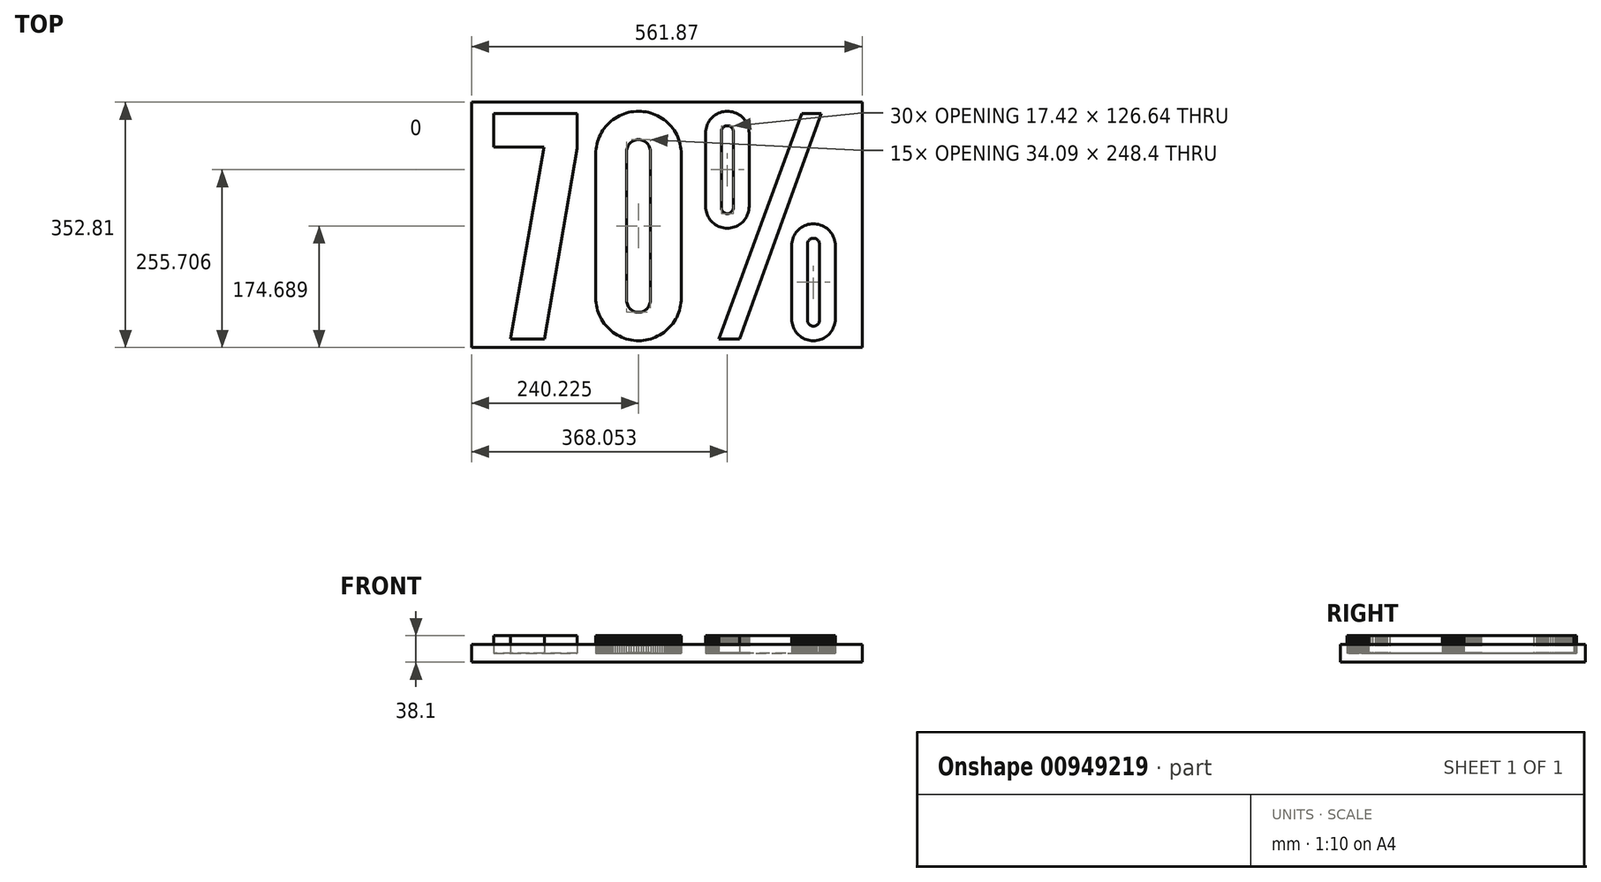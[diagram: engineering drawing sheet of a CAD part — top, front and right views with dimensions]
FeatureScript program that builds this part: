
annotation { "Feature Type Name" : "Feature", "Feature Type Description" : "" }
export const myFeature = defineFeature(function(context is Context, id is Id, definition is map)
    precondition{}
    {
        {
            var Q0;
            Q0=qCreatedBy(makeId("Top.planeOp"),FACE);
            var sketch = newSketch(context, id + "F0", { "sketchPlane" : qUnion([Q0])});
            skLineSegment(sketch, "E0", {"start": v(-116.2, -328.45) * mm, "end": v(-116.2, -376.5) * mm});
            skLineSegment(sketch, "E1", {"start": v(-116.2, -376.5) * mm, "end": v(-116.2, -377.7) * mm});
            skLineSegment(sketch, "E2", {"start": v(-116.2, -377.7) * mm, "end": v(-115.97, -378.89) * mm});
            skLineSegment(sketch, "E3", {"start": v(-115.97, -378.89) * mm, "end": v(-115.65, -379.97) * mm});
            skLineSegment(sketch, "E4", {"start": v(-115.65, -379.97) * mm, "end": v(-115.22, -381.05) * mm});
            skLineSegment(sketch, "E5", {"start": v(-115.22, -381.05) * mm, "end": v(-114.78, -382.02) * mm});
            skLineSegment(sketch, "E6", {"start": v(-114.78, -382.02) * mm, "end": v(-114.14, -383) * mm});
            skLineSegment(sketch, "E7", {"start": v(-114.14, -383) * mm, "end": v(-113.38, -383.86) * mm});
            skLineSegment(sketch, "E8", {"start": v(-113.38, -383.86) * mm, "end": v(-112.62, -384.73) * mm});
            skLineSegment(sketch, "E9", {"start": v(-112.62, -384.73) * mm, "end": v(-111.65, -385.49) * mm});
            skLineSegment(sketch, "E10", {"start": v(-111.65, -385.49) * mm, "end": v(-110.78, -386.03) * mm});
            skLineSegment(sketch, "E11", {"start": v(-110.78, -386.03) * mm, "end": v(-109.7, -386.57) * mm});
            skLineSegment(sketch, "E12", {"start": v(-109.7, -386.57) * mm, "end": v(-108.61, -387) * mm});
            skLineSegment(sketch, "E13", {"start": v(-108.61, -387) * mm, "end": v(-107.53, -387.33) * mm});
            skLineSegment(sketch, "E14", {"start": v(-107.53, -387.33) * mm, "end": v(-106.34, -387.44) * mm});
            skLineSegment(sketch, "E15", {"start": v(-106.34, -387.44) * mm, "end": v(-105.26, -387.54) * mm});
            skLineSegment(sketch, "E16", {"start": v(-105.26, -387.54) * mm, "end": v(-104.07, -387.44) * mm});
            skLineSegment(sketch, "E17", {"start": v(-104.07, -387.44) * mm, "end": v(-102.99, -387.33) * mm});
            skLineSegment(sketch, "E18", {"start": v(-102.99, -387.33) * mm, "end": v(-101.8, -387) * mm});
            skLineSegment(sketch, "E19", {"start": v(-101.8, -387) * mm, "end": v(-100.82, -386.57) * mm});
            skLineSegment(sketch, "E20", {"start": v(-100.82, -386.57) * mm, "end": v(-99.74, -386.03) * mm});
            skLineSegment(sketch, "E21", {"start": v(-99.74, -386.03) * mm, "end": v(-98.76, -385.49) * mm});
            skLineSegment(sketch, "E22", {"start": v(-98.76, -385.49) * mm, "end": v(-97.9, -384.73) * mm});
            skLineSegment(sketch, "E23", {"start": v(-97.9, -384.73) * mm, "end": v(-97.03, -383.86) * mm});
            skLineSegment(sketch, "E24", {"start": v(-97.03, -383.86) * mm, "end": v(-96.38, -383) * mm});
            skLineSegment(sketch, "E25", {"start": v(-96.38, -383) * mm, "end": v(-95.73, -382.02) * mm});
            skLineSegment(sketch, "E26", {"start": v(-95.73, -382.02) * mm, "end": v(-95.2, -381.05) * mm});
            skLineSegment(sketch, "E27", {"start": v(-95.2, -381.05) * mm, "end": v(-94.76, -379.97) * mm});
            skLineSegment(sketch, "E28", {"start": v(-94.76, -379.97) * mm, "end": v(-94.54, -378.89) * mm});
            skLineSegment(sketch, "E29", {"start": v(-94.54, -378.89) * mm, "end": v(-94.33, -377.7) * mm});
            skLineSegment(sketch, "E30", {"start": v(-94.33, -377.7) * mm, "end": v(-94.22, -376.5) * mm});
            skLineSegment(sketch, "E31", {"start": v(-94.22, -376.5) * mm, "end": v(-94.22, -328.45) * mm});
            skLineSegment(sketch, "E32", {"start": v(-94.22, -328.45) * mm, "end": v(-102.23, -328.45) * mm});
            skLineSegment(sketch, "E33", {"start": v(-102.23, -328.45) * mm, "end": v(-102.23, -377.15) * mm});
            skLineSegment(sketch, "E34", {"start": v(-108.3, -377.15) * mm, "end": v(-108.18, -377.8) * mm});
            skLineSegment(sketch, "E35", {"start": v(-108.18, -377.8) * mm, "end": v(-108.08, -378.34) * mm});
            skLineSegment(sketch, "E36", {"start": v(-108.08, -378.34) * mm, "end": v(-107.75, -378.89) * mm});
            skLineSegment(sketch, "E37", {"start": v(-107.75, -378.89) * mm, "end": v(-107.43, -379.32) * mm});
            skLineSegment(sketch, "E38", {"start": v(-107.43, -379.32) * mm, "end": v(-106.88, -379.75) * mm});
            skLineSegment(sketch, "E39", {"start": v(-106.88, -379.75) * mm, "end": v(-106.45, -379.97) * mm});
            skLineSegment(sketch, "E40", {"start": v(-106.45, -379.97) * mm, "end": v(-105.8, -380.18) * mm});
            skLineSegment(sketch, "E41", {"start": v(-105.8, -380.18) * mm, "end": v(-104.61, -380.18) * mm});
            skLineSegment(sketch, "E42", {"start": v(-104.61, -380.18) * mm, "end": v(-104.07, -379.97) * mm});
            skLineSegment(sketch, "E43", {"start": v(-104.07, -379.97) * mm, "end": v(-103.53, -379.75) * mm});
            skLineSegment(sketch, "E44", {"start": v(-103.53, -379.75) * mm, "end": v(-103.1, -379.32) * mm});
            skLineSegment(sketch, "E45", {"start": v(-103.1, -379.32) * mm, "end": v(-102.66, -378.89) * mm});
            skLineSegment(sketch, "E46", {"start": v(-102.66, -378.89) * mm, "end": v(-102.23, -377.8) * mm});
            skLineSegment(sketch, "E47", {"start": v(-102.23, -377.8) * mm, "end": v(-102.23, -377.15) * mm});
            skLineSegment(sketch, "E48", {"start": v(-108.3, -377.15) * mm, "end": v(-108.3, -328.45) * mm});
            skLineSegment(sketch, "E49", {"start": v(-108.3, -328.45) * mm, "end": v(-116.2, -328.45) * mm});
            skLineSegment(sketch, "E50", {"start": v(9.9, -341.44) * mm, "end": v(9.9, -375.1) * mm});
            skLineSegment(sketch, "E51", {"start": v(3.95, -380.3) * mm, "end": v(4.82, -380.18) * mm});
            skLineSegment(sketch, "E52", {"start": v(4.82, -380.18) * mm, "end": v(5.8, -379.97) * mm});
            skLineSegment(sketch, "E53", {"start": v(5.8, -379.97) * mm, "end": v(6.66, -379.54) * mm});
            skLineSegment(sketch, "E54", {"start": v(6.66, -379.54) * mm, "end": v(7.42, -379) * mm});
            skLineSegment(sketch, "E55", {"start": v(7.42, -379) * mm, "end": v(8.17, -378.45) * mm});
            skLineSegment(sketch, "E56", {"start": v(8.17, -378.45) * mm, "end": v(8.82, -377.7) * mm});
            skLineSegment(sketch, "E57", {"start": v(8.82, -377.7) * mm, "end": v(9.25, -376.94) * mm});
            skLineSegment(sketch, "E58", {"start": v(9.25, -376.94) * mm, "end": v(9.69, -376.07) * mm});
            skLineSegment(sketch, "E59", {"start": v(9.69, -376.07) * mm, "end": v(9.9, -375.1) * mm});
            skLineSegment(sketch, "E60", {"start": v(3.95, -380.3) * mm, "end": v(3.2, -380.3) * mm});
            skLineSegment(sketch, "E61", {"start": v(3.2, -380.3) * mm, "end": v(3.2, -336.24) * mm});
            skLineSegment(sketch, "E62", {"start": v(3.2, -336.24) * mm, "end": v(3.95, -336.24) * mm});
            skLineSegment(sketch, "E63", {"start": v(9.9, -341.44) * mm, "end": v(9.69, -340.46) * mm});
            skLineSegment(sketch, "E64", {"start": v(9.69, -340.46) * mm, "end": v(9.25, -339.6) * mm});
            skLineSegment(sketch, "E65", {"start": v(9.25, -339.6) * mm, "end": v(8.82, -338.84) * mm});
            skLineSegment(sketch, "E66", {"start": v(8.82, -338.84) * mm, "end": v(8.17, -338.08) * mm});
            skLineSegment(sketch, "E67", {"start": v(8.17, -338.08) * mm, "end": v(7.42, -337.43) * mm});
            skLineSegment(sketch, "E68", {"start": v(7.42, -337.43) * mm, "end": v(6.66, -337) * mm});
            skLineSegment(sketch, "E69", {"start": v(6.66, -337) * mm, "end": v(5.8, -336.56) * mm});
            skLineSegment(sketch, "E70", {"start": v(5.8, -336.56) * mm, "end": v(4.82, -336.35) * mm});
            skLineSegment(sketch, "E71", {"start": v(4.82, -336.35) * mm, "end": v(3.95, -336.24) * mm});
            skLineSegment(sketch, "E72", {"start": v(-5.36, -328.45) * mm, "end": v(-5.36, -387.98) * mm});
            skLineSegment(sketch, "E73", {"start": v(-5.36, -387.98) * mm, "end": v(8.6, -387.98) * mm});
            skLineSegment(sketch, "E74", {"start": v(8.6, -387.98) * mm, "end": v(9.9, -387.44) * mm});
            skLineSegment(sketch, "E75", {"start": v(9.9, -387.44) * mm, "end": v(11.2, -386.79) * mm});
            skLineSegment(sketch, "E76", {"start": v(11.2, -386.79) * mm, "end": v(12.4, -386.03) * mm});
            skLineSegment(sketch, "E77", {"start": v(12.4, -386.03) * mm, "end": v(13.48, -385.16) * mm});
            skLineSegment(sketch, "E78", {"start": v(13.48, -385.16) * mm, "end": v(14.45, -384.19) * mm});
            skLineSegment(sketch, "E79", {"start": v(14.45, -384.19) * mm, "end": v(15.42, -383.1) * mm});
            skLineSegment(sketch, "E80", {"start": v(15.42, -383.1) * mm, "end": v(16.3, -382.02) * mm});
            skLineSegment(sketch, "E81", {"start": v(16.3, -382.02) * mm, "end": v(16.94, -380.73) * mm});
            skLineSegment(sketch, "E82", {"start": v(16.94, -380.73) * mm, "end": v(17.59, -379.54) * mm});
            skLineSegment(sketch, "E83", {"start": v(17.59, -379.54) * mm, "end": v(18.13, -378.13) * mm});
            skLineSegment(sketch, "E84", {"start": v(18.13, -378.13) * mm, "end": v(18.46, -376.83) * mm});
            skLineSegment(sketch, "E85", {"start": v(18.46, -376.83) * mm, "end": v(18.46, -339.7) * mm});
            skLineSegment(sketch, "E86", {"start": v(18.46, -339.7) * mm, "end": v(18.13, -338.3) * mm});
            skLineSegment(sketch, "E87", {"start": v(18.13, -338.3) * mm, "end": v(17.59, -337) * mm});
            skLineSegment(sketch, "E88", {"start": v(17.59, -337) * mm, "end": v(16.94, -335.7) * mm});
            skLineSegment(sketch, "E89", {"start": v(16.94, -335.7) * mm, "end": v(16.3, -334.5) * mm});
            skLineSegment(sketch, "E90", {"start": v(16.3, -334.5) * mm, "end": v(15.42, -333.43) * mm});
            skLineSegment(sketch, "E91", {"start": v(15.42, -333.43) * mm, "end": v(14.45, -332.34) * mm});
            skLineSegment(sketch, "E92", {"start": v(14.45, -332.34) * mm, "end": v(13.48, -331.37) * mm});
            skLineSegment(sketch, "E93", {"start": v(13.48, -331.37) * mm, "end": v(12.4, -330.5) * mm});
            skLineSegment(sketch, "E94", {"start": v(12.4, -330.5) * mm, "end": v(11.2, -329.75) * mm});
            skLineSegment(sketch, "E95", {"start": v(11.2, -329.75) * mm, "end": v(9.9, -329.1) * mm});
            skLineSegment(sketch, "E96", {"start": v(9.9, -329.1) * mm, "end": v(8.6, -328.45) * mm});
            skLineSegment(sketch, "E97", {"start": v(8.6, -328.45) * mm, "end": v(-5.36, -328.45) * mm});
            skLineSegment(sketch, "E98", {"start": v(-135.57, -338.84) * mm, "end": v(-135.57, -377.15) * mm});
            skLineSegment(sketch, "E99", {"start": v(-141.63, -377.15) * mm, "end": v(-141.63, -377.8) * mm});
            skLineSegment(sketch, "E100", {"start": v(-141.63, -377.8) * mm, "end": v(-141.41, -378.34) * mm});
            skLineSegment(sketch, "E101", {"start": v(-141.41, -378.34) * mm, "end": v(-141.09, -378.89) * mm});
            skLineSegment(sketch, "E102", {"start": v(-141.09, -378.89) * mm, "end": v(-140.76, -379.32) * mm});
            skLineSegment(sketch, "E103", {"start": v(-140.76, -379.32) * mm, "end": v(-140.33, -379.75) * mm});
            skLineSegment(sketch, "E104", {"start": v(-140.33, -379.75) * mm, "end": v(-139.79, -379.97) * mm});
            skLineSegment(sketch, "E105", {"start": v(-139.79, -379.97) * mm, "end": v(-139.14, -380.18) * mm});
            skLineSegment(sketch, "E106", {"start": v(-139.14, -380.18) * mm, "end": v(-137.95, -380.18) * mm});
            skLineSegment(sketch, "E107", {"start": v(-137.95, -380.18) * mm, "end": v(-136.86, -379.75) * mm});
            skLineSegment(sketch, "E108", {"start": v(-136.86, -379.75) * mm, "end": v(-136, -378.89) * mm});
            skLineSegment(sketch, "E109", {"start": v(-136, -378.89) * mm, "end": v(-135.57, -377.8) * mm});
            skLineSegment(sketch, "E110", {"start": v(-135.57, -377.8) * mm, "end": v(-135.57, -377.15) * mm});
            skLineSegment(sketch, "E111", {"start": v(-141.63, -377.15) * mm, "end": v(-141.63, -338.84) * mm});
            skLineSegment(sketch, "E112", {"start": v(-135.57, -338.84) * mm, "end": v(-135.57, -338.3) * mm});
            skLineSegment(sketch, "E113", {"start": v(-135.57, -338.3) * mm, "end": v(-135.78, -337.65) * mm});
            skLineSegment(sketch, "E114", {"start": v(-135.78, -337.65) * mm, "end": v(-136, -337.21) * mm});
            skLineSegment(sketch, "E115", {"start": v(-136, -337.21) * mm, "end": v(-136.43, -336.67) * mm});
            skLineSegment(sketch, "E116", {"start": v(-136.43, -336.67) * mm, "end": v(-136.86, -336.35) * mm});
            skLineSegment(sketch, "E117", {"start": v(-136.86, -336.35) * mm, "end": v(-137.4, -336.02) * mm});
            skLineSegment(sketch, "E118", {"start": v(-137.4, -336.02) * mm, "end": v(-137.95, -335.91) * mm});
            skLineSegment(sketch, "E119", {"start": v(-137.95, -335.91) * mm, "end": v(-138.6, -335.8) * mm});
            skLineSegment(sketch, "E120", {"start": v(-138.6, -335.8) * mm, "end": v(-139.14, -335.91) * mm});
            skLineSegment(sketch, "E121", {"start": v(-139.14, -335.91) * mm, "end": v(-139.79, -336.02) * mm});
            skLineSegment(sketch, "E122", {"start": v(-139.79, -336.02) * mm, "end": v(-140.33, -336.35) * mm});
            skLineSegment(sketch, "E123", {"start": v(-140.33, -336.35) * mm, "end": v(-140.76, -336.67) * mm});
            skLineSegment(sketch, "E124", {"start": v(-140.76, -336.67) * mm, "end": v(-141.09, -337.21) * mm});
            skLineSegment(sketch, "E125", {"start": v(-141.09, -337.21) * mm, "end": v(-141.41, -337.65) * mm});
            skLineSegment(sketch, "E126", {"start": v(-141.41, -337.65) * mm, "end": v(-141.63, -338.3) * mm});
            skLineSegment(sketch, "E127", {"start": v(-141.63, -338.3) * mm, "end": v(-141.63, -338.84) * mm});
            skLineSegment(sketch, "E128", {"start": v(-149.53, -376.5) * mm, "end": v(-149.53, -339.49) * mm});
            skLineSegment(sketch, "E129", {"start": v(-127.55, -339.49) * mm, "end": v(-127.66, -338.3) * mm});
            skLineSegment(sketch, "E130", {"start": v(-127.66, -338.3) * mm, "end": v(-128.1, -336.13) * mm});
            skLineSegment(sketch, "E131", {"start": v(-128.1, -336.13) * mm, "end": v(-128.53, -335.05) * mm});
            skLineSegment(sketch, "E132", {"start": v(-128.53, -335.05) * mm, "end": v(-129.07, -333.97) * mm});
            skLineSegment(sketch, "E133", {"start": v(-129.07, -333.97) * mm, "end": v(-129.72, -333) * mm});
            skLineSegment(sketch, "E134", {"start": v(-129.72, -333) * mm, "end": v(-130.48, -332.13) * mm});
            skLineSegment(sketch, "E135", {"start": v(-130.48, -332.13) * mm, "end": v(-131.24, -331.37) * mm});
            skLineSegment(sketch, "E136", {"start": v(-131.24, -331.37) * mm, "end": v(-132.1, -330.61) * mm});
            skLineSegment(sketch, "E137", {"start": v(-132.1, -330.61) * mm, "end": v(-133.08, -329.96) * mm});
            skLineSegment(sketch, "E138", {"start": v(-133.08, -329.96) * mm, "end": v(-134.16, -329.42) * mm});
            skLineSegment(sketch, "E139", {"start": v(-134.16, -329.42) * mm, "end": v(-135.24, -328.99) * mm});
            skLineSegment(sketch, "E140", {"start": v(-135.24, -328.99) * mm, "end": v(-136.33, -328.77) * mm});
            skLineSegment(sketch, "E141", {"start": v(-136.33, -328.77) * mm, "end": v(-137.4, -328.56) * mm});
            skLineSegment(sketch, "E142", {"start": v(-137.4, -328.56) * mm, "end": v(-138.6, -328.45) * mm});
            skLineSegment(sketch, "E143", {"start": v(-138.6, -328.45) * mm, "end": v(-139.79, -328.56) * mm});
            skLineSegment(sketch, "E144", {"start": v(-139.79, -328.56) * mm, "end": v(-140.87, -328.77) * mm});
            skLineSegment(sketch, "E145", {"start": v(-140.87, -328.77) * mm, "end": v(-141.95, -328.99) * mm});
            skLineSegment(sketch, "E146", {"start": v(-141.95, -328.99) * mm, "end": v(-143.03, -329.42) * mm});
            skLineSegment(sketch, "E147", {"start": v(-143.03, -329.42) * mm, "end": v(-144.12, -329.96) * mm});
            skLineSegment(sketch, "E148", {"start": v(-144.12, -329.96) * mm, "end": v(-145.1, -330.61) * mm});
            skLineSegment(sketch, "E149", {"start": v(-145.1, -330.61) * mm, "end": v(-145.96, -331.37) * mm});
            skLineSegment(sketch, "E150", {"start": v(-145.96, -331.37) * mm, "end": v(-146.71, -332.13) * mm});
            skLineSegment(sketch, "E151", {"start": v(-146.71, -332.13) * mm, "end": v(-147.47, -333) * mm});
            skLineSegment(sketch, "E152", {"start": v(-147.47, -333) * mm, "end": v(-148.12, -333.97) * mm});
            skLineSegment(sketch, "E153", {"start": v(-148.12, -333.97) * mm, "end": v(-148.66, -335.05) * mm});
            skLineSegment(sketch, "E154", {"start": v(-148.66, -335.05) * mm, "end": v(-148.99, -336.13) * mm});
            skLineSegment(sketch, "E155", {"start": v(-148.99, -336.13) * mm, "end": v(-149.31, -337.21) * mm});
            skLineSegment(sketch, "E156", {"start": v(-149.31, -337.21) * mm, "end": v(-149.53, -338.3) * mm});
            skLineSegment(sketch, "E157", {"start": v(-149.53, -338.3) * mm, "end": v(-149.53, -339.49) * mm});
            skLineSegment(sketch, "E158", {"start": v(-127.55, -339.49) * mm, "end": v(-127.55, -376.5) * mm});
            skLineSegment(sketch, "E159", {"start": v(-129.29, -382.35) * mm, "end": v(-128.64, -381.27) * mm});
            skLineSegment(sketch, "E160", {"start": v(-128.64, -381.27) * mm, "end": v(-128.2, -380.08) * mm});
            skLineSegment(sketch, "E161", {"start": v(-128.2, -380.08) * mm, "end": v(-127.88, -379) * mm});
            skLineSegment(sketch, "E162", {"start": v(-127.88, -379) * mm, "end": v(-127.66, -377.8) * mm});
            skLineSegment(sketch, "E163", {"start": v(-127.66, -377.8) * mm, "end": v(-127.55, -376.5) * mm});
            skLineSegment(sketch, "E164", {"start": v(-129.29, -382.35) * mm, "end": v(-128.2, -383.43) * mm});
            skLineSegment(sketch, "E165", {"start": v(-128.2, -383.43) * mm, "end": v(-127.55, -383.97) * mm});
            skLineSegment(sketch, "E166", {"start": v(-127.55, -383.97) * mm, "end": v(-126.8, -384.3) * mm});
            skLineSegment(sketch, "E167", {"start": v(-126.8, -384.3) * mm, "end": v(-126.04, -384.51) * mm});
            skLineSegment(sketch, "E168", {"start": v(-126.04, -384.51) * mm, "end": v(-126.04, -391.55) * mm});
            skLineSegment(sketch, "E169", {"start": v(-134.05, -386.57) * mm, "end": v(-133.4, -387.44) * mm});
            skLineSegment(sketch, "E170", {"start": v(-133.4, -387.44) * mm, "end": v(-132.75, -388.3) * mm});
            skLineSegment(sketch, "E171", {"start": v(-132.75, -388.3) * mm, "end": v(-131.89, -389.06) * mm});
            skLineSegment(sketch, "E172", {"start": v(-131.89, -389.06) * mm, "end": v(-131.13, -389.7) * mm});
            skLineSegment(sketch, "E173", {"start": v(-131.13, -389.7) * mm, "end": v(-130.16, -390.25) * mm});
            skLineSegment(sketch, "E174", {"start": v(-130.16, -390.25) * mm, "end": v(-129.18, -390.8) * mm});
            skLineSegment(sketch, "E175", {"start": v(-129.18, -390.8) * mm, "end": v(-128.2, -391.12) * mm});
            skLineSegment(sketch, "E176", {"start": v(-128.2, -391.12) * mm, "end": v(-127.12, -391.33) * mm});
            skLineSegment(sketch, "E177", {"start": v(-127.12, -391.33) * mm, "end": v(-126.04, -391.55) * mm});
            skLineSegment(sketch, "E178", {"start": v(-149.53, -376.5) * mm, "end": v(-149.53, -377.7) * mm});
            skLineSegment(sketch, "E179", {"start": v(-149.53, -377.7) * mm, "end": v(-149.31, -378.89) * mm});
            skLineSegment(sketch, "E180", {"start": v(-149.31, -378.89) * mm, "end": v(-148.99, -379.97) * mm});
            skLineSegment(sketch, "E181", {"start": v(-148.99, -379.97) * mm, "end": v(-148.66, -381.05) * mm});
            skLineSegment(sketch, "E182", {"start": v(-148.66, -381.05) * mm, "end": v(-148.12, -382.02) * mm});
            skLineSegment(sketch, "E183", {"start": v(-148.12, -382.02) * mm, "end": v(-147.47, -383) * mm});
            skLineSegment(sketch, "E184", {"start": v(-147.47, -383) * mm, "end": v(-146.71, -383.97) * mm});
            skLineSegment(sketch, "E185", {"start": v(-146.71, -383.97) * mm, "end": v(-145.85, -384.73) * mm});
            skLineSegment(sketch, "E186", {"start": v(-145.85, -384.73) * mm, "end": v(-144.98, -385.49) * mm});
            skLineSegment(sketch, "E187", {"start": v(-144.98, -385.49) * mm, "end": v(-144, -386.14) * mm});
            skLineSegment(sketch, "E188", {"start": v(-144, -386.14) * mm, "end": v(-143.03, -386.57) * mm});
            skLineSegment(sketch, "E189", {"start": v(-143.03, -386.57) * mm, "end": v(-141.95, -387) * mm});
            skLineSegment(sketch, "E190", {"start": v(-141.95, -387) * mm, "end": v(-140.76, -387.33) * mm});
            skLineSegment(sketch, "E191", {"start": v(-140.76, -387.33) * mm, "end": v(-139.68, -387.44) * mm});
            skLineSegment(sketch, "E192", {"start": v(-139.68, -387.44) * mm, "end": v(-138.49, -387.54) * mm});
            skLineSegment(sketch, "E193", {"start": v(-138.49, -387.54) * mm, "end": v(-137.3, -387.44) * mm});
            skLineSegment(sketch, "E194", {"start": v(-137.3, -387.44) * mm, "end": v(-136.22, -387.33) * mm});
            skLineSegment(sketch, "E195", {"start": v(-136.22, -387.33) * mm, "end": v(-135.13, -387) * mm});
            skLineSegment(sketch, "E196", {"start": v(-135.13, -387) * mm, "end": v(-134.05, -386.57) * mm});
            skLineSegment(sketch, "E197", {"start": v(-167.06, -338.84) * mm, "end": v(-167.06, -343.7) * mm});
            skLineSegment(sketch, "E198", {"start": v(-167.06, -343.7) * mm, "end": v(-159.16, -343.7) * mm});
            skLineSegment(sketch, "E199", {"start": v(-159.16, -343.7) * mm, "end": v(-159.16, -339.49) * mm});
            skLineSegment(sketch, "E200", {"start": v(-159.16, -339.49) * mm, "end": v(-159.16, -338.3) * mm});
            skLineSegment(sketch, "E201", {"start": v(-159.16, -338.3) * mm, "end": v(-159.38, -337.21) * mm});
            skLineSegment(sketch, "E202", {"start": v(-159.38, -337.21) * mm, "end": v(-159.7, -336.13) * mm});
            skLineSegment(sketch, "E203", {"start": v(-159.7, -336.13) * mm, "end": v(-160.03, -335.05) * mm});
            skLineSegment(sketch, "E204", {"start": v(-160.03, -335.05) * mm, "end": v(-160.57, -333.97) * mm});
            skLineSegment(sketch, "E205", {"start": v(-160.57, -333.97) * mm, "end": v(-161.22, -333) * mm});
            skLineSegment(sketch, "E206", {"start": v(-161.22, -333) * mm, "end": v(-161.97, -332.13) * mm});
            skLineSegment(sketch, "E207", {"start": v(-161.97, -332.13) * mm, "end": v(-162.73, -331.37) * mm});
            skLineSegment(sketch, "E208", {"start": v(-162.73, -331.37) * mm, "end": v(-163.7, -330.61) * mm});
            skLineSegment(sketch, "E209", {"start": v(-163.7, -330.61) * mm, "end": v(-164.58, -329.96) * mm});
            skLineSegment(sketch, "E210", {"start": v(-164.58, -329.96) * mm, "end": v(-165.65, -329.42) * mm});
            skLineSegment(sketch, "E211", {"start": v(-165.65, -329.42) * mm, "end": v(-166.74, -328.99) * mm});
            skLineSegment(sketch, "E212", {"start": v(-166.74, -328.99) * mm, "end": v(-167.82, -328.77) * mm});
            skLineSegment(sketch, "E213", {"start": v(-167.82, -328.77) * mm, "end": v(-169.01, -328.56) * mm});
            skLineSegment(sketch, "E214", {"start": v(-169.01, -328.56) * mm, "end": v(-170.1, -328.45) * mm});
            skLineSegment(sketch, "E215", {"start": v(-170.1, -328.45) * mm, "end": v(-171.28, -328.56) * mm});
            skLineSegment(sketch, "E216", {"start": v(-171.28, -328.56) * mm, "end": v(-172.37, -328.77) * mm});
            skLineSegment(sketch, "E217", {"start": v(-172.37, -328.77) * mm, "end": v(-173.45, -328.99) * mm});
            skLineSegment(sketch, "E218", {"start": v(-173.45, -328.99) * mm, "end": v(-174.53, -329.42) * mm});
            skLineSegment(sketch, "E219", {"start": v(-174.53, -329.42) * mm, "end": v(-175.61, -329.96) * mm});
            skLineSegment(sketch, "E220", {"start": v(-175.61, -329.96) * mm, "end": v(-176.59, -330.61) * mm});
            skLineSegment(sketch, "E221", {"start": v(-176.59, -330.61) * mm, "end": v(-177.46, -331.37) * mm});
            skLineSegment(sketch, "E222", {"start": v(-177.46, -331.37) * mm, "end": v(-178.32, -332.13) * mm});
            skLineSegment(sketch, "E223", {"start": v(-178.32, -332.13) * mm, "end": v(-178.97, -333) * mm});
            skLineSegment(sketch, "E224", {"start": v(-178.97, -333) * mm, "end": v(-179.62, -333.97) * mm});
            skLineSegment(sketch, "E225", {"start": v(-179.62, -333.97) * mm, "end": v(-180.16, -335.05) * mm});
            skLineSegment(sketch, "E226", {"start": v(-180.16, -335.05) * mm, "end": v(-180.6, -336.13) * mm});
            skLineSegment(sketch, "E227", {"start": v(-180.6, -336.13) * mm, "end": v(-180.8, -337.21) * mm});
            skLineSegment(sketch, "E228", {"start": v(-180.8, -337.21) * mm, "end": v(-181.03, -338.3) * mm});
            skLineSegment(sketch, "E229", {"start": v(-181.03, -338.3) * mm, "end": v(-181.13, -339.49) * mm});
            skLineSegment(sketch, "E230", {"start": v(-181.13, -339.49) * mm, "end": v(-181.13, -343.7) * mm});
            skLineSegment(sketch, "E231", {"start": v(-181.13, -343.7) * mm, "end": v(-180.38, -346.09) * mm});
            skLineSegment(sketch, "E232", {"start": v(-180.38, -346.09) * mm, "end": v(-179.51, -348.36) * mm});
            skLineSegment(sketch, "E233", {"start": v(-179.51, -348.36) * mm, "end": v(-178.54, -350.63) * mm});
            skLineSegment(sketch, "E234", {"start": v(-178.54, -350.63) * mm, "end": v(-177.46, -352.8) * mm});
            skLineSegment(sketch, "E235", {"start": v(-177.46, -352.8) * mm, "end": v(-176.26, -354.96) * mm});
            skLineSegment(sketch, "E236", {"start": v(-176.26, -354.96) * mm, "end": v(-174.86, -357.02) * mm});
            skLineSegment(sketch, "E237", {"start": v(-174.86, -357.02) * mm, "end": v(-173.34, -358.97) * mm});
            skLineSegment(sketch, "E238", {"start": v(-166.52, -370.66) * mm, "end": v(-168.69, -366.65) * mm});
            skLineSegment(sketch, "E239", {"start": v(-168.69, -366.65) * mm, "end": v(-170.96, -362.87) * mm});
            skLineSegment(sketch, "E240", {"start": v(-170.96, -362.87) * mm, "end": v(-173.34, -358.97) * mm});
            skLineSegment(sketch, "E241", {"start": v(-166.52, -370.66) * mm, "end": v(-166.52, -376.18) * mm});
            skLineSegment(sketch, "E242", {"start": v(-174.53, -377.15) * mm, "end": v(-174.31, -377.8) * mm});
            skLineSegment(sketch, "E243", {"start": v(-174.31, -377.8) * mm, "end": v(-174, -378.45) * mm});
            skLineSegment(sketch, "E244", {"start": v(-174, -378.45) * mm, "end": v(-173.56, -379) * mm});
            skLineSegment(sketch, "E245", {"start": v(-173.56, -379) * mm, "end": v(-173.02, -379.43) * mm});
            skLineSegment(sketch, "E246", {"start": v(-173.02, -379.43) * mm, "end": v(-172.47, -379.86) * mm});
            skLineSegment(sketch, "E247", {"start": v(-172.47, -379.86) * mm, "end": v(-171.82, -380.08) * mm});
            skLineSegment(sketch, "E248", {"start": v(-171.82, -380.08) * mm, "end": v(-171.07, -380.3) * mm});
            skLineSegment(sketch, "E249", {"start": v(-171.07, -380.3) * mm, "end": v(-170.42, -380.3) * mm});
            skLineSegment(sketch, "E250", {"start": v(-170.42, -380.3) * mm, "end": v(-169.77, -380.18) * mm});
            skLineSegment(sketch, "E251", {"start": v(-169.77, -380.18) * mm, "end": v(-169.01, -379.97) * mm});
            skLineSegment(sketch, "E252", {"start": v(-169.01, -379.97) * mm, "end": v(-168.47, -379.75) * mm});
            skLineSegment(sketch, "E253", {"start": v(-168.47, -379.75) * mm, "end": v(-167.82, -379.32) * mm});
            skLineSegment(sketch, "E254", {"start": v(-167.82, -379.32) * mm, "end": v(-167.39, -378.78) * mm});
            skLineSegment(sketch, "E255", {"start": v(-167.39, -378.78) * mm, "end": v(-166.96, -378.23) * mm});
            skLineSegment(sketch, "E256", {"start": v(-166.96, -378.23) * mm, "end": v(-166.74, -377.59) * mm});
            skLineSegment(sketch, "E257", {"start": v(-166.74, -377.59) * mm, "end": v(-166.52, -376.94) * mm});
            skLineSegment(sketch, "E258", {"start": v(-166.52, -376.94) * mm, "end": v(-166.52, -376.18) * mm});
            skLineSegment(sketch, "E259", {"start": v(-174.53, -377.15) * mm, "end": v(-174.53, -370.66) * mm});
            skLineSegment(sketch, "E260", {"start": v(-174.53, -370.66) * mm, "end": v(-182.32, -370.66) * mm});
            skLineSegment(sketch, "E261", {"start": v(-182.32, -370.66) * mm, "end": v(-182.32, -376.5) * mm});
            skLineSegment(sketch, "E262", {"start": v(-182.32, -376.5) * mm, "end": v(-182.22, -377.8) * mm});
            skLineSegment(sketch, "E263", {"start": v(-182.22, -377.8) * mm, "end": v(-182, -379) * mm});
            skLineSegment(sketch, "E264", {"start": v(-182, -379) * mm, "end": v(-181.57, -380.08) * mm});
            skLineSegment(sketch, "E265", {"start": v(-181.57, -380.08) * mm, "end": v(-181.13, -381.27) * mm});
            skLineSegment(sketch, "E266", {"start": v(-181.13, -381.27) * mm, "end": v(-180.49, -382.24) * mm});
            skLineSegment(sketch, "E267", {"start": v(-180.49, -382.24) * mm, "end": v(-179.73, -383.21) * mm});
            skLineSegment(sketch, "E268", {"start": v(-179.73, -383.21) * mm, "end": v(-178.97, -384.19) * mm});
            skLineSegment(sketch, "E269", {"start": v(-178.97, -384.19) * mm, "end": v(-178.1, -384.95) * mm});
            skLineSegment(sketch, "E270", {"start": v(-178.1, -384.95) * mm, "end": v(-177.02, -385.7) * mm});
            skLineSegment(sketch, "E271", {"start": v(-177.02, -385.7) * mm, "end": v(-176.05, -386.25) * mm});
            skLineSegment(sketch, "E272", {"start": v(-176.05, -386.25) * mm, "end": v(-174.86, -386.79) * mm});
            skLineSegment(sketch, "E273", {"start": v(-174.86, -386.79) * mm, "end": v(-173.78, -387.11) * mm});
            skLineSegment(sketch, "E274", {"start": v(-173.78, -387.11) * mm, "end": v(-172.58, -387.44) * mm});
            skLineSegment(sketch, "E275", {"start": v(-172.58, -387.44) * mm, "end": v(-171.4, -387.54) * mm});
            skLineSegment(sketch, "E276", {"start": v(-171.4, -387.54) * mm, "end": v(-170.1, -387.54) * mm});
            skLineSegment(sketch, "E277", {"start": v(-170.1, -387.54) * mm, "end": v(-168.9, -387.44) * mm});
            skLineSegment(sketch, "E278", {"start": v(-168.9, -387.44) * mm, "end": v(-167.71, -387.11) * mm});
            skLineSegment(sketch, "E279", {"start": v(-167.71, -387.11) * mm, "end": v(-166.63, -386.79) * mm});
            skLineSegment(sketch, "E280", {"start": v(-166.63, -386.79) * mm, "end": v(-165.44, -386.25) * mm});
            skLineSegment(sketch, "E281", {"start": v(-165.44, -386.25) * mm, "end": v(-164.47, -385.7) * mm});
            skLineSegment(sketch, "E282", {"start": v(-164.47, -385.7) * mm, "end": v(-163.38, -384.95) * mm});
            skLineSegment(sketch, "E283", {"start": v(-163.38, -384.95) * mm, "end": v(-162.52, -384.19) * mm});
            skLineSegment(sketch, "E284", {"start": v(-162.52, -384.19) * mm, "end": v(-161.76, -383.21) * mm});
            skLineSegment(sketch, "E285", {"start": v(-161.76, -383.21) * mm, "end": v(-161, -382.24) * mm});
            skLineSegment(sketch, "E286", {"start": v(-161, -382.24) * mm, "end": v(-160.35, -381.27) * mm});
            skLineSegment(sketch, "E287", {"start": v(-160.35, -381.27) * mm, "end": v(-159.92, -380.08) * mm});
            skLineSegment(sketch, "E288", {"start": v(-159.92, -380.08) * mm, "end": v(-159.49, -379) * mm});
            skLineSegment(sketch, "E289", {"start": v(-159.49, -379) * mm, "end": v(-159.27, -377.8) * mm});
            skLineSegment(sketch, "E290", {"start": v(-159.27, -377.8) * mm, "end": v(-159.16, -376.5) * mm});
            skLineSegment(sketch, "E291", {"start": v(-159.16, -376.5) * mm, "end": v(-159.16, -370.66) * mm});
            skLineSegment(sketch, "E292", {"start": v(-159.16, -370.66) * mm, "end": v(-159.81, -368.06) * mm});
            skLineSegment(sketch, "E293", {"start": v(-159.81, -368.06) * mm, "end": v(-160.79, -365.57) * mm});
            skLineSegment(sketch, "E294", {"start": v(-160.79, -365.57) * mm, "end": v(-161.76, -363.2) * mm});
            skLineSegment(sketch, "E295", {"start": v(-161.76, -363.2) * mm, "end": v(-162.84, -360.8) * mm});
            skLineSegment(sketch, "E296", {"start": v(-162.84, -360.8) * mm, "end": v(-164.14, -358.54) * mm});
            skLineSegment(sketch, "E297", {"start": v(-164.14, -358.54) * mm, "end": v(-165.55, -356.37) * mm});
            skLineSegment(sketch, "E298", {"start": v(-165.55, -356.37) * mm, "end": v(-167.06, -354.2) * mm});
            skLineSegment(sketch, "E299", {"start": v(-173.12, -343.7) * mm, "end": v(-172.15, -345.87) * mm});
            skLineSegment(sketch, "E300", {"start": v(-172.15, -345.87) * mm, "end": v(-171.07, -348.04) * mm});
            skLineSegment(sketch, "E301", {"start": v(-171.07, -348.04) * mm, "end": v(-169.77, -350.2) * mm});
            skLineSegment(sketch, "E302", {"start": v(-169.77, -350.2) * mm, "end": v(-168.47, -352.26) * mm});
            skLineSegment(sketch, "E303", {"start": v(-168.47, -352.26) * mm, "end": v(-167.06, -354.2) * mm});
            skLineSegment(sketch, "E304", {"start": v(-173.12, -343.7) * mm, "end": v(-173.12, -338.84) * mm});
            skLineSegment(sketch, "E305", {"start": v(-167.06, -338.84) * mm, "end": v(-167.06, -338.3) * mm});
            skLineSegment(sketch, "E306", {"start": v(-167.06, -338.3) * mm, "end": v(-167.28, -337.65) * mm});
            skLineSegment(sketch, "E307", {"start": v(-167.28, -337.65) * mm, "end": v(-167.6, -337.21) * mm});
            skLineSegment(sketch, "E308", {"start": v(-167.6, -337.21) * mm, "end": v(-167.93, -336.67) * mm});
            skLineSegment(sketch, "E309", {"start": v(-167.93, -336.67) * mm, "end": v(-168.36, -336.35) * mm});
            skLineSegment(sketch, "E310", {"start": v(-168.36, -336.35) * mm, "end": v(-168.9, -336.02) * mm});
            skLineSegment(sketch, "E311", {"start": v(-168.9, -336.02) * mm, "end": v(-169.55, -335.91) * mm});
            skLineSegment(sketch, "E312", {"start": v(-169.55, -335.91) * mm, "end": v(-170.1, -335.8) * mm});
            skLineSegment(sketch, "E313", {"start": v(-170.1, -335.8) * mm, "end": v(-170.74, -335.91) * mm});
            skLineSegment(sketch, "E314", {"start": v(-170.74, -335.91) * mm, "end": v(-171.28, -336.02) * mm});
            skLineSegment(sketch, "E315", {"start": v(-171.28, -336.02) * mm, "end": v(-171.82, -336.35) * mm});
            skLineSegment(sketch, "E316", {"start": v(-171.82, -336.35) * mm, "end": v(-172.26, -336.67) * mm});
            skLineSegment(sketch, "E317", {"start": v(-172.26, -336.67) * mm, "end": v(-172.7, -337.21) * mm});
            skLineSegment(sketch, "E318", {"start": v(-172.7, -337.21) * mm, "end": v(-172.9, -337.65) * mm});
            skLineSegment(sketch, "E319", {"start": v(-172.9, -337.65) * mm, "end": v(-173.12, -338.3) * mm});
            skLineSegment(sketch, "E320", {"start": v(-173.12, -338.3) * mm, "end": v(-173.12, -338.84) * mm});
            skLineSegment(sketch, "E321", {"start": v(-39.34, -338.84) * mm, "end": v(-39.34, -343.7) * mm});
            skLineSegment(sketch, "E322", {"start": v(-39.34, -343.7) * mm, "end": v(-31.44, -343.7) * mm});
            skLineSegment(sketch, "E323", {"start": v(-31.44, -343.7) * mm, "end": v(-31.44, -339.49) * mm});
            skLineSegment(sketch, "E324", {"start": v(-31.44, -339.49) * mm, "end": v(-31.55, -338.3) * mm});
            skLineSegment(sketch, "E325", {"start": v(-31.55, -338.3) * mm, "end": v(-31.66, -337.21) * mm});
            skLineSegment(sketch, "E326", {"start": v(-31.66, -337.21) * mm, "end": v(-31.98, -336.13) * mm});
            skLineSegment(sketch, "E327", {"start": v(-31.98, -336.13) * mm, "end": v(-32.42, -335.05) * mm});
            skLineSegment(sketch, "E328", {"start": v(-32.42, -335.05) * mm, "end": v(-32.96, -333.97) * mm});
            skLineSegment(sketch, "E329", {"start": v(-32.96, -333.97) * mm, "end": v(-33.6, -333) * mm});
            skLineSegment(sketch, "E330", {"start": v(-33.6, -333) * mm, "end": v(-34.26, -332.13) * mm});
            skLineSegment(sketch, "E331", {"start": v(-34.26, -332.13) * mm, "end": v(-35.12, -331.37) * mm});
            skLineSegment(sketch, "E332", {"start": v(-35.12, -331.37) * mm, "end": v(-35.99, -330.61) * mm});
            skLineSegment(sketch, "E333", {"start": v(-35.99, -330.61) * mm, "end": v(-36.96, -329.96) * mm});
            skLineSegment(sketch, "E334", {"start": v(-36.96, -329.96) * mm, "end": v(-37.94, -329.42) * mm});
            skLineSegment(sketch, "E335", {"start": v(-37.94, -329.42) * mm, "end": v(-39.02, -328.99) * mm});
            skLineSegment(sketch, "E336", {"start": v(-39.02, -328.99) * mm, "end": v(-40.2, -328.77) * mm});
            skLineSegment(sketch, "E337", {"start": v(-40.2, -328.77) * mm, "end": v(-41.3, -328.56) * mm});
            skLineSegment(sketch, "E338", {"start": v(-41.3, -328.56) * mm, "end": v(-42.48, -328.45) * mm});
            skLineSegment(sketch, "E339", {"start": v(-42.48, -328.45) * mm, "end": v(-43.56, -328.56) * mm});
            skLineSegment(sketch, "E340", {"start": v(-43.56, -328.56) * mm, "end": v(-44.75, -328.77) * mm});
            skLineSegment(sketch, "E341", {"start": v(-44.75, -328.77) * mm, "end": v(-45.84, -328.99) * mm});
            skLineSegment(sketch, "E342", {"start": v(-45.84, -328.99) * mm, "end": v(-46.92, -329.42) * mm});
            skLineSegment(sketch, "E343", {"start": v(-46.92, -329.42) * mm, "end": v(-47.9, -329.96) * mm});
            skLineSegment(sketch, "E344", {"start": v(-47.9, -329.96) * mm, "end": v(-48.87, -330.61) * mm});
            skLineSegment(sketch, "E345", {"start": v(-48.87, -330.61) * mm, "end": v(-49.84, -331.37) * mm});
            skLineSegment(sketch, "E346", {"start": v(-49.84, -331.37) * mm, "end": v(-50.6, -332.13) * mm});
            skLineSegment(sketch, "E347", {"start": v(-50.6, -332.13) * mm, "end": v(-51.36, -333) * mm});
            skLineSegment(sketch, "E348", {"start": v(-51.36, -333) * mm, "end": v(-52, -333.97) * mm});
            skLineSegment(sketch, "E349", {"start": v(-52, -333.97) * mm, "end": v(-52.44, -335.05) * mm});
            skLineSegment(sketch, "E350", {"start": v(-52.44, -335.05) * mm, "end": v(-52.87, -336.13) * mm});
            skLineSegment(sketch, "E351", {"start": v(-52.87, -336.13) * mm, "end": v(-53.2, -337.21) * mm});
            skLineSegment(sketch, "E352", {"start": v(-53.2, -337.21) * mm, "end": v(-53.41, -338.3) * mm});
            skLineSegment(sketch, "E353", {"start": v(-53.41, -338.3) * mm, "end": v(-53.41, -339.49) * mm});
            skLineSegment(sketch, "E354", {"start": v(-53.41, -339.49) * mm, "end": v(-53.41, -343.7) * mm});
            skLineSegment(sketch, "E355", {"start": v(-53.41, -343.7) * mm, "end": v(-52.77, -346.09) * mm});
            skLineSegment(sketch, "E356", {"start": v(-52.77, -346.09) * mm, "end": v(-51.9, -348.36) * mm});
            skLineSegment(sketch, "E357", {"start": v(-51.9, -348.36) * mm, "end": v(-50.92, -350.63) * mm});
            skLineSegment(sketch, "E358", {"start": v(-50.92, -350.63) * mm, "end": v(-49.84, -352.8) * mm});
            skLineSegment(sketch, "E359", {"start": v(-49.84, -352.8) * mm, "end": v(-48.54, -354.96) * mm});
            skLineSegment(sketch, "E360", {"start": v(-48.54, -354.96) * mm, "end": v(-47.25, -357.02) * mm});
            skLineSegment(sketch, "E361", {"start": v(-47.25, -357.02) * mm, "end": v(-45.73, -358.97) * mm});
            skLineSegment(sketch, "E362", {"start": v(-38.8, -370.66) * mm, "end": v(-40.97, -366.65) * mm});
            skLineSegment(sketch, "E363", {"start": v(-40.97, -366.65) * mm, "end": v(-43.35, -362.87) * mm});
            skLineSegment(sketch, "E364", {"start": v(-43.35, -362.87) * mm, "end": v(-45.73, -358.97) * mm});
            skLineSegment(sketch, "E365", {"start": v(-38.8, -370.66) * mm, "end": v(-38.8, -376.18) * mm});
            skLineSegment(sketch, "E366", {"start": v(-46.81, -377.15) * mm, "end": v(-46.6, -377.8) * mm});
            skLineSegment(sketch, "E367", {"start": v(-46.6, -377.8) * mm, "end": v(-46.27, -378.45) * mm});
            skLineSegment(sketch, "E368", {"start": v(-46.27, -378.45) * mm, "end": v(-45.84, -379) * mm});
            skLineSegment(sketch, "E369", {"start": v(-45.84, -379) * mm, "end": v(-45.4, -379.43) * mm});
            skLineSegment(sketch, "E370", {"start": v(-45.4, -379.43) * mm, "end": v(-44.75, -379.86) * mm});
            skLineSegment(sketch, "E371", {"start": v(-44.75, -379.86) * mm, "end": v(-44.1, -380.08) * mm});
            skLineSegment(sketch, "E372", {"start": v(-44.1, -380.08) * mm, "end": v(-43.46, -380.3) * mm});
            skLineSegment(sketch, "E373", {"start": v(-43.46, -380.3) * mm, "end": v(-42.7, -380.3) * mm});
            skLineSegment(sketch, "E374", {"start": v(-42.7, -380.3) * mm, "end": v(-42.05, -380.18) * mm});
            skLineSegment(sketch, "E375", {"start": v(-42.05, -380.18) * mm, "end": v(-40.75, -379.75) * mm});
            skLineSegment(sketch, "E376", {"start": v(-40.75, -379.75) * mm, "end": v(-40.2, -379.32) * mm});
            skLineSegment(sketch, "E377", {"start": v(-40.2, -379.32) * mm, "end": v(-39.67, -378.78) * mm});
            skLineSegment(sketch, "E378", {"start": v(-39.67, -378.78) * mm, "end": v(-39.34, -378.23) * mm});
            skLineSegment(sketch, "E379", {"start": v(-39.34, -378.23) * mm, "end": v(-39.02, -377.59) * mm});
            skLineSegment(sketch, "E380", {"start": v(-39.02, -377.59) * mm, "end": v(-38.91, -376.94) * mm});
            skLineSegment(sketch, "E381", {"start": v(-38.91, -376.94) * mm, "end": v(-38.8, -376.18) * mm});
            skLineSegment(sketch, "E382", {"start": v(-46.81, -377.15) * mm, "end": v(-46.81, -370.66) * mm});
            skLineSegment(sketch, "E383", {"start": v(-46.81, -370.66) * mm, "end": v(-54.71, -370.66) * mm});
            skLineSegment(sketch, "E384", {"start": v(-54.71, -370.66) * mm, "end": v(-54.71, -376.5) * mm});
            skLineSegment(sketch, "E385", {"start": v(-54.71, -376.5) * mm, "end": v(-54.6, -377.8) * mm});
            skLineSegment(sketch, "E386", {"start": v(-54.6, -377.8) * mm, "end": v(-54.28, -379) * mm});
            skLineSegment(sketch, "E387", {"start": v(-54.28, -379) * mm, "end": v(-53.96, -380.08) * mm});
            skLineSegment(sketch, "E388", {"start": v(-53.96, -380.08) * mm, "end": v(-53.41, -381.27) * mm});
            skLineSegment(sketch, "E389", {"start": v(-53.41, -381.27) * mm, "end": v(-52.87, -382.24) * mm});
            skLineSegment(sketch, "E390", {"start": v(-52.87, -382.24) * mm, "end": v(-52.12, -383.21) * mm});
            skLineSegment(sketch, "E391", {"start": v(-52.12, -383.21) * mm, "end": v(-51.25, -384.19) * mm});
            skLineSegment(sketch, "E392", {"start": v(-51.25, -384.19) * mm, "end": v(-50.38, -384.95) * mm});
            skLineSegment(sketch, "E393", {"start": v(-50.38, -384.95) * mm, "end": v(-49.4, -385.7) * mm});
            skLineSegment(sketch, "E394", {"start": v(-49.4, -385.7) * mm, "end": v(-48.33, -386.25) * mm});
            skLineSegment(sketch, "E395", {"start": v(-48.33, -386.25) * mm, "end": v(-47.25, -386.79) * mm});
            skLineSegment(sketch, "E396", {"start": v(-47.25, -386.79) * mm, "end": v(-44.86, -387.44) * mm});
            skLineSegment(sketch, "E397", {"start": v(-44.86, -387.44) * mm, "end": v(-43.67, -387.54) * mm});
            skLineSegment(sketch, "E398", {"start": v(-43.67, -387.54) * mm, "end": v(-42.48, -387.54) * mm});
            skLineSegment(sketch, "E399", {"start": v(-42.48, -387.54) * mm, "end": v(-41.3, -387.44) * mm});
            skLineSegment(sketch, "E400", {"start": v(-41.3, -387.44) * mm, "end": v(-38.91, -386.79) * mm});
            skLineSegment(sketch, "E401", {"start": v(-38.91, -386.79) * mm, "end": v(-37.83, -386.25) * mm});
            skLineSegment(sketch, "E402", {"start": v(-37.83, -386.25) * mm, "end": v(-36.75, -385.7) * mm});
            skLineSegment(sketch, "E403", {"start": v(-36.75, -385.7) * mm, "end": v(-35.77, -384.95) * mm});
            skLineSegment(sketch, "E404", {"start": v(-35.77, -384.95) * mm, "end": v(-34.9, -384.19) * mm});
            skLineSegment(sketch, "E405", {"start": v(-34.9, -384.19) * mm, "end": v(-34.04, -383.21) * mm});
            skLineSegment(sketch, "E406", {"start": v(-34.04, -383.21) * mm, "end": v(-33.28, -382.24) * mm});
            skLineSegment(sketch, "E407", {"start": v(-33.28, -382.24) * mm, "end": v(-32.74, -381.27) * mm});
            skLineSegment(sketch, "E408", {"start": v(-32.74, -381.27) * mm, "end": v(-32.2, -380.08) * mm});
            skLineSegment(sketch, "E409", {"start": v(-32.2, -380.08) * mm, "end": v(-31.88, -379) * mm});
            skLineSegment(sketch, "E410", {"start": v(-31.88, -379) * mm, "end": v(-31.55, -377.8) * mm});
            skLineSegment(sketch, "E411", {"start": v(-31.55, -377.8) * mm, "end": v(-31.44, -376.5) * mm});
            skLineSegment(sketch, "E412", {"start": v(-31.44, -376.5) * mm, "end": v(-31.44, -370.66) * mm});
            skLineSegment(sketch, "E413", {"start": v(-31.44, -370.66) * mm, "end": v(-32.2, -368.06) * mm});
            skLineSegment(sketch, "E414", {"start": v(-32.2, -368.06) * mm, "end": v(-33.07, -365.57) * mm});
            skLineSegment(sketch, "E415", {"start": v(-33.07, -365.57) * mm, "end": v(-34.04, -363.2) * mm});
            skLineSegment(sketch, "E416", {"start": v(-34.04, -363.2) * mm, "end": v(-35.23, -360.8) * mm});
            skLineSegment(sketch, "E417", {"start": v(-35.23, -360.8) * mm, "end": v(-36.53, -358.54) * mm});
            skLineSegment(sketch, "E418", {"start": v(-36.53, -358.54) * mm, "end": v(-37.83, -356.37) * mm});
            skLineSegment(sketch, "E419", {"start": v(-37.83, -356.37) * mm, "end": v(-39.34, -354.2) * mm});
            skLineSegment(sketch, "E420", {"start": v(-45.51, -343.7) * mm, "end": v(-44.54, -345.87) * mm});
            skLineSegment(sketch, "E421", {"start": v(-44.54, -345.87) * mm, "end": v(-43.35, -348.04) * mm});
            skLineSegment(sketch, "E422", {"start": v(-43.35, -348.04) * mm, "end": v(-42.16, -350.2) * mm});
            skLineSegment(sketch, "E423", {"start": v(-42.16, -350.2) * mm, "end": v(-40.86, -352.26) * mm});
            skLineSegment(sketch, "E424", {"start": v(-40.86, -352.26) * mm, "end": v(-39.34, -354.2) * mm});
            skLineSegment(sketch, "E425", {"start": v(-45.51, -343.7) * mm, "end": v(-45.51, -338.84) * mm});
            skLineSegment(sketch, "E426", {"start": v(-39.34, -338.84) * mm, "end": v(-39.45, -338.3) * mm});
            skLineSegment(sketch, "E427", {"start": v(-39.45, -338.3) * mm, "end": v(-39.67, -337.65) * mm});
            skLineSegment(sketch, "E428", {"start": v(-39.67, -337.65) * mm, "end": v(-39.89, -337.21) * mm});
            skLineSegment(sketch, "E429", {"start": v(-39.89, -337.21) * mm, "end": v(-40.32, -336.67) * mm});
            skLineSegment(sketch, "E430", {"start": v(-40.32, -336.67) * mm, "end": v(-40.75, -336.35) * mm});
            skLineSegment(sketch, "E431", {"start": v(-40.75, -336.35) * mm, "end": v(-41.3, -336.02) * mm});
            skLineSegment(sketch, "E432", {"start": v(-41.3, -336.02) * mm, "end": v(-41.83, -335.91) * mm});
            skLineSegment(sketch, "E433", {"start": v(-41.83, -335.91) * mm, "end": v(-42.48, -335.8) * mm});
            skLineSegment(sketch, "E434", {"start": v(-42.48, -335.8) * mm, "end": v(-43.03, -335.91) * mm});
            skLineSegment(sketch, "E435", {"start": v(-43.03, -335.91) * mm, "end": v(-43.56, -336.02) * mm});
            skLineSegment(sketch, "E436", {"start": v(-43.56, -336.02) * mm, "end": v(-44.1, -336.35) * mm});
            skLineSegment(sketch, "E437", {"start": v(-44.1, -336.35) * mm, "end": v(-44.65, -336.67) * mm});
            skLineSegment(sketch, "E438", {"start": v(-44.65, -336.67) * mm, "end": v(-44.97, -337.21) * mm});
            skLineSegment(sketch, "E439", {"start": v(-44.97, -337.21) * mm, "end": v(-45.3, -337.65) * mm});
            skLineSegment(sketch, "E440", {"start": v(-45.3, -337.65) * mm, "end": v(-45.4, -338.3) * mm});
            skLineSegment(sketch, "E441", {"start": v(-45.4, -338.3) * mm, "end": v(-45.51, -338.84) * mm});
            skLineSegment(sketch, "E442", {"start": v(-234.06, -376.18) * mm, "end": v(-233.52, -374.88) * mm});
            skLineSegment(sketch, "E443", {"start": v(-233.52, -374.88) * mm, "end": v(-233.09, -373.47) * mm});
            skLineSegment(sketch, "E444", {"start": v(-233.09, -373.47) * mm, "end": v(-232.65, -372.07) * mm});
            skLineSegment(sketch, "E445", {"start": v(-232.65, -372.07) * mm, "end": v(-232.55, -370.66) * mm});
            skLineSegment(sketch, "E446", {"start": v(-232.55, -370.66) * mm, "end": v(-232.44, -369.25) * mm});
            skLineSegment(sketch, "E447", {"start": v(-232.44, -369.25) * mm, "end": v(-232.55, -367.84) * mm});
            skLineSegment(sketch, "E448", {"start": v(-232.55, -367.84) * mm, "end": v(-232.65, -366.44) * mm});
            skLineSegment(sketch, "E449", {"start": v(-232.65, -366.44) * mm, "end": v(-233.09, -365.03) * mm});
            skLineSegment(sketch, "E450", {"start": v(-233.09, -365.03) * mm, "end": v(-233.52, -363.73) * mm});
            skLineSegment(sketch, "E451", {"start": v(-233.52, -363.73) * mm, "end": v(-234.06, -362.43) * mm});
            skLineSegment(sketch, "E452", {"start": v(-239.37, -378.34) * mm, "end": v(-238.28, -378.13) * mm});
            skLineSegment(sketch, "E453", {"start": v(-238.28, -378.13) * mm, "end": v(-237.1, -377.91) * mm});
            skLineSegment(sketch, "E454", {"start": v(-237.1, -377.91) * mm, "end": v(-236.01, -377.48) * mm});
            skLineSegment(sketch, "E455", {"start": v(-236.01, -377.48) * mm, "end": v(-235.04, -376.83) * mm});
            skLineSegment(sketch, "E456", {"start": v(-235.04, -376.83) * mm, "end": v(-234.06, -376.18) * mm});
            skLineSegment(sketch, "E457", {"start": v(-239.37, -378.34) * mm, "end": v(-239.37, -360.27) * mm});
            skLineSegment(sketch, "E458", {"start": v(-234.06, -362.43) * mm, "end": v(-235.04, -361.68) * mm});
            skLineSegment(sketch, "E459", {"start": v(-235.04, -361.68) * mm, "end": v(-236.01, -361.13) * mm});
            skLineSegment(sketch, "E460", {"start": v(-236.01, -361.13) * mm, "end": v(-237.1, -360.7) * mm});
            skLineSegment(sketch, "E461", {"start": v(-237.1, -360.7) * mm, "end": v(-238.28, -360.38) * mm});
            skLineSegment(sketch, "E462", {"start": v(-238.28, -360.38) * mm, "end": v(-239.37, -360.27) * mm});
            skLineSegment(sketch, "E463", {"start": v(-234.06, -350.2) * mm, "end": v(-233.52, -349.12) * mm});
            skLineSegment(sketch, "E464", {"start": v(-233.52, -349.12) * mm, "end": v(-232.98, -348.04) * mm});
            skLineSegment(sketch, "E465", {"start": v(-232.98, -348.04) * mm, "end": v(-232.65, -346.85) * mm});
            skLineSegment(sketch, "E466", {"start": v(-232.65, -346.85) * mm, "end": v(-232.44, -345.66) * mm});
            skLineSegment(sketch, "E467", {"start": v(-232.44, -345.66) * mm, "end": v(-232.44, -343.17) * mm});
            skLineSegment(sketch, "E468", {"start": v(-232.44, -343.17) * mm, "end": v(-232.65, -341.98) * mm});
            skLineSegment(sketch, "E469", {"start": v(-232.65, -341.98) * mm, "end": v(-232.98, -340.79) * mm});
            skLineSegment(sketch, "E470", {"start": v(-232.98, -340.79) * mm, "end": v(-233.52, -339.6) * mm});
            skLineSegment(sketch, "E471", {"start": v(-233.52, -339.6) * mm, "end": v(-234.06, -338.62) * mm});
            skLineSegment(sketch, "E472", {"start": v(-239.37, -352.48) * mm, "end": v(-238.6, -352.58) * mm});
            skLineSegment(sketch, "E473", {"start": v(-238.6, -352.58) * mm, "end": v(-237.1, -352.37) * mm});
            skLineSegment(sketch, "E474", {"start": v(-237.1, -352.37) * mm, "end": v(-236.44, -352.15) * mm});
            skLineSegment(sketch, "E475", {"start": v(-236.44, -352.15) * mm, "end": v(-235.69, -351.82) * mm});
            skLineSegment(sketch, "E476", {"start": v(-235.69, -351.82) * mm, "end": v(-235.14, -351.4) * mm});
            skLineSegment(sketch, "E477", {"start": v(-235.14, -351.4) * mm, "end": v(-234.6, -350.85) * mm});
            skLineSegment(sketch, "E478", {"start": v(-234.6, -350.85) * mm, "end": v(-234.06, -350.2) * mm});
            skLineSegment(sketch, "E479", {"start": v(-239.37, -352.48) * mm, "end": v(-239.37, -336.35) * mm});
            skLineSegment(sketch, "E480", {"start": v(-234.06, -338.62) * mm, "end": v(-235.04, -337.86) * mm});
            skLineSegment(sketch, "E481", {"start": v(-235.04, -337.86) * mm, "end": v(-236.01, -337.32) * mm});
            skLineSegment(sketch, "E482", {"start": v(-236.01, -337.32) * mm, "end": v(-237.1, -336.78) * mm});
            skLineSegment(sketch, "E483", {"start": v(-237.1, -336.78) * mm, "end": v(-238.28, -336.56) * mm});
            skLineSegment(sketch, "E484", {"start": v(-238.28, -336.56) * mm, "end": v(-239.37, -336.35) * mm});
            skLineSegment(sketch, "E485", {"start": v(-247.7, -328.45) * mm, "end": v(-247.7, -387.98) * mm});
            skLineSegment(sketch, "E486", {"start": v(-247.7, -387.98) * mm, "end": v(-238.82, -387.98) * mm});
            skLineSegment(sketch, "E487", {"start": v(-238.82, -387.98) * mm, "end": v(-237.53, -387.87) * mm});
            skLineSegment(sketch, "E488", {"start": v(-237.53, -387.87) * mm, "end": v(-236.12, -387.54) * mm});
            skLineSegment(sketch, "E489", {"start": v(-236.12, -387.54) * mm, "end": v(-234.82, -387.11) * mm});
            skLineSegment(sketch, "E490", {"start": v(-234.82, -387.11) * mm, "end": v(-233.52, -386.57) * mm});
            skLineSegment(sketch, "E491", {"start": v(-233.52, -386.57) * mm, "end": v(-232.33, -385.92) * mm});
            skLineSegment(sketch, "E492", {"start": v(-232.33, -385.92) * mm, "end": v(-231.14, -385.16) * mm});
            skLineSegment(sketch, "E493", {"start": v(-231.14, -385.16) * mm, "end": v(-230.06, -384.3) * mm});
            skLineSegment(sketch, "E494", {"start": v(-230.06, -384.3) * mm, "end": v(-229.08, -383.32) * mm});
            skLineSegment(sketch, "E495", {"start": v(-229.08, -383.32) * mm, "end": v(-228.22, -382.24) * mm});
            skLineSegment(sketch, "E496", {"start": v(-228.22, -382.24) * mm, "end": v(-227.46, -381.16) * mm});
            skLineSegment(sketch, "E497", {"start": v(-227.46, -381.16) * mm, "end": v(-226.81, -379.97) * mm});
            skLineSegment(sketch, "E498", {"start": v(-226.81, -379.97) * mm, "end": v(-226.05, -378.34) * mm});
            skLineSegment(sketch, "E499", {"start": v(-226.05, -378.34) * mm, "end": v(-225.4, -376.83) * mm});
            skLineSegment(sketch, "E500", {"start": v(-225.4, -376.83) * mm, "end": v(-224.97, -375.2) * mm});
            skLineSegment(sketch, "E501", {"start": v(-224.97, -375.2) * mm, "end": v(-224.54, -373.47) * mm});
            skLineSegment(sketch, "E502", {"start": v(-224.54, -373.47) * mm, "end": v(-224.32, -371.85) * mm});
            skLineSegment(sketch, "E503", {"start": v(-224.32, -371.85) * mm, "end": v(-224.21, -370.12) * mm});
            skLineSegment(sketch, "E504", {"start": v(-224.21, -370.12) * mm, "end": v(-224.21, -368.39) * mm});
            skLineSegment(sketch, "E505", {"start": v(-224.21, -368.39) * mm, "end": v(-224.32, -366.76) * mm});
            skLineSegment(sketch, "E506", {"start": v(-224.32, -366.76) * mm, "end": v(-224.54, -365.03) * mm});
            skLineSegment(sketch, "E507", {"start": v(-224.54, -365.03) * mm, "end": v(-224.97, -363.4) * mm});
            skLineSegment(sketch, "E508", {"start": v(-224.97, -363.4) * mm, "end": v(-225.4, -361.78) * mm});
            skLineSegment(sketch, "E509", {"start": v(-225.4, -361.78) * mm, "end": v(-226.05, -360.16) * mm});
            skLineSegment(sketch, "E510", {"start": v(-226.05, -360.16) * mm, "end": v(-226.81, -358.64) * mm});
            skLineSegment(sketch, "E511", {"start": v(-226.81, -358.64) * mm, "end": v(-227.68, -357.45) * mm});
            skLineSegment(sketch, "E512", {"start": v(-227.68, -357.45) * mm, "end": v(-228.65, -356.48) * mm});
            skLineSegment(sketch, "E513", {"start": v(-228.65, -356.48) * mm, "end": v(-229.73, -355.5) * mm});
            skLineSegment(sketch, "E514", {"start": v(-229.73, -355.5) * mm, "end": v(-228.65, -354.53) * mm});
            skLineSegment(sketch, "E515", {"start": v(-228.65, -354.53) * mm, "end": v(-227.68, -353.56) * mm});
            skLineSegment(sketch, "E516", {"start": v(-227.68, -353.56) * mm, "end": v(-226.81, -352.37) * mm});
            skLineSegment(sketch, "E517", {"start": v(-226.81, -352.37) * mm, "end": v(-226.05, -351.18) * mm});
            skLineSegment(sketch, "E518", {"start": v(-226.05, -351.18) * mm, "end": v(-225.4, -349.88) * mm});
            skLineSegment(sketch, "E519", {"start": v(-225.4, -349.88) * mm, "end": v(-224.86, -348.47) * mm});
            skLineSegment(sketch, "E520", {"start": v(-224.86, -348.47) * mm, "end": v(-224.54, -347.06) * mm});
            skLineSegment(sketch, "E521", {"start": v(-224.54, -347.06) * mm, "end": v(-224.21, -345.66) * mm});
            skLineSegment(sketch, "E522", {"start": v(-224.21, -345.66) * mm, "end": v(-224.1, -344.25) * mm});
            skLineSegment(sketch, "E523", {"start": v(-224.1, -344.25) * mm, "end": v(-224.1, -342.84) * mm});
            skLineSegment(sketch, "E524", {"start": v(-224.1, -342.84) * mm, "end": v(-224.21, -341.33) * mm});
            skLineSegment(sketch, "E525", {"start": v(-224.21, -341.33) * mm, "end": v(-224.54, -339.92) * mm});
            skLineSegment(sketch, "E526", {"start": v(-224.54, -339.92) * mm, "end": v(-224.86, -338.51) * mm});
            skLineSegment(sketch, "E527", {"start": v(-224.86, -338.51) * mm, "end": v(-225.4, -337.21) * mm});
            skLineSegment(sketch, "E528", {"start": v(-225.4, -337.21) * mm, "end": v(-226.05, -335.91) * mm});
            skLineSegment(sketch, "E529", {"start": v(-226.05, -335.91) * mm, "end": v(-226.81, -334.62) * mm});
            skLineSegment(sketch, "E530", {"start": v(-226.81, -334.62) * mm, "end": v(-227.57, -333.53) * mm});
            skLineSegment(sketch, "E531", {"start": v(-227.57, -333.53) * mm, "end": v(-228.54, -332.45) * mm});
            skLineSegment(sketch, "E532", {"start": v(-228.54, -332.45) * mm, "end": v(-229.62, -331.37) * mm});
            skLineSegment(sketch, "E533", {"start": v(-229.62, -331.37) * mm, "end": v(-230.82, -330.5) * mm});
            skLineSegment(sketch, "E534", {"start": v(-230.82, -330.5) * mm, "end": v(-232, -329.75) * mm});
            skLineSegment(sketch, "E535", {"start": v(-232, -329.75) * mm, "end": v(-233.3, -329.1) * mm});
            skLineSegment(sketch, "E536", {"start": v(-233.3, -329.1) * mm, "end": v(-234.6, -328.45) * mm});
            skLineSegment(sketch, "E537", {"start": v(-234.6, -328.45) * mm, "end": v(-247.7, -328.45) * mm});
            skLineSegment(sketch, "E538", {"start": v(239.48, -378.67) * mm, "end": v(247.7, -378.67) * mm});
            skLineSegment(sketch, "E539", {"start": v(247.7, -378.67) * mm, "end": v(247.7, -387.98) * mm});
            skLineSegment(sketch, "E540", {"start": v(247.7, -387.98) * mm, "end": v(239.48, -387.98) * mm});
            skLineSegment(sketch, "E541", {"start": v(239.48, -387.98) * mm, "end": v(239.48, -378.67) * mm});
            skLineSegment(sketch, "E542", {"start": v(-237.74, -272.7) * mm, "end": v(-237.74, -296.4) * mm});
            skLineSegment(sketch, "E543", {"start": v(-241.96, -300.09) * mm, "end": v(-241.31, -299.98) * mm});
            skLineSegment(sketch, "E544", {"start": v(-241.31, -299.98) * mm, "end": v(-240.56, -299.76) * mm});
            skLineSegment(sketch, "E545", {"start": v(-240.56, -299.76) * mm, "end": v(-239.9, -299.44) * mm});
            skLineSegment(sketch, "E546", {"start": v(-239.9, -299.44) * mm, "end": v(-239.26, -299) * mm});
            skLineSegment(sketch, "E547", {"start": v(-239.26, -299) * mm, "end": v(-238.72, -298.46) * mm});
            skLineSegment(sketch, "E548", {"start": v(-238.72, -298.46) * mm, "end": v(-238.28, -297.81) * mm});
            skLineSegment(sketch, "E549", {"start": v(-238.28, -297.81) * mm, "end": v(-237.96, -297.17) * mm});
            skLineSegment(sketch, "E550", {"start": v(-237.96, -297.17) * mm, "end": v(-237.74, -296.4) * mm});
            skLineSegment(sketch, "E551", {"start": v(-241.96, -300.09) * mm, "end": v(-242.5, -300.09) * mm});
            skLineSegment(sketch, "E552", {"start": v(-242.5, -300.09) * mm, "end": v(-242.5, -269.02) * mm});
            skLineSegment(sketch, "E553", {"start": v(-242.5, -269.02) * mm, "end": v(-241.96, -269.02) * mm});
            skLineSegment(sketch, "E554", {"start": v(-237.74, -272.7) * mm, "end": v(-237.96, -271.95) * mm});
            skLineSegment(sketch, "E555", {"start": v(-237.96, -271.95) * mm, "end": v(-238.28, -271.3) * mm});
            skLineSegment(sketch, "E556", {"start": v(-238.28, -271.3) * mm, "end": v(-238.72, -270.65) * mm});
            skLineSegment(sketch, "E557", {"start": v(-238.72, -270.65) * mm, "end": v(-239.26, -270.1) * mm});
            skLineSegment(sketch, "E558", {"start": v(-239.26, -270.1) * mm, "end": v(-239.9, -269.67) * mm});
            skLineSegment(sketch, "E559", {"start": v(-239.9, -269.67) * mm, "end": v(-240.56, -269.35) * mm});
            skLineSegment(sketch, "E560", {"start": v(-240.56, -269.35) * mm, "end": v(-241.31, -269.13) * mm});
            skLineSegment(sketch, "E561", {"start": v(-241.31, -269.13) * mm, "end": v(-241.96, -269.02) * mm});
            skLineSegment(sketch, "E562", {"start": v(-248.57, -263.61) * mm, "end": v(-248.57, -305.5) * mm});
            skLineSegment(sketch, "E563", {"start": v(-248.57, -305.5) * mm, "end": v(-238.72, -305.5) * mm});
            skLineSegment(sketch, "E564", {"start": v(-238.72, -305.5) * mm, "end": v(-237.53, -305.07) * mm});
            skLineSegment(sketch, "E565", {"start": v(-237.53, -305.07) * mm, "end": v(-236.55, -304.42) * mm});
            skLineSegment(sketch, "E566", {"start": v(-236.55, -304.42) * mm, "end": v(-235.47, -303.77) * mm});
            skLineSegment(sketch, "E567", {"start": v(-235.47, -303.77) * mm, "end": v(-234.6, -302.9) * mm});
            skLineSegment(sketch, "E568", {"start": v(-234.6, -302.9) * mm, "end": v(-233.85, -302.04) * mm});
            skLineSegment(sketch, "E569", {"start": v(-233.85, -302.04) * mm, "end": v(-233.09, -301.06) * mm});
            skLineSegment(sketch, "E570", {"start": v(-233.09, -301.06) * mm, "end": v(-232.55, -299.98) * mm});
            skLineSegment(sketch, "E571", {"start": v(-232.55, -299.98) * mm, "end": v(-232, -298.79) * mm});
            skLineSegment(sketch, "E572", {"start": v(-232, -298.79) * mm, "end": v(-231.68, -297.7) * mm});
            skLineSegment(sketch, "E573", {"start": v(-231.68, -297.7) * mm, "end": v(-231.68, -271.4) * mm});
            skLineSegment(sketch, "E574", {"start": v(-231.68, -271.4) * mm, "end": v(-232, -270.32) * mm});
            skLineSegment(sketch, "E575", {"start": v(-232, -270.32) * mm, "end": v(-232.55, -269.13) * mm});
            skLineSegment(sketch, "E576", {"start": v(-232.55, -269.13) * mm, "end": v(-233.09, -268.05) * mm});
            skLineSegment(sketch, "E577", {"start": v(-233.09, -268.05) * mm, "end": v(-233.85, -267.08) * mm});
            skLineSegment(sketch, "E578", {"start": v(-233.85, -267.08) * mm, "end": v(-234.6, -266.2) * mm});
            skLineSegment(sketch, "E579", {"start": v(-234.6, -266.2) * mm, "end": v(-235.47, -265.34) * mm});
            skLineSegment(sketch, "E580", {"start": v(-235.47, -265.34) * mm, "end": v(-236.55, -264.7) * mm});
            skLineSegment(sketch, "E581", {"start": v(-236.55, -264.7) * mm, "end": v(-237.53, -264.04) * mm});
            skLineSegment(sketch, "E582", {"start": v(-237.53, -264.04) * mm, "end": v(-238.72, -263.61) * mm});
            skLineSegment(sketch, "E583", {"start": v(-238.72, -263.61) * mm, "end": v(-248.57, -263.61) * mm});
            skLineSegment(sketch, "E584", {"start": v(63.16, -272.7) * mm, "end": v(63.16, -296.4) * mm});
            skLineSegment(sketch, "E585", {"start": v(58.93, -300.09) * mm, "end": v(59.7, -299.98) * mm});
            skLineSegment(sketch, "E586", {"start": v(59.7, -299.98) * mm, "end": v(60.45, -299.76) * mm});
            skLineSegment(sketch, "E587", {"start": v(60.45, -299.76) * mm, "end": v(61.1, -299.44) * mm});
            skLineSegment(sketch, "E588", {"start": v(61.1, -299.44) * mm, "end": v(61.64, -299) * mm});
            skLineSegment(sketch, "E589", {"start": v(61.64, -299) * mm, "end": v(62.18, -298.46) * mm});
            skLineSegment(sketch, "E590", {"start": v(62.18, -298.46) * mm, "end": v(62.62, -297.81) * mm});
            skLineSegment(sketch, "E591", {"start": v(62.62, -297.81) * mm, "end": v(62.94, -297.17) * mm});
            skLineSegment(sketch, "E592", {"start": v(62.94, -297.17) * mm, "end": v(63.16, -296.4) * mm});
            skLineSegment(sketch, "E593", {"start": v(58.93, -300.09) * mm, "end": v(58.5, -300.09) * mm});
            skLineSegment(sketch, "E594", {"start": v(58.5, -300.09) * mm, "end": v(58.5, -269.02) * mm});
            skLineSegment(sketch, "E595", {"start": v(58.5, -269.02) * mm, "end": v(58.93, -269.02) * mm});
            skLineSegment(sketch, "E596", {"start": v(63.16, -272.7) * mm, "end": v(62.94, -271.95) * mm});
            skLineSegment(sketch, "E597", {"start": v(62.94, -271.95) * mm, "end": v(62.62, -271.3) * mm});
            skLineSegment(sketch, "E598", {"start": v(62.62, -271.3) * mm, "end": v(62.18, -270.65) * mm});
            skLineSegment(sketch, "E599", {"start": v(62.18, -270.65) * mm, "end": v(61.64, -270.1) * mm});
            skLineSegment(sketch, "E600", {"start": v(61.64, -270.1) * mm, "end": v(61.1, -269.67) * mm});
            skLineSegment(sketch, "E601", {"start": v(61.1, -269.67) * mm, "end": v(60.45, -269.35) * mm});
            skLineSegment(sketch, "E602", {"start": v(60.45, -269.35) * mm, "end": v(59.7, -269.13) * mm});
            skLineSegment(sketch, "E603", {"start": v(59.7, -269.13) * mm, "end": v(58.93, -269.02) * mm});
            skLineSegment(sketch, "E604", {"start": v(52.44, -263.61) * mm, "end": v(52.44, -305.5) * mm});
            skLineSegment(sketch, "E605", {"start": v(52.44, -305.5) * mm, "end": v(62.29, -305.5) * mm});
            skLineSegment(sketch, "E606", {"start": v(62.29, -305.5) * mm, "end": v(63.37, -305.07) * mm});
            skLineSegment(sketch, "E607", {"start": v(63.37, -305.07) * mm, "end": v(64.46, -304.42) * mm});
            skLineSegment(sketch, "E608", {"start": v(64.46, -304.42) * mm, "end": v(65.43, -303.77) * mm});
            skLineSegment(sketch, "E609", {"start": v(65.43, -303.77) * mm, "end": v(66.3, -302.9) * mm});
            skLineSegment(sketch, "E610", {"start": v(66.3, -302.9) * mm, "end": v(67.16, -302.04) * mm});
            skLineSegment(sketch, "E611", {"start": v(67.16, -302.04) * mm, "end": v(67.8, -301.06) * mm});
            skLineSegment(sketch, "E612", {"start": v(67.8, -301.06) * mm, "end": v(68.46, -299.98) * mm});
            skLineSegment(sketch, "E613", {"start": v(68.46, -299.98) * mm, "end": v(68.9, -298.79) * mm});
            skLineSegment(sketch, "E614", {"start": v(68.9, -298.79) * mm, "end": v(69.22, -297.7) * mm});
            skLineSegment(sketch, "E615", {"start": v(69.22, -297.7) * mm, "end": v(69.22, -271.4) * mm});
            skLineSegment(sketch, "E616", {"start": v(69.22, -271.4) * mm, "end": v(68.9, -270.32) * mm});
            skLineSegment(sketch, "E617", {"start": v(68.9, -270.32) * mm, "end": v(68.46, -269.13) * mm});
            skLineSegment(sketch, "E618", {"start": v(68.46, -269.13) * mm, "end": v(67.8, -268.05) * mm});
            skLineSegment(sketch, "E619", {"start": v(67.8, -268.05) * mm, "end": v(67.16, -267.08) * mm});
            skLineSegment(sketch, "E620", {"start": v(67.16, -267.08) * mm, "end": v(65.43, -265.34) * mm});
            skLineSegment(sketch, "E621", {"start": v(65.43, -265.34) * mm, "end": v(64.46, -264.7) * mm});
            skLineSegment(sketch, "E622", {"start": v(64.46, -264.7) * mm, "end": v(63.37, -264.04) * mm});
            skLineSegment(sketch, "E623", {"start": v(63.37, -264.04) * mm, "end": v(62.29, -263.61) * mm});
            skLineSegment(sketch, "E624", {"start": v(62.29, -263.61) * mm, "end": v(52.44, -263.61) * mm});
            skLineSegment(sketch, "E625", {"start": v(135.13, -272.7) * mm, "end": v(135.13, -296.4) * mm});
            skLineSegment(sketch, "E626", {"start": v(130.91, -300.09) * mm, "end": v(131.67, -299.98) * mm});
            skLineSegment(sketch, "E627", {"start": v(131.67, -299.98) * mm, "end": v(132.43, -299.76) * mm});
            skLineSegment(sketch, "E628", {"start": v(132.43, -299.76) * mm, "end": v(133.08, -299.44) * mm});
            skLineSegment(sketch, "E629", {"start": v(133.08, -299.44) * mm, "end": v(133.62, -299) * mm});
            skLineSegment(sketch, "E630", {"start": v(133.62, -299) * mm, "end": v(134.16, -298.46) * mm});
            skLineSegment(sketch, "E631", {"start": v(134.16, -298.46) * mm, "end": v(134.6, -297.81) * mm});
            skLineSegment(sketch, "E632", {"start": v(134.6, -297.81) * mm, "end": v(134.92, -297.17) * mm});
            skLineSegment(sketch, "E633", {"start": v(134.92, -297.17) * mm, "end": v(135.13, -296.4) * mm});
            skLineSegment(sketch, "E634", {"start": v(130.91, -300.09) * mm, "end": v(130.37, -300.09) * mm});
            skLineSegment(sketch, "E635", {"start": v(130.37, -300.09) * mm, "end": v(130.37, -269.02) * mm});
            skLineSegment(sketch, "E636", {"start": v(130.37, -269.02) * mm, "end": v(130.91, -269.02) * mm});
            skLineSegment(sketch, "E637", {"start": v(135.13, -272.7) * mm, "end": v(134.92, -271.95) * mm});
            skLineSegment(sketch, "E638", {"start": v(134.92, -271.95) * mm, "end": v(134.6, -271.3) * mm});
            skLineSegment(sketch, "E639", {"start": v(134.6, -271.3) * mm, "end": v(134.16, -270.65) * mm});
            skLineSegment(sketch, "E640", {"start": v(134.16, -270.65) * mm, "end": v(133.62, -270.1) * mm});
            skLineSegment(sketch, "E641", {"start": v(133.62, -270.1) * mm, "end": v(133.08, -269.67) * mm});
            skLineSegment(sketch, "E642", {"start": v(133.08, -269.67) * mm, "end": v(132.43, -269.35) * mm});
            skLineSegment(sketch, "E643", {"start": v(132.43, -269.35) * mm, "end": v(131.67, -269.13) * mm});
            skLineSegment(sketch, "E644", {"start": v(131.67, -269.13) * mm, "end": v(130.91, -269.02) * mm});
            skLineSegment(sketch, "E645", {"start": v(124.42, -263.61) * mm, "end": v(124.42, -305.5) * mm});
            skLineSegment(sketch, "E646", {"start": v(124.42, -305.5) * mm, "end": v(134.27, -305.5) * mm});
            skLineSegment(sketch, "E647", {"start": v(134.27, -305.5) * mm, "end": v(135.35, -305.07) * mm});
            skLineSegment(sketch, "E648", {"start": v(135.35, -305.07) * mm, "end": v(136.43, -304.42) * mm});
            skLineSegment(sketch, "E649", {"start": v(136.43, -304.42) * mm, "end": v(137.4, -303.77) * mm});
            skLineSegment(sketch, "E650", {"start": v(137.4, -303.77) * mm, "end": v(138.27, -302.9) * mm});
            skLineSegment(sketch, "E651", {"start": v(138.27, -302.9) * mm, "end": v(139.14, -302.04) * mm});
            skLineSegment(sketch, "E652", {"start": v(139.14, -302.04) * mm, "end": v(139.79, -301.06) * mm});
            skLineSegment(sketch, "E653", {"start": v(139.79, -301.06) * mm, "end": v(140.44, -299.98) * mm});
            skLineSegment(sketch, "E654", {"start": v(140.44, -299.98) * mm, "end": v(140.87, -298.79) * mm});
            skLineSegment(sketch, "E655", {"start": v(140.87, -298.79) * mm, "end": v(141.2, -297.7) * mm});
            skLineSegment(sketch, "E656", {"start": v(141.2, -297.7) * mm, "end": v(141.2, -271.4) * mm});
            skLineSegment(sketch, "E657", {"start": v(141.2, -271.4) * mm, "end": v(140.87, -270.32) * mm});
            skLineSegment(sketch, "E658", {"start": v(140.87, -270.32) * mm, "end": v(140.44, -269.13) * mm});
            skLineSegment(sketch, "E659", {"start": v(140.44, -269.13) * mm, "end": v(139.79, -268.05) * mm});
            skLineSegment(sketch, "E660", {"start": v(139.79, -268.05) * mm, "end": v(139.14, -267.08) * mm});
            skLineSegment(sketch, "E661", {"start": v(139.14, -267.08) * mm, "end": v(137.4, -265.34) * mm});
            skLineSegment(sketch, "E662", {"start": v(137.4, -265.34) * mm, "end": v(136.43, -264.7) * mm});
            skLineSegment(sketch, "E663", {"start": v(136.43, -264.7) * mm, "end": v(135.35, -264.04) * mm});
            skLineSegment(sketch, "E664", {"start": v(135.35, -264.04) * mm, "end": v(134.27, -263.61) * mm});
            skLineSegment(sketch, "E665", {"start": v(134.27, -263.61) * mm, "end": v(124.42, -263.61) * mm});
            skLineSegment(sketch, "E666", {"start": v(-223.02, -263.61) * mm, "end": v(-217.07, -263.61) * mm});
            skLineSegment(sketch, "E667", {"start": v(-217.07, -263.61) * mm, "end": v(-217.07, -305.5) * mm});
            skLineSegment(sketch, "E668", {"start": v(-217.07, -305.5) * mm, "end": v(-223.02, -305.5) * mm});
            skLineSegment(sketch, "E669", {"start": v(-223.02, -305.5) * mm, "end": v(-223.02, -263.61) * mm});
            skLineSegment(sketch, "E670", {"start": v(-197.15, -280.82) * mm, "end": v(-196.61, -279.85) * mm});
            skLineSegment(sketch, "E671", {"start": v(-196.61, -279.85) * mm, "end": v(-196.29, -278.76) * mm});
            skLineSegment(sketch, "E672", {"start": v(-196.29, -278.76) * mm, "end": v(-195.96, -277.68) * mm});
            skLineSegment(sketch, "E673", {"start": v(-195.96, -277.68) * mm, "end": v(-195.86, -276.5) * mm});
            skLineSegment(sketch, "E674", {"start": v(-195.86, -276.5) * mm, "end": v(-195.86, -275.4) * mm});
            skLineSegment(sketch, "E675", {"start": v(-195.86, -275.4) * mm, "end": v(-195.96, -274.22) * mm});
            skLineSegment(sketch, "E676", {"start": v(-195.96, -274.22) * mm, "end": v(-196.29, -273.14) * mm});
            skLineSegment(sketch, "E677", {"start": v(-196.29, -273.14) * mm, "end": v(-196.61, -272.05) * mm});
            skLineSegment(sketch, "E678", {"start": v(-196.61, -272.05) * mm, "end": v(-197.15, -271.08) * mm});
            skLineSegment(sketch, "E679", {"start": v(-200.83, -282.34) * mm, "end": v(-199.86, -282.23) * mm});
            skLineSegment(sketch, "E680", {"start": v(-199.86, -282.23) * mm, "end": v(-198.88, -281.9) * mm});
            skLineSegment(sketch, "E681", {"start": v(-198.88, -281.9) * mm, "end": v(-197.91, -281.47) * mm});
            skLineSegment(sketch, "E682", {"start": v(-197.91, -281.47) * mm, "end": v(-197.15, -280.82) * mm});
            skLineSegment(sketch, "E683", {"start": v(-200.83, -282.34) * mm, "end": v(-200.83, -269.57) * mm});
            skLineSegment(sketch, "E684", {"start": v(-197.15, -271.08) * mm, "end": v(-197.91, -270.43) * mm});
            skLineSegment(sketch, "E685", {"start": v(-197.91, -270.43) * mm, "end": v(-198.88, -270) * mm});
            skLineSegment(sketch, "E686", {"start": v(-198.88, -270) * mm, "end": v(-199.86, -269.67) * mm});
            skLineSegment(sketch, "E687", {"start": v(-199.86, -269.67) * mm, "end": v(-200.83, -269.57) * mm});
            skLineSegment(sketch, "E688", {"start": v(-200.83, -263.61) * mm, "end": v(-206.46, -263.61) * mm});
            skLineSegment(sketch, "E689", {"start": v(-206.46, -263.61) * mm, "end": v(-206.46, -305.5) * mm});
            skLineSegment(sketch, "E690", {"start": v(-206.46, -305.5) * mm, "end": v(-200.83, -305.5) * mm});
            skLineSegment(sketch, "E691", {"start": v(-200.83, -305.5) * mm, "end": v(-200.83, -287.2) * mm});
            skLineSegment(sketch, "E692", {"start": v(-200.83, -287.2) * mm, "end": v(-200.4, -287.42) * mm});
            skLineSegment(sketch, "E693", {"start": v(-200.4, -287.42) * mm, "end": v(-199.54, -287.42) * mm});
            skLineSegment(sketch, "E694", {"start": v(-199.54, -287.42) * mm, "end": v(-199.1, -287.2) * mm});
            skLineSegment(sketch, "E695", {"start": v(-199.1, -287.2) * mm, "end": v(-195.86, -305.5) * mm});
            skLineSegment(sketch, "E696", {"start": v(-195.86, -305.5) * mm, "end": v(-190, -305.5) * mm});
            skLineSegment(sketch, "E697", {"start": v(-190, -305.5) * mm, "end": v(-193.47, -285.58) * mm});
            skLineSegment(sketch, "E698", {"start": v(-193.47, -285.58) * mm, "end": v(-192.6, -284.4) * mm});
            skLineSegment(sketch, "E699", {"start": v(-192.6, -284.4) * mm, "end": v(-191.96, -283.1) * mm});
            skLineSegment(sketch, "E700", {"start": v(-191.96, -283.1) * mm, "end": v(-191.3, -281.8) * mm});
            skLineSegment(sketch, "E701", {"start": v(-191.3, -281.8) * mm, "end": v(-190.87, -280.39) * mm});
            skLineSegment(sketch, "E702", {"start": v(-190.87, -280.39) * mm, "end": v(-190.44, -278.87) * mm});
            skLineSegment(sketch, "E703", {"start": v(-190.44, -278.87) * mm, "end": v(-190.23, -277.47) * mm});
            skLineSegment(sketch, "E704", {"start": v(-190.23, -277.47) * mm, "end": v(-190.23, -274.44) * mm});
            skLineSegment(sketch, "E705", {"start": v(-190.23, -274.44) * mm, "end": v(-190.44, -273.03) * mm});
            skLineSegment(sketch, "E706", {"start": v(-190.44, -273.03) * mm, "end": v(-190.87, -271.51) * mm});
            skLineSegment(sketch, "E707", {"start": v(-190.87, -271.51) * mm, "end": v(-191.3, -270.1) * mm});
            skLineSegment(sketch, "E708", {"start": v(-191.3, -270.1) * mm, "end": v(-191.96, -268.8) * mm});
            skLineSegment(sketch, "E709", {"start": v(-191.96, -268.8) * mm, "end": v(-192.6, -267.5) * mm});
            skLineSegment(sketch, "E710", {"start": v(-192.6, -267.5) * mm, "end": v(-193.47, -266.32) * mm});
            skLineSegment(sketch, "E711", {"start": v(-193.47, -266.32) * mm, "end": v(-194.56, -265.56) * mm});
            skLineSegment(sketch, "E712", {"start": v(-194.56, -265.56) * mm, "end": v(-195.75, -264.91) * mm});
            skLineSegment(sketch, "E713", {"start": v(-195.75, -264.91) * mm, "end": v(-196.93, -264.37) * mm});
            skLineSegment(sketch, "E714", {"start": v(-196.93, -264.37) * mm, "end": v(-198.24, -263.94) * mm});
            skLineSegment(sketch, "E715", {"start": v(-198.24, -263.94) * mm, "end": v(-199.54, -263.72) * mm});
            skLineSegment(sketch, "E716", {"start": v(-199.54, -263.72) * mm, "end": v(-200.83, -263.61) * mm});
            skLineSegment(sketch, "E717", {"start": v(-167.82, -263.61) * mm, "end": v(-181.57, -263.61) * mm});
            skLineSegment(sketch, "E718", {"start": v(-181.57, -263.61) * mm, "end": v(-181.57, -305.5) * mm});
            skLineSegment(sketch, "E719", {"start": v(-181.57, -305.5) * mm, "end": v(-167.82, -305.5) * mm});
            skLineSegment(sketch, "E720", {"start": v(-167.82, -305.5) * mm, "end": v(-167.82, -299.65) * mm});
            skLineSegment(sketch, "E721", {"start": v(-167.82, -299.65) * mm, "end": v(-175.83, -299.65) * mm});
            skLineSegment(sketch, "E722", {"start": v(-175.83, -299.65) * mm, "end": v(-175.83, -287.64) * mm});
            skLineSegment(sketch, "E723", {"start": v(-175.83, -287.64) * mm, "end": v(-170.1, -287.64) * mm});
            skLineSegment(sketch, "E724", {"start": v(-170.1, -287.64) * mm, "end": v(-170.1, -281.36) * mm});
            skLineSegment(sketch, "E725", {"start": v(-170.1, -281.36) * mm, "end": v(-175.83, -281.36) * mm});
            skLineSegment(sketch, "E726", {"start": v(-175.83, -281.36) * mm, "end": v(-175.83, -270.32) * mm});
            skLineSegment(sketch, "E727", {"start": v(-175.83, -270.32) * mm, "end": v(-167.82, -270.32) * mm});
            skLineSegment(sketch, "E728", {"start": v(-167.82, -270.32) * mm, "end": v(-167.82, -263.61) * mm});
            skLineSegment(sketch, "E729", {"start": v(-41.72, -263.61) * mm, "end": v(-55.47, -263.61) * mm});
            skLineSegment(sketch, "E730", {"start": v(-55.47, -263.61) * mm, "end": v(-55.47, -305.5) * mm});
            skLineSegment(sketch, "E731", {"start": v(-55.47, -305.5) * mm, "end": v(-41.72, -305.5) * mm});
            skLineSegment(sketch, "E732", {"start": v(-41.72, -305.5) * mm, "end": v(-41.72, -299.65) * mm});
            skLineSegment(sketch, "E733", {"start": v(-41.72, -299.65) * mm, "end": v(-49.73, -299.65) * mm});
            skLineSegment(sketch, "E734", {"start": v(-49.73, -299.65) * mm, "end": v(-49.73, -287.64) * mm});
            skLineSegment(sketch, "E735", {"start": v(-49.73, -287.64) * mm, "end": v(-44, -287.64) * mm});
            skLineSegment(sketch, "E736", {"start": v(-44, -287.64) * mm, "end": v(-44, -281.36) * mm});
            skLineSegment(sketch, "E737", {"start": v(-44, -281.36) * mm, "end": v(-49.73, -281.36) * mm});
            skLineSegment(sketch, "E738", {"start": v(-49.73, -281.36) * mm, "end": v(-49.73, -270.32) * mm});
            skLineSegment(sketch, "E739", {"start": v(-49.73, -270.32) * mm, "end": v(-41.72, -270.32) * mm});
            skLineSegment(sketch, "E740", {"start": v(-41.72, -270.32) * mm, "end": v(-41.72, -263.61) * mm});
            skLineSegment(sketch, "E741", {"start": v(31.01, -263.61) * mm, "end": v(17.26, -263.61) * mm});
            skLineSegment(sketch, "E742", {"start": v(17.26, -263.61) * mm, "end": v(17.26, -305.5) * mm});
            skLineSegment(sketch, "E743", {"start": v(17.26, -305.5) * mm, "end": v(31.01, -305.5) * mm});
            skLineSegment(sketch, "E744", {"start": v(31.01, -305.5) * mm, "end": v(31.01, -299.65) * mm});
            skLineSegment(sketch, "E745", {"start": v(31.01, -299.65) * mm, "end": v(23, -299.65) * mm});
            skLineSegment(sketch, "E746", {"start": v(23, -299.65) * mm, "end": v(23, -287.64) * mm});
            skLineSegment(sketch, "E747", {"start": v(23, -287.64) * mm, "end": v(28.74, -287.64) * mm});
            skLineSegment(sketch, "E748", {"start": v(28.74, -287.64) * mm, "end": v(28.74, -281.36) * mm});
            skLineSegment(sketch, "E749", {"start": v(28.74, -281.36) * mm, "end": v(23, -281.36) * mm});
            skLineSegment(sketch, "E750", {"start": v(23, -281.36) * mm, "end": v(23, -270.32) * mm});
            skLineSegment(sketch, "E751", {"start": v(23, -270.32) * mm, "end": v(31.01, -270.32) * mm});
            skLineSegment(sketch, "E752", {"start": v(31.01, -270.32) * mm, "end": v(31.01, -263.61) * mm});
            skLineSegment(sketch, "E753", {"start": v(92.38, -263.61) * mm, "end": v(78.63, -263.61) * mm});
            skLineSegment(sketch, "E754", {"start": v(78.63, -263.61) * mm, "end": v(78.63, -305.5) * mm});
            skLineSegment(sketch, "E755", {"start": v(78.63, -305.5) * mm, "end": v(92.38, -305.5) * mm});
            skLineSegment(sketch, "E756", {"start": v(92.38, -305.5) * mm, "end": v(92.38, -299.65) * mm});
            skLineSegment(sketch, "E757", {"start": v(92.38, -299.65) * mm, "end": v(84.37, -299.65) * mm});
            skLineSegment(sketch, "E758", {"start": v(84.37, -299.65) * mm, "end": v(84.37, -287.64) * mm});
            skLineSegment(sketch, "E759", {"start": v(84.37, -287.64) * mm, "end": v(90.1, -287.64) * mm});
            skLineSegment(sketch, "E760", {"start": v(90.1, -287.64) * mm, "end": v(90.1, -281.36) * mm});
            skLineSegment(sketch, "E761", {"start": v(90.1, -281.36) * mm, "end": v(84.37, -281.36) * mm});
            skLineSegment(sketch, "E762", {"start": v(84.37, -281.36) * mm, "end": v(84.37, -270.32) * mm});
            skLineSegment(sketch, "E763", {"start": v(84.37, -270.32) * mm, "end": v(92.38, -270.32) * mm});
            skLineSegment(sketch, "E764", {"start": v(92.38, -270.32) * mm, "end": v(92.38, -263.61) * mm});
            skLineSegment(sketch, "E765", {"start": v(164.47, -263.61) * mm, "end": v(150.72, -263.61) * mm});
            skLineSegment(sketch, "E766", {"start": v(150.72, -263.61) * mm, "end": v(150.72, -305.5) * mm});
            skLineSegment(sketch, "E767", {"start": v(150.72, -305.5) * mm, "end": v(164.47, -305.5) * mm});
            skLineSegment(sketch, "E768", {"start": v(164.47, -305.5) * mm, "end": v(164.47, -299.65) * mm});
            skLineSegment(sketch, "E769", {"start": v(164.47, -299.65) * mm, "end": v(156.46, -299.65) * mm});
            skLineSegment(sketch, "E770", {"start": v(156.46, -299.65) * mm, "end": v(156.46, -287.64) * mm});
            skLineSegment(sketch, "E771", {"start": v(156.46, -287.64) * mm, "end": v(162.2, -287.64) * mm});
            skLineSegment(sketch, "E772", {"start": v(162.2, -287.64) * mm, "end": v(162.2, -281.36) * mm});
            skLineSegment(sketch, "E773", {"start": v(162.2, -281.36) * mm, "end": v(156.46, -281.36) * mm});
            skLineSegment(sketch, "E774", {"start": v(156.46, -281.36) * mm, "end": v(156.46, -270.32) * mm});
            skLineSegment(sketch, "E775", {"start": v(156.46, -270.32) * mm, "end": v(164.47, -270.32) * mm});
            skLineSegment(sketch, "E776", {"start": v(164.47, -270.32) * mm, "end": v(164.47, -263.61) * mm});
            skLineSegment(sketch, "E777", {"start": v(-159.7, -297.7) * mm, "end": v(-159.7, -298.79) * mm});
            skLineSegment(sketch, "E778", {"start": v(-159.7, -298.79) * mm, "end": v(-159.49, -299.76) * mm});
            skLineSegment(sketch, "E779", {"start": v(-159.49, -299.76) * mm, "end": v(-159.16, -300.74) * mm});
            skLineSegment(sketch, "E780", {"start": v(-159.16, -300.74) * mm, "end": v(-158.73, -301.6) * mm});
            skLineSegment(sketch, "E781", {"start": v(-158.73, -301.6) * mm, "end": v(-158.08, -302.47) * mm});
            skLineSegment(sketch, "E782", {"start": v(-158.08, -302.47) * mm, "end": v(-157.43, -303.23) * mm});
            skLineSegment(sketch, "E783", {"start": v(-157.43, -303.23) * mm, "end": v(-156.67, -303.98) * mm});
            skLineSegment(sketch, "E784", {"start": v(-156.67, -303.98) * mm, "end": v(-155.8, -304.53) * mm});
            skLineSegment(sketch, "E785", {"start": v(-155.8, -304.53) * mm, "end": v(-154.94, -304.96) * mm});
            skLineSegment(sketch, "E786", {"start": v(-154.94, -304.96) * mm, "end": v(-153.97, -305.28) * mm});
            skLineSegment(sketch, "E787", {"start": v(-153.97, -305.28) * mm, "end": v(-152.88, -305.5) * mm});
            skLineSegment(sketch, "E788", {"start": v(-152.88, -305.5) * mm, "end": v(-150.94, -305.5) * mm});
            skLineSegment(sketch, "E789", {"start": v(-150.94, -305.5) * mm, "end": v(-149.85, -305.28) * mm});
            skLineSegment(sketch, "E790", {"start": v(-149.85, -305.28) * mm, "end": v(-148.88, -304.96) * mm});
            skLineSegment(sketch, "E791", {"start": v(-148.88, -304.96) * mm, "end": v(-148.01, -304.53) * mm});
            skLineSegment(sketch, "E792", {"start": v(-148.01, -304.53) * mm, "end": v(-147.15, -303.98) * mm});
            skLineSegment(sketch, "E793", {"start": v(-147.15, -303.98) * mm, "end": v(-146.39, -303.23) * mm});
            skLineSegment(sketch, "E794", {"start": v(-146.39, -303.23) * mm, "end": v(-145.74, -302.47) * mm});
            skLineSegment(sketch, "E795", {"start": v(-145.74, -302.47) * mm, "end": v(-144.66, -300.74) * mm});
            skLineSegment(sketch, "E796", {"start": v(-144.66, -300.74) * mm, "end": v(-144.33, -299.76) * mm});
            skLineSegment(sketch, "E797", {"start": v(-144.33, -299.76) * mm, "end": v(-144.22, -298.79) * mm});
            skLineSegment(sketch, "E798", {"start": v(-144.22, -298.79) * mm, "end": v(-144.12, -297.7) * mm});
            skLineSegment(sketch, "E799", {"start": v(-144.12, -297.7) * mm, "end": v(-144.12, -291.21) * mm});
            skLineSegment(sketch, "E800", {"start": v(-144.12, -291.21) * mm, "end": v(-149.74, -291.21) * mm});
            skLineSegment(sketch, "E801", {"start": v(-149.74, -291.21) * mm, "end": v(-149.74, -298.14) * mm});
            skLineSegment(sketch, "E802", {"start": v(-154.07, -298.14) * mm, "end": v(-154.07, -298.68) * mm});
            skLineSegment(sketch, "E803", {"start": v(-154.07, -298.68) * mm, "end": v(-153.86, -299.11) * mm});
            skLineSegment(sketch, "E804", {"start": v(-153.86, -299.11) * mm, "end": v(-153.64, -299.55) * mm});
            skLineSegment(sketch, "E805", {"start": v(-153.64, -299.55) * mm, "end": v(-153.32, -299.87) * mm});
            skLineSegment(sketch, "E806", {"start": v(-153.32, -299.87) * mm, "end": v(-152.88, -300.09) * mm});
            skLineSegment(sketch, "E807", {"start": v(-152.88, -300.09) * mm, "end": v(-152.45, -300.3) * mm});
            skLineSegment(sketch, "E808", {"start": v(-152.45, -300.3) * mm, "end": v(-151.48, -300.3) * mm});
            skLineSegment(sketch, "E809", {"start": v(-151.48, -300.3) * mm, "end": v(-150.94, -300.09) * mm});
            skLineSegment(sketch, "E810", {"start": v(-150.94, -300.09) * mm, "end": v(-150.61, -299.87) * mm});
            skLineSegment(sketch, "E811", {"start": v(-150.61, -299.87) * mm, "end": v(-150.18, -299.55) * mm});
            skLineSegment(sketch, "E812", {"start": v(-150.18, -299.55) * mm, "end": v(-149.96, -299.11) * mm});
            skLineSegment(sketch, "E813", {"start": v(-149.96, -299.11) * mm, "end": v(-149.74, -298.68) * mm});
            skLineSegment(sketch, "E814", {"start": v(-149.74, -298.68) * mm, "end": v(-149.74, -298.14) * mm});
            skLineSegment(sketch, "E815", {"start": v(-154.07, -298.14) * mm, "end": v(-154.07, -270.97) * mm});
            skLineSegment(sketch, "E816", {"start": v(-149.74, -270.97) * mm, "end": v(-149.74, -270.43) * mm});
            skLineSegment(sketch, "E817", {"start": v(-149.74, -270.43) * mm, "end": v(-149.96, -270) * mm});
            skLineSegment(sketch, "E818", {"start": v(-149.96, -270) * mm, "end": v(-150.18, -269.57) * mm});
            skLineSegment(sketch, "E819", {"start": v(-150.18, -269.57) * mm, "end": v(-150.61, -269.24) * mm});
            skLineSegment(sketch, "E820", {"start": v(-150.61, -269.24) * mm, "end": v(-150.94, -269.02) * mm});
            skLineSegment(sketch, "E821", {"start": v(-150.94, -269.02) * mm, "end": v(-151.48, -268.8) * mm});
            skLineSegment(sketch, "E822", {"start": v(-151.48, -268.8) * mm, "end": v(-152.45, -268.8) * mm});
            skLineSegment(sketch, "E823", {"start": v(-152.45, -268.8) * mm, "end": v(-153.32, -269.24) * mm});
            skLineSegment(sketch, "E824", {"start": v(-153.32, -269.24) * mm, "end": v(-153.64, -269.57) * mm});
            skLineSegment(sketch, "E825", {"start": v(-153.64, -269.57) * mm, "end": v(-153.86, -270) * mm});
            skLineSegment(sketch, "E826", {"start": v(-153.86, -270) * mm, "end": v(-154.07, -270.43) * mm});
            skLineSegment(sketch, "E827", {"start": v(-154.07, -270.43) * mm, "end": v(-154.07, -270.97) * mm});
            skLineSegment(sketch, "E828", {"start": v(-149.74, -270.97) * mm, "end": v(-149.74, -277.9) * mm});
            skLineSegment(sketch, "E829", {"start": v(-149.74, -277.9) * mm, "end": v(-144.12, -277.9) * mm});
            skLineSegment(sketch, "E830", {"start": v(-144.12, -277.9) * mm, "end": v(-144.12, -271.4) * mm});
            skLineSegment(sketch, "E831", {"start": v(-144.12, -271.4) * mm, "end": v(-144.22, -270.32) * mm});
            skLineSegment(sketch, "E832", {"start": v(-144.22, -270.32) * mm, "end": v(-144.33, -269.35) * mm});
            skLineSegment(sketch, "E833", {"start": v(-144.33, -269.35) * mm, "end": v(-144.66, -268.37) * mm});
            skLineSegment(sketch, "E834", {"start": v(-144.66, -268.37) * mm, "end": v(-145.2, -267.5) * mm});
            skLineSegment(sketch, "E835", {"start": v(-145.2, -267.5) * mm, "end": v(-145.74, -266.64) * mm});
            skLineSegment(sketch, "E836", {"start": v(-145.74, -266.64) * mm, "end": v(-146.39, -265.88) * mm});
            skLineSegment(sketch, "E837", {"start": v(-146.39, -265.88) * mm, "end": v(-147.15, -265.13) * mm});
            skLineSegment(sketch, "E838", {"start": v(-147.15, -265.13) * mm, "end": v(-148.01, -264.59) * mm});
            skLineSegment(sketch, "E839", {"start": v(-148.01, -264.59) * mm, "end": v(-148.88, -264.15) * mm});
            skLineSegment(sketch, "E840", {"start": v(-148.88, -264.15) * mm, "end": v(-149.85, -263.83) * mm});
            skLineSegment(sketch, "E841", {"start": v(-149.85, -263.83) * mm, "end": v(-150.94, -263.61) * mm});
            skLineSegment(sketch, "E842", {"start": v(-150.94, -263.61) * mm, "end": v(-152.88, -263.61) * mm});
            skLineSegment(sketch, "E843", {"start": v(-152.88, -263.61) * mm, "end": v(-153.97, -263.83) * mm});
            skLineSegment(sketch, "E844", {"start": v(-153.97, -263.83) * mm, "end": v(-154.94, -264.15) * mm});
            skLineSegment(sketch, "E845", {"start": v(-154.94, -264.15) * mm, "end": v(-155.8, -264.59) * mm});
            skLineSegment(sketch, "E846", {"start": v(-155.8, -264.59) * mm, "end": v(-156.67, -265.13) * mm});
            skLineSegment(sketch, "E847", {"start": v(-156.67, -265.13) * mm, "end": v(-157.43, -265.88) * mm});
            skLineSegment(sketch, "E848", {"start": v(-157.43, -265.88) * mm, "end": v(-158.08, -266.64) * mm});
            skLineSegment(sketch, "E849", {"start": v(-158.08, -266.64) * mm, "end": v(-158.73, -267.5) * mm});
            skLineSegment(sketch, "E850", {"start": v(-158.73, -267.5) * mm, "end": v(-159.16, -268.37) * mm});
            skLineSegment(sketch, "E851", {"start": v(-159.16, -268.37) * mm, "end": v(-159.49, -269.35) * mm});
            skLineSegment(sketch, "E852", {"start": v(-159.49, -269.35) * mm, "end": v(-159.7, -270.32) * mm});
            skLineSegment(sketch, "E853", {"start": v(-159.7, -270.32) * mm, "end": v(-159.7, -271.4) * mm});
            skLineSegment(sketch, "E854", {"start": v(-159.7, -271.4) * mm, "end": v(-159.7, -297.7) * mm});
            skLineSegment(sketch, "E855", {"start": v(-119.87, -263.61) * mm, "end": v(-136.97, -263.61) * mm});
            skLineSegment(sketch, "E856", {"start": v(-136.97, -263.61) * mm, "end": v(-136.97, -270.32) * mm});
            skLineSegment(sketch, "E857", {"start": v(-136.97, -270.32) * mm, "end": v(-131.56, -270.32) * mm});
            skLineSegment(sketch, "E858", {"start": v(-131.56, -270.32) * mm, "end": v(-131.56, -305.5) * mm});
            skLineSegment(sketch, "E859", {"start": v(-131.56, -305.5) * mm, "end": v(-125.6, -305.5) * mm});
            skLineSegment(sketch, "E860", {"start": v(-125.6, -305.5) * mm, "end": v(-125.6, -270.32) * mm});
            skLineSegment(sketch, "E861", {"start": v(-125.6, -270.32) * mm, "end": v(-119.87, -270.32) * mm});
            skLineSegment(sketch, "E862", {"start": v(-119.87, -270.32) * mm, "end": v(-119.87, -263.61) * mm});
            skLineSegment(sketch, "E863", {"start": v(9.58, -263.61) * mm, "end": v(-7.52, -263.61) * mm});
            skLineSegment(sketch, "E864", {"start": v(-7.52, -263.61) * mm, "end": v(-7.52, -270.32) * mm});
            skLineSegment(sketch, "E865", {"start": v(-7.52, -270.32) * mm, "end": v(-2.1, -270.32) * mm});
            skLineSegment(sketch, "E866", {"start": v(-2.1, -270.32) * mm, "end": v(-2.1, -305.5) * mm});
            skLineSegment(sketch, "E867", {"start": v(-2.1, -305.5) * mm, "end": v(3.74, -305.5) * mm});
            skLineSegment(sketch, "E868", {"start": v(3.74, -305.5) * mm, "end": v(3.74, -270.32) * mm});
            skLineSegment(sketch, "E869", {"start": v(3.74, -270.32) * mm, "end": v(9.58, -270.32) * mm});
            skLineSegment(sketch, "E870", {"start": v(9.58, -270.32) * mm, "end": v(9.58, -263.61) * mm});
            skLineSegment(sketch, "E871", {"start": v(110.35, -270.97) * mm, "end": v(110.35, -274.33) * mm});
            skLineSegment(sketch, "E872", {"start": v(110.35, -274.33) * mm, "end": v(116.08, -274.33) * mm});
            skLineSegment(sketch, "E873", {"start": v(116.08, -274.33) * mm, "end": v(116.08, -271.4) * mm});
            skLineSegment(sketch, "E874", {"start": v(116.08, -271.4) * mm, "end": v(115.98, -270.32) * mm});
            skLineSegment(sketch, "E875", {"start": v(115.98, -270.32) * mm, "end": v(115.76, -269.35) * mm});
            skLineSegment(sketch, "E876", {"start": v(115.76, -269.35) * mm, "end": v(115.43, -268.37) * mm});
            skLineSegment(sketch, "E877", {"start": v(115.43, -268.37) * mm, "end": v(115, -267.5) * mm});
            skLineSegment(sketch, "E878", {"start": v(115, -267.5) * mm, "end": v(114.46, -266.64) * mm});
            skLineSegment(sketch, "E879", {"start": v(114.46, -266.64) * mm, "end": v(113.7, -265.88) * mm});
            skLineSegment(sketch, "E880", {"start": v(113.7, -265.88) * mm, "end": v(112.95, -265.24) * mm});
            skLineSegment(sketch, "E881", {"start": v(112.95, -265.24) * mm, "end": v(112.08, -264.59) * mm});
            skLineSegment(sketch, "E882", {"start": v(112.08, -264.59) * mm, "end": v(111.21, -264.15) * mm});
            skLineSegment(sketch, "E883", {"start": v(111.21, -264.15) * mm, "end": v(110.24, -263.83) * mm});
            skLineSegment(sketch, "E884", {"start": v(110.24, -263.83) * mm, "end": v(109.26, -263.61) * mm});
            skLineSegment(sketch, "E885", {"start": v(109.26, -263.61) * mm, "end": v(107.2, -263.61) * mm});
            skLineSegment(sketch, "E886", {"start": v(107.2, -263.61) * mm, "end": v(106.23, -263.83) * mm});
            skLineSegment(sketch, "E887", {"start": v(106.23, -263.83) * mm, "end": v(105.26, -264.15) * mm});
            skLineSegment(sketch, "E888", {"start": v(105.26, -264.15) * mm, "end": v(104.29, -264.59) * mm});
            skLineSegment(sketch, "E889", {"start": v(104.29, -264.59) * mm, "end": v(103.53, -265.24) * mm});
            skLineSegment(sketch, "E890", {"start": v(103.53, -265.24) * mm, "end": v(102.67, -265.88) * mm});
            skLineSegment(sketch, "E891", {"start": v(102.67, -265.88) * mm, "end": v(102.02, -266.64) * mm});
            skLineSegment(sketch, "E892", {"start": v(102.02, -266.64) * mm, "end": v(101.47, -267.5) * mm});
            skLineSegment(sketch, "E893", {"start": v(101.47, -267.5) * mm, "end": v(101.04, -268.37) * mm});
            skLineSegment(sketch, "E894", {"start": v(101.04, -268.37) * mm, "end": v(100.72, -269.35) * mm});
            skLineSegment(sketch, "E895", {"start": v(100.72, -269.35) * mm, "end": v(100.5, -270.32) * mm});
            skLineSegment(sketch, "E896", {"start": v(100.5, -270.32) * mm, "end": v(100.39, -271.4) * mm});
            skLineSegment(sketch, "E897", {"start": v(100.39, -271.4) * mm, "end": v(100.39, -274.33) * mm});
            skLineSegment(sketch, "E898", {"start": v(100.39, -274.33) * mm, "end": v(101.04, -276.28) * mm});
            skLineSegment(sketch, "E899", {"start": v(101.04, -276.28) * mm, "end": v(101.69, -278.22) * mm});
            skLineSegment(sketch, "E900", {"start": v(101.69, -278.22) * mm, "end": v(102.56, -280.06) * mm});
            skLineSegment(sketch, "E901", {"start": v(102.56, -280.06) * mm, "end": v(103.53, -281.9) * mm});
            skLineSegment(sketch, "E902", {"start": v(103.53, -281.9) * mm, "end": v(104.72, -283.64) * mm});
            skLineSegment(sketch, "E903", {"start": v(104.72, -283.64) * mm, "end": v(105.9, -285.26) * mm});
            skLineSegment(sketch, "E904", {"start": v(110.78, -293.49) * mm, "end": v(108.4, -289.37) * mm});
            skLineSegment(sketch, "E905", {"start": v(108.4, -289.37) * mm, "end": v(105.9, -285.26) * mm});
            skLineSegment(sketch, "E906", {"start": v(110.78, -293.49) * mm, "end": v(110.78, -297.49) * mm});
            skLineSegment(sketch, "E907", {"start": v(105.05, -298.14) * mm, "end": v(105.26, -298.68) * mm});
            skLineSegment(sketch, "E908", {"start": v(105.26, -298.68) * mm, "end": v(105.59, -299.22) * mm});
            skLineSegment(sketch, "E909", {"start": v(105.59, -299.22) * mm, "end": v(105.9, -299.65) * mm});
            skLineSegment(sketch, "E910", {"start": v(105.9, -299.65) * mm, "end": v(106.34, -299.98) * mm});
            skLineSegment(sketch, "E911", {"start": v(106.34, -299.98) * mm, "end": v(106.88, -300.2) * mm});
            skLineSegment(sketch, "E912", {"start": v(106.88, -300.2) * mm, "end": v(107.43, -300.3) * mm});
            skLineSegment(sketch, "E913", {"start": v(107.43, -300.3) * mm, "end": v(107.97, -300.41) * mm});
            skLineSegment(sketch, "E914", {"start": v(107.97, -300.41) * mm, "end": v(108.51, -300.3) * mm});
            skLineSegment(sketch, "E915", {"start": v(108.51, -300.3) * mm, "end": v(109.05, -300.2) * mm});
            skLineSegment(sketch, "E916", {"start": v(109.05, -300.2) * mm, "end": v(109.59, -299.87) * mm});
            skLineSegment(sketch, "E917", {"start": v(109.59, -299.87) * mm, "end": v(110.02, -299.55) * mm});
            skLineSegment(sketch, "E918", {"start": v(110.02, -299.55) * mm, "end": v(110.35, -299.11) * mm});
            skLineSegment(sketch, "E919", {"start": v(110.35, -299.11) * mm, "end": v(110.78, -298.03) * mm});
            skLineSegment(sketch, "E920", {"start": v(110.78, -298.03) * mm, "end": v(110.78, -297.49) * mm});
            skLineSegment(sketch, "E921", {"start": v(105.05, -298.14) * mm, "end": v(105.05, -293.49) * mm});
            skLineSegment(sketch, "E922", {"start": v(105.05, -293.49) * mm, "end": v(99.52, -293.49) * mm});
            skLineSegment(sketch, "E923", {"start": v(99.52, -293.49) * mm, "end": v(99.52, -297.7) * mm});
            skLineSegment(sketch, "E924", {"start": v(99.52, -297.7) * mm, "end": v(99.63, -298.68) * mm});
            skLineSegment(sketch, "E925", {"start": v(99.63, -298.68) * mm, "end": v(99.85, -299.65) * mm});
            skLineSegment(sketch, "E926", {"start": v(99.85, -299.65) * mm, "end": v(100.17, -300.63) * mm});
            skLineSegment(sketch, "E927", {"start": v(100.17, -300.63) * mm, "end": v(100.72, -301.5) * mm});
            skLineSegment(sketch, "E928", {"start": v(100.72, -301.5) * mm, "end": v(101.26, -302.36) * mm});
            skLineSegment(sketch, "E929", {"start": v(101.26, -302.36) * mm, "end": v(101.9, -303.12) * mm});
            skLineSegment(sketch, "E930", {"start": v(101.9, -303.12) * mm, "end": v(102.67, -303.77) * mm});
            skLineSegment(sketch, "E931", {"start": v(102.67, -303.77) * mm, "end": v(103.53, -304.3) * mm});
            skLineSegment(sketch, "E932", {"start": v(103.53, -304.3) * mm, "end": v(104.4, -304.85) * mm});
            skLineSegment(sketch, "E933", {"start": v(104.4, -304.85) * mm, "end": v(105.26, -305.18) * mm});
            skLineSegment(sketch, "E934", {"start": v(105.26, -305.18) * mm, "end": v(106.23, -305.4) * mm});
            skLineSegment(sketch, "E935", {"start": v(106.23, -305.4) * mm, "end": v(107.32, -305.5) * mm});
            skLineSegment(sketch, "E936", {"start": v(107.32, -305.5) * mm, "end": v(108.3, -305.5) * mm});
            skLineSegment(sketch, "E937", {"start": v(108.3, -305.5) * mm, "end": v(109.26, -305.4) * mm});
            skLineSegment(sketch, "E938", {"start": v(109.26, -305.4) * mm, "end": v(110.24, -305.18) * mm});
            skLineSegment(sketch, "E939", {"start": v(110.24, -305.18) * mm, "end": v(111.21, -304.85) * mm});
            skLineSegment(sketch, "E940", {"start": v(111.21, -304.85) * mm, "end": v(112.08, -304.3) * mm});
            skLineSegment(sketch, "E941", {"start": v(112.08, -304.3) * mm, "end": v(112.95, -303.77) * mm});
            skLineSegment(sketch, "E942", {"start": v(112.95, -303.77) * mm, "end": v(114.35, -302.36) * mm});
            skLineSegment(sketch, "E943", {"start": v(114.35, -302.36) * mm, "end": v(114.9, -301.5) * mm});
            skLineSegment(sketch, "E944", {"start": v(114.9, -301.5) * mm, "end": v(115.33, -300.63) * mm});
            skLineSegment(sketch, "E945", {"start": v(115.33, -300.63) * mm, "end": v(115.65, -299.65) * mm});
            skLineSegment(sketch, "E946", {"start": v(115.65, -299.65) * mm, "end": v(115.87, -298.68) * mm});
            skLineSegment(sketch, "E947", {"start": v(115.87, -298.68) * mm, "end": v(116.08, -297.7) * mm});
            skLineSegment(sketch, "E948", {"start": v(116.08, -297.7) * mm, "end": v(116.08, -293.49) * mm});
            skLineSegment(sketch, "E949", {"start": v(116.08, -293.49) * mm, "end": v(115.43, -291.43) * mm});
            skLineSegment(sketch, "E950", {"start": v(115.43, -291.43) * mm, "end": v(114.68, -289.37) * mm});
            skLineSegment(sketch, "E951", {"start": v(114.68, -289.37) * mm, "end": v(113.81, -287.42) * mm});
            skLineSegment(sketch, "E952", {"start": v(113.81, -287.42) * mm, "end": v(112.73, -285.48) * mm});
            skLineSegment(sketch, "E953", {"start": v(112.73, -285.48) * mm, "end": v(111.65, -283.64) * mm});
            skLineSegment(sketch, "E954", {"start": v(111.65, -283.64) * mm, "end": v(110.35, -281.9) * mm});
            skLineSegment(sketch, "E955", {"start": v(106.02, -274.33) * mm, "end": v(107, -276.38) * mm});
            skLineSegment(sketch, "E956", {"start": v(107, -276.38) * mm, "end": v(107.97, -278.22) * mm});
            skLineSegment(sketch, "E957", {"start": v(107.97, -278.22) * mm, "end": v(109.16, -280.06) * mm});
            skLineSegment(sketch, "E958", {"start": v(109.16, -280.06) * mm, "end": v(110.35, -281.9) * mm});
            skLineSegment(sketch, "E959", {"start": v(106.02, -274.33) * mm, "end": v(106.02, -270.97) * mm});
            skLineSegment(sketch, "E960", {"start": v(110.35, -270.97) * mm, "end": v(110.35, -270.43) * mm});
            skLineSegment(sketch, "E961", {"start": v(110.35, -270.43) * mm, "end": v(110.13, -270) * mm});
            skLineSegment(sketch, "E962", {"start": v(110.13, -270) * mm, "end": v(109.91, -269.57) * mm});
            skLineSegment(sketch, "E963", {"start": v(109.91, -269.57) * mm, "end": v(109.59, -269.24) * mm});
            skLineSegment(sketch, "E964", {"start": v(109.59, -269.24) * mm, "end": v(109.16, -269.02) * mm});
            skLineSegment(sketch, "E965", {"start": v(109.16, -269.02) * mm, "end": v(108.73, -268.8) * mm});
            skLineSegment(sketch, "E966", {"start": v(108.73, -268.8) * mm, "end": v(107.75, -268.8) * mm});
            skLineSegment(sketch, "E967", {"start": v(107.75, -268.8) * mm, "end": v(107.32, -269.02) * mm});
            skLineSegment(sketch, "E968", {"start": v(107.32, -269.02) * mm, "end": v(106.88, -269.24) * mm});
            skLineSegment(sketch, "E969", {"start": v(106.88, -269.24) * mm, "end": v(106.56, -269.57) * mm});
            skLineSegment(sketch, "E970", {"start": v(106.56, -269.57) * mm, "end": v(106.23, -270) * mm});
            skLineSegment(sketch, "E971", {"start": v(106.23, -270) * mm, "end": v(106.13, -270.43) * mm});
            skLineSegment(sketch, "E972", {"start": v(106.13, -270.43) * mm, "end": v(106.02, -270.97) * mm});
            skLineSegment(sketch, "E973", {"start": v(242.94, -270.97) * mm, "end": v(242.94, -274.33) * mm});
            skLineSegment(sketch, "E974", {"start": v(242.94, -274.33) * mm, "end": v(248.57, -274.33) * mm});
            skLineSegment(sketch, "E975", {"start": v(248.57, -274.33) * mm, "end": v(248.57, -271.4) * mm});
            skLineSegment(sketch, "E976", {"start": v(248.57, -271.4) * mm, "end": v(248.57, -270.32) * mm});
            skLineSegment(sketch, "E977", {"start": v(248.57, -270.32) * mm, "end": v(248.35, -269.35) * mm});
            skLineSegment(sketch, "E978", {"start": v(248.35, -269.35) * mm, "end": v(248.03, -268.37) * mm});
            skLineSegment(sketch, "E979", {"start": v(248.03, -268.37) * mm, "end": v(247.48, -267.5) * mm});
            skLineSegment(sketch, "E980", {"start": v(247.48, -267.5) * mm, "end": v(246.94, -266.64) * mm});
            skLineSegment(sketch, "E981", {"start": v(246.94, -266.64) * mm, "end": v(246.3, -265.88) * mm});
            skLineSegment(sketch, "E982", {"start": v(246.3, -265.88) * mm, "end": v(245.54, -265.24) * mm});
            skLineSegment(sketch, "E983", {"start": v(245.54, -265.24) * mm, "end": v(244.67, -264.59) * mm});
            skLineSegment(sketch, "E984", {"start": v(244.67, -264.59) * mm, "end": v(243.8, -264.15) * mm});
            skLineSegment(sketch, "E985", {"start": v(243.8, -264.15) * mm, "end": v(242.83, -263.83) * mm});
            skLineSegment(sketch, "E986", {"start": v(242.83, -263.83) * mm, "end": v(241.75, -263.61) * mm});
            skLineSegment(sketch, "E987", {"start": v(241.75, -263.61) * mm, "end": v(239.8, -263.61) * mm});
            skLineSegment(sketch, "E988", {"start": v(239.8, -263.61) * mm, "end": v(238.72, -263.83) * mm});
            skLineSegment(sketch, "E989", {"start": v(238.72, -263.83) * mm, "end": v(237.74, -264.15) * mm});
            skLineSegment(sketch, "E990", {"start": v(237.74, -264.15) * mm, "end": v(236.88, -264.59) * mm});
            skLineSegment(sketch, "E991", {"start": v(236.88, -264.59) * mm, "end": v(236.01, -265.24) * mm});
            skLineSegment(sketch, "E992", {"start": v(236.01, -265.24) * mm, "end": v(235.25, -265.88) * mm});
            skLineSegment(sketch, "E993", {"start": v(235.25, -265.88) * mm, "end": v(234.6, -266.64) * mm});
            skLineSegment(sketch, "E994", {"start": v(234.6, -266.64) * mm, "end": v(234.07, -267.5) * mm});
            skLineSegment(sketch, "E995", {"start": v(234.07, -267.5) * mm, "end": v(233.52, -268.37) * mm});
            skLineSegment(sketch, "E996", {"start": v(233.52, -268.37) * mm, "end": v(233.2, -269.35) * mm});
            skLineSegment(sketch, "E997", {"start": v(233.2, -269.35) * mm, "end": v(233.09, -270.32) * mm});
            skLineSegment(sketch, "E998", {"start": v(233.09, -270.32) * mm, "end": v(232.98, -271.4) * mm});
            skLineSegment(sketch, "E999", {"start": v(232.98, -271.4) * mm, "end": v(232.98, -274.33) * mm});
            skLineSegment(sketch, "E1000", {"start": v(232.98, -274.33) * mm, "end": v(233.52, -276.28) * mm});
            skLineSegment(sketch, "E1001", {"start": v(233.52, -276.28) * mm, "end": v(234.28, -278.22) * mm});
            skLineSegment(sketch, "E1002", {"start": v(234.28, -278.22) * mm, "end": v(235.14, -280.06) * mm});
            skLineSegment(sketch, "E1003", {"start": v(235.14, -280.06) * mm, "end": v(236.12, -281.9) * mm});
            skLineSegment(sketch, "E1004", {"start": v(236.12, -281.9) * mm, "end": v(237.2, -283.64) * mm});
            skLineSegment(sketch, "E1005", {"start": v(237.2, -283.64) * mm, "end": v(238.5, -285.26) * mm});
            skLineSegment(sketch, "E1006", {"start": v(243.37, -293.49) * mm, "end": v(241, -289.37) * mm});
            skLineSegment(sketch, "E1007", {"start": v(241, -289.37) * mm, "end": v(238.5, -285.26) * mm});
            skLineSegment(sketch, "E1008", {"start": v(243.37, -293.49) * mm, "end": v(243.37, -297.49) * mm});
            skLineSegment(sketch, "E1009", {"start": v(237.63, -298.14) * mm, "end": v(237.85, -298.68) * mm});
            skLineSegment(sketch, "E1010", {"start": v(237.85, -298.68) * mm, "end": v(238.07, -299.22) * mm});
            skLineSegment(sketch, "E1011", {"start": v(238.07, -299.22) * mm, "end": v(238.5, -299.65) * mm});
            skLineSegment(sketch, "E1012", {"start": v(238.5, -299.65) * mm, "end": v(238.93, -299.98) * mm});
            skLineSegment(sketch, "E1013", {"start": v(238.93, -299.98) * mm, "end": v(239.48, -300.2) * mm});
            skLineSegment(sketch, "E1014", {"start": v(239.48, -300.2) * mm, "end": v(240.02, -300.3) * mm});
            skLineSegment(sketch, "E1015", {"start": v(240.02, -300.3) * mm, "end": v(240.55, -300.41) * mm});
            skLineSegment(sketch, "E1016", {"start": v(240.55, -300.41) * mm, "end": v(241.1, -300.3) * mm});
            skLineSegment(sketch, "E1017", {"start": v(241.1, -300.3) * mm, "end": v(241.64, -300.2) * mm});
            skLineSegment(sketch, "E1018", {"start": v(241.64, -300.2) * mm, "end": v(242.07, -299.87) * mm});
            skLineSegment(sketch, "E1019", {"start": v(242.07, -299.87) * mm, "end": v(242.5, -299.55) * mm});
            skLineSegment(sketch, "E1020", {"start": v(242.5, -299.55) * mm, "end": v(242.94, -299.11) * mm});
            skLineSegment(sketch, "E1021", {"start": v(242.94, -299.11) * mm, "end": v(243.16, -298.57) * mm});
            skLineSegment(sketch, "E1022", {"start": v(243.16, -298.57) * mm, "end": v(243.37, -297.49) * mm});
            skLineSegment(sketch, "E1023", {"start": v(237.63, -298.14) * mm, "end": v(237.63, -293.49) * mm});
            skLineSegment(sketch, "E1024", {"start": v(237.63, -293.49) * mm, "end": v(232.12, -293.49) * mm});
            skLineSegment(sketch, "E1025", {"start": v(232.12, -293.49) * mm, "end": v(232.12, -297.7) * mm});
            skLineSegment(sketch, "E1026", {"start": v(232.12, -297.7) * mm, "end": v(232.22, -298.68) * mm});
            skLineSegment(sketch, "E1027", {"start": v(232.22, -298.68) * mm, "end": v(232.44, -299.65) * mm});
            skLineSegment(sketch, "E1028", {"start": v(232.44, -299.65) * mm, "end": v(232.76, -300.63) * mm});
            skLineSegment(sketch, "E1029", {"start": v(232.76, -300.63) * mm, "end": v(233.2, -301.5) * mm});
            skLineSegment(sketch, "E1030", {"start": v(233.2, -301.5) * mm, "end": v(233.85, -302.36) * mm});
            skLineSegment(sketch, "E1031", {"start": v(233.85, -302.36) * mm, "end": v(234.5, -303.12) * mm});
            skLineSegment(sketch, "E1032", {"start": v(234.5, -303.12) * mm, "end": v(235.25, -303.77) * mm});
            skLineSegment(sketch, "E1033", {"start": v(235.25, -303.77) * mm, "end": v(236.01, -304.3) * mm});
            skLineSegment(sketch, "E1034", {"start": v(236.01, -304.3) * mm, "end": v(236.88, -304.85) * mm});
            skLineSegment(sketch, "E1035", {"start": v(236.88, -304.85) * mm, "end": v(237.85, -305.18) * mm});
            skLineSegment(sketch, "E1036", {"start": v(237.85, -305.18) * mm, "end": v(238.83, -305.4) * mm});
            skLineSegment(sketch, "E1037", {"start": v(238.83, -305.4) * mm, "end": v(239.8, -305.5) * mm});
            skLineSegment(sketch, "E1038", {"start": v(239.8, -305.5) * mm, "end": v(240.77, -305.5) * mm});
            skLineSegment(sketch, "E1039", {"start": v(240.77, -305.5) * mm, "end": v(241.86, -305.4) * mm});
            skLineSegment(sketch, "E1040", {"start": v(241.86, -305.4) * mm, "end": v(242.83, -305.18) * mm});
            skLineSegment(sketch, "E1041", {"start": v(242.83, -305.18) * mm, "end": v(243.7, -304.85) * mm});
            skLineSegment(sketch, "E1042", {"start": v(243.7, -304.85) * mm, "end": v(244.67, -304.3) * mm});
            skLineSegment(sketch, "E1043", {"start": v(244.67, -304.3) * mm, "end": v(245.43, -303.77) * mm});
            skLineSegment(sketch, "E1044", {"start": v(245.43, -303.77) * mm, "end": v(246.19, -303.12) * mm});
            skLineSegment(sketch, "E1045", {"start": v(246.19, -303.12) * mm, "end": v(246.83, -302.36) * mm});
            skLineSegment(sketch, "E1046", {"start": v(246.83, -302.36) * mm, "end": v(247.38, -301.5) * mm});
            skLineSegment(sketch, "E1047", {"start": v(247.38, -301.5) * mm, "end": v(247.92, -300.63) * mm});
            skLineSegment(sketch, "E1048", {"start": v(247.92, -300.63) * mm, "end": v(248.24, -299.65) * mm});
            skLineSegment(sketch, "E1049", {"start": v(248.24, -299.65) * mm, "end": v(248.46, -298.68) * mm});
            skLineSegment(sketch, "E1050", {"start": v(248.46, -298.68) * mm, "end": v(248.57, -297.7) * mm});
            skLineSegment(sketch, "E1051", {"start": v(248.57, -297.7) * mm, "end": v(248.57, -293.49) * mm});
            skLineSegment(sketch, "E1052", {"start": v(248.57, -293.49) * mm, "end": v(247.92, -291.43) * mm});
            skLineSegment(sketch, "E1053", {"start": v(247.92, -291.43) * mm, "end": v(247.16, -289.37) * mm});
            skLineSegment(sketch, "E1054", {"start": v(247.16, -289.37) * mm, "end": v(246.3, -287.42) * mm});
            skLineSegment(sketch, "E1055", {"start": v(246.3, -287.42) * mm, "end": v(245.32, -285.48) * mm});
            skLineSegment(sketch, "E1056", {"start": v(245.32, -285.48) * mm, "end": v(244.24, -283.64) * mm});
            skLineSegment(sketch, "E1057", {"start": v(244.24, -283.64) * mm, "end": v(242.94, -281.9) * mm});
            skLineSegment(sketch, "E1058", {"start": v(238.6, -274.33) * mm, "end": v(239.48, -276.38) * mm});
            skLineSegment(sketch, "E1059", {"start": v(239.48, -276.38) * mm, "end": v(240.55, -278.22) * mm});
            skLineSegment(sketch, "E1060", {"start": v(240.55, -278.22) * mm, "end": v(241.64, -280.06) * mm});
            skLineSegment(sketch, "E1061", {"start": v(241.64, -280.06) * mm, "end": v(242.94, -281.9) * mm});
            skLineSegment(sketch, "E1062", {"start": v(238.6, -274.33) * mm, "end": v(238.6, -270.97) * mm});
            skLineSegment(sketch, "E1063", {"start": v(242.94, -270.97) * mm, "end": v(242.94, -270.43) * mm});
            skLineSegment(sketch, "E1064", {"start": v(242.94, -270.43) * mm, "end": v(242.72, -270) * mm});
            skLineSegment(sketch, "E1065", {"start": v(242.72, -270) * mm, "end": v(242.5, -269.57) * mm});
            skLineSegment(sketch, "E1066", {"start": v(242.5, -269.57) * mm, "end": v(242.18, -269.24) * mm});
            skLineSegment(sketch, "E1067", {"start": v(242.18, -269.24) * mm, "end": v(241.75, -269.02) * mm});
            skLineSegment(sketch, "E1068", {"start": v(241.75, -269.02) * mm, "end": v(241.2, -268.8) * mm});
            skLineSegment(sketch, "E1069", {"start": v(241.2, -268.8) * mm, "end": v(240.34, -268.8) * mm});
            skLineSegment(sketch, "E1070", {"start": v(240.34, -268.8) * mm, "end": v(239.8, -269.02) * mm});
            skLineSegment(sketch, "E1071", {"start": v(239.8, -269.02) * mm, "end": v(239.48, -269.24) * mm});
            skLineSegment(sketch, "E1072", {"start": v(239.48, -269.24) * mm, "end": v(239.04, -269.57) * mm});
            skLineSegment(sketch, "E1073", {"start": v(239.04, -269.57) * mm, "end": v(238.83, -270) * mm});
            skLineSegment(sketch, "E1074", {"start": v(238.83, -270) * mm, "end": v(238.6, -270.43) * mm});
            skLineSegment(sketch, "E1075", {"start": v(238.6, -270.43) * mm, "end": v(238.6, -270.97) * mm});
            skLineSegment(sketch, "E1076", {"start": v(-105.48, -274.44) * mm, "end": v(-103.1, -290.89) * mm});
            skLineSegment(sketch, "E1077", {"start": v(-103.1, -290.89) * mm, "end": v(-107.86, -290.89) * mm});
            skLineSegment(sketch, "E1078", {"start": v(-107.86, -290.89) * mm, "end": v(-105.48, -274.44) * mm});
            skLineSegment(sketch, "E1079", {"start": v(-101.8, -263.61) * mm, "end": v(-109.16, -263.61) * mm});
            skLineSegment(sketch, "E1080", {"start": v(-109.16, -263.61) * mm, "end": v(-115.22, -305.5) * mm});
            skLineSegment(sketch, "E1081", {"start": v(-115.22, -305.5) * mm, "end": v(-110.02, -305.5) * mm});
            skLineSegment(sketch, "E1082", {"start": v(-110.02, -305.5) * mm, "end": v(-108.72, -297.27) * mm});
            skLineSegment(sketch, "E1083", {"start": v(-108.72, -297.27) * mm, "end": v(-102.12, -297.27) * mm});
            skLineSegment(sketch, "E1084", {"start": v(-102.12, -297.27) * mm, "end": v(-100.93, -305.5) * mm});
            skLineSegment(sketch, "E1085", {"start": v(-100.93, -305.5) * mm, "end": v(-95.63, -305.5) * mm});
            skLineSegment(sketch, "E1086", {"start": v(-95.63, -305.5) * mm, "end": v(-101.8, -263.61) * mm});
            skLineSegment(sketch, "E1087", {"start": v(191.74, -263.61) * mm, "end": v(185.9, -263.61) * mm});
            skLineSegment(sketch, "E1088", {"start": v(185.9, -263.61) * mm, "end": v(185.9, -305.5) * mm});
            skLineSegment(sketch, "E1089", {"start": v(185.9, -305.5) * mm, "end": v(199.75, -305.5) * mm});
            skLineSegment(sketch, "E1090", {"start": v(199.75, -305.5) * mm, "end": v(199.75, -300.3) * mm});
            skLineSegment(sketch, "E1091", {"start": v(199.75, -300.3) * mm, "end": v(191.74, -300.3) * mm});
            skLineSegment(sketch, "E1092", {"start": v(191.74, -300.3) * mm, "end": v(191.74, -263.61) * mm});
            skLineSegment(sketch, "E1093", {"start": v(217.07, -270.97) * mm, "end": v(217.07, -298.14) * mm});
            skLineSegment(sketch, "E1094", {"start": v(212.74, -298.14) * mm, "end": v(212.74, -298.68) * mm});
            skLineSegment(sketch, "E1095", {"start": v(212.74, -298.68) * mm, "end": v(212.96, -299.11) * mm});
            skLineSegment(sketch, "E1096", {"start": v(212.96, -299.11) * mm, "end": v(213.17, -299.55) * mm});
            skLineSegment(sketch, "E1097", {"start": v(213.17, -299.55) * mm, "end": v(213.6, -299.87) * mm});
            skLineSegment(sketch, "E1098", {"start": v(213.6, -299.87) * mm, "end": v(213.93, -300.09) * mm});
            skLineSegment(sketch, "E1099", {"start": v(213.93, -300.09) * mm, "end": v(214.47, -300.3) * mm});
            skLineSegment(sketch, "E1100", {"start": v(214.47, -300.3) * mm, "end": v(215.45, -300.3) * mm});
            skLineSegment(sketch, "E1101", {"start": v(215.45, -300.3) * mm, "end": v(215.88, -300.09) * mm});
            skLineSegment(sketch, "E1102", {"start": v(215.88, -300.09) * mm, "end": v(216.31, -299.87) * mm});
            skLineSegment(sketch, "E1103", {"start": v(216.31, -299.87) * mm, "end": v(216.64, -299.55) * mm});
            skLineSegment(sketch, "E1104", {"start": v(216.64, -299.55) * mm, "end": v(216.85, -299.11) * mm});
            skLineSegment(sketch, "E1105", {"start": v(216.85, -299.11) * mm, "end": v(217.07, -298.68) * mm});
            skLineSegment(sketch, "E1106", {"start": v(217.07, -298.68) * mm, "end": v(217.07, -298.14) * mm});
            skLineSegment(sketch, "E1107", {"start": v(212.74, -298.14) * mm, "end": v(212.74, -270.97) * mm});
            skLineSegment(sketch, "E1108", {"start": v(217.07, -270.97) * mm, "end": v(217.07, -270.43) * mm});
            skLineSegment(sketch, "E1109", {"start": v(217.07, -270.43) * mm, "end": v(216.64, -269.57) * mm});
            skLineSegment(sketch, "E1110", {"start": v(216.64, -269.57) * mm, "end": v(216.31, -269.24) * mm});
            skLineSegment(sketch, "E1111", {"start": v(216.31, -269.24) * mm, "end": v(215.88, -269.02) * mm});
            skLineSegment(sketch, "E1112", {"start": v(215.88, -269.02) * mm, "end": v(215.45, -268.8) * mm});
            skLineSegment(sketch, "E1113", {"start": v(215.45, -268.8) * mm, "end": v(214.47, -268.8) * mm});
            skLineSegment(sketch, "E1114", {"start": v(214.47, -268.8) * mm, "end": v(213.93, -269.02) * mm});
            skLineSegment(sketch, "E1115", {"start": v(213.93, -269.02) * mm, "end": v(213.6, -269.24) * mm});
            skLineSegment(sketch, "E1116", {"start": v(213.6, -269.24) * mm, "end": v(213.17, -269.57) * mm});
            skLineSegment(sketch, "E1117", {"start": v(213.17, -269.57) * mm, "end": v(212.96, -270) * mm});
            skLineSegment(sketch, "E1118", {"start": v(212.96, -270) * mm, "end": v(212.74, -270.43) * mm});
            skLineSegment(sketch, "E1119", {"start": v(212.74, -270.43) * mm, "end": v(212.74, -270.97) * mm});
            skLineSegment(sketch, "E1120", {"start": v(207.11, -271.4) * mm, "end": v(207.11, -297.7) * mm});
            skLineSegment(sketch, "E1121", {"start": v(207.11, -297.7) * mm, "end": v(207.22, -298.79) * mm});
            skLineSegment(sketch, "E1122", {"start": v(207.22, -298.79) * mm, "end": v(207.33, -299.76) * mm});
            skLineSegment(sketch, "E1123", {"start": v(207.33, -299.76) * mm, "end": v(207.65, -300.74) * mm});
            skLineSegment(sketch, "E1124", {"start": v(207.65, -300.74) * mm, "end": v(208.74, -302.47) * mm});
            skLineSegment(sketch, "E1125", {"start": v(208.74, -302.47) * mm, "end": v(209.39, -303.23) * mm});
            skLineSegment(sketch, "E1126", {"start": v(209.39, -303.23) * mm, "end": v(210.14, -303.98) * mm});
            skLineSegment(sketch, "E1127", {"start": v(210.14, -303.98) * mm, "end": v(211, -304.53) * mm});
            skLineSegment(sketch, "E1128", {"start": v(211, -304.53) * mm, "end": v(211.87, -304.96) * mm});
            skLineSegment(sketch, "E1129", {"start": v(211.87, -304.96) * mm, "end": v(212.85, -305.28) * mm});
            skLineSegment(sketch, "E1130", {"start": v(212.85, -305.28) * mm, "end": v(213.93, -305.5) * mm});
            skLineSegment(sketch, "E1131", {"start": v(213.93, -305.5) * mm, "end": v(215.88, -305.5) * mm});
            skLineSegment(sketch, "E1132", {"start": v(215.88, -305.5) * mm, "end": v(216.96, -305.28) * mm});
            skLineSegment(sketch, "E1133", {"start": v(216.96, -305.28) * mm, "end": v(217.94, -304.96) * mm});
            skLineSegment(sketch, "E1134", {"start": v(217.94, -304.96) * mm, "end": v(218.8, -304.53) * mm});
            skLineSegment(sketch, "E1135", {"start": v(218.8, -304.53) * mm, "end": v(219.67, -303.98) * mm});
            skLineSegment(sketch, "E1136", {"start": v(219.67, -303.98) * mm, "end": v(220.43, -303.23) * mm});
            skLineSegment(sketch, "E1137", {"start": v(220.43, -303.23) * mm, "end": v(221.08, -302.47) * mm});
            skLineSegment(sketch, "E1138", {"start": v(221.08, -302.47) * mm, "end": v(221.72, -301.6) * mm});
            skLineSegment(sketch, "E1139", {"start": v(221.72, -301.6) * mm, "end": v(222.16, -300.74) * mm});
            skLineSegment(sketch, "E1140", {"start": v(222.16, -300.74) * mm, "end": v(222.48, -299.76) * mm});
            skLineSegment(sketch, "E1141", {"start": v(222.48, -299.76) * mm, "end": v(222.7, -298.79) * mm});
            skLineSegment(sketch, "E1142", {"start": v(222.7, -298.79) * mm, "end": v(222.7, -297.7) * mm});
            skLineSegment(sketch, "E1143", {"start": v(222.7, -297.7) * mm, "end": v(222.7, -271.4) * mm});
            skLineSegment(sketch, "E1144", {"start": v(222.7, -271.4) * mm, "end": v(222.7, -270.32) * mm});
            skLineSegment(sketch, "E1145", {"start": v(222.7, -270.32) * mm, "end": v(222.48, -269.35) * mm});
            skLineSegment(sketch, "E1146", {"start": v(222.48, -269.35) * mm, "end": v(222.16, -268.37) * mm});
            skLineSegment(sketch, "E1147", {"start": v(222.16, -268.37) * mm, "end": v(221.72, -267.5) * mm});
            skLineSegment(sketch, "E1148", {"start": v(221.72, -267.5) * mm, "end": v(221.08, -266.64) * mm});
            skLineSegment(sketch, "E1149", {"start": v(221.08, -266.64) * mm, "end": v(220.43, -265.88) * mm});
            skLineSegment(sketch, "E1150", {"start": v(220.43, -265.88) * mm, "end": v(219.67, -265.13) * mm});
            skLineSegment(sketch, "E1151", {"start": v(219.67, -265.13) * mm, "end": v(218.8, -264.59) * mm});
            skLineSegment(sketch, "E1152", {"start": v(218.8, -264.59) * mm, "end": v(217.94, -264.15) * mm});
            skLineSegment(sketch, "E1153", {"start": v(217.94, -264.15) * mm, "end": v(216.96, -263.83) * mm});
            skLineSegment(sketch, "E1154", {"start": v(216.96, -263.83) * mm, "end": v(215.88, -263.61) * mm});
            skLineSegment(sketch, "E1155", {"start": v(215.88, -263.61) * mm, "end": v(213.93, -263.61) * mm});
            skLineSegment(sketch, "E1156", {"start": v(213.93, -263.61) * mm, "end": v(212.85, -263.83) * mm});
            skLineSegment(sketch, "E1157", {"start": v(212.85, -263.83) * mm, "end": v(211.87, -264.15) * mm});
            skLineSegment(sketch, "E1158", {"start": v(211.87, -264.15) * mm, "end": v(211, -264.59) * mm});
            skLineSegment(sketch, "E1159", {"start": v(211, -264.59) * mm, "end": v(210.14, -265.13) * mm});
            skLineSegment(sketch, "E1160", {"start": v(210.14, -265.13) * mm, "end": v(209.39, -265.88) * mm});
            skLineSegment(sketch, "E1161", {"start": v(209.39, -265.88) * mm, "end": v(208.74, -266.64) * mm});
            skLineSegment(sketch, "E1162", {"start": v(208.74, -266.64) * mm, "end": v(208.2, -267.5) * mm});
            skLineSegment(sketch, "E1163", {"start": v(208.2, -267.5) * mm, "end": v(207.65, -268.37) * mm});
            skLineSegment(sketch, "E1164", {"start": v(207.65, -268.37) * mm, "end": v(207.33, -269.35) * mm});
            skLineSegment(sketch, "E1165", {"start": v(207.33, -269.35) * mm, "end": v(207.22, -270.32) * mm});
            skLineSegment(sketch, "E1166", {"start": v(207.22, -270.32) * mm, "end": v(207.11, -271.4) * mm});
            skLineSegment(sketch, "E1167", {"start": v(-80.58, -263.61) * mm, "end": v(-87.4, -263.61) * mm});
            skLineSegment(sketch, "E1168", {"start": v(-87.4, -263.61) * mm, "end": v(-87.4, -305.5) * mm});
            skLineSegment(sketch, "E1169", {"start": v(-87.4, -305.5) * mm, "end": v(-82.31, -305.5) * mm});
            skLineSegment(sketch, "E1170", {"start": v(-82.31, -305.5) * mm, "end": v(-82.31, -277.25) * mm});
            skLineSegment(sketch, "E1171", {"start": v(-82.31, -277.25) * mm, "end": v(-81.77, -277.25) * mm});
            skLineSegment(sketch, "E1172", {"start": v(-81.77, -277.25) * mm, "end": v(-77.55, -305.5) * mm});
            skLineSegment(sketch, "E1173", {"start": v(-77.55, -305.5) * mm, "end": v(-75.17, -305.5) * mm});
            skLineSegment(sketch, "E1174", {"start": v(-75.17, -305.5) * mm, "end": v(-70.95, -277.25) * mm});
            skLineSegment(sketch, "E1175", {"start": v(-70.95, -277.25) * mm, "end": v(-70.52, -277.25) * mm});
            skLineSegment(sketch, "E1176", {"start": v(-70.52, -277.25) * mm, "end": v(-70.52, -305.5) * mm});
            skLineSegment(sketch, "E1177", {"start": v(-70.52, -305.5) * mm, "end": v(-65.32, -305.5) * mm});
            skLineSegment(sketch, "E1178", {"start": v(-65.32, -305.5) * mm, "end": v(-65.32, -263.61) * mm});
            skLineSegment(sketch, "E1179", {"start": v(-65.32, -263.61) * mm, "end": v(-72.14, -263.61) * mm});
            skLineSegment(sketch, "E1180", {"start": v(-72.14, -263.61) * mm, "end": v(-75.93, -284.83) * mm});
            skLineSegment(sketch, "E1181", {"start": v(-75.93, -284.83) * mm, "end": v(-76.8, -284.83) * mm});
            skLineSegment(sketch, "E1182", {"start": v(-76.8, -284.83) * mm, "end": v(-80.58, -263.61) * mm});
            skLineSegment(sketch, "E1183", {"start": v(-27.65, -263.61) * mm, "end": v(-33.17, -263.61) * mm});
            skLineSegment(sketch, "E1184", {"start": v(-33.17, -263.61) * mm, "end": v(-33.17, -305.5) * mm});
            skLineSegment(sketch, "E1185", {"start": v(-33.17, -305.5) * mm, "end": v(-27.65, -305.5) * mm});
            skLineSegment(sketch, "E1186", {"start": v(-27.65, -305.5) * mm, "end": v(-27.65, -281.9) * mm});
            skLineSegment(sketch, "E1187", {"start": v(-27.65, -281.9) * mm, "end": v(-27, -281.9) * mm});
            skLineSegment(sketch, "E1188", {"start": v(-27, -281.9) * mm, "end": v(-20.73, -305.5) * mm});
            skLineSegment(sketch, "E1189", {"start": v(-20.73, -305.5) * mm, "end": v(-15.53, -305.5) * mm});
            skLineSegment(sketch, "E1190", {"start": v(-15.53, -305.5) * mm, "end": v(-15.53, -263.61) * mm});
            skLineSegment(sketch, "E1191", {"start": v(-15.53, -263.61) * mm, "end": v(-20.73, -263.61) * mm});
            skLineSegment(sketch, "E1192", {"start": v(-20.73, -263.61) * mm, "end": v(-20.73, -287.75) * mm});
            skLineSegment(sketch, "E1193", {"start": v(-20.73, -287.75) * mm, "end": v(-21.38, -287.75) * mm});
            skLineSegment(sketch, "E1194", {"start": v(-21.38, -287.75) * mm, "end": v(-27.65, -263.61) * mm});
            skLineSegment(sketch, "E1195", {"start": v(-0.05, 391.55) * mm, "end": v(-13.58, 391.55) * mm});
            skLineSegment(sketch, "E1196", {"start": v(-13.58, 391.55) * mm, "end": v(-13.58, 298.68) * mm});
            skLineSegment(sketch, "E1197", {"start": v(-13.58, 298.68) * mm, "end": v(-0.05, 298.68) * mm});
            skLineSegment(sketch, "E1198", {"start": v(-0.05, 298.68) * mm, "end": v(-0.05, 333.2) * mm});
            skLineSegment(sketch, "E1199", {"start": v(-0.05, 333.2) * mm, "end": v(3.84, 341.54) * mm});
            skLineSegment(sketch, "E1200", {"start": v(3.84, 341.54) * mm, "end": v(14.01, 298.68) * mm});
            skLineSegment(sketch, "E1201", {"start": v(14.01, 298.68) * mm, "end": v(27.22, 298.68) * mm});
            skLineSegment(sketch, "E1202", {"start": v(27.22, 298.68) * mm, "end": v(12.61, 360.16) * mm});
            skLineSegment(sketch, "E1203", {"start": v(12.61, 360.16) * mm, "end": v(25.17, 391.55) * mm});
            skLineSegment(sketch, "E1204", {"start": v(25.17, 391.55) * mm, "end": v(12.5, 391.55) * mm});
            skLineSegment(sketch, "E1205", {"start": v(12.5, 391.55) * mm, "end": v(-0.05, 357.34) * mm});
            skLineSegment(sketch, "E1206", {"start": v(-0.05, 357.34) * mm, "end": v(-0.05, 391.55) * mm});
            skLineSegment(sketch, "E1207", {"start": v(103.53, 391.55) * mm, "end": v(90.1, 391.55) * mm});
            skLineSegment(sketch, "E1208", {"start": v(90.1, 391.55) * mm, "end": v(90.1, 298.68) * mm});
            skLineSegment(sketch, "E1209", {"start": v(90.1, 298.68) * mm, "end": v(103.53, 298.68) * mm});
            skLineSegment(sketch, "E1210", {"start": v(103.53, 298.68) * mm, "end": v(103.53, 333.2) * mm});
            skLineSegment(sketch, "E1211", {"start": v(103.53, 333.2) * mm, "end": v(107.53, 341.54) * mm});
            skLineSegment(sketch, "E1212", {"start": v(107.53, 341.54) * mm, "end": v(117.6, 298.68) * mm});
            skLineSegment(sketch, "E1213", {"start": v(117.6, 298.68) * mm, "end": v(130.8, 298.68) * mm});
            skLineSegment(sketch, "E1214", {"start": v(130.8, 298.68) * mm, "end": v(116.3, 360.16) * mm});
            skLineSegment(sketch, "E1215", {"start": v(116.3, 360.16) * mm, "end": v(128.75, 391.55) * mm});
            skLineSegment(sketch, "E1216", {"start": v(128.75, 391.55) * mm, "end": v(116.08, 391.55) * mm});
            skLineSegment(sketch, "E1217", {"start": v(116.08, 391.55) * mm, "end": v(103.53, 357.34) * mm});
            skLineSegment(sketch, "E1218", {"start": v(103.53, 357.34) * mm, "end": v(103.53, 391.55) * mm});
            skLineSegment(sketch, "E1219", {"start": v(56.88, 367.4) * mm, "end": v(62.18, 331.15) * mm});
            skLineSegment(sketch, "E1220", {"start": v(62.18, 331.15) * mm, "end": v(51.69, 331.15) * mm});
            skLineSegment(sketch, "E1221", {"start": v(51.69, 331.15) * mm, "end": v(56.88, 367.4) * mm});
            skLineSegment(sketch, "E1222", {"start": v(65.1, 391.55) * mm, "end": v(48.76, 391.55) * mm});
            skLineSegment(sketch, "E1223", {"start": v(48.76, 391.55) * mm, "end": v(35.23, 298.68) * mm});
            skLineSegment(sketch, "E1224", {"start": v(35.23, 298.68) * mm, "end": v(46.92, 298.68) * mm});
            skLineSegment(sketch, "E1225", {"start": v(46.92, 298.68) * mm, "end": v(49.63, 317.08) * mm});
            skLineSegment(sketch, "E1226", {"start": v(49.63, 317.08) * mm, "end": v(64.24, 317.08) * mm});
            skLineSegment(sketch, "E1227", {"start": v(64.24, 317.08) * mm, "end": v(66.95, 298.68) * mm});
            skLineSegment(sketch, "E1228", {"start": v(66.95, 298.68) * mm, "end": v(78.63, 298.68) * mm});
            skLineSegment(sketch, "E1229", {"start": v(78.63, 298.68) * mm, "end": v(65.1, 391.55) * mm});
            skLineSegment(sketch, "E1230", {"start": v(159.92, 367.4) * mm, "end": v(165.23, 331.15) * mm});
            skLineSegment(sketch, "E1231", {"start": v(165.23, 331.15) * mm, "end": v(154.62, 331.15) * mm});
            skLineSegment(sketch, "E1232", {"start": v(154.62, 331.15) * mm, "end": v(159.92, 367.4) * mm});
            skLineSegment(sketch, "E1233", {"start": v(168.04, 391.55) * mm, "end": v(151.8, 391.55) * mm});
            skLineSegment(sketch, "E1234", {"start": v(151.8, 391.55) * mm, "end": v(138.16, 298.68) * mm});
            skLineSegment(sketch, "E1235", {"start": v(138.16, 298.68) * mm, "end": v(149.86, 298.68) * mm});
            skLineSegment(sketch, "E1236", {"start": v(149.86, 298.68) * mm, "end": v(152.56, 317.08) * mm});
            skLineSegment(sketch, "E1237", {"start": v(152.56, 317.08) * mm, "end": v(167.28, 317.08) * mm});
            skLineSegment(sketch, "E1238", {"start": v(167.28, 317.08) * mm, "end": v(169.88, 298.68) * mm});
            skLineSegment(sketch, "E1239", {"start": v(169.88, 298.68) * mm, "end": v(181.57, 298.68) * mm});
            skLineSegment(sketch, "E1240", {"start": v(181.57, 298.68) * mm, "end": v(168.04, 391.55) * mm});
            skLineSegment(sketch, "E1241", {"start": v(-78.42, 391.55) * mm, "end": v(-62.07, 391.55) * mm});
            skLineSegment(sketch, "E1242", {"start": v(-70.19, 367.4) * mm, "end": v(-64.89, 331.15) * mm});
            skLineSegment(sketch, "E1243", {"start": v(-64.89, 331.15) * mm, "end": v(-75.5, 331.15) * mm});
            skLineSegment(sketch, "E1244", {"start": v(-75.5, 331.15) * mm, "end": v(-70.19, 367.4) * mm});
            skLineSegment(sketch, "E1245", {"start": v(-62.07, 391.55) * mm, "end": v(-78.42, 391.55) * mm});
            skLineSegment(sketch, "E1246", {"start": v(-78.42, 391.55) * mm, "end": v(-91.95, 298.68) * mm});
            skLineSegment(sketch, "E1247", {"start": v(-91.95, 298.68) * mm, "end": v(-80.26, 298.68) * mm});
            skLineSegment(sketch, "E1248", {"start": v(-80.26, 298.68) * mm, "end": v(-77.55, 317.08) * mm});
            skLineSegment(sketch, "E1249", {"start": v(-77.55, 317.08) * mm, "end": v(-62.83, 317.08) * mm});
            skLineSegment(sketch, "E1250", {"start": v(-62.83, 317.08) * mm, "end": v(-60.23, 298.68) * mm});
            skLineSegment(sketch, "E1251", {"start": v(-60.23, 298.68) * mm, "end": v(-48.54, 298.68) * mm});
            skLineSegment(sketch, "E1252", {"start": v(-48.54, 298.68) * mm, "end": v(-62.07, 391.55) * mm});
            skLineSegment(sketch, "E1253", {"start": v(-171.5, 391.55) * mm, "end": v(-155.16, 391.55) * mm});
            skLineSegment(sketch, "E1254", {"start": v(-163.27, 367.4) * mm, "end": v(-158.08, 331.15) * mm});
            skLineSegment(sketch, "E1255", {"start": v(-158.08, 331.15) * mm, "end": v(-168.58, 331.15) * mm});
            skLineSegment(sketch, "E1256", {"start": v(-168.58, 331.15) * mm, "end": v(-163.27, 367.4) * mm});
            skLineSegment(sketch, "E1257", {"start": v(-155.16, 391.55) * mm, "end": v(-171.5, 391.55) * mm});
            skLineSegment(sketch, "E1258", {"start": v(-171.5, 391.55) * mm, "end": v(-185.03, 298.68) * mm});
            skLineSegment(sketch, "E1259", {"start": v(-185.03, 298.68) * mm, "end": v(-173.34, 298.68) * mm});
            skLineSegment(sketch, "E1260", {"start": v(-173.34, 298.68) * mm, "end": v(-170.64, 317.08) * mm});
            skLineSegment(sketch, "E1261", {"start": v(-170.64, 317.08) * mm, "end": v(-156.02, 317.08) * mm});
            skLineSegment(sketch, "E1262", {"start": v(-156.02, 317.08) * mm, "end": v(-153.32, 298.68) * mm});
            skLineSegment(sketch, "E1263", {"start": v(-153.32, 298.68) * mm, "end": v(-141.63, 298.68) * mm});
            skLineSegment(sketch, "E1264", {"start": v(-141.63, 298.68) * mm, "end": v(-155.16, 391.55) * mm});
            skLineSegment(sketch, "E1265", {"start": v(198.78, 391.55) * mm, "end": v(187.2, 391.55) * mm});
            skLineSegment(sketch, "E1266", {"start": v(187.2, 391.55) * mm, "end": v(199.53, 298.68) * mm});
            skLineSegment(sketch, "E1267", {"start": v(199.53, 298.68) * mm, "end": v(209.39, 298.68) * mm});
            skLineSegment(sketch, "E1268", {"start": v(209.39, 298.68) * mm, "end": v(216.85, 348.8) * mm});
            skLineSegment(sketch, "E1269", {"start": v(216.85, 348.8) * mm, "end": v(217.4, 348.8) * mm});
            skLineSegment(sketch, "E1270", {"start": v(217.4, 348.8) * mm, "end": v(224.86, 298.68) * mm});
            skLineSegment(sketch, "E1271", {"start": v(224.86, 298.68) * mm, "end": v(234.71, 298.68) * mm});
            skLineSegment(sketch, "E1272", {"start": v(234.71, 298.68) * mm, "end": v(246.94, 391.55) * mm});
            skLineSegment(sketch, "E1273", {"start": v(246.94, 391.55) * mm, "end": v(235.47, 391.55) * mm});
            skLineSegment(sketch, "E1274", {"start": v(235.47, 391.55) * mm, "end": v(229.3, 339.27) * mm});
            skLineSegment(sketch, "E1275", {"start": v(229.3, 339.27) * mm, "end": v(228.44, 339.27) * mm});
            skLineSegment(sketch, "E1276", {"start": v(228.44, 339.27) * mm, "end": v(221.94, 391.55) * mm});
            skLineSegment(sketch, "E1277", {"start": v(221.94, 391.55) * mm, "end": v(212.3, 391.55) * mm});
            skLineSegment(sketch, "E1278", {"start": v(212.3, 391.55) * mm, "end": v(205.81, 339.27) * mm});
            skLineSegment(sketch, "E1279", {"start": v(205.81, 339.27) * mm, "end": v(204.95, 339.27) * mm});
            skLineSegment(sketch, "E1280", {"start": v(204.95, 339.27) * mm, "end": v(198.78, 391.55) * mm});
            skLineSegment(sketch, "E1281", {"start": v(-96.82, 391.55) * mm, "end": v(-109.26, 391.55) * mm});
            skLineSegment(sketch, "E1282", {"start": v(-109.26, 391.55) * mm, "end": v(-116.4, 361.02) * mm});
            skLineSegment(sketch, "E1283", {"start": v(-116.4, 361.02) * mm, "end": v(-117.38, 361.02) * mm});
            skLineSegment(sketch, "E1284", {"start": v(-117.38, 361.02) * mm, "end": v(-124.85, 391.55) * mm});
            skLineSegment(sketch, "E1285", {"start": v(-124.85, 391.55) * mm, "end": v(-137.62, 391.55) * mm});
            skLineSegment(sketch, "E1286", {"start": v(-137.62, 391.55) * mm, "end": v(-124.1, 341) * mm});
            skLineSegment(sketch, "E1287", {"start": v(-124.1, 341) * mm, "end": v(-124.1, 298.68) * mm});
            skLineSegment(sketch, "E1288", {"start": v(-124.1, 298.68) * mm, "end": v(-110.24, 298.68) * mm});
            skLineSegment(sketch, "E1289", {"start": v(-110.24, 298.68) * mm, "end": v(-110.24, 341) * mm});
            skLineSegment(sketch, "E1290", {"start": v(-110.24, 341) * mm, "end": v(-96.82, 391.55) * mm});
            skLineSegment(sketch, "E1291", {"start": v(-231.36, 391.55) * mm, "end": v(-246.4, 391.55) * mm});
            skLineSegment(sketch, "E1292", {"start": v(-246.4, 391.55) * mm, "end": v(-246.4, 298.68) * mm});
            skLineSegment(sketch, "E1293", {"start": v(-246.4, 298.68) * mm, "end": v(-235.04, 298.68) * mm});
            skLineSegment(sketch, "E1294", {"start": v(-235.04, 298.68) * mm, "end": v(-235.04, 361.35) * mm});
            skLineSegment(sketch, "E1295", {"start": v(-235.04, 361.35) * mm, "end": v(-234.06, 361.35) * mm});
            skLineSegment(sketch, "E1296", {"start": v(-234.06, 361.35) * mm, "end": v(-224.75, 298.68) * mm});
            skLineSegment(sketch, "E1297", {"start": v(-224.75, 298.68) * mm, "end": v(-219.23, 298.68) * mm});
            skLineSegment(sketch, "E1298", {"start": v(-219.23, 298.68) * mm, "end": v(-209.93, 361.35) * mm});
            skLineSegment(sketch, "E1299", {"start": v(-209.93, 361.35) * mm, "end": v(-208.95, 361.35) * mm});
            skLineSegment(sketch, "E1300", {"start": v(-208.95, 361.35) * mm, "end": v(-208.95, 298.68) * mm});
            skLineSegment(sketch, "E1301", {"start": v(-208.95, 298.68) * mm, "end": v(-197.59, 298.68) * mm});
            skLineSegment(sketch, "E1302", {"start": v(-197.59, 298.68) * mm, "end": v(-197.59, 391.55) * mm});
            skLineSegment(sketch, "E1303", {"start": v(-197.59, 391.55) * mm, "end": v(-212.63, 391.55) * mm});
            skLineSegment(sketch, "E1304", {"start": v(-212.63, 391.55) * mm, "end": v(-221.07, 344.68) * mm});
            skLineSegment(sketch, "E1305", {"start": v(-221.07, 344.68) * mm, "end": v(-222.91, 344.68) * mm});
            skLineSegment(sketch, "E1306", {"start": v(-222.91, 344.68) * mm, "end": v(-231.36, 391.55) * mm});
            skLineSegment(sketch, "E1307", {"start": v(-202.13, 262.3) * mm, "end": v(-189.8, 262.3) * mm});
            skLineSegment(sketch, "E1308", {"start": v(-195.96, 244.02) * mm, "end": v(-192.07, 216.74) * mm});
            skLineSegment(sketch, "E1309", {"start": v(-192.07, 216.74) * mm, "end": v(-199.97, 216.74) * mm});
            skLineSegment(sketch, "E1310", {"start": v(-199.97, 216.74) * mm, "end": v(-195.96, 244.02) * mm});
            skLineSegment(sketch, "E1311", {"start": v(-189.8, 262.3) * mm, "end": v(-202.13, 262.3) * mm});
            skLineSegment(sketch, "E1312", {"start": v(-202.13, 262.3) * mm, "end": v(-212.41, 192.18) * mm});
            skLineSegment(sketch, "E1313", {"start": v(-212.41, 192.18) * mm, "end": v(-203.54, 192.18) * mm});
            skLineSegment(sketch, "E1314", {"start": v(-203.54, 192.18) * mm, "end": v(-201.6, 206.03) * mm});
            skLineSegment(sketch, "E1315", {"start": v(-201.6, 206.03) * mm, "end": v(-190.44, 206.03) * mm});
            skLineSegment(sketch, "E1316", {"start": v(-190.44, 206.03) * mm, "end": v(-188.39, 192.18) * mm});
            skLineSegment(sketch, "E1317", {"start": v(-188.39, 192.18) * mm, "end": v(-179.62, 192.18) * mm});
            skLineSegment(sketch, "E1318", {"start": v(-179.62, 192.18) * mm, "end": v(-189.8, 262.3) * mm});
            skLineSegment(sketch, "E1319", {"start": v(-124.96, 262.3) * mm, "end": v(-112.62, 262.3) * mm});
            skLineSegment(sketch, "E1320", {"start": v(-118.79, 244.02) * mm, "end": v(-114.78, 216.74) * mm});
            skLineSegment(sketch, "E1321", {"start": v(-114.78, 216.74) * mm, "end": v(-122.8, 216.74) * mm});
            skLineSegment(sketch, "E1322", {"start": v(-122.8, 216.74) * mm, "end": v(-118.79, 244.02) * mm});
            skLineSegment(sketch, "E1323", {"start": v(-112.62, 262.3) * mm, "end": v(-124.96, 262.3) * mm});
            skLineSegment(sketch, "E1324", {"start": v(-124.96, 262.3) * mm, "end": v(-135.13, 192.18) * mm});
            skLineSegment(sketch, "E1325", {"start": v(-135.13, 192.18) * mm, "end": v(-126.37, 192.18) * mm});
            skLineSegment(sketch, "E1326", {"start": v(-126.37, 192.18) * mm, "end": v(-124.3, 206.03) * mm});
            skLineSegment(sketch, "E1327", {"start": v(-124.3, 206.03) * mm, "end": v(-113.27, 206.03) * mm});
            skLineSegment(sketch, "E1328", {"start": v(-113.27, 206.03) * mm, "end": v(-111.21, 192.18) * mm});
            skLineSegment(sketch, "E1329", {"start": v(-111.21, 192.18) * mm, "end": v(-102.34, 192.18) * mm});
            skLineSegment(sketch, "E1330", {"start": v(-102.34, 192.18) * mm, "end": v(-112.62, 262.3) * mm});
            skLineSegment(sketch, "E1331", {"start": v(87.5, 262.3) * mm, "end": v(99.85, 262.3) * mm});
            skLineSegment(sketch, "E1332", {"start": v(93.68, 244.02) * mm, "end": v(97.68, 216.74) * mm});
            skLineSegment(sketch, "E1333", {"start": v(97.68, 216.74) * mm, "end": v(89.68, 216.74) * mm});
            skLineSegment(sketch, "E1334", {"start": v(89.68, 216.74) * mm, "end": v(93.68, 244.02) * mm});
            skLineSegment(sketch, "E1335", {"start": v(99.85, 262.3) * mm, "end": v(87.5, 262.3) * mm});
            skLineSegment(sketch, "E1336", {"start": v(87.5, 262.3) * mm, "end": v(77.33, 192.18) * mm});
            skLineSegment(sketch, "E1337", {"start": v(77.33, 192.18) * mm, "end": v(86.1, 192.18) * mm});
            skLineSegment(sketch, "E1338", {"start": v(86.1, 192.18) * mm, "end": v(88.16, 206.03) * mm});
            skLineSegment(sketch, "E1339", {"start": v(88.16, 206.03) * mm, "end": v(99.2, 206.03) * mm});
            skLineSegment(sketch, "E1340", {"start": v(99.2, 206.03) * mm, "end": v(101.26, 192.18) * mm});
            skLineSegment(sketch, "E1341", {"start": v(101.26, 192.18) * mm, "end": v(110.02, 192.18) * mm});
            skLineSegment(sketch, "E1342", {"start": v(110.02, 192.18) * mm, "end": v(99.85, 262.3) * mm});
            skLineSegment(sketch, "E1343", {"start": v(161.54, 262.3) * mm, "end": v(171.4, 262.3) * mm});
            skLineSegment(sketch, "E1344", {"start": v(171.4, 262.3) * mm, "end": v(171.4, 192.18) * mm});
            skLineSegment(sketch, "E1345", {"start": v(171.4, 192.18) * mm, "end": v(161.54, 192.18) * mm});
            skLineSegment(sketch, "E1346", {"start": v(161.54, 192.18) * mm, "end": v(161.54, 262.3) * mm});
            skLineSegment(sketch, "E1347", {"start": v(237.74, 249.97) * mm, "end": v(237.74, 204.51) * mm});
            skLineSegment(sketch, "E1348", {"start": v(230.5, 204.51) * mm, "end": v(230.5, 203.65) * mm});
            skLineSegment(sketch, "E1349", {"start": v(230.5, 203.65) * mm, "end": v(230.81, 202.89) * mm});
            skLineSegment(sketch, "E1350", {"start": v(230.81, 202.89) * mm, "end": v(231.25, 202.24) * mm});
            skLineSegment(sketch, "E1351", {"start": v(231.25, 202.24) * mm, "end": v(231.8, 201.6) * mm});
            skLineSegment(sketch, "E1352", {"start": v(231.8, 201.6) * mm, "end": v(232.44, 201.16) * mm});
            skLineSegment(sketch, "E1353", {"start": v(232.44, 201.16) * mm, "end": v(233.3, 200.94) * mm});
            skLineSegment(sketch, "E1354", {"start": v(233.3, 200.94) * mm, "end": v(234.07, 200.83) * mm});
            skLineSegment(sketch, "E1355", {"start": v(234.07, 200.83) * mm, "end": v(234.82, 200.94) * mm});
            skLineSegment(sketch, "E1356", {"start": v(234.82, 200.94) * mm, "end": v(235.69, 201.16) * mm});
            skLineSegment(sketch, "E1357", {"start": v(235.69, 201.16) * mm, "end": v(236.34, 201.6) * mm});
            skLineSegment(sketch, "E1358", {"start": v(236.34, 201.6) * mm, "end": v(236.88, 202.24) * mm});
            skLineSegment(sketch, "E1359", {"start": v(236.88, 202.24) * mm, "end": v(237.3, 202.89) * mm});
            skLineSegment(sketch, "E1360", {"start": v(237.3, 202.89) * mm, "end": v(237.63, 203.65) * mm});
            skLineSegment(sketch, "E1361", {"start": v(237.63, 203.65) * mm, "end": v(237.74, 204.51) * mm});
            skLineSegment(sketch, "E1362", {"start": v(230.5, 204.51) * mm, "end": v(230.5, 249.97) * mm});
            skLineSegment(sketch, "E1363", {"start": v(237.74, 249.97) * mm, "end": v(237.63, 250.84) * mm});
            skLineSegment(sketch, "E1364", {"start": v(237.63, 250.84) * mm, "end": v(237.3, 251.6) * mm});
            skLineSegment(sketch, "E1365", {"start": v(237.3, 251.6) * mm, "end": v(236.88, 252.25) * mm});
            skLineSegment(sketch, "E1366", {"start": v(236.88, 252.25) * mm, "end": v(236.34, 252.78) * mm});
            skLineSegment(sketch, "E1367", {"start": v(236.34, 252.78) * mm, "end": v(235.69, 253.22) * mm});
            skLineSegment(sketch, "E1368", {"start": v(235.69, 253.22) * mm, "end": v(234.82, 253.54) * mm});
            skLineSegment(sketch, "E1369", {"start": v(234.82, 253.54) * mm, "end": v(234.07, 253.65) * mm});
            skLineSegment(sketch, "E1370", {"start": v(234.07, 253.65) * mm, "end": v(233.3, 253.54) * mm});
            skLineSegment(sketch, "E1371", {"start": v(233.3, 253.54) * mm, "end": v(232.44, 253.22) * mm});
            skLineSegment(sketch, "E1372", {"start": v(232.44, 253.22) * mm, "end": v(231.8, 252.78) * mm});
            skLineSegment(sketch, "E1373", {"start": v(231.8, 252.78) * mm, "end": v(231.25, 252.25) * mm});
            skLineSegment(sketch, "E1374", {"start": v(231.25, 252.25) * mm, "end": v(230.81, 251.6) * mm});
            skLineSegment(sketch, "E1375", {"start": v(230.81, 251.6) * mm, "end": v(230.5, 250.84) * mm});
            skLineSegment(sketch, "E1376", {"start": v(230.5, 250.84) * mm, "end": v(230.5, 249.97) * mm});
            skLineSegment(sketch, "E1377", {"start": v(221.08, 249.22) * mm, "end": v(221.08, 205.16) * mm});
            skLineSegment(sketch, "E1378", {"start": v(221.08, 205.16) * mm, "end": v(221.08, 203.65) * mm});
            skLineSegment(sketch, "E1379", {"start": v(221.08, 203.65) * mm, "end": v(221.4, 202.13) * mm});
            skLineSegment(sketch, "E1380", {"start": v(221.4, 202.13) * mm, "end": v(221.83, 200.62) * mm});
            skLineSegment(sketch, "E1381", {"start": v(221.83, 200.62) * mm, "end": v(222.48, 199.1) * mm});
            skLineSegment(sketch, "E1382", {"start": v(222.48, 199.1) * mm, "end": v(223.35, 197.8) * mm});
            skLineSegment(sketch, "E1383", {"start": v(223.35, 197.8) * mm, "end": v(224.32, 196.61) * mm});
            skLineSegment(sketch, "E1384", {"start": v(224.32, 196.61) * mm, "end": v(225.4, 195.42) * mm});
            skLineSegment(sketch, "E1385", {"start": v(225.4, 195.42) * mm, "end": v(226.7, 194.45) * mm});
            skLineSegment(sketch, "E1386", {"start": v(226.7, 194.45) * mm, "end": v(228, 193.69) * mm});
            skLineSegment(sketch, "E1387", {"start": v(228, 193.69) * mm, "end": v(229.4, 193.04) * mm});
            skLineSegment(sketch, "E1388", {"start": v(229.4, 193.04) * mm, "end": v(230.92, 192.5) * mm});
            skLineSegment(sketch, "E1389", {"start": v(230.92, 192.5) * mm, "end": v(232.55, 192.28) * mm});
            skLineSegment(sketch, "E1390", {"start": v(232.55, 192.28) * mm, "end": v(234.07, 192.18) * mm});
            skLineSegment(sketch, "E1391", {"start": v(234.07, 192.18) * mm, "end": v(235.69, 192.28) * mm});
            skLineSegment(sketch, "E1392", {"start": v(235.69, 192.28) * mm, "end": v(237.2, 192.5) * mm});
            skLineSegment(sketch, "E1393", {"start": v(237.2, 192.5) * mm, "end": v(238.72, 193.04) * mm});
            skLineSegment(sketch, "E1394", {"start": v(238.72, 193.04) * mm, "end": v(240.13, 193.69) * mm});
            skLineSegment(sketch, "E1395", {"start": v(240.13, 193.69) * mm, "end": v(241.42, 194.45) * mm});
            skLineSegment(sketch, "E1396", {"start": v(241.42, 194.45) * mm, "end": v(242.72, 195.42) * mm});
            skLineSegment(sketch, "E1397", {"start": v(242.72, 195.42) * mm, "end": v(243.8, 196.61) * mm});
            skLineSegment(sketch, "E1398", {"start": v(243.8, 196.61) * mm, "end": v(244.78, 197.8) * mm});
            skLineSegment(sketch, "E1399", {"start": v(244.78, 197.8) * mm, "end": v(245.64, 199.1) * mm});
            skLineSegment(sketch, "E1400", {"start": v(245.64, 199.1) * mm, "end": v(246.3, 200.62) * mm});
            skLineSegment(sketch, "E1401", {"start": v(246.3, 200.62) * mm, "end": v(246.72, 202.13) * mm});
            skLineSegment(sketch, "E1402", {"start": v(246.72, 202.13) * mm, "end": v(247.05, 203.65) * mm});
            skLineSegment(sketch, "E1403", {"start": v(247.05, 203.65) * mm, "end": v(247.16, 205.16) * mm});
            skLineSegment(sketch, "E1404", {"start": v(247.16, 205.16) * mm, "end": v(247.16, 249.22) * mm});
            skLineSegment(sketch, "E1405", {"start": v(247.16, 249.22) * mm, "end": v(247.05, 250.84) * mm});
            skLineSegment(sketch, "E1406", {"start": v(247.05, 250.84) * mm, "end": v(246.72, 252.36) * mm});
            skLineSegment(sketch, "E1407", {"start": v(246.72, 252.36) * mm, "end": v(246.3, 253.87) * mm});
            skLineSegment(sketch, "E1408", {"start": v(246.3, 253.87) * mm, "end": v(245.64, 255.28) * mm});
            skLineSegment(sketch, "E1409", {"start": v(245.64, 255.28) * mm, "end": v(244.78, 256.68) * mm});
            skLineSegment(sketch, "E1410", {"start": v(244.78, 256.68) * mm, "end": v(243.8, 257.87) * mm});
            skLineSegment(sketch, "E1411", {"start": v(243.8, 257.87) * mm, "end": v(242.72, 258.96) * mm});
            skLineSegment(sketch, "E1412", {"start": v(242.72, 258.96) * mm, "end": v(241.42, 259.93) * mm});
            skLineSegment(sketch, "E1413", {"start": v(241.42, 259.93) * mm, "end": v(240.13, 260.8) * mm});
            skLineSegment(sketch, "E1414", {"start": v(240.13, 260.8) * mm, "end": v(238.72, 261.45) * mm});
            skLineSegment(sketch, "E1415", {"start": v(238.72, 261.45) * mm, "end": v(237.2, 261.88) * mm});
            skLineSegment(sketch, "E1416", {"start": v(237.2, 261.88) * mm, "end": v(235.69, 262.2) * mm});
            skLineSegment(sketch, "E1417", {"start": v(235.69, 262.2) * mm, "end": v(234.07, 262.3) * mm});
            skLineSegment(sketch, "E1418", {"start": v(234.07, 262.3) * mm, "end": v(232.55, 262.2) * mm});
            skLineSegment(sketch, "E1419", {"start": v(232.55, 262.2) * mm, "end": v(230.92, 261.88) * mm});
            skLineSegment(sketch, "E1420", {"start": v(230.92, 261.88) * mm, "end": v(229.4, 261.45) * mm});
            skLineSegment(sketch, "E1421", {"start": v(229.4, 261.45) * mm, "end": v(228, 260.8) * mm});
            skLineSegment(sketch, "E1422", {"start": v(228, 260.8) * mm, "end": v(226.7, 259.93) * mm});
            skLineSegment(sketch, "E1423", {"start": v(226.7, 259.93) * mm, "end": v(225.4, 258.96) * mm});
            skLineSegment(sketch, "E1424", {"start": v(225.4, 258.96) * mm, "end": v(224.32, 257.87) * mm});
            skLineSegment(sketch, "E1425", {"start": v(224.32, 257.87) * mm, "end": v(223.35, 256.68) * mm});
            skLineSegment(sketch, "E1426", {"start": v(223.35, 256.68) * mm, "end": v(222.48, 255.28) * mm});
            skLineSegment(sketch, "E1427", {"start": v(222.48, 255.28) * mm, "end": v(221.83, 253.87) * mm});
            skLineSegment(sketch, "E1428", {"start": v(221.83, 253.87) * mm, "end": v(221.4, 252.36) * mm});
            skLineSegment(sketch, "E1429", {"start": v(221.4, 252.36) * mm, "end": v(221.08, 250.84) * mm});
            skLineSegment(sketch, "E1430", {"start": v(221.08, 250.84) * mm, "end": v(221.08, 249.22) * mm});
            skLineSegment(sketch, "E1431", {"start": v(183.84, 205.16) * mm, "end": v(183.95, 203.65) * mm});
            skLineSegment(sketch, "E1432", {"start": v(183.95, 203.65) * mm, "end": v(184.17, 202.13) * mm});
            skLineSegment(sketch, "E1433", {"start": v(184.17, 202.13) * mm, "end": v(184.7, 200.62) * mm});
            skLineSegment(sketch, "E1434", {"start": v(184.7, 200.62) * mm, "end": v(185.36, 199.1) * mm});
            skLineSegment(sketch, "E1435", {"start": v(185.36, 199.1) * mm, "end": v(186.11, 197.8) * mm});
            skLineSegment(sketch, "E1436", {"start": v(186.11, 197.8) * mm, "end": v(187.09, 196.61) * mm});
            skLineSegment(sketch, "E1437", {"start": v(187.09, 196.61) * mm, "end": v(188.17, 195.42) * mm});
            skLineSegment(sketch, "E1438", {"start": v(188.17, 195.42) * mm, "end": v(189.47, 194.45) * mm});
            skLineSegment(sketch, "E1439", {"start": v(189.47, 194.45) * mm, "end": v(190.77, 193.69) * mm});
            skLineSegment(sketch, "E1440", {"start": v(190.77, 193.69) * mm, "end": v(192.18, 193.04) * mm});
            skLineSegment(sketch, "E1441", {"start": v(192.18, 193.04) * mm, "end": v(193.7, 192.5) * mm});
            skLineSegment(sketch, "E1442", {"start": v(193.7, 192.5) * mm, "end": v(195.31, 192.28) * mm});
            skLineSegment(sketch, "E1443", {"start": v(195.31, 192.28) * mm, "end": v(196.83, 192.18) * mm});
            skLineSegment(sketch, "E1444", {"start": v(196.83, 192.18) * mm, "end": v(198.45, 192.28) * mm});
            skLineSegment(sketch, "E1445", {"start": v(198.45, 192.28) * mm, "end": v(199.97, 192.5) * mm});
            skLineSegment(sketch, "E1446", {"start": v(199.97, 192.5) * mm, "end": v(201.48, 193.04) * mm});
            skLineSegment(sketch, "E1447", {"start": v(201.48, 193.04) * mm, "end": v(202.9, 193.69) * mm});
            skLineSegment(sketch, "E1448", {"start": v(202.9, 193.69) * mm, "end": v(204.3, 194.45) * mm});
            skLineSegment(sketch, "E1449", {"start": v(204.3, 194.45) * mm, "end": v(205.5, 195.42) * mm});
            skLineSegment(sketch, "E1450", {"start": v(205.5, 195.42) * mm, "end": v(206.57, 196.61) * mm});
            skLineSegment(sketch, "E1451", {"start": v(206.57, 196.61) * mm, "end": v(207.54, 197.8) * mm});
            skLineSegment(sketch, "E1452", {"start": v(207.54, 197.8) * mm, "end": v(208.41, 199.1) * mm});
            skLineSegment(sketch, "E1453", {"start": v(208.41, 199.1) * mm, "end": v(209.06, 200.62) * mm});
            skLineSegment(sketch, "E1454", {"start": v(209.06, 200.62) * mm, "end": v(209.5, 202.13) * mm});
            skLineSegment(sketch, "E1455", {"start": v(209.5, 202.13) * mm, "end": v(209.82, 203.65) * mm});
            skLineSegment(sketch, "E1456", {"start": v(209.82, 203.65) * mm, "end": v(209.93, 205.16) * mm});
            skLineSegment(sketch, "E1457", {"start": v(209.93, 205.16) * mm, "end": v(209.93, 216.2) * mm});
            skLineSegment(sketch, "E1458", {"start": v(209.93, 216.2) * mm, "end": v(200.51, 216.2) * mm});
            skLineSegment(sketch, "E1459", {"start": v(200.51, 216.2) * mm, "end": v(200.51, 204.51) * mm});
            skLineSegment(sketch, "E1460", {"start": v(193.26, 204.51) * mm, "end": v(193.37, 203.65) * mm});
            skLineSegment(sketch, "E1461", {"start": v(193.37, 203.65) * mm, "end": v(193.58, 202.89) * mm});
            skLineSegment(sketch, "E1462", {"start": v(193.58, 202.89) * mm, "end": v(194.02, 202.24) * mm});
            skLineSegment(sketch, "E1463", {"start": v(194.02, 202.24) * mm, "end": v(194.56, 201.6) * mm});
            skLineSegment(sketch, "E1464", {"start": v(194.56, 201.6) * mm, "end": v(195.31, 201.16) * mm});
            skLineSegment(sketch, "E1465", {"start": v(195.31, 201.16) * mm, "end": v(196.07, 200.94) * mm});
            skLineSegment(sketch, "E1466", {"start": v(196.07, 200.94) * mm, "end": v(196.83, 200.83) * mm});
            skLineSegment(sketch, "E1467", {"start": v(196.83, 200.83) * mm, "end": v(197.7, 200.94) * mm});
            skLineSegment(sketch, "E1468", {"start": v(197.7, 200.94) * mm, "end": v(198.45, 201.16) * mm});
            skLineSegment(sketch, "E1469", {"start": v(198.45, 201.16) * mm, "end": v(199.1, 201.6) * mm});
            skLineSegment(sketch, "E1470", {"start": v(199.1, 201.6) * mm, "end": v(199.64, 202.24) * mm});
            skLineSegment(sketch, "E1471", {"start": v(199.64, 202.24) * mm, "end": v(200.08, 202.89) * mm});
            skLineSegment(sketch, "E1472", {"start": v(200.08, 202.89) * mm, "end": v(200.4, 203.65) * mm});
            skLineSegment(sketch, "E1473", {"start": v(200.4, 203.65) * mm, "end": v(200.51, 204.51) * mm});
            skLineSegment(sketch, "E1474", {"start": v(193.26, 204.51) * mm, "end": v(193.26, 249.97) * mm});
            skLineSegment(sketch, "E1475", {"start": v(200.51, 249.97) * mm, "end": v(200.4, 250.84) * mm});
            skLineSegment(sketch, "E1476", {"start": v(200.4, 250.84) * mm, "end": v(200.08, 251.6) * mm});
            skLineSegment(sketch, "E1477", {"start": v(200.08, 251.6) * mm, "end": v(199.64, 252.25) * mm});
            skLineSegment(sketch, "E1478", {"start": v(199.64, 252.25) * mm, "end": v(199.1, 252.78) * mm});
            skLineSegment(sketch, "E1479", {"start": v(199.1, 252.78) * mm, "end": v(198.45, 253.22) * mm});
            skLineSegment(sketch, "E1480", {"start": v(198.45, 253.22) * mm, "end": v(197.7, 253.54) * mm});
            skLineSegment(sketch, "E1481", {"start": v(197.7, 253.54) * mm, "end": v(196.83, 253.65) * mm});
            skLineSegment(sketch, "E1482", {"start": v(196.83, 253.65) * mm, "end": v(196.07, 253.54) * mm});
            skLineSegment(sketch, "E1483", {"start": v(196.07, 253.54) * mm, "end": v(195.31, 253.22) * mm});
            skLineSegment(sketch, "E1484", {"start": v(195.31, 253.22) * mm, "end": v(194.56, 252.78) * mm});
            skLineSegment(sketch, "E1485", {"start": v(194.56, 252.78) * mm, "end": v(194.02, 252.25) * mm});
            skLineSegment(sketch, "E1486", {"start": v(194.02, 252.25) * mm, "end": v(193.58, 251.6) * mm});
            skLineSegment(sketch, "E1487", {"start": v(193.58, 251.6) * mm, "end": v(193.37, 250.84) * mm});
            skLineSegment(sketch, "E1488", {"start": v(193.37, 250.84) * mm, "end": v(193.26, 249.97) * mm});
            skLineSegment(sketch, "E1489", {"start": v(200.51, 249.97) * mm, "end": v(200.51, 238.28) * mm});
            skLineSegment(sketch, "E1490", {"start": v(200.51, 238.28) * mm, "end": v(209.93, 238.28) * mm});
            skLineSegment(sketch, "E1491", {"start": v(209.93, 238.28) * mm, "end": v(209.93, 249.22) * mm});
            skLineSegment(sketch, "E1492", {"start": v(209.93, 249.22) * mm, "end": v(209.82, 250.84) * mm});
            skLineSegment(sketch, "E1493", {"start": v(209.82, 250.84) * mm, "end": v(209.5, 252.36) * mm});
            skLineSegment(sketch, "E1494", {"start": v(209.5, 252.36) * mm, "end": v(209.06, 253.87) * mm});
            skLineSegment(sketch, "E1495", {"start": v(209.06, 253.87) * mm, "end": v(208.41, 255.28) * mm});
            skLineSegment(sketch, "E1496", {"start": v(208.41, 255.28) * mm, "end": v(207.54, 256.68) * mm});
            skLineSegment(sketch, "E1497", {"start": v(207.54, 256.68) * mm, "end": v(206.57, 257.87) * mm});
            skLineSegment(sketch, "E1498", {"start": v(206.57, 257.87) * mm, "end": v(205.5, 258.96) * mm});
            skLineSegment(sketch, "E1499", {"start": v(205.5, 258.96) * mm, "end": v(204.3, 259.93) * mm});
            skLineSegment(sketch, "E1500", {"start": v(204.3, 259.93) * mm, "end": v(202.9, 260.8) * mm});
            skLineSegment(sketch, "E1501", {"start": v(202.9, 260.8) * mm, "end": v(201.48, 261.45) * mm});
            skLineSegment(sketch, "E1502", {"start": v(201.48, 261.45) * mm, "end": v(199.97, 261.88) * mm});
            skLineSegment(sketch, "E1503", {"start": v(199.97, 261.88) * mm, "end": v(198.45, 262.2) * mm});
            skLineSegment(sketch, "E1504", {"start": v(198.45, 262.2) * mm, "end": v(196.83, 262.3) * mm});
            skLineSegment(sketch, "E1505", {"start": v(196.83, 262.3) * mm, "end": v(195.31, 262.2) * mm});
            skLineSegment(sketch, "E1506", {"start": v(195.31, 262.2) * mm, "end": v(193.7, 261.88) * mm});
            skLineSegment(sketch, "E1507", {"start": v(193.7, 261.88) * mm, "end": v(192.18, 261.45) * mm});
            skLineSegment(sketch, "E1508", {"start": v(192.18, 261.45) * mm, "end": v(190.77, 260.8) * mm});
            skLineSegment(sketch, "E1509", {"start": v(190.77, 260.8) * mm, "end": v(189.47, 259.93) * mm});
            skLineSegment(sketch, "E1510", {"start": v(189.47, 259.93) * mm, "end": v(188.17, 258.96) * mm});
            skLineSegment(sketch, "E1511", {"start": v(188.17, 258.96) * mm, "end": v(187.09, 257.87) * mm});
            skLineSegment(sketch, "E1512", {"start": v(187.09, 257.87) * mm, "end": v(186.11, 256.68) * mm});
            skLineSegment(sketch, "E1513", {"start": v(186.11, 256.68) * mm, "end": v(185.36, 255.28) * mm});
            skLineSegment(sketch, "E1514", {"start": v(185.36, 255.28) * mm, "end": v(184.7, 253.87) * mm});
            skLineSegment(sketch, "E1515", {"start": v(184.7, 253.87) * mm, "end": v(184.17, 252.36) * mm});
            skLineSegment(sketch, "E1516", {"start": v(184.17, 252.36) * mm, "end": v(183.95, 250.84) * mm});
            skLineSegment(sketch, "E1517", {"start": v(183.95, 250.84) * mm, "end": v(183.84, 249.22) * mm});
            skLineSegment(sketch, "E1518", {"start": v(183.84, 249.22) * mm, "end": v(183.84, 205.16) * mm});
            skLineSegment(sketch, "E1519", {"start": v(-19.1, 249.97) * mm, "end": v(-19.1, 204.51) * mm});
            skLineSegment(sketch, "E1520", {"start": v(-26.35, 204.51) * mm, "end": v(-26.25, 203.65) * mm});
            skLineSegment(sketch, "E1521", {"start": v(-26.25, 203.65) * mm, "end": v(-25.92, 202.89) * mm});
            skLineSegment(sketch, "E1522", {"start": v(-25.92, 202.89) * mm, "end": v(-25.49, 202.24) * mm});
            skLineSegment(sketch, "E1523", {"start": v(-25.49, 202.24) * mm, "end": v(-24.95, 201.6) * mm});
            skLineSegment(sketch, "E1524", {"start": v(-24.95, 201.6) * mm, "end": v(-24.3, 201.16) * mm});
            skLineSegment(sketch, "E1525", {"start": v(-24.3, 201.16) * mm, "end": v(-23.54, 200.94) * mm});
            skLineSegment(sketch, "E1526", {"start": v(-23.54, 200.94) * mm, "end": v(-22.67, 200.83) * mm});
            skLineSegment(sketch, "E1527", {"start": v(-22.67, 200.83) * mm, "end": v(-21.92, 200.94) * mm});
            skLineSegment(sketch, "E1528", {"start": v(-21.92, 200.94) * mm, "end": v(-21.16, 201.16) * mm});
            skLineSegment(sketch, "E1529", {"start": v(-21.16, 201.16) * mm, "end": v(-20.4, 201.6) * mm});
            skLineSegment(sketch, "E1530", {"start": v(-20.4, 201.6) * mm, "end": v(-19.86, 202.24) * mm});
            skLineSegment(sketch, "E1531", {"start": v(-19.86, 202.24) * mm, "end": v(-19.43, 202.89) * mm});
            skLineSegment(sketch, "E1532", {"start": v(-19.43, 202.89) * mm, "end": v(-19.1, 203.65) * mm});
            skLineSegment(sketch, "E1533", {"start": v(-19.1, 203.65) * mm, "end": v(-19.1, 204.51) * mm});
            skLineSegment(sketch, "E1534", {"start": v(-26.35, 204.51) * mm, "end": v(-26.35, 249.97) * mm});
            skLineSegment(sketch, "E1535", {"start": v(-19.1, 249.97) * mm, "end": v(-19.1, 250.84) * mm});
            skLineSegment(sketch, "E1536", {"start": v(-19.1, 250.84) * mm, "end": v(-19.43, 251.6) * mm});
            skLineSegment(sketch, "E1537", {"start": v(-19.43, 251.6) * mm, "end": v(-19.86, 252.25) * mm});
            skLineSegment(sketch, "E1538", {"start": v(-19.86, 252.25) * mm, "end": v(-20.4, 252.78) * mm});
            skLineSegment(sketch, "E1539", {"start": v(-20.4, 252.78) * mm, "end": v(-21.16, 253.22) * mm});
            skLineSegment(sketch, "E1540", {"start": v(-21.16, 253.22) * mm, "end": v(-21.92, 253.54) * mm});
            skLineSegment(sketch, "E1541", {"start": v(-21.92, 253.54) * mm, "end": v(-22.67, 253.65) * mm});
            skLineSegment(sketch, "E1542", {"start": v(-22.67, 253.65) * mm, "end": v(-23.54, 253.54) * mm});
            skLineSegment(sketch, "E1543", {"start": v(-23.54, 253.54) * mm, "end": v(-24.3, 253.22) * mm});
            skLineSegment(sketch, "E1544", {"start": v(-24.3, 253.22) * mm, "end": v(-24.95, 252.78) * mm});
            skLineSegment(sketch, "E1545", {"start": v(-24.95, 252.78) * mm, "end": v(-25.49, 252.25) * mm});
            skLineSegment(sketch, "E1546", {"start": v(-25.49, 252.25) * mm, "end": v(-25.92, 251.6) * mm});
            skLineSegment(sketch, "E1547", {"start": v(-25.92, 251.6) * mm, "end": v(-26.25, 250.84) * mm});
            skLineSegment(sketch, "E1548", {"start": v(-26.25, 250.84) * mm, "end": v(-26.35, 249.97) * mm});
            skLineSegment(sketch, "E1549", {"start": v(-35.77, 249.22) * mm, "end": v(-35.77, 205.16) * mm});
            skLineSegment(sketch, "E1550", {"start": v(-35.77, 205.16) * mm, "end": v(-35.66, 203.65) * mm});
            skLineSegment(sketch, "E1551", {"start": v(-35.66, 203.65) * mm, "end": v(-35.34, 202.13) * mm});
            skLineSegment(sketch, "E1552", {"start": v(-35.34, 202.13) * mm, "end": v(-34.9, 200.62) * mm});
            skLineSegment(sketch, "E1553", {"start": v(-34.9, 200.62) * mm, "end": v(-34.26, 199.1) * mm});
            skLineSegment(sketch, "E1554", {"start": v(-34.26, 199.1) * mm, "end": v(-33.4, 197.8) * mm});
            skLineSegment(sketch, "E1555", {"start": v(-33.4, 197.8) * mm, "end": v(-32.42, 196.61) * mm});
            skLineSegment(sketch, "E1556", {"start": v(-32.42, 196.61) * mm, "end": v(-31.33, 195.42) * mm});
            skLineSegment(sketch, "E1557", {"start": v(-31.33, 195.42) * mm, "end": v(-30.14, 194.45) * mm});
            skLineSegment(sketch, "E1558", {"start": v(-30.14, 194.45) * mm, "end": v(-28.74, 193.69) * mm});
            skLineSegment(sketch, "E1559", {"start": v(-28.74, 193.69) * mm, "end": v(-27.33, 193.04) * mm});
            skLineSegment(sketch, "E1560", {"start": v(-27.33, 193.04) * mm, "end": v(-25.81, 192.5) * mm});
            skLineSegment(sketch, "E1561", {"start": v(-25.81, 192.5) * mm, "end": v(-24.3, 192.28) * mm});
            skLineSegment(sketch, "E1562", {"start": v(-24.3, 192.28) * mm, "end": v(-22.67, 192.18) * mm});
            skLineSegment(sketch, "E1563", {"start": v(-22.67, 192.18) * mm, "end": v(-21.16, 192.28) * mm});
            skLineSegment(sketch, "E1564", {"start": v(-21.16, 192.28) * mm, "end": v(-19.54, 192.5) * mm});
            skLineSegment(sketch, "E1565", {"start": v(-19.54, 192.5) * mm, "end": v(-18.02, 193.04) * mm});
            skLineSegment(sketch, "E1566", {"start": v(-18.02, 193.04) * mm, "end": v(-16.61, 193.69) * mm});
            skLineSegment(sketch, "E1567", {"start": v(-16.61, 193.69) * mm, "end": v(-15.31, 194.45) * mm});
            skLineSegment(sketch, "E1568", {"start": v(-15.31, 194.45) * mm, "end": v(-14.02, 195.42) * mm});
            skLineSegment(sketch, "E1569", {"start": v(-14.02, 195.42) * mm, "end": v(-12.93, 196.61) * mm});
            skLineSegment(sketch, "E1570", {"start": v(-12.93, 196.61) * mm, "end": v(-11.96, 197.8) * mm});
            skLineSegment(sketch, "E1571", {"start": v(-11.96, 197.8) * mm, "end": v(-11.1, 199.1) * mm});
            skLineSegment(sketch, "E1572", {"start": v(-11.1, 199.1) * mm, "end": v(-10.45, 200.62) * mm});
            skLineSegment(sketch, "E1573", {"start": v(-10.45, 200.62) * mm, "end": v(-10.01, 202.13) * mm});
            skLineSegment(sketch, "E1574", {"start": v(-10.01, 202.13) * mm, "end": v(-9.69, 203.65) * mm});
            skLineSegment(sketch, "E1575", {"start": v(-9.69, 203.65) * mm, "end": v(-9.69, 205.16) * mm});
            skLineSegment(sketch, "E1576", {"start": v(-9.69, 205.16) * mm, "end": v(-9.69, 249.22) * mm});
            skLineSegment(sketch, "E1577", {"start": v(-9.69, 249.22) * mm, "end": v(-9.69, 250.84) * mm});
            skLineSegment(sketch, "E1578", {"start": v(-9.69, 250.84) * mm, "end": v(-10.01, 252.36) * mm});
            skLineSegment(sketch, "E1579", {"start": v(-10.01, 252.36) * mm, "end": v(-10.45, 253.87) * mm});
            skLineSegment(sketch, "E1580", {"start": v(-10.45, 253.87) * mm, "end": v(-11.1, 255.28) * mm});
            skLineSegment(sketch, "E1581", {"start": v(-11.1, 255.28) * mm, "end": v(-11.96, 256.68) * mm});
            skLineSegment(sketch, "E1582", {"start": v(-11.96, 256.68) * mm, "end": v(-12.93, 257.87) * mm});
            skLineSegment(sketch, "E1583", {"start": v(-12.93, 257.87) * mm, "end": v(-14.02, 258.96) * mm});
            skLineSegment(sketch, "E1584", {"start": v(-14.02, 258.96) * mm, "end": v(-15.31, 259.93) * mm});
            skLineSegment(sketch, "E1585", {"start": v(-15.31, 259.93) * mm, "end": v(-16.61, 260.8) * mm});
            skLineSegment(sketch, "E1586", {"start": v(-16.61, 260.8) * mm, "end": v(-18.02, 261.45) * mm});
            skLineSegment(sketch, "E1587", {"start": v(-18.02, 261.45) * mm, "end": v(-19.54, 261.88) * mm});
            skLineSegment(sketch, "E1588", {"start": v(-19.54, 261.88) * mm, "end": v(-21.16, 262.2) * mm});
            skLineSegment(sketch, "E1589", {"start": v(-21.16, 262.2) * mm, "end": v(-22.67, 262.3) * mm});
            skLineSegment(sketch, "E1590", {"start": v(-22.67, 262.3) * mm, "end": v(-24.3, 262.2) * mm});
            skLineSegment(sketch, "E1591", {"start": v(-24.3, 262.2) * mm, "end": v(-25.81, 261.88) * mm});
            skLineSegment(sketch, "E1592", {"start": v(-25.81, 261.88) * mm, "end": v(-27.33, 261.45) * mm});
            skLineSegment(sketch, "E1593", {"start": v(-27.33, 261.45) * mm, "end": v(-28.74, 260.8) * mm});
            skLineSegment(sketch, "E1594", {"start": v(-28.74, 260.8) * mm, "end": v(-30.14, 259.93) * mm});
            skLineSegment(sketch, "E1595", {"start": v(-30.14, 259.93) * mm, "end": v(-31.33, 258.96) * mm});
            skLineSegment(sketch, "E1596", {"start": v(-31.33, 258.96) * mm, "end": v(-32.42, 257.87) * mm});
            skLineSegment(sketch, "E1597", {"start": v(-32.42, 257.87) * mm, "end": v(-33.4, 256.68) * mm});
            skLineSegment(sketch, "E1598", {"start": v(-33.4, 256.68) * mm, "end": v(-34.26, 255.28) * mm});
            skLineSegment(sketch, "E1599", {"start": v(-34.26, 255.28) * mm, "end": v(-34.9, 253.87) * mm});
            skLineSegment(sketch, "E1600", {"start": v(-34.9, 253.87) * mm, "end": v(-35.34, 252.36) * mm});
            skLineSegment(sketch, "E1601", {"start": v(-35.34, 252.36) * mm, "end": v(-35.66, 250.84) * mm});
            skLineSegment(sketch, "E1602", {"start": v(-35.66, 250.84) * mm, "end": v(-35.77, 249.22) * mm});
            skLineSegment(sketch, "E1603", {"start": v(-76.58, 249.97) * mm, "end": v(-76.58, 204.51) * mm});
            skLineSegment(sketch, "E1604", {"start": v(-83.83, 204.51) * mm, "end": v(-83.72, 203.65) * mm});
            skLineSegment(sketch, "E1605", {"start": v(-83.72, 203.65) * mm, "end": v(-83.5, 202.89) * mm});
            skLineSegment(sketch, "E1606", {"start": v(-83.5, 202.89) * mm, "end": v(-83.07, 202.24) * mm});
            skLineSegment(sketch, "E1607", {"start": v(-83.07, 202.24) * mm, "end": v(-82.53, 201.6) * mm});
            skLineSegment(sketch, "E1608", {"start": v(-82.53, 201.6) * mm, "end": v(-81.77, 201.16) * mm});
            skLineSegment(sketch, "E1609", {"start": v(-81.77, 201.16) * mm, "end": v(-81.01, 200.94) * mm});
            skLineSegment(sketch, "E1610", {"start": v(-81.01, 200.94) * mm, "end": v(-80.26, 200.83) * mm});
            skLineSegment(sketch, "E1611", {"start": v(-80.26, 200.83) * mm, "end": v(-79.39, 200.94) * mm});
            skLineSegment(sketch, "E1612", {"start": v(-79.39, 200.94) * mm, "end": v(-78.63, 201.16) * mm});
            skLineSegment(sketch, "E1613", {"start": v(-78.63, 201.16) * mm, "end": v(-77.98, 201.6) * mm});
            skLineSegment(sketch, "E1614", {"start": v(-77.98, 201.6) * mm, "end": v(-77.44, 202.24) * mm});
            skLineSegment(sketch, "E1615", {"start": v(-77.44, 202.24) * mm, "end": v(-77.01, 202.89) * mm});
            skLineSegment(sketch, "E1616", {"start": v(-77.01, 202.89) * mm, "end": v(-76.68, 203.65) * mm});
            skLineSegment(sketch, "E1617", {"start": v(-76.68, 203.65) * mm, "end": v(-76.58, 204.51) * mm});
            skLineSegment(sketch, "E1618", {"start": v(-83.83, 204.51) * mm, "end": v(-83.83, 249.97) * mm});
            skLineSegment(sketch, "E1619", {"start": v(-76.58, 249.97) * mm, "end": v(-76.68, 250.84) * mm});
            skLineSegment(sketch, "E1620", {"start": v(-76.68, 250.84) * mm, "end": v(-77.01, 251.6) * mm});
            skLineSegment(sketch, "E1621", {"start": v(-77.01, 251.6) * mm, "end": v(-77.44, 252.25) * mm});
            skLineSegment(sketch, "E1622", {"start": v(-77.44, 252.25) * mm, "end": v(-77.98, 252.78) * mm});
            skLineSegment(sketch, "E1623", {"start": v(-77.98, 252.78) * mm, "end": v(-78.63, 253.22) * mm});
            skLineSegment(sketch, "E1624", {"start": v(-78.63, 253.22) * mm, "end": v(-79.39, 253.54) * mm});
            skLineSegment(sketch, "E1625", {"start": v(-79.39, 253.54) * mm, "end": v(-80.26, 253.65) * mm});
            skLineSegment(sketch, "E1626", {"start": v(-80.26, 253.65) * mm, "end": v(-81.01, 253.54) * mm});
            skLineSegment(sketch, "E1627", {"start": v(-81.01, 253.54) * mm, "end": v(-81.77, 253.22) * mm});
            skLineSegment(sketch, "E1628", {"start": v(-81.77, 253.22) * mm, "end": v(-82.53, 252.78) * mm});
            skLineSegment(sketch, "E1629", {"start": v(-82.53, 252.78) * mm, "end": v(-83.07, 252.25) * mm});
            skLineSegment(sketch, "E1630", {"start": v(-83.07, 252.25) * mm, "end": v(-83.5, 251.6) * mm});
            skLineSegment(sketch, "E1631", {"start": v(-83.5, 251.6) * mm, "end": v(-83.72, 250.84) * mm});
            skLineSegment(sketch, "E1632", {"start": v(-83.72, 250.84) * mm, "end": v(-83.83, 249.97) * mm});
            skLineSegment(sketch, "E1633", {"start": v(-93.25, 249.22) * mm, "end": v(-93.25, 205.16) * mm});
            skLineSegment(sketch, "E1634", {"start": v(-93.25, 205.16) * mm, "end": v(-93.14, 203.65) * mm});
            skLineSegment(sketch, "E1635", {"start": v(-93.14, 203.65) * mm, "end": v(-92.92, 202.13) * mm});
            skLineSegment(sketch, "E1636", {"start": v(-92.92, 202.13) * mm, "end": v(-92.38, 200.62) * mm});
            skLineSegment(sketch, "E1637", {"start": v(-92.38, 200.62) * mm, "end": v(-91.84, 199.1) * mm});
            skLineSegment(sketch, "E1638", {"start": v(-91.84, 199.1) * mm, "end": v(-90.97, 197.8) * mm});
            skLineSegment(sketch, "E1639", {"start": v(-90.97, 197.8) * mm, "end": v(-90, 196.61) * mm});
            skLineSegment(sketch, "E1640", {"start": v(-90, 196.61) * mm, "end": v(-88.91, 195.42) * mm});
            skLineSegment(sketch, "E1641", {"start": v(-88.91, 195.42) * mm, "end": v(-87.62, 194.45) * mm});
            skLineSegment(sketch, "E1642", {"start": v(-87.62, 194.45) * mm, "end": v(-86.32, 193.69) * mm});
            skLineSegment(sketch, "E1643", {"start": v(-86.32, 193.69) * mm, "end": v(-84.91, 193.04) * mm});
            skLineSegment(sketch, "E1644", {"start": v(-84.91, 193.04) * mm, "end": v(-83.4, 192.5) * mm});
            skLineSegment(sketch, "E1645", {"start": v(-83.4, 192.5) * mm, "end": v(-81.77, 192.28) * mm});
            skLineSegment(sketch, "E1646", {"start": v(-81.77, 192.28) * mm, "end": v(-80.26, 192.18) * mm});
            skLineSegment(sketch, "E1647", {"start": v(-80.26, 192.18) * mm, "end": v(-78.63, 192.28) * mm});
            skLineSegment(sketch, "E1648", {"start": v(-78.63, 192.28) * mm, "end": v(-77.12, 192.5) * mm});
            skLineSegment(sketch, "E1649", {"start": v(-77.12, 192.5) * mm, "end": v(-75.6, 193.04) * mm});
            skLineSegment(sketch, "E1650", {"start": v(-75.6, 193.04) * mm, "end": v(-74.2, 193.69) * mm});
            skLineSegment(sketch, "E1651", {"start": v(-74.2, 193.69) * mm, "end": v(-72.79, 194.45) * mm});
            skLineSegment(sketch, "E1652", {"start": v(-72.79, 194.45) * mm, "end": v(-71.6, 195.42) * mm});
            skLineSegment(sketch, "E1653", {"start": v(-71.6, 195.42) * mm, "end": v(-70.52, 196.61) * mm});
            skLineSegment(sketch, "E1654", {"start": v(-70.52, 196.61) * mm, "end": v(-69.54, 197.8) * mm});
            skLineSegment(sketch, "E1655", {"start": v(-69.54, 197.8) * mm, "end": v(-68.67, 199.1) * mm});
            skLineSegment(sketch, "E1656", {"start": v(-68.67, 199.1) * mm, "end": v(-68.03, 200.62) * mm});
            skLineSegment(sketch, "E1657", {"start": v(-68.03, 200.62) * mm, "end": v(-67.6, 202.13) * mm});
            skLineSegment(sketch, "E1658", {"start": v(-67.6, 202.13) * mm, "end": v(-67.27, 203.65) * mm});
            skLineSegment(sketch, "E1659", {"start": v(-67.27, 203.65) * mm, "end": v(-67.16, 205.16) * mm});
            skLineSegment(sketch, "E1660", {"start": v(-67.16, 205.16) * mm, "end": v(-67.16, 249.22) * mm});
            skLineSegment(sketch, "E1661", {"start": v(-67.16, 249.22) * mm, "end": v(-67.27, 250.84) * mm});
            skLineSegment(sketch, "E1662", {"start": v(-67.27, 250.84) * mm, "end": v(-67.6, 252.36) * mm});
            skLineSegment(sketch, "E1663", {"start": v(-67.6, 252.36) * mm, "end": v(-68.03, 253.87) * mm});
            skLineSegment(sketch, "E1664", {"start": v(-68.03, 253.87) * mm, "end": v(-68.67, 255.28) * mm});
            skLineSegment(sketch, "E1665", {"start": v(-68.67, 255.28) * mm, "end": v(-69.54, 256.68) * mm});
            skLineSegment(sketch, "E1666", {"start": v(-69.54, 256.68) * mm, "end": v(-70.52, 257.87) * mm});
            skLineSegment(sketch, "E1667", {"start": v(-70.52, 257.87) * mm, "end": v(-71.6, 258.96) * mm});
            skLineSegment(sketch, "E1668", {"start": v(-71.6, 258.96) * mm, "end": v(-72.79, 259.93) * mm});
            skLineSegment(sketch, "E1669", {"start": v(-72.79, 259.93) * mm, "end": v(-74.2, 260.8) * mm});
            skLineSegment(sketch, "E1670", {"start": v(-74.2, 260.8) * mm, "end": v(-75.6, 261.45) * mm});
            skLineSegment(sketch, "E1671", {"start": v(-75.6, 261.45) * mm, "end": v(-77.12, 261.88) * mm});
            skLineSegment(sketch, "E1672", {"start": v(-77.12, 261.88) * mm, "end": v(-78.63, 262.2) * mm});
            skLineSegment(sketch, "E1673", {"start": v(-78.63, 262.2) * mm, "end": v(-80.26, 262.3) * mm});
            skLineSegment(sketch, "E1674", {"start": v(-80.26, 262.3) * mm, "end": v(-81.77, 262.2) * mm});
            skLineSegment(sketch, "E1675", {"start": v(-81.77, 262.2) * mm, "end": v(-83.4, 261.88) * mm});
            skLineSegment(sketch, "E1676", {"start": v(-83.4, 261.88) * mm, "end": v(-84.91, 261.45) * mm});
            skLineSegment(sketch, "E1677", {"start": v(-84.91, 261.45) * mm, "end": v(-86.32, 260.8) * mm});
            skLineSegment(sketch, "E1678", {"start": v(-86.32, 260.8) * mm, "end": v(-87.62, 259.93) * mm});
            skLineSegment(sketch, "E1679", {"start": v(-87.62, 259.93) * mm, "end": v(-88.91, 258.96) * mm});
            skLineSegment(sketch, "E1680", {"start": v(-88.91, 258.96) * mm, "end": v(-90, 257.87) * mm});
            skLineSegment(sketch, "E1681", {"start": v(-90, 257.87) * mm, "end": v(-90.97, 256.68) * mm});
            skLineSegment(sketch, "E1682", {"start": v(-90.97, 256.68) * mm, "end": v(-91.84, 255.28) * mm});
            skLineSegment(sketch, "E1683", {"start": v(-91.84, 255.28) * mm, "end": v(-92.38, 253.87) * mm});
            skLineSegment(sketch, "E1684", {"start": v(-92.38, 253.87) * mm, "end": v(-92.92, 252.36) * mm});
            skLineSegment(sketch, "E1685", {"start": v(-92.92, 252.36) * mm, "end": v(-93.14, 250.84) * mm});
            skLineSegment(sketch, "E1686", {"start": v(-93.14, 250.84) * mm, "end": v(-93.25, 249.22) * mm});
            skLineSegment(sketch, "E1687", {"start": v(-246.72, 205.16) * mm, "end": v(-246.62, 203.65) * mm});
            skLineSegment(sketch, "E1688", {"start": v(-246.62, 203.65) * mm, "end": v(-246.3, 202.13) * mm});
            skLineSegment(sketch, "E1689", {"start": v(-246.3, 202.13) * mm, "end": v(-245.86, 200.62) * mm});
            skLineSegment(sketch, "E1690", {"start": v(-245.86, 200.62) * mm, "end": v(-245.21, 199.1) * mm});
            skLineSegment(sketch, "E1691", {"start": v(-245.21, 199.1) * mm, "end": v(-244.34, 197.8) * mm});
            skLineSegment(sketch, "E1692", {"start": v(-244.34, 197.8) * mm, "end": v(-243.37, 196.61) * mm});
            skLineSegment(sketch, "E1693", {"start": v(-243.37, 196.61) * mm, "end": v(-242.29, 195.42) * mm});
            skLineSegment(sketch, "E1694", {"start": v(-242.29, 195.42) * mm, "end": v(-240.99, 194.45) * mm});
            skLineSegment(sketch, "E1695", {"start": v(-240.99, 194.45) * mm, "end": v(-239.69, 193.69) * mm});
            skLineSegment(sketch, "E1696", {"start": v(-239.69, 193.69) * mm, "end": v(-238.28, 193.04) * mm});
            skLineSegment(sketch, "E1697", {"start": v(-238.28, 193.04) * mm, "end": v(-236.77, 192.5) * mm});
            skLineSegment(sketch, "E1698", {"start": v(-236.77, 192.5) * mm, "end": v(-235.25, 192.28) * mm});
            skLineSegment(sketch, "E1699", {"start": v(-235.25, 192.28) * mm, "end": v(-233.63, 192.18) * mm});
            skLineSegment(sketch, "E1700", {"start": v(-233.63, 192.18) * mm, "end": v(-232.11, 192.28) * mm});
            skLineSegment(sketch, "E1701", {"start": v(-232.11, 192.28) * mm, "end": v(-230.49, 192.5) * mm});
            skLineSegment(sketch, "E1702", {"start": v(-230.49, 192.5) * mm, "end": v(-228.97, 193.04) * mm});
            skLineSegment(sketch, "E1703", {"start": v(-228.97, 193.04) * mm, "end": v(-227.57, 193.69) * mm});
            skLineSegment(sketch, "E1704", {"start": v(-227.57, 193.69) * mm, "end": v(-226.27, 194.45) * mm});
            skLineSegment(sketch, "E1705", {"start": v(-226.27, 194.45) * mm, "end": v(-224.97, 195.42) * mm});
            skLineSegment(sketch, "E1706", {"start": v(-224.97, 195.42) * mm, "end": v(-223.89, 196.61) * mm});
            skLineSegment(sketch, "E1707", {"start": v(-223.89, 196.61) * mm, "end": v(-222.91, 197.8) * mm});
            skLineSegment(sketch, "E1708", {"start": v(-222.91, 197.8) * mm, "end": v(-222.05, 199.1) * mm});
            skLineSegment(sketch, "E1709", {"start": v(-222.05, 199.1) * mm, "end": v(-221.4, 200.62) * mm});
            skLineSegment(sketch, "E1710", {"start": v(-221.4, 200.62) * mm, "end": v(-220.96, 202.13) * mm});
            skLineSegment(sketch, "E1711", {"start": v(-220.96, 202.13) * mm, "end": v(-220.64, 203.65) * mm});
            skLineSegment(sketch, "E1712", {"start": v(-220.64, 203.65) * mm, "end": v(-220.64, 205.16) * mm});
            skLineSegment(sketch, "E1713", {"start": v(-220.64, 205.16) * mm, "end": v(-220.64, 216.2) * mm});
            skLineSegment(sketch, "E1714", {"start": v(-220.64, 216.2) * mm, "end": v(-230.06, 216.2) * mm});
            skLineSegment(sketch, "E1715", {"start": v(-230.06, 216.2) * mm, "end": v(-230.06, 204.51) * mm});
            skLineSegment(sketch, "E1716", {"start": v(-237.3, 204.51) * mm, "end": v(-237.2, 203.65) * mm});
            skLineSegment(sketch, "E1717", {"start": v(-237.2, 203.65) * mm, "end": v(-236.88, 202.89) * mm});
            skLineSegment(sketch, "E1718", {"start": v(-236.88, 202.89) * mm, "end": v(-236.44, 202.24) * mm});
            skLineSegment(sketch, "E1719", {"start": v(-236.44, 202.24) * mm, "end": v(-235.9, 201.6) * mm});
            skLineSegment(sketch, "E1720", {"start": v(-235.9, 201.6) * mm, "end": v(-235.25, 201.16) * mm});
            skLineSegment(sketch, "E1721", {"start": v(-235.25, 201.16) * mm, "end": v(-234.39, 200.94) * mm});
            skLineSegment(sketch, "E1722", {"start": v(-234.39, 200.94) * mm, "end": v(-233.63, 200.83) * mm});
            skLineSegment(sketch, "E1723", {"start": v(-233.63, 200.83) * mm, "end": v(-232.87, 200.94) * mm});
            skLineSegment(sketch, "E1724", {"start": v(-232.87, 200.94) * mm, "end": v(-232.11, 201.16) * mm});
            skLineSegment(sketch, "E1725", {"start": v(-232.11, 201.16) * mm, "end": v(-231.36, 201.6) * mm});
            skLineSegment(sketch, "E1726", {"start": v(-231.36, 201.6) * mm, "end": v(-230.82, 202.24) * mm});
            skLineSegment(sketch, "E1727", {"start": v(-230.82, 202.24) * mm, "end": v(-230.38, 202.89) * mm});
            skLineSegment(sketch, "E1728", {"start": v(-230.38, 202.89) * mm, "end": v(-230.06, 203.65) * mm});
            skLineSegment(sketch, "E1729", {"start": v(-230.06, 203.65) * mm, "end": v(-230.06, 204.51) * mm});
            skLineSegment(sketch, "E1730", {"start": v(-237.3, 204.51) * mm, "end": v(-237.3, 249.97) * mm});
            skLineSegment(sketch, "E1731", {"start": v(-230.06, 249.97) * mm, "end": v(-230.06, 250.84) * mm});
            skLineSegment(sketch, "E1732", {"start": v(-230.06, 250.84) * mm, "end": v(-230.38, 251.6) * mm});
            skLineSegment(sketch, "E1733", {"start": v(-230.38, 251.6) * mm, "end": v(-230.82, 252.25) * mm});
            skLineSegment(sketch, "E1734", {"start": v(-230.82, 252.25) * mm, "end": v(-231.36, 252.78) * mm});
            skLineSegment(sketch, "E1735", {"start": v(-231.36, 252.78) * mm, "end": v(-232.11, 253.22) * mm});
            skLineSegment(sketch, "E1736", {"start": v(-232.11, 253.22) * mm, "end": v(-232.87, 253.54) * mm});
            skLineSegment(sketch, "E1737", {"start": v(-232.87, 253.54) * mm, "end": v(-233.63, 253.65) * mm});
            skLineSegment(sketch, "E1738", {"start": v(-233.63, 253.65) * mm, "end": v(-234.39, 253.54) * mm});
            skLineSegment(sketch, "E1739", {"start": v(-234.39, 253.54) * mm, "end": v(-235.25, 253.22) * mm});
            skLineSegment(sketch, "E1740", {"start": v(-235.25, 253.22) * mm, "end": v(-235.9, 252.78) * mm});
            skLineSegment(sketch, "E1741", {"start": v(-235.9, 252.78) * mm, "end": v(-236.44, 252.25) * mm});
            skLineSegment(sketch, "E1742", {"start": v(-236.44, 252.25) * mm, "end": v(-236.88, 251.6) * mm});
            skLineSegment(sketch, "E1743", {"start": v(-236.88, 251.6) * mm, "end": v(-237.2, 250.84) * mm});
            skLineSegment(sketch, "E1744", {"start": v(-237.2, 250.84) * mm, "end": v(-237.3, 249.97) * mm});
            skLineSegment(sketch, "E1745", {"start": v(-230.06, 249.97) * mm, "end": v(-230.06, 238.28) * mm});
            skLineSegment(sketch, "E1746", {"start": v(-230.06, 238.28) * mm, "end": v(-220.64, 238.28) * mm});
            skLineSegment(sketch, "E1747", {"start": v(-220.64, 238.28) * mm, "end": v(-220.64, 249.22) * mm});
            skLineSegment(sketch, "E1748", {"start": v(-220.64, 249.22) * mm, "end": v(-220.64, 250.84) * mm});
            skLineSegment(sketch, "E1749", {"start": v(-220.64, 250.84) * mm, "end": v(-220.96, 252.36) * mm});
            skLineSegment(sketch, "E1750", {"start": v(-220.96, 252.36) * mm, "end": v(-221.4, 253.87) * mm});
            skLineSegment(sketch, "E1751", {"start": v(-221.4, 253.87) * mm, "end": v(-222.05, 255.28) * mm});
            skLineSegment(sketch, "E1752", {"start": v(-222.05, 255.28) * mm, "end": v(-222.91, 256.68) * mm});
            skLineSegment(sketch, "E1753", {"start": v(-222.91, 256.68) * mm, "end": v(-223.89, 257.87) * mm});
            skLineSegment(sketch, "E1754", {"start": v(-223.89, 257.87) * mm, "end": v(-224.97, 258.96) * mm});
            skLineSegment(sketch, "E1755", {"start": v(-224.97, 258.96) * mm, "end": v(-226.27, 259.93) * mm});
            skLineSegment(sketch, "E1756", {"start": v(-226.27, 259.93) * mm, "end": v(-227.57, 260.8) * mm});
            skLineSegment(sketch, "E1757", {"start": v(-227.57, 260.8) * mm, "end": v(-228.97, 261.45) * mm});
            skLineSegment(sketch, "E1758", {"start": v(-228.97, 261.45) * mm, "end": v(-230.49, 261.88) * mm});
            skLineSegment(sketch, "E1759", {"start": v(-230.49, 261.88) * mm, "end": v(-232.11, 262.2) * mm});
            skLineSegment(sketch, "E1760", {"start": v(-232.11, 262.2) * mm, "end": v(-233.63, 262.3) * mm});
            skLineSegment(sketch, "E1761", {"start": v(-233.63, 262.3) * mm, "end": v(-235.25, 262.2) * mm});
            skLineSegment(sketch, "E1762", {"start": v(-235.25, 262.2) * mm, "end": v(-236.77, 261.88) * mm});
            skLineSegment(sketch, "E1763", {"start": v(-236.77, 261.88) * mm, "end": v(-238.28, 261.45) * mm});
            skLineSegment(sketch, "E1764", {"start": v(-238.28, 261.45) * mm, "end": v(-239.69, 260.8) * mm});
            skLineSegment(sketch, "E1765", {"start": v(-239.69, 260.8) * mm, "end": v(-240.99, 259.93) * mm});
            skLineSegment(sketch, "E1766", {"start": v(-240.99, 259.93) * mm, "end": v(-242.29, 258.96) * mm});
            skLineSegment(sketch, "E1767", {"start": v(-242.29, 258.96) * mm, "end": v(-243.37, 257.87) * mm});
            skLineSegment(sketch, "E1768", {"start": v(-243.37, 257.87) * mm, "end": v(-244.34, 256.68) * mm});
            skLineSegment(sketch, "E1769", {"start": v(-244.34, 256.68) * mm, "end": v(-245.21, 255.28) * mm});
            skLineSegment(sketch, "E1770", {"start": v(-245.21, 255.28) * mm, "end": v(-245.86, 253.87) * mm});
            skLineSegment(sketch, "E1771", {"start": v(-245.86, 253.87) * mm, "end": v(-246.3, 252.36) * mm});
            skLineSegment(sketch, "E1772", {"start": v(-246.3, 252.36) * mm, "end": v(-246.62, 250.84) * mm});
            skLineSegment(sketch, "E1773", {"start": v(-246.62, 250.84) * mm, "end": v(-246.72, 249.22) * mm});
            skLineSegment(sketch, "E1774", {"start": v(-246.72, 249.22) * mm, "end": v(-246.72, 205.16) * mm});
            skLineSegment(sketch, "E1775", {"start": v(-169.99, 205.16) * mm, "end": v(-169.88, 203.65) * mm});
            skLineSegment(sketch, "E1776", {"start": v(-169.88, 203.65) * mm, "end": v(-169.66, 202.13) * mm});
            skLineSegment(sketch, "E1777", {"start": v(-169.66, 202.13) * mm, "end": v(-169.12, 200.62) * mm});
            skLineSegment(sketch, "E1778", {"start": v(-169.12, 200.62) * mm, "end": v(-168.47, 199.1) * mm});
            skLineSegment(sketch, "E1779", {"start": v(-168.47, 199.1) * mm, "end": v(-167.71, 197.8) * mm});
            skLineSegment(sketch, "E1780", {"start": v(-167.71, 197.8) * mm, "end": v(-166.74, 196.61) * mm});
            skLineSegment(sketch, "E1781", {"start": v(-166.74, 196.61) * mm, "end": v(-165.55, 195.42) * mm});
            skLineSegment(sketch, "E1782", {"start": v(-165.55, 195.42) * mm, "end": v(-164.36, 194.45) * mm});
            skLineSegment(sketch, "E1783", {"start": v(-164.36, 194.45) * mm, "end": v(-163.06, 193.69) * mm});
            skLineSegment(sketch, "E1784", {"start": v(-163.06, 193.69) * mm, "end": v(-161.54, 193.04) * mm});
            skLineSegment(sketch, "E1785", {"start": v(-161.54, 193.04) * mm, "end": v(-160.03, 192.5) * mm});
            skLineSegment(sketch, "E1786", {"start": v(-160.03, 192.5) * mm, "end": v(-158.51, 192.28) * mm});
            skLineSegment(sketch, "E1787", {"start": v(-158.51, 192.28) * mm, "end": v(-157, 192.18) * mm});
            skLineSegment(sketch, "E1788", {"start": v(-157, 192.18) * mm, "end": v(-155.37, 192.28) * mm});
            skLineSegment(sketch, "E1789", {"start": v(-155.37, 192.28) * mm, "end": v(-153.86, 192.5) * mm});
            skLineSegment(sketch, "E1790", {"start": v(-153.86, 192.5) * mm, "end": v(-152.34, 193.04) * mm});
            skLineSegment(sketch, "E1791", {"start": v(-152.34, 193.04) * mm, "end": v(-150.94, 193.69) * mm});
            skLineSegment(sketch, "E1792", {"start": v(-150.94, 193.69) * mm, "end": v(-149.53, 194.45) * mm});
            skLineSegment(sketch, "E1793", {"start": v(-149.53, 194.45) * mm, "end": v(-148.34, 195.42) * mm});
            skLineSegment(sketch, "E1794", {"start": v(-148.34, 195.42) * mm, "end": v(-147.15, 196.61) * mm});
            skLineSegment(sketch, "E1795", {"start": v(-147.15, 196.61) * mm, "end": v(-146.17, 197.8) * mm});
            skLineSegment(sketch, "E1796", {"start": v(-146.17, 197.8) * mm, "end": v(-145.42, 199.1) * mm});
            skLineSegment(sketch, "E1797", {"start": v(-145.42, 199.1) * mm, "end": v(-144.77, 200.62) * mm});
            skLineSegment(sketch, "E1798", {"start": v(-144.77, 200.62) * mm, "end": v(-144.33, 202.13) * mm});
            skLineSegment(sketch, "E1799", {"start": v(-144.33, 202.13) * mm, "end": v(-144, 203.65) * mm});
            skLineSegment(sketch, "E1800", {"start": v(-144, 203.65) * mm, "end": v(-143.9, 205.16) * mm});
            skLineSegment(sketch, "E1801", {"start": v(-143.9, 205.16) * mm, "end": v(-143.9, 216.2) * mm});
            skLineSegment(sketch, "E1802", {"start": v(-143.9, 216.2) * mm, "end": v(-153.32, 216.2) * mm});
            skLineSegment(sketch, "E1803", {"start": v(-153.32, 216.2) * mm, "end": v(-153.32, 204.51) * mm});
            skLineSegment(sketch, "E1804", {"start": v(-160.57, 204.51) * mm, "end": v(-160.46, 203.65) * mm});
            skLineSegment(sketch, "E1805", {"start": v(-160.46, 203.65) * mm, "end": v(-160.24, 202.89) * mm});
            skLineSegment(sketch, "E1806", {"start": v(-160.24, 202.89) * mm, "end": v(-159.81, 202.24) * mm});
            skLineSegment(sketch, "E1807", {"start": v(-159.81, 202.24) * mm, "end": v(-159.16, 201.6) * mm});
            skLineSegment(sketch, "E1808", {"start": v(-159.16, 201.6) * mm, "end": v(-158.51, 201.16) * mm});
            skLineSegment(sketch, "E1809", {"start": v(-158.51, 201.16) * mm, "end": v(-157.76, 200.94) * mm});
            skLineSegment(sketch, "E1810", {"start": v(-157.76, 200.94) * mm, "end": v(-157, 200.83) * mm});
            skLineSegment(sketch, "E1811", {"start": v(-157, 200.83) * mm, "end": v(-156.13, 200.94) * mm});
            skLineSegment(sketch, "E1812", {"start": v(-156.13, 200.94) * mm, "end": v(-155.37, 201.16) * mm});
            skLineSegment(sketch, "E1813", {"start": v(-155.37, 201.16) * mm, "end": v(-154.73, 201.6) * mm});
            skLineSegment(sketch, "E1814", {"start": v(-154.73, 201.6) * mm, "end": v(-154.07, 202.24) * mm});
            skLineSegment(sketch, "E1815", {"start": v(-154.07, 202.24) * mm, "end": v(-153.64, 202.89) * mm});
            skLineSegment(sketch, "E1816", {"start": v(-153.64, 202.89) * mm, "end": v(-153.42, 203.65) * mm});
            skLineSegment(sketch, "E1817", {"start": v(-153.42, 203.65) * mm, "end": v(-153.32, 204.51) * mm});
            skLineSegment(sketch, "E1818", {"start": v(-160.57, 204.51) * mm, "end": v(-160.57, 249.97) * mm});
            skLineSegment(sketch, "E1819", {"start": v(-153.32, 249.97) * mm, "end": v(-153.42, 250.84) * mm});
            skLineSegment(sketch, "E1820", {"start": v(-153.42, 250.84) * mm, "end": v(-153.64, 251.6) * mm});
            skLineSegment(sketch, "E1821", {"start": v(-153.64, 251.6) * mm, "end": v(-154.07, 252.25) * mm});
            skLineSegment(sketch, "E1822", {"start": v(-154.07, 252.25) * mm, "end": v(-154.73, 252.78) * mm});
            skLineSegment(sketch, "E1823", {"start": v(-154.73, 252.78) * mm, "end": v(-155.37, 253.22) * mm});
            skLineSegment(sketch, "E1824", {"start": v(-155.37, 253.22) * mm, "end": v(-156.13, 253.54) * mm});
            skLineSegment(sketch, "E1825", {"start": v(-156.13, 253.54) * mm, "end": v(-157, 253.65) * mm});
            skLineSegment(sketch, "E1826", {"start": v(-157, 253.65) * mm, "end": v(-157.76, 253.54) * mm});
            skLineSegment(sketch, "E1827", {"start": v(-157.76, 253.54) * mm, "end": v(-158.51, 253.22) * mm});
            skLineSegment(sketch, "E1828", {"start": v(-158.51, 253.22) * mm, "end": v(-159.16, 252.78) * mm});
            skLineSegment(sketch, "E1829", {"start": v(-159.16, 252.78) * mm, "end": v(-159.81, 252.25) * mm});
            skLineSegment(sketch, "E1830", {"start": v(-159.81, 252.25) * mm, "end": v(-160.24, 251.6) * mm});
            skLineSegment(sketch, "E1831", {"start": v(-160.24, 251.6) * mm, "end": v(-160.46, 250.84) * mm});
            skLineSegment(sketch, "E1832", {"start": v(-160.46, 250.84) * mm, "end": v(-160.57, 249.97) * mm});
            skLineSegment(sketch, "E1833", {"start": v(-153.32, 249.97) * mm, "end": v(-153.32, 238.28) * mm});
            skLineSegment(sketch, "E1834", {"start": v(-153.32, 238.28) * mm, "end": v(-143.9, 238.28) * mm});
            skLineSegment(sketch, "E1835", {"start": v(-143.9, 238.28) * mm, "end": v(-143.9, 249.22) * mm});
            skLineSegment(sketch, "E1836", {"start": v(-143.9, 249.22) * mm, "end": v(-144, 250.84) * mm});
            skLineSegment(sketch, "E1837", {"start": v(-144, 250.84) * mm, "end": v(-144.33, 252.36) * mm});
            skLineSegment(sketch, "E1838", {"start": v(-144.33, 252.36) * mm, "end": v(-144.77, 253.87) * mm});
            skLineSegment(sketch, "E1839", {"start": v(-144.77, 253.87) * mm, "end": v(-145.42, 255.28) * mm});
            skLineSegment(sketch, "E1840", {"start": v(-145.42, 255.28) * mm, "end": v(-146.17, 256.68) * mm});
            skLineSegment(sketch, "E1841", {"start": v(-146.17, 256.68) * mm, "end": v(-147.15, 257.87) * mm});
            skLineSegment(sketch, "E1842", {"start": v(-147.15, 257.87) * mm, "end": v(-148.34, 258.96) * mm});
            skLineSegment(sketch, "E1843", {"start": v(-148.34, 258.96) * mm, "end": v(-149.53, 259.93) * mm});
            skLineSegment(sketch, "E1844", {"start": v(-149.53, 259.93) * mm, "end": v(-150.94, 260.8) * mm});
            skLineSegment(sketch, "E1845", {"start": v(-150.94, 260.8) * mm, "end": v(-152.34, 261.45) * mm});
            skLineSegment(sketch, "E1846", {"start": v(-152.34, 261.45) * mm, "end": v(-153.86, 261.88) * mm});
            skLineSegment(sketch, "E1847", {"start": v(-153.86, 261.88) * mm, "end": v(-155.37, 262.2) * mm});
            skLineSegment(sketch, "E1848", {"start": v(-155.37, 262.2) * mm, "end": v(-157, 262.3) * mm});
            skLineSegment(sketch, "E1849", {"start": v(-157, 262.3) * mm, "end": v(-158.51, 262.2) * mm});
            skLineSegment(sketch, "E1850", {"start": v(-158.51, 262.2) * mm, "end": v(-160.03, 261.88) * mm});
            skLineSegment(sketch, "E1851", {"start": v(-160.03, 261.88) * mm, "end": v(-161.54, 261.45) * mm});
            skLineSegment(sketch, "E1852", {"start": v(-161.54, 261.45) * mm, "end": v(-163.06, 260.8) * mm});
            skLineSegment(sketch, "E1853", {"start": v(-163.06, 260.8) * mm, "end": v(-164.36, 259.93) * mm});
            skLineSegment(sketch, "E1854", {"start": v(-164.36, 259.93) * mm, "end": v(-165.55, 258.96) * mm});
            skLineSegment(sketch, "E1855", {"start": v(-165.55, 258.96) * mm, "end": v(-166.74, 257.87) * mm});
            skLineSegment(sketch, "E1856", {"start": v(-166.74, 257.87) * mm, "end": v(-167.71, 256.68) * mm});
            skLineSegment(sketch, "E1857", {"start": v(-167.71, 256.68) * mm, "end": v(-168.47, 255.28) * mm});
            skLineSegment(sketch, "E1858", {"start": v(-168.47, 255.28) * mm, "end": v(-169.12, 253.87) * mm});
            skLineSegment(sketch, "E1859", {"start": v(-169.12, 253.87) * mm, "end": v(-169.66, 252.36) * mm});
            skLineSegment(sketch, "E1860", {"start": v(-169.66, 252.36) * mm, "end": v(-169.88, 250.84) * mm});
            skLineSegment(sketch, "E1861", {"start": v(-169.88, 250.84) * mm, "end": v(-169.99, 249.22) * mm});
            skLineSegment(sketch, "E1862", {"start": v(-169.99, 249.22) * mm, "end": v(-169.99, 205.16) * mm});
            skLineSegment(sketch, "E1863", {"start": v(129.07, 262.3) * mm, "end": v(119.77, 262.3) * mm});
            skLineSegment(sketch, "E1864", {"start": v(119.77, 262.3) * mm, "end": v(119.77, 192.18) * mm});
            skLineSegment(sketch, "E1865", {"start": v(119.77, 192.18) * mm, "end": v(129.07, 192.18) * mm});
            skLineSegment(sketch, "E1866", {"start": v(129.07, 192.18) * mm, "end": v(129.07, 231.79) * mm});
            skLineSegment(sketch, "E1867", {"start": v(129.07, 231.79) * mm, "end": v(130.05, 231.79) * mm});
            skLineSegment(sketch, "E1868", {"start": v(130.05, 231.79) * mm, "end": v(140.54, 192.18) * mm});
            skLineSegment(sketch, "E1869", {"start": v(140.54, 192.18) * mm, "end": v(149.31, 192.18) * mm});
            skLineSegment(sketch, "E1870", {"start": v(149.31, 192.18) * mm, "end": v(149.31, 262.3) * mm});
            skLineSegment(sketch, "E1871", {"start": v(149.31, 262.3) * mm, "end": v(140.54, 262.3) * mm});
            skLineSegment(sketch, "E1872", {"start": v(140.54, 262.3) * mm, "end": v(140.54, 221.83) * mm});
            skLineSegment(sketch, "E1873", {"start": v(140.54, 221.83) * mm, "end": v(139.36, 221.83) * mm});
            skLineSegment(sketch, "E1874", {"start": v(139.36, 221.83) * mm, "end": v(129.07, 262.3) * mm});
            skLineSegment(sketch, "E1875", {"start": v(57.53, 249.97) * mm, "end": v(57.53, 238.28) * mm});
            skLineSegment(sketch, "E1876", {"start": v(57.53, 238.28) * mm, "end": v(66.95, 238.28) * mm});
            skLineSegment(sketch, "E1877", {"start": v(66.95, 238.28) * mm, "end": v(66.95, 249.22) * mm});
            skLineSegment(sketch, "E1878", {"start": v(66.95, 249.22) * mm, "end": v(66.84, 250.84) * mm});
            skLineSegment(sketch, "E1879", {"start": v(66.84, 250.84) * mm, "end": v(66.62, 252.36) * mm});
            skLineSegment(sketch, "E1880", {"start": v(66.62, 252.36) * mm, "end": v(66.08, 253.87) * mm});
            skLineSegment(sketch, "E1881", {"start": v(66.08, 253.87) * mm, "end": v(65.43, 255.28) * mm});
            skLineSegment(sketch, "E1882", {"start": v(65.43, 255.28) * mm, "end": v(64.67, 256.68) * mm});
            skLineSegment(sketch, "E1883", {"start": v(64.67, 256.68) * mm, "end": v(63.7, 257.87) * mm});
            skLineSegment(sketch, "E1884", {"start": v(63.7, 257.87) * mm, "end": v(62.5, 258.96) * mm});
            skLineSegment(sketch, "E1885", {"start": v(62.5, 258.96) * mm, "end": v(61.31, 259.93) * mm});
            skLineSegment(sketch, "E1886", {"start": v(61.31, 259.93) * mm, "end": v(60.02, 260.8) * mm});
            skLineSegment(sketch, "E1887", {"start": v(60.02, 260.8) * mm, "end": v(58.5, 261.45) * mm});
            skLineSegment(sketch, "E1888", {"start": v(58.5, 261.45) * mm, "end": v(56.99, 261.88) * mm});
            skLineSegment(sketch, "E1889", {"start": v(56.99, 261.88) * mm, "end": v(55.47, 262.2) * mm});
            skLineSegment(sketch, "E1890", {"start": v(55.47, 262.2) * mm, "end": v(53.96, 262.3) * mm});
            skLineSegment(sketch, "E1891", {"start": v(53.96, 262.3) * mm, "end": v(52.33, 262.2) * mm});
            skLineSegment(sketch, "E1892", {"start": v(52.33, 262.2) * mm, "end": v(50.82, 261.88) * mm});
            skLineSegment(sketch, "E1893", {"start": v(50.82, 261.88) * mm, "end": v(49.3, 261.45) * mm});
            skLineSegment(sketch, "E1894", {"start": v(49.3, 261.45) * mm, "end": v(47.9, 260.8) * mm});
            skLineSegment(sketch, "E1895", {"start": v(47.9, 260.8) * mm, "end": v(46.49, 259.93) * mm});
            skLineSegment(sketch, "E1896", {"start": v(46.49, 259.93) * mm, "end": v(45.3, 258.96) * mm});
            skLineSegment(sketch, "E1897", {"start": v(45.3, 258.96) * mm, "end": v(44.1, 257.87) * mm});
            skLineSegment(sketch, "E1898", {"start": v(44.1, 257.87) * mm, "end": v(43.13, 256.68) * mm});
            skLineSegment(sketch, "E1899", {"start": v(43.13, 256.68) * mm, "end": v(42.37, 255.28) * mm});
            skLineSegment(sketch, "E1900", {"start": v(42.37, 255.28) * mm, "end": v(41.73, 253.87) * mm});
            skLineSegment(sketch, "E1901", {"start": v(41.73, 253.87) * mm, "end": v(41.19, 252.36) * mm});
            skLineSegment(sketch, "E1902", {"start": v(41.19, 252.36) * mm, "end": v(40.97, 250.84) * mm});
            skLineSegment(sketch, "E1903", {"start": v(40.97, 250.84) * mm, "end": v(40.86, 249.22) * mm});
            skLineSegment(sketch, "E1904", {"start": v(40.86, 249.22) * mm, "end": v(40.86, 205.16) * mm});
            skLineSegment(sketch, "E1905", {"start": v(40.86, 205.16) * mm, "end": v(40.97, 203.65) * mm});
            skLineSegment(sketch, "E1906", {"start": v(40.97, 203.65) * mm, "end": v(41.19, 202.13) * mm});
            skLineSegment(sketch, "E1907", {"start": v(41.19, 202.13) * mm, "end": v(41.73, 200.62) * mm});
            skLineSegment(sketch, "E1908", {"start": v(41.73, 200.62) * mm, "end": v(42.37, 199.1) * mm});
            skLineSegment(sketch, "E1909", {"start": v(42.37, 199.1) * mm, "end": v(43.13, 197.8) * mm});
            skLineSegment(sketch, "E1910", {"start": v(43.13, 197.8) * mm, "end": v(44.1, 196.61) * mm});
            skLineSegment(sketch, "E1911", {"start": v(44.1, 196.61) * mm, "end": v(45.3, 195.42) * mm});
            skLineSegment(sketch, "E1912", {"start": v(45.3, 195.42) * mm, "end": v(46.49, 194.45) * mm});
            skLineSegment(sketch, "E1913", {"start": v(46.49, 194.45) * mm, "end": v(47.9, 193.69) * mm});
            skLineSegment(sketch, "E1914", {"start": v(47.9, 193.69) * mm, "end": v(49.3, 193.04) * mm});
            skLineSegment(sketch, "E1915", {"start": v(49.3, 193.04) * mm, "end": v(50.82, 192.5) * mm});
            skLineSegment(sketch, "E1916", {"start": v(50.82, 192.5) * mm, "end": v(52.33, 192.28) * mm});
            skLineSegment(sketch, "E1917", {"start": v(52.33, 192.28) * mm, "end": v(53.96, 192.18) * mm});
            skLineSegment(sketch, "E1918", {"start": v(53.96, 192.18) * mm, "end": v(55.04, 192.4) * mm});
            skLineSegment(sketch, "E1919", {"start": v(55.04, 192.4) * mm, "end": v(56.23, 192.71) * mm});
            skLineSegment(sketch, "E1920", {"start": v(56.23, 192.71) * mm, "end": v(57.2, 193.25) * mm});
            skLineSegment(sketch, "E1921", {"start": v(57.2, 193.25) * mm, "end": v(58.18, 194.01) * mm});
            skLineSegment(sketch, "E1922", {"start": v(58.18, 194.01) * mm, "end": v(59.04, 194.88) * mm});
            skLineSegment(sketch, "E1923", {"start": v(59.04, 194.88) * mm, "end": v(59.7, 195.85) * mm});
            skLineSegment(sketch, "E1924", {"start": v(59.7, 195.85) * mm, "end": v(61.42, 194.66) * mm});
            skLineSegment(sketch, "E1925", {"start": v(61.42, 194.66) * mm, "end": v(61.42, 192.18) * mm});
            skLineSegment(sketch, "E1926", {"start": v(61.42, 192.18) * mm, "end": v(66.95, 192.18) * mm});
            skLineSegment(sketch, "E1927", {"start": v(66.95, 192.18) * mm, "end": v(66.95, 226.7) * mm});
            skLineSegment(sketch, "E1928", {"start": v(66.95, 226.7) * mm, "end": v(53.74, 226.7) * mm});
            skLineSegment(sketch, "E1929", {"start": v(53.74, 226.7) * mm, "end": v(53.74, 218.37) * mm});
            skLineSegment(sketch, "E1930", {"start": v(53.74, 218.37) * mm, "end": v(57.53, 218.37) * mm});
            skLineSegment(sketch, "E1931", {"start": v(57.53, 218.37) * mm, "end": v(57.53, 204.51) * mm});
            skLineSegment(sketch, "E1932", {"start": v(50.28, 204.51) * mm, "end": v(50.38, 203.65) * mm});
            skLineSegment(sketch, "E1933", {"start": v(50.38, 203.65) * mm, "end": v(50.6, 202.89) * mm});
            skLineSegment(sketch, "E1934", {"start": v(50.6, 202.89) * mm, "end": v(51.04, 202.24) * mm});
            skLineSegment(sketch, "E1935", {"start": v(51.04, 202.24) * mm, "end": v(51.69, 201.6) * mm});
            skLineSegment(sketch, "E1936", {"start": v(51.69, 201.6) * mm, "end": v(52.33, 201.16) * mm});
            skLineSegment(sketch, "E1937", {"start": v(52.33, 201.16) * mm, "end": v(53.1, 200.94) * mm});
            skLineSegment(sketch, "E1938", {"start": v(53.1, 200.94) * mm, "end": v(53.96, 200.83) * mm});
            skLineSegment(sketch, "E1939", {"start": v(53.96, 200.83) * mm, "end": v(54.72, 200.94) * mm});
            skLineSegment(sketch, "E1940", {"start": v(54.72, 200.94) * mm, "end": v(55.47, 201.16) * mm});
            skLineSegment(sketch, "E1941", {"start": v(55.47, 201.16) * mm, "end": v(56.12, 201.6) * mm});
            skLineSegment(sketch, "E1942", {"start": v(56.12, 201.6) * mm, "end": v(56.77, 202.24) * mm});
            skLineSegment(sketch, "E1943", {"start": v(56.77, 202.24) * mm, "end": v(57.2, 202.89) * mm});
            skLineSegment(sketch, "E1944", {"start": v(57.2, 202.89) * mm, "end": v(57.42, 203.65) * mm});
            skLineSegment(sketch, "E1945", {"start": v(57.42, 203.65) * mm, "end": v(57.53, 204.51) * mm});
            skLineSegment(sketch, "E1946", {"start": v(50.28, 204.51) * mm, "end": v(50.28, 249.97) * mm});
            skLineSegment(sketch, "E1947", {"start": v(57.53, 249.97) * mm, "end": v(57.42, 250.84) * mm});
            skLineSegment(sketch, "E1948", {"start": v(57.42, 250.84) * mm, "end": v(57.2, 251.6) * mm});
            skLineSegment(sketch, "E1949", {"start": v(57.2, 251.6) * mm, "end": v(56.77, 252.25) * mm});
            skLineSegment(sketch, "E1950", {"start": v(56.77, 252.25) * mm, "end": v(56.12, 252.78) * mm});
            skLineSegment(sketch, "E1951", {"start": v(56.12, 252.78) * mm, "end": v(55.47, 253.22) * mm});
            skLineSegment(sketch, "E1952", {"start": v(55.47, 253.22) * mm, "end": v(54.72, 253.54) * mm});
            skLineSegment(sketch, "E1953", {"start": v(54.72, 253.54) * mm, "end": v(53.96, 253.65) * mm});
            skLineSegment(sketch, "E1954", {"start": v(53.96, 253.65) * mm, "end": v(53.1, 253.54) * mm});
            skLineSegment(sketch, "E1955", {"start": v(53.1, 253.54) * mm, "end": v(52.33, 253.22) * mm});
            skLineSegment(sketch, "E1956", {"start": v(52.33, 253.22) * mm, "end": v(51.69, 252.78) * mm});
            skLineSegment(sketch, "E1957", {"start": v(51.69, 252.78) * mm, "end": v(51.04, 252.25) * mm});
            skLineSegment(sketch, "E1958", {"start": v(51.04, 252.25) * mm, "end": v(50.6, 251.6) * mm});
            skLineSegment(sketch, "E1959", {"start": v(50.6, 251.6) * mm, "end": v(50.38, 250.84) * mm});
            skLineSegment(sketch, "E1960", {"start": v(50.38, 250.84) * mm, "end": v(50.28, 249.97) * mm});
            skLineSegment(sketch, "E1961", {"start": v(18.35, 233.41) * mm, "end": v(19.21, 235.14) * mm});
            skLineSegment(sketch, "E1962", {"start": v(19.21, 235.14) * mm, "end": v(19.86, 236.87) * mm});
            skLineSegment(sketch, "E1963", {"start": v(19.86, 236.87) * mm, "end": v(20.18, 238.72) * mm});
            skLineSegment(sketch, "E1964", {"start": v(20.18, 238.72) * mm, "end": v(20.4, 240.66) * mm});
            skLineSegment(sketch, "E1965", {"start": v(20.4, 240.66) * mm, "end": v(20.4, 242.5) * mm});
            skLineSegment(sketch, "E1966", {"start": v(20.4, 242.5) * mm, "end": v(20.18, 244.45) * mm});
            skLineSegment(sketch, "E1967", {"start": v(20.18, 244.45) * mm, "end": v(19.86, 246.3) * mm});
            skLineSegment(sketch, "E1968", {"start": v(19.86, 246.3) * mm, "end": v(19.21, 248.13) * mm});
            skLineSegment(sketch, "E1969", {"start": v(19.21, 248.13) * mm, "end": v(18.35, 249.75) * mm});
            skLineSegment(sketch, "E1970", {"start": v(12.07, 230.81) * mm, "end": v(13.8, 231.14) * mm});
            skLineSegment(sketch, "E1971", {"start": v(13.8, 231.14) * mm, "end": v(15.42, 231.57) * mm});
            skLineSegment(sketch, "E1972", {"start": v(15.42, 231.57) * mm, "end": v(16.94, 232.44) * mm});
            skLineSegment(sketch, "E1973", {"start": v(16.94, 232.44) * mm, "end": v(18.35, 233.41) * mm});
            skLineSegment(sketch, "E1974", {"start": v(12.07, 230.81) * mm, "end": v(12.07, 252.36) * mm});
            skLineSegment(sketch, "E1975", {"start": v(18.35, 249.75) * mm, "end": v(16.94, 250.84) * mm});
            skLineSegment(sketch, "E1976", {"start": v(16.94, 250.84) * mm, "end": v(15.42, 251.6) * mm});
            skLineSegment(sketch, "E1977", {"start": v(15.42, 251.6) * mm, "end": v(13.8, 252.14) * mm});
            skLineSegment(sketch, "E1978", {"start": v(13.8, 252.14) * mm, "end": v(12.07, 252.36) * mm});
            skLineSegment(sketch, "E1979", {"start": v(12.07, 262.3) * mm, "end": v(2.76, 262.3) * mm});
            skLineSegment(sketch, "E1980", {"start": v(2.76, 262.3) * mm, "end": v(2.76, 192.18) * mm});
            skLineSegment(sketch, "E1981", {"start": v(2.76, 192.18) * mm, "end": v(12.07, 192.18) * mm});
            skLineSegment(sketch, "E1982", {"start": v(12.07, 192.18) * mm, "end": v(12.07, 222.8) * mm});
            skLineSegment(sketch, "E1983", {"start": v(12.07, 222.8) * mm, "end": v(12.83, 222.48) * mm});
            skLineSegment(sketch, "E1984", {"start": v(12.83, 222.48) * mm, "end": v(13.59, 222.37) * mm});
            skLineSegment(sketch, "E1985", {"start": v(13.59, 222.37) * mm, "end": v(14.34, 222.48) * mm});
            skLineSegment(sketch, "E1986", {"start": v(14.34, 222.48) * mm, "end": v(15, 222.8) * mm});
            skLineSegment(sketch, "E1987", {"start": v(15, 222.8) * mm, "end": v(20.4, 192.18) * mm});
            skLineSegment(sketch, "E1988", {"start": v(20.4, 192.18) * mm, "end": v(30.14, 192.18) * mm});
            skLineSegment(sketch, "E1989", {"start": v(30.14, 192.18) * mm, "end": v(24.4, 225.5) * mm});
            skLineSegment(sketch, "E1990", {"start": v(24.4, 225.5) * mm, "end": v(25.7, 227.35) * mm});
            skLineSegment(sketch, "E1991", {"start": v(25.7, 227.35) * mm, "end": v(26.9, 229.4) * mm});
            skLineSegment(sketch, "E1992", {"start": v(26.9, 229.4) * mm, "end": v(27.87, 231.46) * mm});
            skLineSegment(sketch, "E1993", {"start": v(27.87, 231.46) * mm, "end": v(28.63, 233.63) * mm});
            skLineSegment(sketch, "E1994", {"start": v(28.63, 233.63) * mm, "end": v(29.28, 235.9) * mm});
            skLineSegment(sketch, "E1995", {"start": v(29.28, 235.9) * mm, "end": v(29.6, 238.17) * mm});
            skLineSegment(sketch, "E1996", {"start": v(29.6, 238.17) * mm, "end": v(29.82, 240.45) * mm});
            skLineSegment(sketch, "E1997", {"start": v(29.82, 240.45) * mm, "end": v(29.82, 242.72) * mm});
            skLineSegment(sketch, "E1998", {"start": v(29.82, 242.72) * mm, "end": v(29.6, 245.1) * mm});
            skLineSegment(sketch, "E1999", {"start": v(29.6, 245.1) * mm, "end": v(29.28, 247.37) * mm});
            skLineSegment(sketch, "E2000", {"start": v(29.28, 247.37) * mm, "end": v(28.63, 249.54) * mm});
            skLineSegment(sketch, "E2001", {"start": v(28.63, 249.54) * mm, "end": v(27.87, 251.7) * mm});
            skLineSegment(sketch, "E2002", {"start": v(27.87, 251.7) * mm, "end": v(26.9, 253.87) * mm});
            skLineSegment(sketch, "E2003", {"start": v(26.9, 253.87) * mm, "end": v(25.7, 255.82) * mm});
            skLineSegment(sketch, "E2004", {"start": v(25.7, 255.82) * mm, "end": v(24.4, 257.77) * mm});
            skLineSegment(sketch, "E2005", {"start": v(24.4, 257.77) * mm, "end": v(22.9, 258.85) * mm});
            skLineSegment(sketch, "E2006", {"start": v(22.9, 258.85) * mm, "end": v(21.16, 259.82) * mm});
            skLineSegment(sketch, "E2007", {"start": v(21.16, 259.82) * mm, "end": v(19.54, 260.69) * mm});
            skLineSegment(sketch, "E2008", {"start": v(19.54, 260.69) * mm, "end": v(17.7, 261.34) * mm});
            skLineSegment(sketch, "E2009", {"start": v(17.7, 261.34) * mm, "end": v(15.86, 261.77) * mm});
            skLineSegment(sketch, "E2010", {"start": v(15.86, 261.77) * mm, "end": v(14.01, 262.1) * mm});
            skLineSegment(sketch, "E2011", {"start": v(14.01, 262.1) * mm, "end": v(12.07, 262.3) * mm});
            skLineSegment(sketch, "E2012", {"start": v(-50.5, 170.52) * mm, "end": v(-40.1, 170.52) * mm});
            skLineSegment(sketch, "E2013", {"start": v(-45.3, 155.16) * mm, "end": v(-41.94, 132.1) * mm});
            skLineSegment(sketch, "E2014", {"start": v(-41.94, 132.1) * mm, "end": v(-48.65, 132.1) * mm});
            skLineSegment(sketch, "E2015", {"start": v(-48.65, 132.1) * mm, "end": v(-45.3, 155.16) * mm});
            skLineSegment(sketch, "E2016", {"start": v(-40.1, 170.52) * mm, "end": v(-50.5, 170.52) * mm});
            skLineSegment(sketch, "E2017", {"start": v(-50.5, 170.52) * mm, "end": v(-59.15, 111.54) * mm});
            skLineSegment(sketch, "E2018", {"start": v(-59.15, 111.54) * mm, "end": v(-51.68, 111.54) * mm});
            skLineSegment(sketch, "E2019", {"start": v(-51.68, 111.54) * mm, "end": v(-49.95, 123.23) * mm});
            skLineSegment(sketch, "E2020", {"start": v(-49.95, 123.23) * mm, "end": v(-40.64, 123.23) * mm});
            skLineSegment(sketch, "E2021", {"start": v(-40.64, 123.23) * mm, "end": v(-38.91, 111.54) * mm});
            skLineSegment(sketch, "E2022", {"start": v(-38.91, 111.54) * mm, "end": v(-31.55, 111.54) * mm});
            skLineSegment(sketch, "E2023", {"start": v(-31.55, 111.54) * mm, "end": v(-40.1, 170.52) * mm});
            skLineSegment(sketch, "E2024", {"start": v(56.55, 170.52) * mm, "end": v(66.95, 170.52) * mm});
            skLineSegment(sketch, "E2025", {"start": v(61.75, 155.16) * mm, "end": v(65.1, 132.1) * mm});
            skLineSegment(sketch, "E2026", {"start": v(65.1, 132.1) * mm, "end": v(58.4, 132.1) * mm});
            skLineSegment(sketch, "E2027", {"start": v(58.4, 132.1) * mm, "end": v(61.75, 155.16) * mm});
            skLineSegment(sketch, "E2028", {"start": v(66.95, 170.52) * mm, "end": v(56.55, 170.52) * mm});
            skLineSegment(sketch, "E2029", {"start": v(56.55, 170.52) * mm, "end": v(48, 111.54) * mm});
            skLineSegment(sketch, "E2030", {"start": v(48, 111.54) * mm, "end": v(55.36, 111.54) * mm});
            skLineSegment(sketch, "E2031", {"start": v(55.36, 111.54) * mm, "end": v(57.1, 123.23) * mm});
            skLineSegment(sketch, "E2032", {"start": v(57.1, 123.23) * mm, "end": v(66.4, 123.23) * mm});
            skLineSegment(sketch, "E2033", {"start": v(66.4, 123.23) * mm, "end": v(68.13, 111.54) * mm});
            skLineSegment(sketch, "E2034", {"start": v(68.13, 111.54) * mm, "end": v(75.6, 111.54) * mm});
            skLineSegment(sketch, "E2035", {"start": v(75.6, 111.54) * mm, "end": v(66.95, 170.52) * mm});
            skLineSegment(sketch, "E2036", {"start": v(133.73, 170.52) * mm, "end": v(144.12, 170.52) * mm});
            skLineSegment(sketch, "E2037", {"start": v(138.92, 155.16) * mm, "end": v(142.28, 132.1) * mm});
            skLineSegment(sketch, "E2038", {"start": v(142.28, 132.1) * mm, "end": v(135.57, 132.1) * mm});
            skLineSegment(sketch, "E2039", {"start": v(135.57, 132.1) * mm, "end": v(138.92, 155.16) * mm});
            skLineSegment(sketch, "E2040", {"start": v(144.12, 170.52) * mm, "end": v(133.73, 170.52) * mm});
            skLineSegment(sketch, "E2041", {"start": v(133.73, 170.52) * mm, "end": v(125.18, 111.54) * mm});
            skLineSegment(sketch, "E2042", {"start": v(125.18, 111.54) * mm, "end": v(132.54, 111.54) * mm});
            skLineSegment(sketch, "E2043", {"start": v(132.54, 111.54) * mm, "end": v(134.27, 123.23) * mm});
            skLineSegment(sketch, "E2044", {"start": v(134.27, 123.23) * mm, "end": v(143.58, 123.23) * mm});
            skLineSegment(sketch, "E2045", {"start": v(143.58, 123.23) * mm, "end": v(145.3, 111.54) * mm});
            skLineSegment(sketch, "E2046", {"start": v(145.3, 111.54) * mm, "end": v(152.78, 111.54) * mm});
            skLineSegment(sketch, "E2047", {"start": v(152.78, 111.54) * mm, "end": v(144.12, 170.52) * mm});
            skLineSegment(sketch, "E2048", {"start": v(-248.03, 122.47) * mm, "end": v(-247.92, 121.06) * mm});
            skLineSegment(sketch, "E2049", {"start": v(-247.92, 121.06) * mm, "end": v(-247.6, 119.65) * mm});
            skLineSegment(sketch, "E2050", {"start": v(-247.6, 119.65) * mm, "end": v(-247.16, 118.25) * mm});
            skLineSegment(sketch, "E2051", {"start": v(-247.16, 118.25) * mm, "end": v(-246.5, 116.95) * mm});
            skLineSegment(sketch, "E2052", {"start": v(-246.5, 116.95) * mm, "end": v(-245.75, 115.76) * mm});
            skLineSegment(sketch, "E2053", {"start": v(-245.75, 115.76) * mm, "end": v(-244.78, 114.68) * mm});
            skLineSegment(sketch, "E2054", {"start": v(-244.78, 114.68) * mm, "end": v(-243.7, 113.8) * mm});
            skLineSegment(sketch, "E2055", {"start": v(-243.7, 113.8) * mm, "end": v(-242.5, 112.95) * mm});
            skLineSegment(sketch, "E2056", {"start": v(-242.5, 112.95) * mm, "end": v(-241.2, 112.3) * mm});
            skLineSegment(sketch, "E2057", {"start": v(-241.2, 112.3) * mm, "end": v(-239.9, 111.86) * mm});
            skLineSegment(sketch, "E2058", {"start": v(-239.9, 111.86) * mm, "end": v(-238.5, 111.54) * mm});
            skLineSegment(sketch, "E2059", {"start": v(-238.5, 111.54) * mm, "end": v(-235.58, 111.54) * mm});
            skLineSegment(sketch, "E2060", {"start": v(-235.58, 111.54) * mm, "end": v(-234.17, 111.86) * mm});
            skLineSegment(sketch, "E2061", {"start": v(-234.17, 111.86) * mm, "end": v(-232.87, 112.3) * mm});
            skLineSegment(sketch, "E2062", {"start": v(-232.87, 112.3) * mm, "end": v(-231.57, 112.95) * mm});
            skLineSegment(sketch, "E2063", {"start": v(-231.57, 112.95) * mm, "end": v(-230.38, 113.8) * mm});
            skLineSegment(sketch, "E2064", {"start": v(-230.38, 113.8) * mm, "end": v(-229.3, 114.68) * mm});
            skLineSegment(sketch, "E2065", {"start": v(-229.3, 114.68) * mm, "end": v(-228.33, 115.76) * mm});
            skLineSegment(sketch, "E2066", {"start": v(-228.33, 115.76) * mm, "end": v(-227.57, 116.95) * mm});
            skLineSegment(sketch, "E2067", {"start": v(-227.57, 116.95) * mm, "end": v(-226.92, 118.25) * mm});
            skLineSegment(sketch, "E2068", {"start": v(-226.92, 118.25) * mm, "end": v(-226.38, 119.65) * mm});
            skLineSegment(sketch, "E2069", {"start": v(-226.38, 119.65) * mm, "end": v(-226.16, 121.06) * mm});
            skLineSegment(sketch, "E2070", {"start": v(-226.16, 121.06) * mm, "end": v(-226.05, 122.47) * mm});
            skLineSegment(sketch, "E2071", {"start": v(-226.05, 122.47) * mm, "end": v(-226.05, 131.67) * mm});
            skLineSegment(sketch, "E2072", {"start": v(-226.05, 131.67) * mm, "end": v(-233.95, 131.67) * mm});
            skLineSegment(sketch, "E2073", {"start": v(-233.95, 131.67) * mm, "end": v(-233.95, 121.82) * mm});
            skLineSegment(sketch, "E2074", {"start": v(-240.12, 121.82) * mm, "end": v(-240.01, 121.06) * mm});
            skLineSegment(sketch, "E2075", {"start": v(-240.01, 121.06) * mm, "end": v(-239.69, 120.3) * mm});
            skLineSegment(sketch, "E2076", {"start": v(-239.69, 120.3) * mm, "end": v(-239.15, 119.65) * mm});
            skLineSegment(sketch, "E2077", {"start": v(-239.15, 119.65) * mm, "end": v(-238.5, 119.22) * mm});
            skLineSegment(sketch, "E2078", {"start": v(-238.5, 119.22) * mm, "end": v(-237.85, 118.9) * mm});
            skLineSegment(sketch, "E2079", {"start": v(-237.85, 118.9) * mm, "end": v(-236.98, 118.79) * mm});
            skLineSegment(sketch, "E2080", {"start": v(-236.98, 118.79) * mm, "end": v(-236.23, 118.9) * mm});
            skLineSegment(sketch, "E2081", {"start": v(-236.23, 118.9) * mm, "end": v(-235.47, 119.22) * mm});
            skLineSegment(sketch, "E2082", {"start": v(-235.47, 119.22) * mm, "end": v(-234.82, 119.65) * mm});
            skLineSegment(sketch, "E2083", {"start": v(-234.82, 119.65) * mm, "end": v(-234.39, 120.3) * mm});
            skLineSegment(sketch, "E2084", {"start": v(-234.39, 120.3) * mm, "end": v(-234.06, 121.06) * mm});
            skLineSegment(sketch, "E2085", {"start": v(-234.06, 121.06) * mm, "end": v(-233.95, 121.82) * mm});
            skLineSegment(sketch, "E2086", {"start": v(-240.12, 121.82) * mm, "end": v(-240.12, 160.14) * mm});
            skLineSegment(sketch, "E2087", {"start": v(-233.95, 160.14) * mm, "end": v(-234.06, 161) * mm});
            skLineSegment(sketch, "E2088", {"start": v(-234.06, 161) * mm, "end": v(-234.39, 161.65) * mm});
            skLineSegment(sketch, "E2089", {"start": v(-234.39, 161.65) * mm, "end": v(-234.82, 162.3) * mm});
            skLineSegment(sketch, "E2090", {"start": v(-234.82, 162.3) * mm, "end": v(-235.47, 162.84) * mm});
            skLineSegment(sketch, "E2091", {"start": v(-235.47, 162.84) * mm, "end": v(-236.23, 163.17) * mm});
            skLineSegment(sketch, "E2092", {"start": v(-236.23, 163.17) * mm, "end": v(-237.85, 163.17) * mm});
            skLineSegment(sketch, "E2093", {"start": v(-237.85, 163.17) * mm, "end": v(-238.5, 162.84) * mm});
            skLineSegment(sketch, "E2094", {"start": v(-238.5, 162.84) * mm, "end": v(-239.15, 162.3) * mm});
            skLineSegment(sketch, "E2095", {"start": v(-239.15, 162.3) * mm, "end": v(-239.69, 161.65) * mm});
            skLineSegment(sketch, "E2096", {"start": v(-239.69, 161.65) * mm, "end": v(-240.01, 161) * mm});
            skLineSegment(sketch, "E2097", {"start": v(-240.01, 161) * mm, "end": v(-240.12, 160.14) * mm});
            skLineSegment(sketch, "E2098", {"start": v(-233.95, 160.14) * mm, "end": v(-233.95, 150.29) * mm});
            skLineSegment(sketch, "E2099", {"start": v(-233.95, 150.29) * mm, "end": v(-226.05, 150.29) * mm});
            skLineSegment(sketch, "E2100", {"start": v(-226.05, 150.29) * mm, "end": v(-226.05, 159.6) * mm});
            skLineSegment(sketch, "E2101", {"start": v(-226.05, 159.6) * mm, "end": v(-226.16, 161) * mm});
            skLineSegment(sketch, "E2102", {"start": v(-226.16, 161) * mm, "end": v(-226.38, 162.4) * mm});
            skLineSegment(sketch, "E2103", {"start": v(-226.38, 162.4) * mm, "end": v(-226.92, 163.7) * mm});
            skLineSegment(sketch, "E2104", {"start": v(-226.92, 163.7) * mm, "end": v(-227.57, 165) * mm});
            skLineSegment(sketch, "E2105", {"start": v(-227.57, 165) * mm, "end": v(-228.33, 166.2) * mm});
            skLineSegment(sketch, "E2106", {"start": v(-228.33, 166.2) * mm, "end": v(-229.3, 167.28) * mm});
            skLineSegment(sketch, "E2107", {"start": v(-229.3, 167.28) * mm, "end": v(-230.38, 168.25) * mm});
            skLineSegment(sketch, "E2108", {"start": v(-230.38, 168.25) * mm, "end": v(-231.57, 169.01) * mm});
            skLineSegment(sketch, "E2109", {"start": v(-231.57, 169.01) * mm, "end": v(-232.87, 169.66) * mm});
            skLineSegment(sketch, "E2110", {"start": v(-232.87, 169.66) * mm, "end": v(-234.17, 170.2) * mm});
            skLineSegment(sketch, "E2111", {"start": v(-234.17, 170.2) * mm, "end": v(-235.58, 170.42) * mm});
            skLineSegment(sketch, "E2112", {"start": v(-235.58, 170.42) * mm, "end": v(-236.98, 170.52) * mm});
            skLineSegment(sketch, "E2113", {"start": v(-236.98, 170.52) * mm, "end": v(-238.5, 170.42) * mm});
            skLineSegment(sketch, "E2114", {"start": v(-238.5, 170.42) * mm, "end": v(-239.9, 170.2) * mm});
            skLineSegment(sketch, "E2115", {"start": v(-239.9, 170.2) * mm, "end": v(-241.2, 169.66) * mm});
            skLineSegment(sketch, "E2116", {"start": v(-241.2, 169.66) * mm, "end": v(-242.5, 169.01) * mm});
            skLineSegment(sketch, "E2117", {"start": v(-242.5, 169.01) * mm, "end": v(-243.7, 168.25) * mm});
            skLineSegment(sketch, "E2118", {"start": v(-243.7, 168.25) * mm, "end": v(-244.78, 167.28) * mm});
            skLineSegment(sketch, "E2119", {"start": v(-244.78, 167.28) * mm, "end": v(-245.75, 166.2) * mm});
            skLineSegment(sketch, "E2120", {"start": v(-245.75, 166.2) * mm, "end": v(-246.5, 165) * mm});
            skLineSegment(sketch, "E2121", {"start": v(-246.5, 165) * mm, "end": v(-247.16, 163.7) * mm});
            skLineSegment(sketch, "E2122", {"start": v(-247.16, 163.7) * mm, "end": v(-247.6, 162.4) * mm});
            skLineSegment(sketch, "E2123", {"start": v(-247.6, 162.4) * mm, "end": v(-247.92, 161) * mm});
            skLineSegment(sketch, "E2124", {"start": v(-247.92, 161) * mm, "end": v(-248.03, 159.6) * mm});
            skLineSegment(sketch, "E2125", {"start": v(-248.03, 159.6) * mm, "end": v(-248.03, 122.47) * mm});
            skLineSegment(sketch, "E2126", {"start": v(-149.64, 122.47) * mm, "end": v(-149.53, 121.06) * mm});
            skLineSegment(sketch, "E2127", {"start": v(-149.53, 121.06) * mm, "end": v(-149.2, 119.65) * mm});
            skLineSegment(sketch, "E2128", {"start": v(-149.2, 119.65) * mm, "end": v(-148.77, 118.25) * mm});
            skLineSegment(sketch, "E2129", {"start": v(-148.77, 118.25) * mm, "end": v(-148.12, 116.95) * mm});
            skLineSegment(sketch, "E2130", {"start": v(-148.12, 116.95) * mm, "end": v(-147.36, 115.76) * mm});
            skLineSegment(sketch, "E2131", {"start": v(-147.36, 115.76) * mm, "end": v(-146.39, 114.68) * mm});
            skLineSegment(sketch, "E2132", {"start": v(-146.39, 114.68) * mm, "end": v(-145.3, 113.8) * mm});
            skLineSegment(sketch, "E2133", {"start": v(-145.3, 113.8) * mm, "end": v(-144.12, 112.95) * mm});
            skLineSegment(sketch, "E2134", {"start": v(-144.12, 112.95) * mm, "end": v(-142.82, 112.3) * mm});
            skLineSegment(sketch, "E2135", {"start": v(-142.82, 112.3) * mm, "end": v(-141.41, 111.86) * mm});
            skLineSegment(sketch, "E2136", {"start": v(-141.41, 111.86) * mm, "end": v(-140, 111.54) * mm});
            skLineSegment(sketch, "E2137", {"start": v(-140, 111.54) * mm, "end": v(-137.19, 111.54) * mm});
            skLineSegment(sketch, "E2138", {"start": v(-137.19, 111.54) * mm, "end": v(-135.78, 111.86) * mm});
            skLineSegment(sketch, "E2139", {"start": v(-135.78, 111.86) * mm, "end": v(-134.37, 112.3) * mm});
            skLineSegment(sketch, "E2140", {"start": v(-134.37, 112.3) * mm, "end": v(-133.08, 112.95) * mm});
            skLineSegment(sketch, "E2141", {"start": v(-133.08, 112.95) * mm, "end": v(-131.89, 113.8) * mm});
            skLineSegment(sketch, "E2142", {"start": v(-131.89, 113.8) * mm, "end": v(-130.8, 114.68) * mm});
            skLineSegment(sketch, "E2143", {"start": v(-130.8, 114.68) * mm, "end": v(-129.94, 115.76) * mm});
            skLineSegment(sketch, "E2144", {"start": v(-129.94, 115.76) * mm, "end": v(-129.07, 116.95) * mm});
            skLineSegment(sketch, "E2145", {"start": v(-129.07, 116.95) * mm, "end": v(-128.42, 118.25) * mm});
            skLineSegment(sketch, "E2146", {"start": v(-128.42, 118.25) * mm, "end": v(-127.99, 119.65) * mm});
            skLineSegment(sketch, "E2147", {"start": v(-127.99, 119.65) * mm, "end": v(-127.77, 121.06) * mm});
            skLineSegment(sketch, "E2148", {"start": v(-127.77, 121.06) * mm, "end": v(-127.66, 122.47) * mm});
            skLineSegment(sketch, "E2149", {"start": v(-127.66, 122.47) * mm, "end": v(-127.66, 131.67) * mm});
            skLineSegment(sketch, "E2150", {"start": v(-127.66, 131.67) * mm, "end": v(-135.57, 131.67) * mm});
            skLineSegment(sketch, "E2151", {"start": v(-135.57, 131.67) * mm, "end": v(-135.57, 121.82) * mm});
            skLineSegment(sketch, "E2152", {"start": v(-141.63, 121.82) * mm, "end": v(-141.52, 121.06) * mm});
            skLineSegment(sketch, "E2153", {"start": v(-141.52, 121.06) * mm, "end": v(-141.3, 120.3) * mm});
            skLineSegment(sketch, "E2154", {"start": v(-141.3, 120.3) * mm, "end": v(-140.76, 119.65) * mm});
            skLineSegment(sketch, "E2155", {"start": v(-140.76, 119.65) * mm, "end": v(-140.11, 119.22) * mm});
            skLineSegment(sketch, "E2156", {"start": v(-140.11, 119.22) * mm, "end": v(-139.36, 118.9) * mm});
            skLineSegment(sketch, "E2157", {"start": v(-139.36, 118.9) * mm, "end": v(-138.6, 118.79) * mm});
            skLineSegment(sketch, "E2158", {"start": v(-138.6, 118.79) * mm, "end": v(-137.84, 118.9) * mm});
            skLineSegment(sketch, "E2159", {"start": v(-137.84, 118.9) * mm, "end": v(-137.08, 119.22) * mm});
            skLineSegment(sketch, "E2160", {"start": v(-137.08, 119.22) * mm, "end": v(-136.43, 119.65) * mm});
            skLineSegment(sketch, "E2161", {"start": v(-136.43, 119.65) * mm, "end": v(-136, 120.3) * mm});
            skLineSegment(sketch, "E2162", {"start": v(-136, 120.3) * mm, "end": v(-135.68, 121.06) * mm});
            skLineSegment(sketch, "E2163", {"start": v(-135.68, 121.06) * mm, "end": v(-135.57, 121.82) * mm});
            skLineSegment(sketch, "E2164", {"start": v(-141.63, 121.82) * mm, "end": v(-141.63, 160.14) * mm});
            skLineSegment(sketch, "E2165", {"start": v(-135.57, 160.14) * mm, "end": v(-135.68, 161) * mm});
            skLineSegment(sketch, "E2166", {"start": v(-135.68, 161) * mm, "end": v(-136, 161.65) * mm});
            skLineSegment(sketch, "E2167", {"start": v(-136, 161.65) * mm, "end": v(-136.43, 162.3) * mm});
            skLineSegment(sketch, "E2168", {"start": v(-136.43, 162.3) * mm, "end": v(-137.08, 162.84) * mm});
            skLineSegment(sketch, "E2169", {"start": v(-137.08, 162.84) * mm, "end": v(-137.84, 163.17) * mm});
            skLineSegment(sketch, "E2170", {"start": v(-137.84, 163.17) * mm, "end": v(-139.36, 163.17) * mm});
            skLineSegment(sketch, "E2171", {"start": v(-139.36, 163.17) * mm, "end": v(-140.11, 162.84) * mm});
            skLineSegment(sketch, "E2172", {"start": v(-140.11, 162.84) * mm, "end": v(-140.76, 162.3) * mm});
            skLineSegment(sketch, "E2173", {"start": v(-140.76, 162.3) * mm, "end": v(-141.3, 161.65) * mm});
            skLineSegment(sketch, "E2174", {"start": v(-141.3, 161.65) * mm, "end": v(-141.52, 161) * mm});
            skLineSegment(sketch, "E2175", {"start": v(-141.52, 161) * mm, "end": v(-141.63, 160.14) * mm});
            skLineSegment(sketch, "E2176", {"start": v(-135.57, 160.14) * mm, "end": v(-135.57, 150.29) * mm});
            skLineSegment(sketch, "E2177", {"start": v(-135.57, 150.29) * mm, "end": v(-127.66, 150.29) * mm});
            skLineSegment(sketch, "E2178", {"start": v(-127.66, 150.29) * mm, "end": v(-127.66, 159.6) * mm});
            skLineSegment(sketch, "E2179", {"start": v(-127.66, 159.6) * mm, "end": v(-127.77, 161) * mm});
            skLineSegment(sketch, "E2180", {"start": v(-127.77, 161) * mm, "end": v(-127.99, 162.4) * mm});
            skLineSegment(sketch, "E2181", {"start": v(-127.99, 162.4) * mm, "end": v(-128.42, 163.7) * mm});
            skLineSegment(sketch, "E2182", {"start": v(-128.42, 163.7) * mm, "end": v(-129.07, 165) * mm});
            skLineSegment(sketch, "E2183", {"start": v(-129.07, 165) * mm, "end": v(-129.94, 166.2) * mm});
            skLineSegment(sketch, "E2184", {"start": v(-129.94, 166.2) * mm, "end": v(-130.8, 167.28) * mm});
            skLineSegment(sketch, "E2185", {"start": v(-130.8, 167.28) * mm, "end": v(-131.89, 168.25) * mm});
            skLineSegment(sketch, "E2186", {"start": v(-131.89, 168.25) * mm, "end": v(-133.08, 169.01) * mm});
            skLineSegment(sketch, "E2187", {"start": v(-133.08, 169.01) * mm, "end": v(-134.37, 169.66) * mm});
            skLineSegment(sketch, "E2188", {"start": v(-134.37, 169.66) * mm, "end": v(-135.78, 170.2) * mm});
            skLineSegment(sketch, "E2189", {"start": v(-135.78, 170.2) * mm, "end": v(-137.19, 170.42) * mm});
            skLineSegment(sketch, "E2190", {"start": v(-137.19, 170.42) * mm, "end": v(-138.6, 170.52) * mm});
            skLineSegment(sketch, "E2191", {"start": v(-138.6, 170.52) * mm, "end": v(-140, 170.42) * mm});
            skLineSegment(sketch, "E2192", {"start": v(-140, 170.42) * mm, "end": v(-141.41, 170.2) * mm});
            skLineSegment(sketch, "E2193", {"start": v(-141.41, 170.2) * mm, "end": v(-142.82, 169.66) * mm});
            skLineSegment(sketch, "E2194", {"start": v(-142.82, 169.66) * mm, "end": v(-144.12, 169.01) * mm});
            skLineSegment(sketch, "E2195", {"start": v(-144.12, 169.01) * mm, "end": v(-145.3, 168.25) * mm});
            skLineSegment(sketch, "E2196", {"start": v(-145.3, 168.25) * mm, "end": v(-146.39, 167.28) * mm});
            skLineSegment(sketch, "E2197", {"start": v(-146.39, 167.28) * mm, "end": v(-147.36, 166.2) * mm});
            skLineSegment(sketch, "E2198", {"start": v(-147.36, 166.2) * mm, "end": v(-148.12, 165) * mm});
            skLineSegment(sketch, "E2199", {"start": v(-148.12, 165) * mm, "end": v(-148.77, 163.7) * mm});
            skLineSegment(sketch, "E2200", {"start": v(-148.77, 163.7) * mm, "end": v(-149.2, 162.4) * mm});
            skLineSegment(sketch, "E2201", {"start": v(-149.2, 162.4) * mm, "end": v(-149.53, 161) * mm});
            skLineSegment(sketch, "E2202", {"start": v(-149.53, 161) * mm, "end": v(-149.64, 159.6) * mm});
            skLineSegment(sketch, "E2203", {"start": v(-149.64, 159.6) * mm, "end": v(-149.64, 122.47) * mm});
            skLineSegment(sketch, "E2204", {"start": v(-167.93, 160.14) * mm, "end": v(-167.93, 121.82) * mm});
            skLineSegment(sketch, "E2205", {"start": v(-174.1, 121.82) * mm, "end": v(-174, 121.06) * mm});
            skLineSegment(sketch, "E2206", {"start": v(-174, 121.06) * mm, "end": v(-173.67, 120.3) * mm});
            skLineSegment(sketch, "E2207", {"start": v(-173.67, 120.3) * mm, "end": v(-173.23, 119.65) * mm});
            skLineSegment(sketch, "E2208", {"start": v(-173.23, 119.65) * mm, "end": v(-172.58, 119.22) * mm});
            skLineSegment(sketch, "E2209", {"start": v(-172.58, 119.22) * mm, "end": v(-171.82, 118.9) * mm});
            skLineSegment(sketch, "E2210", {"start": v(-171.82, 118.9) * mm, "end": v(-171.07, 118.79) * mm});
            skLineSegment(sketch, "E2211", {"start": v(-171.07, 118.79) * mm, "end": v(-170.2, 118.9) * mm});
            skLineSegment(sketch, "E2212", {"start": v(-170.2, 118.9) * mm, "end": v(-169.55, 119.22) * mm});
            skLineSegment(sketch, "E2213", {"start": v(-169.55, 119.22) * mm, "end": v(-168.9, 119.65) * mm});
            skLineSegment(sketch, "E2214", {"start": v(-168.9, 119.65) * mm, "end": v(-168.36, 120.3) * mm});
            skLineSegment(sketch, "E2215", {"start": v(-168.36, 120.3) * mm, "end": v(-168.04, 121.06) * mm});
            skLineSegment(sketch, "E2216", {"start": v(-168.04, 121.06) * mm, "end": v(-167.93, 121.82) * mm});
            skLineSegment(sketch, "E2217", {"start": v(-174.1, 121.82) * mm, "end": v(-174.1, 160.14) * mm});
            skLineSegment(sketch, "E2218", {"start": v(-167.93, 160.14) * mm, "end": v(-168.04, 161) * mm});
            skLineSegment(sketch, "E2219", {"start": v(-168.04, 161) * mm, "end": v(-168.36, 161.65) * mm});
            skLineSegment(sketch, "E2220", {"start": v(-168.36, 161.65) * mm, "end": v(-168.9, 162.3) * mm});
            skLineSegment(sketch, "E2221", {"start": v(-168.9, 162.3) * mm, "end": v(-169.55, 162.84) * mm});
            skLineSegment(sketch, "E2222", {"start": v(-169.55, 162.84) * mm, "end": v(-170.2, 163.17) * mm});
            skLineSegment(sketch, "E2223", {"start": v(-170.2, 163.17) * mm, "end": v(-171.82, 163.17) * mm});
            skLineSegment(sketch, "E2224", {"start": v(-171.82, 163.17) * mm, "end": v(-172.58, 162.84) * mm});
            skLineSegment(sketch, "E2225", {"start": v(-172.58, 162.84) * mm, "end": v(-173.23, 162.3) * mm});
            skLineSegment(sketch, "E2226", {"start": v(-173.23, 162.3) * mm, "end": v(-173.67, 161.65) * mm});
            skLineSegment(sketch, "E2227", {"start": v(-173.67, 161.65) * mm, "end": v(-174, 161) * mm});
            skLineSegment(sketch, "E2228", {"start": v(-174, 161) * mm, "end": v(-174.1, 160.14) * mm});
            skLineSegment(sketch, "E2229", {"start": v(-182, 159.6) * mm, "end": v(-182, 122.47) * mm});
            skLineSegment(sketch, "E2230", {"start": v(-182, 122.47) * mm, "end": v(-181.9, 121.06) * mm});
            skLineSegment(sketch, "E2231", {"start": v(-181.9, 121.06) * mm, "end": v(-181.67, 119.65) * mm});
            skLineSegment(sketch, "E2232", {"start": v(-181.67, 119.65) * mm, "end": v(-181.13, 118.25) * mm});
            skLineSegment(sketch, "E2233", {"start": v(-181.13, 118.25) * mm, "end": v(-180.49, 116.95) * mm});
            skLineSegment(sketch, "E2234", {"start": v(-180.49, 116.95) * mm, "end": v(-179.73, 115.76) * mm});
            skLineSegment(sketch, "E2235", {"start": v(-179.73, 115.76) * mm, "end": v(-178.75, 114.68) * mm});
            skLineSegment(sketch, "E2236", {"start": v(-178.75, 114.68) * mm, "end": v(-177.67, 113.8) * mm});
            skLineSegment(sketch, "E2237", {"start": v(-177.67, 113.8) * mm, "end": v(-176.48, 112.95) * mm});
            skLineSegment(sketch, "E2238", {"start": v(-176.48, 112.95) * mm, "end": v(-175.18, 112.3) * mm});
            skLineSegment(sketch, "E2239", {"start": v(-175.18, 112.3) * mm, "end": v(-173.88, 111.86) * mm});
            skLineSegment(sketch, "E2240", {"start": v(-173.88, 111.86) * mm, "end": v(-172.47, 111.54) * mm});
            skLineSegment(sketch, "E2241", {"start": v(-172.47, 111.54) * mm, "end": v(-169.55, 111.54) * mm});
            skLineSegment(sketch, "E2242", {"start": v(-169.55, 111.54) * mm, "end": v(-168.14, 111.86) * mm});
            skLineSegment(sketch, "E2243", {"start": v(-168.14, 111.86) * mm, "end": v(-166.85, 112.3) * mm});
            skLineSegment(sketch, "E2244", {"start": v(-166.85, 112.3) * mm, "end": v(-165.55, 112.95) * mm});
            skLineSegment(sketch, "E2245", {"start": v(-165.55, 112.95) * mm, "end": v(-164.36, 113.8) * mm});
            skLineSegment(sketch, "E2246", {"start": v(-164.36, 113.8) * mm, "end": v(-163.27, 114.68) * mm});
            skLineSegment(sketch, "E2247", {"start": v(-163.27, 114.68) * mm, "end": v(-162.3, 115.76) * mm});
            skLineSegment(sketch, "E2248", {"start": v(-162.3, 115.76) * mm, "end": v(-161.54, 116.95) * mm});
            skLineSegment(sketch, "E2249", {"start": v(-161.54, 116.95) * mm, "end": v(-160.9, 118.25) * mm});
            skLineSegment(sketch, "E2250", {"start": v(-160.9, 118.25) * mm, "end": v(-160.46, 119.65) * mm});
            skLineSegment(sketch, "E2251", {"start": v(-160.46, 119.65) * mm, "end": v(-160.14, 121.06) * mm});
            skLineSegment(sketch, "E2252", {"start": v(-160.14, 121.06) * mm, "end": v(-160.03, 122.47) * mm});
            skLineSegment(sketch, "E2253", {"start": v(-160.03, 122.47) * mm, "end": v(-160.03, 159.6) * mm});
            skLineSegment(sketch, "E2254", {"start": v(-160.03, 159.6) * mm, "end": v(-160.14, 161) * mm});
            skLineSegment(sketch, "E2255", {"start": v(-160.14, 161) * mm, "end": v(-160.46, 162.4) * mm});
            skLineSegment(sketch, "E2256", {"start": v(-160.46, 162.4) * mm, "end": v(-160.9, 163.7) * mm});
            skLineSegment(sketch, "E2257", {"start": v(-160.9, 163.7) * mm, "end": v(-161.54, 165) * mm});
            skLineSegment(sketch, "E2258", {"start": v(-161.54, 165) * mm, "end": v(-162.3, 166.2) * mm});
            skLineSegment(sketch, "E2259", {"start": v(-162.3, 166.2) * mm, "end": v(-163.27, 167.28) * mm});
            skLineSegment(sketch, "E2260", {"start": v(-163.27, 167.28) * mm, "end": v(-164.36, 168.25) * mm});
            skLineSegment(sketch, "E2261", {"start": v(-164.36, 168.25) * mm, "end": v(-165.55, 169.01) * mm});
            skLineSegment(sketch, "E2262", {"start": v(-165.55, 169.01) * mm, "end": v(-166.85, 169.66) * mm});
            skLineSegment(sketch, "E2263", {"start": v(-166.85, 169.66) * mm, "end": v(-168.14, 170.2) * mm});
            skLineSegment(sketch, "E2264", {"start": v(-168.14, 170.2) * mm, "end": v(-169.55, 170.42) * mm});
            skLineSegment(sketch, "E2265", {"start": v(-169.55, 170.42) * mm, "end": v(-171.07, 170.52) * mm});
            skLineSegment(sketch, "E2266", {"start": v(-171.07, 170.52) * mm, "end": v(-172.47, 170.42) * mm});
            skLineSegment(sketch, "E2267", {"start": v(-172.47, 170.42) * mm, "end": v(-173.88, 170.2) * mm});
            skLineSegment(sketch, "E2268", {"start": v(-173.88, 170.2) * mm, "end": v(-175.18, 169.66) * mm});
            skLineSegment(sketch, "E2269", {"start": v(-175.18, 169.66) * mm, "end": v(-176.48, 169.01) * mm});
            skLineSegment(sketch, "E2270", {"start": v(-176.48, 169.01) * mm, "end": v(-177.67, 168.25) * mm});
            skLineSegment(sketch, "E2271", {"start": v(-177.67, 168.25) * mm, "end": v(-178.75, 167.28) * mm});
            skLineSegment(sketch, "E2272", {"start": v(-178.75, 167.28) * mm, "end": v(-179.73, 166.2) * mm});
            skLineSegment(sketch, "E2273", {"start": v(-179.73, 166.2) * mm, "end": v(-180.49, 165) * mm});
            skLineSegment(sketch, "E2274", {"start": v(-180.49, 165) * mm, "end": v(-181.13, 163.7) * mm});
            skLineSegment(sketch, "E2275", {"start": v(-181.13, 163.7) * mm, "end": v(-181.67, 162.4) * mm});
            skLineSegment(sketch, "E2276", {"start": v(-181.67, 162.4) * mm, "end": v(-181.9, 161) * mm});
            skLineSegment(sketch, "E2277", {"start": v(-181.9, 161) * mm, "end": v(-182, 159.6) * mm});
            skLineSegment(sketch, "E2278", {"start": v(-103.85, 160.14) * mm, "end": v(-103.85, 121.82) * mm});
            skLineSegment(sketch, "E2279", {"start": v(-110.02, 121.82) * mm, "end": v(-109.91, 121.06) * mm});
            skLineSegment(sketch, "E2280", {"start": v(-109.91, 121.06) * mm, "end": v(-109.59, 120.3) * mm});
            skLineSegment(sketch, "E2281", {"start": v(-109.59, 120.3) * mm, "end": v(-109.05, 119.65) * mm});
            skLineSegment(sketch, "E2282", {"start": v(-109.05, 119.65) * mm, "end": v(-108.4, 119.22) * mm});
            skLineSegment(sketch, "E2283", {"start": v(-108.4, 119.22) * mm, "end": v(-107.75, 118.9) * mm});
            skLineSegment(sketch, "E2284", {"start": v(-107.75, 118.9) * mm, "end": v(-106.88, 118.79) * mm});
            skLineSegment(sketch, "E2285", {"start": v(-106.88, 118.79) * mm, "end": v(-106.13, 118.9) * mm});
            skLineSegment(sketch, "E2286", {"start": v(-106.13, 118.9) * mm, "end": v(-105.37, 119.22) * mm});
            skLineSegment(sketch, "E2287", {"start": v(-105.37, 119.22) * mm, "end": v(-104.72, 119.65) * mm});
            skLineSegment(sketch, "E2288", {"start": v(-104.72, 119.65) * mm, "end": v(-104.29, 120.3) * mm});
            skLineSegment(sketch, "E2289", {"start": v(-104.29, 120.3) * mm, "end": v(-103.96, 121.06) * mm});
            skLineSegment(sketch, "E2290", {"start": v(-103.96, 121.06) * mm, "end": v(-103.85, 121.82) * mm});
            skLineSegment(sketch, "E2291", {"start": v(-110.02, 121.82) * mm, "end": v(-110.02, 160.14) * mm});
            skLineSegment(sketch, "E2292", {"start": v(-103.85, 160.14) * mm, "end": v(-103.96, 161) * mm});
            skLineSegment(sketch, "E2293", {"start": v(-103.96, 161) * mm, "end": v(-104.29, 161.65) * mm});
            skLineSegment(sketch, "E2294", {"start": v(-104.29, 161.65) * mm, "end": v(-104.72, 162.3) * mm});
            skLineSegment(sketch, "E2295", {"start": v(-104.72, 162.3) * mm, "end": v(-105.37, 162.84) * mm});
            skLineSegment(sketch, "E2296", {"start": v(-105.37, 162.84) * mm, "end": v(-106.13, 163.17) * mm});
            skLineSegment(sketch, "E2297", {"start": v(-106.13, 163.17) * mm, "end": v(-107.75, 163.17) * mm});
            skLineSegment(sketch, "E2298", {"start": v(-107.75, 163.17) * mm, "end": v(-108.4, 162.84) * mm});
            skLineSegment(sketch, "E2299", {"start": v(-108.4, 162.84) * mm, "end": v(-109.05, 162.3) * mm});
            skLineSegment(sketch, "E2300", {"start": v(-109.05, 162.3) * mm, "end": v(-109.59, 161.65) * mm});
            skLineSegment(sketch, "E2301", {"start": v(-109.59, 161.65) * mm, "end": v(-109.91, 161) * mm});
            skLineSegment(sketch, "E2302", {"start": v(-109.91, 161) * mm, "end": v(-110.02, 160.14) * mm});
            skLineSegment(sketch, "E2303", {"start": v(-117.92, 159.6) * mm, "end": v(-117.92, 122.47) * mm});
            skLineSegment(sketch, "E2304", {"start": v(-117.92, 122.47) * mm, "end": v(-117.82, 121.06) * mm});
            skLineSegment(sketch, "E2305", {"start": v(-117.82, 121.06) * mm, "end": v(-117.5, 119.65) * mm});
            skLineSegment(sketch, "E2306", {"start": v(-117.5, 119.65) * mm, "end": v(-117.06, 118.25) * mm});
            skLineSegment(sketch, "E2307", {"start": v(-117.06, 118.25) * mm, "end": v(-116.4, 116.95) * mm});
            skLineSegment(sketch, "E2308", {"start": v(-116.4, 116.95) * mm, "end": v(-115.65, 115.76) * mm});
            skLineSegment(sketch, "E2309", {"start": v(-115.65, 115.76) * mm, "end": v(-114.68, 114.68) * mm});
            skLineSegment(sketch, "E2310", {"start": v(-114.68, 114.68) * mm, "end": v(-113.6, 113.8) * mm});
            skLineSegment(sketch, "E2311", {"start": v(-113.6, 113.8) * mm, "end": v(-112.4, 112.95) * mm});
            skLineSegment(sketch, "E2312", {"start": v(-112.4, 112.95) * mm, "end": v(-111.1, 112.3) * mm});
            skLineSegment(sketch, "E2313", {"start": v(-111.1, 112.3) * mm, "end": v(-109.8, 111.86) * mm});
            skLineSegment(sketch, "E2314", {"start": v(-109.8, 111.86) * mm, "end": v(-108.4, 111.54) * mm});
            skLineSegment(sketch, "E2315", {"start": v(-108.4, 111.54) * mm, "end": v(-105.48, 111.54) * mm});
            skLineSegment(sketch, "E2316", {"start": v(-105.48, 111.54) * mm, "end": v(-104.07, 111.86) * mm});
            skLineSegment(sketch, "E2317", {"start": v(-104.07, 111.86) * mm, "end": v(-102.66, 112.3) * mm});
            skLineSegment(sketch, "E2318", {"start": v(-102.66, 112.3) * mm, "end": v(-101.47, 112.95) * mm});
            skLineSegment(sketch, "E2319", {"start": v(-101.47, 112.95) * mm, "end": v(-100.28, 113.8) * mm});
            skLineSegment(sketch, "E2320", {"start": v(-100.28, 113.8) * mm, "end": v(-99.2, 114.68) * mm});
            skLineSegment(sketch, "E2321", {"start": v(-99.2, 114.68) * mm, "end": v(-98.23, 115.76) * mm});
            skLineSegment(sketch, "E2322", {"start": v(-98.23, 115.76) * mm, "end": v(-97.36, 116.95) * mm});
            skLineSegment(sketch, "E2323", {"start": v(-97.36, 116.95) * mm, "end": v(-96.82, 118.25) * mm});
            skLineSegment(sketch, "E2324", {"start": v(-96.82, 118.25) * mm, "end": v(-96.28, 119.65) * mm});
            skLineSegment(sketch, "E2325", {"start": v(-96.28, 119.65) * mm, "end": v(-96.06, 121.06) * mm});
            skLineSegment(sketch, "E2326", {"start": v(-96.06, 121.06) * mm, "end": v(-95.95, 122.47) * mm});
            skLineSegment(sketch, "E2327", {"start": v(-95.95, 122.47) * mm, "end": v(-95.95, 159.6) * mm});
            skLineSegment(sketch, "E2328", {"start": v(-95.95, 159.6) * mm, "end": v(-96.06, 161) * mm});
            skLineSegment(sketch, "E2329", {"start": v(-96.06, 161) * mm, "end": v(-96.28, 162.4) * mm});
            skLineSegment(sketch, "E2330", {"start": v(-96.28, 162.4) * mm, "end": v(-96.82, 163.7) * mm});
            skLineSegment(sketch, "E2331", {"start": v(-96.82, 163.7) * mm, "end": v(-97.36, 165) * mm});
            skLineSegment(sketch, "E2332", {"start": v(-97.36, 165) * mm, "end": v(-98.23, 166.2) * mm});
            skLineSegment(sketch, "E2333", {"start": v(-98.23, 166.2) * mm, "end": v(-99.2, 167.28) * mm});
            skLineSegment(sketch, "E2334", {"start": v(-99.2, 167.28) * mm, "end": v(-100.28, 168.25) * mm});
            skLineSegment(sketch, "E2335", {"start": v(-100.28, 168.25) * mm, "end": v(-101.47, 169.01) * mm});
            skLineSegment(sketch, "E2336", {"start": v(-101.47, 169.01) * mm, "end": v(-102.66, 169.66) * mm});
            skLineSegment(sketch, "E2337", {"start": v(-102.66, 169.66) * mm, "end": v(-104.07, 170.2) * mm});
            skLineSegment(sketch, "E2338", {"start": v(-104.07, 170.2) * mm, "end": v(-105.48, 170.42) * mm});
            skLineSegment(sketch, "E2339", {"start": v(-105.48, 170.42) * mm, "end": v(-106.88, 170.52) * mm});
            skLineSegment(sketch, "E2340", {"start": v(-106.88, 170.52) * mm, "end": v(-108.4, 170.42) * mm});
            skLineSegment(sketch, "E2341", {"start": v(-108.4, 170.42) * mm, "end": v(-109.8, 170.2) * mm});
            skLineSegment(sketch, "E2342", {"start": v(-109.8, 170.2) * mm, "end": v(-111.1, 169.66) * mm});
            skLineSegment(sketch, "E2343", {"start": v(-111.1, 169.66) * mm, "end": v(-112.4, 169.01) * mm});
            skLineSegment(sketch, "E2344", {"start": v(-112.4, 169.01) * mm, "end": v(-113.6, 168.25) * mm});
            skLineSegment(sketch, "E2345", {"start": v(-113.6, 168.25) * mm, "end": v(-114.68, 167.28) * mm});
            skLineSegment(sketch, "E2346", {"start": v(-114.68, 167.28) * mm, "end": v(-115.65, 166.2) * mm});
            skLineSegment(sketch, "E2347", {"start": v(-115.65, 166.2) * mm, "end": v(-116.4, 165) * mm});
            skLineSegment(sketch, "E2348", {"start": v(-116.4, 165) * mm, "end": v(-117.06, 163.7) * mm});
            skLineSegment(sketch, "E2349", {"start": v(-117.06, 163.7) * mm, "end": v(-117.5, 162.4) * mm});
            skLineSegment(sketch, "E2350", {"start": v(-117.5, 162.4) * mm, "end": v(-117.82, 161) * mm});
            skLineSegment(sketch, "E2351", {"start": v(-117.82, 161) * mm, "end": v(-117.92, 159.6) * mm});
            skLineSegment(sketch, "E2352", {"start": v(240.55, 160.14) * mm, "end": v(240.55, 121.82) * mm});
            skLineSegment(sketch, "E2353", {"start": v(234.5, 121.82) * mm, "end": v(234.6, 121.06) * mm});
            skLineSegment(sketch, "E2354", {"start": v(234.6, 121.06) * mm, "end": v(234.93, 120.3) * mm});
            skLineSegment(sketch, "E2355", {"start": v(234.93, 120.3) * mm, "end": v(235.36, 119.65) * mm});
            skLineSegment(sketch, "E2356", {"start": v(235.36, 119.65) * mm, "end": v(236.01, 119.22) * mm});
            skLineSegment(sketch, "E2357", {"start": v(236.01, 119.22) * mm, "end": v(236.77, 118.9) * mm});
            skLineSegment(sketch, "E2358", {"start": v(236.77, 118.9) * mm, "end": v(237.52, 118.79) * mm});
            skLineSegment(sketch, "E2359", {"start": v(237.52, 118.79) * mm, "end": v(238.4, 118.9) * mm});
            skLineSegment(sketch, "E2360", {"start": v(238.4, 118.9) * mm, "end": v(239.04, 119.22) * mm});
            skLineSegment(sketch, "E2361", {"start": v(239.04, 119.22) * mm, "end": v(239.7, 119.65) * mm});
            skLineSegment(sketch, "E2362", {"start": v(239.7, 119.65) * mm, "end": v(240.23, 120.3) * mm});
            skLineSegment(sketch, "E2363", {"start": v(240.23, 120.3) * mm, "end": v(240.55, 121.06) * mm});
            skLineSegment(sketch, "E2364", {"start": v(240.55, 121.06) * mm, "end": v(240.55, 121.82) * mm});
            skLineSegment(sketch, "E2365", {"start": v(234.5, 121.82) * mm, "end": v(234.5, 160.14) * mm});
            skLineSegment(sketch, "E2366", {"start": v(240.55, 160.14) * mm, "end": v(240.55, 161) * mm});
            skLineSegment(sketch, "E2367", {"start": v(240.55, 161) * mm, "end": v(240.23, 161.65) * mm});
            skLineSegment(sketch, "E2368", {"start": v(240.23, 161.65) * mm, "end": v(239.7, 162.3) * mm});
            skLineSegment(sketch, "E2369", {"start": v(239.7, 162.3) * mm, "end": v(239.04, 162.84) * mm});
            skLineSegment(sketch, "E2370", {"start": v(239.04, 162.84) * mm, "end": v(238.4, 163.17) * mm});
            skLineSegment(sketch, "E2371", {"start": v(238.4, 163.17) * mm, "end": v(236.77, 163.17) * mm});
            skLineSegment(sketch, "E2372", {"start": v(236.77, 163.17) * mm, "end": v(236.01, 162.84) * mm});
            skLineSegment(sketch, "E2373", {"start": v(236.01, 162.84) * mm, "end": v(235.36, 162.3) * mm});
            skLineSegment(sketch, "E2374", {"start": v(235.36, 162.3) * mm, "end": v(234.93, 161.65) * mm});
            skLineSegment(sketch, "E2375", {"start": v(234.93, 161.65) * mm, "end": v(234.6, 161) * mm});
            skLineSegment(sketch, "E2376", {"start": v(234.6, 161) * mm, "end": v(234.5, 160.14) * mm});
            skLineSegment(sketch, "E2377", {"start": v(226.6, 159.6) * mm, "end": v(226.6, 122.47) * mm});
            skLineSegment(sketch, "E2378", {"start": v(226.6, 122.47) * mm, "end": v(226.7, 121.06) * mm});
            skLineSegment(sketch, "E2379", {"start": v(226.7, 121.06) * mm, "end": v(226.92, 119.65) * mm});
            skLineSegment(sketch, "E2380", {"start": v(226.92, 119.65) * mm, "end": v(227.46, 118.25) * mm});
            skLineSegment(sketch, "E2381", {"start": v(227.46, 118.25) * mm, "end": v(228, 116.95) * mm});
            skLineSegment(sketch, "E2382", {"start": v(228, 116.95) * mm, "end": v(228.87, 115.76) * mm});
            skLineSegment(sketch, "E2383", {"start": v(228.87, 115.76) * mm, "end": v(229.84, 114.68) * mm});
            skLineSegment(sketch, "E2384", {"start": v(229.84, 114.68) * mm, "end": v(230.92, 113.8) * mm});
            skLineSegment(sketch, "E2385", {"start": v(230.92, 113.8) * mm, "end": v(232.12, 112.95) * mm});
            skLineSegment(sketch, "E2386", {"start": v(232.12, 112.95) * mm, "end": v(233.3, 112.3) * mm});
            skLineSegment(sketch, "E2387", {"start": v(233.3, 112.3) * mm, "end": v(234.71, 111.86) * mm});
            skLineSegment(sketch, "E2388", {"start": v(234.71, 111.86) * mm, "end": v(236.12, 111.54) * mm});
            skLineSegment(sketch, "E2389", {"start": v(236.12, 111.54) * mm, "end": v(239.04, 111.54) * mm});
            skLineSegment(sketch, "E2390", {"start": v(239.04, 111.54) * mm, "end": v(240.45, 111.86) * mm});
            skLineSegment(sketch, "E2391", {"start": v(240.45, 111.86) * mm, "end": v(241.75, 112.3) * mm});
            skLineSegment(sketch, "E2392", {"start": v(241.75, 112.3) * mm, "end": v(243.05, 112.95) * mm});
            skLineSegment(sketch, "E2393", {"start": v(243.05, 112.95) * mm, "end": v(244.24, 113.8) * mm});
            skLineSegment(sketch, "E2394", {"start": v(244.24, 113.8) * mm, "end": v(245.32, 114.68) * mm});
            skLineSegment(sketch, "E2395", {"start": v(245.32, 114.68) * mm, "end": v(246.3, 115.76) * mm});
            skLineSegment(sketch, "E2396", {"start": v(246.3, 115.76) * mm, "end": v(247.05, 116.95) * mm});
            skLineSegment(sketch, "E2397", {"start": v(247.05, 116.95) * mm, "end": v(247.7, 118.25) * mm});
            skLineSegment(sketch, "E2398", {"start": v(247.7, 118.25) * mm, "end": v(248.14, 119.65) * mm});
            skLineSegment(sketch, "E2399", {"start": v(248.14, 119.65) * mm, "end": v(248.46, 121.06) * mm});
            skLineSegment(sketch, "E2400", {"start": v(248.46, 121.06) * mm, "end": v(248.57, 122.47) * mm});
            skLineSegment(sketch, "E2401", {"start": v(248.57, 122.47) * mm, "end": v(248.57, 159.6) * mm});
            skLineSegment(sketch, "E2402", {"start": v(248.57, 159.6) * mm, "end": v(248.46, 161) * mm});
            skLineSegment(sketch, "E2403", {"start": v(248.46, 161) * mm, "end": v(248.14, 162.4) * mm});
            skLineSegment(sketch, "E2404", {"start": v(248.14, 162.4) * mm, "end": v(247.7, 163.7) * mm});
            skLineSegment(sketch, "E2405", {"start": v(247.7, 163.7) * mm, "end": v(247.05, 165) * mm});
            skLineSegment(sketch, "E2406", {"start": v(247.05, 165) * mm, "end": v(246.3, 166.2) * mm});
            skLineSegment(sketch, "E2407", {"start": v(246.3, 166.2) * mm, "end": v(245.32, 167.28) * mm});
            skLineSegment(sketch, "E2408", {"start": v(245.32, 167.28) * mm, "end": v(244.24, 168.25) * mm});
            skLineSegment(sketch, "E2409", {"start": v(244.24, 168.25) * mm, "end": v(243.05, 169.01) * mm});
            skLineSegment(sketch, "E2410", {"start": v(243.05, 169.01) * mm, "end": v(241.75, 169.66) * mm});
            skLineSegment(sketch, "E2411", {"start": v(241.75, 169.66) * mm, "end": v(240.45, 170.2) * mm});
            skLineSegment(sketch, "E2412", {"start": v(240.45, 170.2) * mm, "end": v(239.04, 170.42) * mm});
            skLineSegment(sketch, "E2413", {"start": v(239.04, 170.42) * mm, "end": v(237.52, 170.52) * mm});
            skLineSegment(sketch, "E2414", {"start": v(237.52, 170.52) * mm, "end": v(236.12, 170.42) * mm});
            skLineSegment(sketch, "E2415", {"start": v(236.12, 170.42) * mm, "end": v(234.71, 170.2) * mm});
            skLineSegment(sketch, "E2416", {"start": v(234.71, 170.2) * mm, "end": v(233.3, 169.66) * mm});
            skLineSegment(sketch, "E2417", {"start": v(233.3, 169.66) * mm, "end": v(232.12, 169.01) * mm});
            skLineSegment(sketch, "E2418", {"start": v(232.12, 169.01) * mm, "end": v(230.92, 168.25) * mm});
            skLineSegment(sketch, "E2419", {"start": v(230.92, 168.25) * mm, "end": v(229.84, 167.28) * mm});
            skLineSegment(sketch, "E2420", {"start": v(229.84, 167.28) * mm, "end": v(228.87, 166.2) * mm});
            skLineSegment(sketch, "E2421", {"start": v(228.87, 166.2) * mm, "end": v(228, 165) * mm});
            skLineSegment(sketch, "E2422", {"start": v(228, 165) * mm, "end": v(227.46, 163.7) * mm});
            skLineSegment(sketch, "E2423", {"start": v(227.46, 163.7) * mm, "end": v(226.92, 162.4) * mm});
            skLineSegment(sketch, "E2424", {"start": v(226.92, 162.4) * mm, "end": v(226.7, 161) * mm});
            skLineSegment(sketch, "E2425", {"start": v(226.7, 161) * mm, "end": v(226.6, 159.6) * mm});
            skLineSegment(sketch, "E2426", {"start": v(-192.93, 170.52) * mm, "end": v(-200.94, 170.52) * mm});
            skLineSegment(sketch, "E2427", {"start": v(-200.94, 170.52) * mm, "end": v(-200.94, 145.63) * mm});
            skLineSegment(sketch, "E2428", {"start": v(-200.94, 145.63) * mm, "end": v(-208.2, 145.63) * mm});
            skLineSegment(sketch, "E2429", {"start": v(-208.2, 145.63) * mm, "end": v(-208.2, 170.52) * mm});
            skLineSegment(sketch, "E2430", {"start": v(-208.2, 170.52) * mm, "end": v(-215.88, 170.52) * mm});
            skLineSegment(sketch, "E2431", {"start": v(-215.88, 170.52) * mm, "end": v(-215.88, 111.54) * mm});
            skLineSegment(sketch, "E2432", {"start": v(-215.88, 111.54) * mm, "end": v(-208.2, 111.54) * mm});
            skLineSegment(sketch, "E2433", {"start": v(-208.2, 111.54) * mm, "end": v(-208.2, 137.2) * mm});
            skLineSegment(sketch, "E2434", {"start": v(-208.2, 137.2) * mm, "end": v(-200.94, 137.2) * mm});
            skLineSegment(sketch, "E2435", {"start": v(-200.94, 137.2) * mm, "end": v(-200.94, 111.54) * mm});
            skLineSegment(sketch, "E2436", {"start": v(-200.94, 111.54) * mm, "end": v(-192.93, 111.54) * mm});
            skLineSegment(sketch, "E2437", {"start": v(-192.93, 111.54) * mm, "end": v(-192.93, 170.52) * mm});
            skLineSegment(sketch, "E2438", {"start": v(-77.23, 170.52) * mm, "end": v(-85.35, 170.52) * mm});
            skLineSegment(sketch, "E2439", {"start": v(-85.35, 170.52) * mm, "end": v(-85.35, 111.54) * mm});
            skLineSegment(sketch, "E2440", {"start": v(-85.35, 111.54) * mm, "end": v(-65.86, 111.54) * mm});
            skLineSegment(sketch, "E2441", {"start": v(-65.86, 111.54) * mm, "end": v(-65.86, 118.9) * mm});
            skLineSegment(sketch, "E2442", {"start": v(-65.86, 118.9) * mm, "end": v(-77.23, 118.9) * mm});
            skLineSegment(sketch, "E2443", {"start": v(-77.23, 118.9) * mm, "end": v(-77.23, 170.52) * mm});
            skLineSegment(sketch, "E2444", {"start": v(24.3, 170.52) * mm, "end": v(5.03, 170.52) * mm});
            skLineSegment(sketch, "E2445", {"start": v(5.03, 170.52) * mm, "end": v(5.03, 111.54) * mm});
            skLineSegment(sketch, "E2446", {"start": v(5.03, 111.54) * mm, "end": v(24.3, 111.54) * mm});
            skLineSegment(sketch, "E2447", {"start": v(24.3, 111.54) * mm, "end": v(24.3, 119.65) * mm});
            skLineSegment(sketch, "E2448", {"start": v(24.3, 119.65) * mm, "end": v(13.04, 119.65) * mm});
            skLineSegment(sketch, "E2449", {"start": v(13.04, 119.65) * mm, "end": v(13.04, 136.76) * mm});
            skLineSegment(sketch, "E2450", {"start": v(13.04, 136.76) * mm, "end": v(21.16, 136.76) * mm});
            skLineSegment(sketch, "E2451", {"start": v(21.16, 136.76) * mm, "end": v(21.16, 145.52) * mm});
            skLineSegment(sketch, "E2452", {"start": v(21.16, 145.52) * mm, "end": v(13.04, 145.52) * mm});
            skLineSegment(sketch, "E2453", {"start": v(13.04, 145.52) * mm, "end": v(13.04, 161) * mm});
            skLineSegment(sketch, "E2454", {"start": v(13.04, 161) * mm, "end": v(24.3, 161) * mm});
            skLineSegment(sketch, "E2455", {"start": v(24.3, 161) * mm, "end": v(24.3, 170.52) * mm});
            skLineSegment(sketch, "E2456", {"start": v(-3.08, 170.52) * mm, "end": v(-27.11, 170.52) * mm});
            skLineSegment(sketch, "E2457", {"start": v(-27.11, 170.52) * mm, "end": v(-27.11, 161) * mm});
            skLineSegment(sketch, "E2458", {"start": v(-27.11, 161) * mm, "end": v(-19.54, 161) * mm});
            skLineSegment(sketch, "E2459", {"start": v(-19.54, 161) * mm, "end": v(-19.54, 111.54) * mm});
            skLineSegment(sketch, "E2460", {"start": v(-19.54, 111.54) * mm, "end": v(-11.2, 111.54) * mm});
            skLineSegment(sketch, "E2461", {"start": v(-11.2, 111.54) * mm, "end": v(-11.2, 161) * mm});
            skLineSegment(sketch, "E2462", {"start": v(-11.2, 161) * mm, "end": v(-3.08, 161) * mm});
            skLineSegment(sketch, "E2463", {"start": v(-3.08, 161) * mm, "end": v(-3.08, 170.52) * mm});
            skLineSegment(sketch, "E2464", {"start": v(94.65, 170.52) * mm, "end": v(85.02, 170.52) * mm});
            skLineSegment(sketch, "E2465", {"start": v(85.02, 170.52) * mm, "end": v(85.02, 111.54) * mm});
            skLineSegment(sketch, "E2466", {"start": v(85.02, 111.54) * mm, "end": v(92.27, 111.54) * mm});
            skLineSegment(sketch, "E2467", {"start": v(92.27, 111.54) * mm, "end": v(92.27, 151.26) * mm});
            skLineSegment(sketch, "E2468", {"start": v(92.27, 151.26) * mm, "end": v(92.92, 151.26) * mm});
            skLineSegment(sketch, "E2469", {"start": v(92.92, 151.26) * mm, "end": v(98.88, 111.54) * mm});
            skLineSegment(sketch, "E2470", {"start": v(98.88, 111.54) * mm, "end": v(102.34, 111.54) * mm});
            skLineSegment(sketch, "E2471", {"start": v(102.34, 111.54) * mm, "end": v(108.18, 151.26) * mm});
            skLineSegment(sketch, "E2472", {"start": v(108.18, 151.26) * mm, "end": v(108.83, 151.26) * mm});
            skLineSegment(sketch, "E2473", {"start": v(108.83, 151.26) * mm, "end": v(108.83, 111.54) * mm});
            skLineSegment(sketch, "E2474", {"start": v(108.83, 111.54) * mm, "end": v(116.08, 111.54) * mm});
            skLineSegment(sketch, "E2475", {"start": v(116.08, 111.54) * mm, "end": v(116.08, 170.52) * mm});
            skLineSegment(sketch, "E2476", {"start": v(116.08, 170.52) * mm, "end": v(106.45, 170.52) * mm});
            skLineSegment(sketch, "E2477", {"start": v(106.45, 170.52) * mm, "end": v(101.15, 140.65) * mm});
            skLineSegment(sketch, "E2478", {"start": v(101.15, 140.65) * mm, "end": v(99.96, 140.65) * mm});
            skLineSegment(sketch, "E2479", {"start": v(99.96, 140.65) * mm, "end": v(94.65, 170.52) * mm});
            skLineSegment(sketch, "E2480", {"start": v(208.09, 160.14) * mm, "end": v(208.09, 150.29) * mm});
            skLineSegment(sketch, "E2481", {"start": v(208.09, 150.29) * mm, "end": v(215.99, 150.29) * mm});
            skLineSegment(sketch, "E2482", {"start": v(215.99, 150.29) * mm, "end": v(215.99, 159.6) * mm});
            skLineSegment(sketch, "E2483", {"start": v(215.99, 159.6) * mm, "end": v(215.88, 161) * mm});
            skLineSegment(sketch, "E2484", {"start": v(215.88, 161) * mm, "end": v(215.66, 162.4) * mm});
            skLineSegment(sketch, "E2485", {"start": v(215.66, 162.4) * mm, "end": v(215.12, 163.7) * mm});
            skLineSegment(sketch, "E2486", {"start": v(215.12, 163.7) * mm, "end": v(214.58, 165) * mm});
            skLineSegment(sketch, "E2487", {"start": v(214.58, 165) * mm, "end": v(213.71, 166.2) * mm});
            skLineSegment(sketch, "E2488", {"start": v(213.71, 166.2) * mm, "end": v(212.74, 167.28) * mm});
            skLineSegment(sketch, "E2489", {"start": v(212.74, 167.28) * mm, "end": v(211.77, 168.25) * mm});
            skLineSegment(sketch, "E2490", {"start": v(211.77, 168.25) * mm, "end": v(210.47, 169.01) * mm});
            skLineSegment(sketch, "E2491", {"start": v(210.47, 169.01) * mm, "end": v(209.28, 169.66) * mm});
            skLineSegment(sketch, "E2492", {"start": v(209.28, 169.66) * mm, "end": v(207.87, 170.2) * mm});
            skLineSegment(sketch, "E2493", {"start": v(207.87, 170.2) * mm, "end": v(206.46, 170.42) * mm});
            skLineSegment(sketch, "E2494", {"start": v(206.46, 170.42) * mm, "end": v(205.06, 170.52) * mm});
            skLineSegment(sketch, "E2495", {"start": v(205.06, 170.52) * mm, "end": v(203.54, 170.42) * mm});
            skLineSegment(sketch, "E2496", {"start": v(203.54, 170.42) * mm, "end": v(202.13, 170.2) * mm});
            skLineSegment(sketch, "E2497", {"start": v(202.13, 170.2) * mm, "end": v(200.83, 169.66) * mm});
            skLineSegment(sketch, "E2498", {"start": v(200.83, 169.66) * mm, "end": v(199.53, 169.01) * mm});
            skLineSegment(sketch, "E2499", {"start": v(199.53, 169.01) * mm, "end": v(198.35, 168.25) * mm});
            skLineSegment(sketch, "E2500", {"start": v(198.35, 168.25) * mm, "end": v(197.26, 167.28) * mm});
            skLineSegment(sketch, "E2501", {"start": v(197.26, 167.28) * mm, "end": v(196.29, 166.2) * mm});
            skLineSegment(sketch, "E2502", {"start": v(196.29, 166.2) * mm, "end": v(195.53, 165) * mm});
            skLineSegment(sketch, "E2503", {"start": v(195.53, 165) * mm, "end": v(194.88, 163.7) * mm});
            skLineSegment(sketch, "E2504", {"start": v(194.88, 163.7) * mm, "end": v(194.45, 162.4) * mm});
            skLineSegment(sketch, "E2505", {"start": v(194.45, 162.4) * mm, "end": v(194.12, 161) * mm});
            skLineSegment(sketch, "E2506", {"start": v(194.12, 161) * mm, "end": v(194.02, 159.6) * mm});
            skLineSegment(sketch, "E2507", {"start": v(194.02, 159.6) * mm, "end": v(194.02, 122.47) * mm});
            skLineSegment(sketch, "E2508", {"start": v(194.02, 122.47) * mm, "end": v(194.12, 121.06) * mm});
            skLineSegment(sketch, "E2509", {"start": v(194.12, 121.06) * mm, "end": v(194.45, 119.65) * mm});
            skLineSegment(sketch, "E2510", {"start": v(194.45, 119.65) * mm, "end": v(194.88, 118.25) * mm});
            skLineSegment(sketch, "E2511", {"start": v(194.88, 118.25) * mm, "end": v(195.53, 116.95) * mm});
            skLineSegment(sketch, "E2512", {"start": v(195.53, 116.95) * mm, "end": v(196.29, 115.76) * mm});
            skLineSegment(sketch, "E2513", {"start": v(196.29, 115.76) * mm, "end": v(197.26, 114.68) * mm});
            skLineSegment(sketch, "E2514", {"start": v(197.26, 114.68) * mm, "end": v(198.35, 113.8) * mm});
            skLineSegment(sketch, "E2515", {"start": v(198.35, 113.8) * mm, "end": v(199.53, 112.95) * mm});
            skLineSegment(sketch, "E2516", {"start": v(199.53, 112.95) * mm, "end": v(200.83, 112.3) * mm});
            skLineSegment(sketch, "E2517", {"start": v(200.83, 112.3) * mm, "end": v(202.13, 111.86) * mm});
            skLineSegment(sketch, "E2518", {"start": v(202.13, 111.86) * mm, "end": v(203.54, 111.54) * mm});
            skLineSegment(sketch, "E2519", {"start": v(203.54, 111.54) * mm, "end": v(205.06, 111.54) * mm});
            skLineSegment(sketch, "E2520", {"start": v(205.06, 111.54) * mm, "end": v(206.25, 111.76) * mm});
            skLineSegment(sketch, "E2521", {"start": v(206.25, 111.76) * mm, "end": v(207.33, 112.19) * mm});
            skLineSegment(sketch, "E2522", {"start": v(207.33, 112.19) * mm, "end": v(208.3, 112.84) * mm});
            skLineSegment(sketch, "E2523", {"start": v(208.3, 112.84) * mm, "end": v(209.17, 113.6) * mm});
            skLineSegment(sketch, "E2524", {"start": v(209.17, 113.6) * mm, "end": v(209.93, 114.57) * mm});
            skLineSegment(sketch, "E2525", {"start": v(209.93, 114.57) * mm, "end": v(211.33, 113.6) * mm});
            skLineSegment(sketch, "E2526", {"start": v(211.33, 113.6) * mm, "end": v(211.33, 111.54) * mm});
            skLineSegment(sketch, "E2527", {"start": v(211.33, 111.54) * mm, "end": v(215.99, 111.54) * mm});
            skLineSegment(sketch, "E2528", {"start": v(215.99, 111.54) * mm, "end": v(215.99, 140.54) * mm});
            skLineSegment(sketch, "E2529", {"start": v(215.99, 140.54) * mm, "end": v(204.84, 140.54) * mm});
            skLineSegment(sketch, "E2530", {"start": v(204.84, 140.54) * mm, "end": v(204.84, 133.62) * mm});
            skLineSegment(sketch, "E2531", {"start": v(204.84, 133.62) * mm, "end": v(208.09, 133.62) * mm});
            skLineSegment(sketch, "E2532", {"start": v(208.09, 133.62) * mm, "end": v(208.09, 121.82) * mm});
            skLineSegment(sketch, "E2533", {"start": v(202.03, 121.82) * mm, "end": v(202.03, 121.06) * mm});
            skLineSegment(sketch, "E2534", {"start": v(202.03, 121.06) * mm, "end": v(202.35, 120.3) * mm});
            skLineSegment(sketch, "E2535", {"start": v(202.35, 120.3) * mm, "end": v(202.9, 119.65) * mm});
            skLineSegment(sketch, "E2536", {"start": v(202.9, 119.65) * mm, "end": v(203.54, 119.22) * mm});
            skLineSegment(sketch, "E2537", {"start": v(203.54, 119.22) * mm, "end": v(204.19, 118.9) * mm});
            skLineSegment(sketch, "E2538", {"start": v(204.19, 118.9) * mm, "end": v(205.06, 118.79) * mm});
            skLineSegment(sketch, "E2539", {"start": v(205.06, 118.79) * mm, "end": v(205.81, 118.9) * mm});
            skLineSegment(sketch, "E2540", {"start": v(205.81, 118.9) * mm, "end": v(206.57, 119.22) * mm});
            skLineSegment(sketch, "E2541", {"start": v(206.57, 119.22) * mm, "end": v(207.22, 119.65) * mm});
            skLineSegment(sketch, "E2542", {"start": v(207.22, 119.65) * mm, "end": v(207.65, 120.3) * mm});
            skLineSegment(sketch, "E2543", {"start": v(207.65, 120.3) * mm, "end": v(207.98, 121.06) * mm});
            skLineSegment(sketch, "E2544", {"start": v(207.98, 121.06) * mm, "end": v(208.09, 121.82) * mm});
            skLineSegment(sketch, "E2545", {"start": v(202.03, 121.82) * mm, "end": v(202.03, 160.14) * mm});
            skLineSegment(sketch, "E2546", {"start": v(208.09, 160.14) * mm, "end": v(207.98, 161) * mm});
            skLineSegment(sketch, "E2547", {"start": v(207.98, 161) * mm, "end": v(207.65, 161.65) * mm});
            skLineSegment(sketch, "E2548", {"start": v(207.65, 161.65) * mm, "end": v(207.22, 162.3) * mm});
            skLineSegment(sketch, "E2549", {"start": v(207.22, 162.3) * mm, "end": v(206.57, 162.84) * mm});
            skLineSegment(sketch, "E2550", {"start": v(206.57, 162.84) * mm, "end": v(205.81, 163.17) * mm});
            skLineSegment(sketch, "E2551", {"start": v(205.81, 163.17) * mm, "end": v(204.19, 163.17) * mm});
            skLineSegment(sketch, "E2552", {"start": v(204.19, 163.17) * mm, "end": v(203.54, 162.84) * mm});
            skLineSegment(sketch, "E2553", {"start": v(203.54, 162.84) * mm, "end": v(202.9, 162.3) * mm});
            skLineSegment(sketch, "E2554", {"start": v(202.9, 162.3) * mm, "end": v(202.35, 161.65) * mm});
            skLineSegment(sketch, "E2555", {"start": v(202.35, 161.65) * mm, "end": v(202.03, 161) * mm});
            skLineSegment(sketch, "E2556", {"start": v(202.03, 161) * mm, "end": v(202.03, 160.14) * mm});
            skLineSegment(sketch, "E2557", {"start": v(175.07, 146.17) * mm, "end": v(175.83, 147.8) * mm});
            skLineSegment(sketch, "E2558", {"start": v(175.83, 147.8) * mm, "end": v(176.48, 149.53) * mm});
            skLineSegment(sketch, "E2559", {"start": v(176.48, 149.53) * mm, "end": v(176.8, 151.26) * mm});
            skLineSegment(sketch, "E2560", {"start": v(176.8, 151.26) * mm, "end": v(176.92, 153.1) * mm});
            skLineSegment(sketch, "E2561", {"start": v(176.92, 153.1) * mm, "end": v(176.8, 154.94) * mm});
            skLineSegment(sketch, "E2562", {"start": v(176.8, 154.94) * mm, "end": v(176.48, 156.67) * mm});
            skLineSegment(sketch, "E2563", {"start": v(176.48, 156.67) * mm, "end": v(175.83, 158.4) * mm});
            skLineSegment(sketch, "E2564", {"start": v(175.83, 158.4) * mm, "end": v(175.07, 160.03) * mm});
            skLineSegment(sketch, "E2565", {"start": v(169.88, 144) * mm, "end": v(171.29, 144.23) * mm});
            skLineSegment(sketch, "E2566", {"start": v(171.29, 144.23) * mm, "end": v(172.7, 144.66) * mm});
            skLineSegment(sketch, "E2567", {"start": v(172.7, 144.66) * mm, "end": v(173.88, 145.3) * mm});
            skLineSegment(sketch, "E2568", {"start": v(173.88, 145.3) * mm, "end": v(175.07, 146.17) * mm});
            skLineSegment(sketch, "E2569", {"start": v(169.88, 144) * mm, "end": v(169.88, 162.2) * mm});
            skLineSegment(sketch, "E2570", {"start": v(175.07, 160.03) * mm, "end": v(173.88, 160.9) * mm});
            skLineSegment(sketch, "E2571", {"start": v(173.88, 160.9) * mm, "end": v(172.7, 161.54) * mm});
            skLineSegment(sketch, "E2572", {"start": v(172.7, 161.54) * mm, "end": v(171.29, 161.98) * mm});
            skLineSegment(sketch, "E2573", {"start": v(171.29, 161.98) * mm, "end": v(169.88, 162.2) * mm});
            skLineSegment(sketch, "E2574", {"start": v(169.88, 170.52) * mm, "end": v(161.98, 170.52) * mm});
            skLineSegment(sketch, "E2575", {"start": v(161.98, 170.52) * mm, "end": v(161.98, 111.54) * mm});
            skLineSegment(sketch, "E2576", {"start": v(161.98, 111.54) * mm, "end": v(169.88, 111.54) * mm});
            skLineSegment(sketch, "E2577", {"start": v(169.88, 111.54) * mm, "end": v(169.88, 137.3) * mm});
            skLineSegment(sketch, "E2578", {"start": v(169.88, 137.3) * mm, "end": v(170.42, 136.97) * mm});
            skLineSegment(sketch, "E2579", {"start": v(170.42, 136.97) * mm, "end": v(171.72, 136.97) * mm});
            skLineSegment(sketch, "E2580", {"start": v(171.72, 136.97) * mm, "end": v(172.26, 137.3) * mm});
            skLineSegment(sketch, "E2581", {"start": v(172.26, 137.3) * mm, "end": v(176.8, 111.54) * mm});
            skLineSegment(sketch, "E2582", {"start": v(176.8, 111.54) * mm, "end": v(185.03, 111.54) * mm});
            skLineSegment(sketch, "E2583", {"start": v(185.03, 111.54) * mm, "end": v(180.16, 139.57) * mm});
            skLineSegment(sketch, "E2584", {"start": v(180.16, 139.57) * mm, "end": v(181.46, 141.41) * mm});
            skLineSegment(sketch, "E2585", {"start": v(181.46, 141.41) * mm, "end": v(182.54, 143.36) * mm});
            skLineSegment(sketch, "E2586", {"start": v(182.54, 143.36) * mm, "end": v(183.4, 145.41) * mm});
            skLineSegment(sketch, "E2587", {"start": v(183.4, 145.41) * mm, "end": v(184.06, 147.58) * mm});
            skLineSegment(sketch, "E2588", {"start": v(184.06, 147.58) * mm, "end": v(184.5, 149.74) * mm});
            skLineSegment(sketch, "E2589", {"start": v(184.5, 149.74) * mm, "end": v(184.82, 152.02) * mm});
            skLineSegment(sketch, "E2590", {"start": v(184.82, 152.02) * mm, "end": v(184.82, 154.18) * mm});
            skLineSegment(sketch, "E2591", {"start": v(184.82, 154.18) * mm, "end": v(184.5, 156.46) * mm});
            skLineSegment(sketch, "E2592", {"start": v(184.5, 156.46) * mm, "end": v(184.06, 158.62) * mm});
            skLineSegment(sketch, "E2593", {"start": v(184.06, 158.62) * mm, "end": v(183.4, 160.78) * mm});
            skLineSegment(sketch, "E2594", {"start": v(183.4, 160.78) * mm, "end": v(182.54, 162.84) * mm});
            skLineSegment(sketch, "E2595", {"start": v(182.54, 162.84) * mm, "end": v(181.46, 164.79) * mm});
            skLineSegment(sketch, "E2596", {"start": v(181.46, 164.79) * mm, "end": v(180.16, 166.63) * mm});
            skLineSegment(sketch, "E2597", {"start": v(180.16, 166.63) * mm, "end": v(178.64, 167.82) * mm});
            skLineSegment(sketch, "E2598", {"start": v(178.64, 167.82) * mm, "end": v(177.02, 168.69) * mm});
            skLineSegment(sketch, "E2599", {"start": v(177.02, 168.69) * mm, "end": v(175.3, 169.44) * mm});
            skLineSegment(sketch, "E2600", {"start": v(175.3, 169.44) * mm, "end": v(173.56, 169.99) * mm});
            skLineSegment(sketch, "E2601", {"start": v(173.56, 169.99) * mm, "end": v(171.72, 170.3) * mm});
            skLineSegment(sketch, "E2602", {"start": v(171.72, 170.3) * mm, "end": v(169.88, 170.52) * mm});
            skLineSegment(sketch, "E2603", {"start": v(89.68, 268.37) * mm, "end": v(94.87, 277.03) * mm});
            skLineSegment(sketch, "E2604", {"start": v(94.87, 277.03) * mm, "end": v(104.18, 277.03) * mm});
            skLineSegment(sketch, "E2605", {"start": v(104.18, 277.03) * mm, "end": v(97.03, 268.37) * mm});
            skLineSegment(sketch, "E2606", {"start": v(97.03, 268.37) * mm, "end": v(89.68, 268.37) * mm});
            skLineSegment(sketch, "E2607", {"start": v(223.02, 86) * mm, "end": v(195.2, 86) * mm});
            skLineSegment(sketch, "E2608", {"start": v(195.2, 86) * mm, "end": v(76.04, -238.18) * mm});
            skLineSegment(sketch, "E2609", {"start": v(76.04, -238.18) * mm, "end": v(106.02, -238.18) * mm});
            skLineSegment(sketch, "E2610", {"start": v(106.02, -238.18) * mm, "end": v(223.02, 86) * mm});
            skLineSegment(sketch, "E2611", {"start": v(-127.77, 86) * mm, "end": v(-247.8, 86) * mm});
            skLineSegment(sketch, "E2612", {"start": v(-247.8, 86) * mm, "end": v(-247.8, 38.26) * mm});
            skLineSegment(sketch, "E2613", {"start": v(-247.8, 38.26) * mm, "end": v(-175.83, 38.26) * mm});
            skLineSegment(sketch, "E2614", {"start": v(-175.83, 38.26) * mm, "end": v(-223.67, -238.18) * mm});
            skLineSegment(sketch, "E2615", {"start": v(-223.67, -238.18) * mm, "end": v(-175.18, -238.18) * mm});
            skLineSegment(sketch, "E2616", {"start": v(-175.18, -238.18) * mm, "end": v(-127.77, 36.1) * mm});
            skLineSegment(sketch, "E2617", {"start": v(-127.77, 36.1) * mm, "end": v(-127.77, 86) * mm});
            skLineSegment(sketch, "E2618", {"start": v(-22.57, 31.66) * mm, "end": v(-22.57, -182.65) * mm});
            skLineSegment(sketch, "E2619", {"start": v(-56.66, -182.65) * mm, "end": v(-56.55, -184.6) * mm});
            skLineSegment(sketch, "E2620", {"start": v(-56.55, -184.6) * mm, "end": v(-56.23, -186.44) * mm});
            skLineSegment(sketch, "E2621", {"start": v(-56.23, -186.44) * mm, "end": v(-55.69, -188.28) * mm});
            skLineSegment(sketch, "E2622", {"start": v(-55.69, -188.28) * mm, "end": v(-55.04, -190.12) * mm});
            skLineSegment(sketch, "E2623", {"start": v(-55.04, -190.12) * mm, "end": v(-54.06, -191.74) * mm});
            skLineSegment(sketch, "E2624", {"start": v(-54.06, -191.74) * mm, "end": v(-52.98, -193.26) * mm});
            skLineSegment(sketch, "E2625", {"start": v(-52.98, -193.26) * mm, "end": v(-51.68, -194.77) * mm});
            skLineSegment(sketch, "E2626", {"start": v(-51.68, -194.77) * mm, "end": v(-50.28, -195.96) * mm});
            skLineSegment(sketch, "E2627", {"start": v(-50.28, -195.96) * mm, "end": v(-48.65, -197.16) * mm});
            skLineSegment(sketch, "E2628", {"start": v(-48.65, -197.16) * mm, "end": v(-47.03, -198.02) * mm});
            skLineSegment(sketch, "E2629", {"start": v(-47.03, -198.02) * mm, "end": v(-45.3, -198.78) * mm});
            skLineSegment(sketch, "E2630", {"start": v(-45.3, -198.78) * mm, "end": v(-43.46, -199.32) * mm});
            skLineSegment(sketch, "E2631", {"start": v(-43.46, -199.32) * mm, "end": v(-41.5, -199.64) * mm});
            skLineSegment(sketch, "E2632", {"start": v(-41.5, -199.64) * mm, "end": v(-39.56, -199.75) * mm});
            skLineSegment(sketch, "E2633", {"start": v(-39.56, -199.75) * mm, "end": v(-37.72, -199.64) * mm});
            skLineSegment(sketch, "E2634", {"start": v(-37.72, -199.64) * mm, "end": v(-35.77, -199.32) * mm});
            skLineSegment(sketch, "E2635", {"start": v(-35.77, -199.32) * mm, "end": v(-33.93, -198.78) * mm});
            skLineSegment(sketch, "E2636", {"start": v(-33.93, -198.78) * mm, "end": v(-32.2, -198.02) * mm});
            skLineSegment(sketch, "E2637", {"start": v(-32.2, -198.02) * mm, "end": v(-30.57, -197.16) * mm});
            skLineSegment(sketch, "E2638", {"start": v(-30.57, -197.16) * mm, "end": v(-28.95, -195.96) * mm});
            skLineSegment(sketch, "E2639", {"start": v(-28.95, -195.96) * mm, "end": v(-27.54, -194.77) * mm});
            skLineSegment(sketch, "E2640", {"start": v(-27.54, -194.77) * mm, "end": v(-26.25, -193.26) * mm});
            skLineSegment(sketch, "E2641", {"start": v(-26.25, -193.26) * mm, "end": v(-25.16, -191.74) * mm});
            skLineSegment(sketch, "E2642", {"start": v(-25.16, -191.74) * mm, "end": v(-24.2, -190.12) * mm});
            skLineSegment(sketch, "E2643", {"start": v(-24.2, -190.12) * mm, "end": v(-23.54, -188.28) * mm});
            skLineSegment(sketch, "E2644", {"start": v(-23.54, -188.28) * mm, "end": v(-23, -186.44) * mm});
            skLineSegment(sketch, "E2645", {"start": v(-23, -186.44) * mm, "end": v(-22.67, -184.6) * mm});
            skLineSegment(sketch, "E2646", {"start": v(-22.67, -184.6) * mm, "end": v(-22.57, -182.65) * mm});
            skLineSegment(sketch, "E2647", {"start": v(-56.66, -182.65) * mm, "end": v(-56.66, 31.66) * mm});
            skLineSegment(sketch, "E2648", {"start": v(-22.57, 31.66) * mm, "end": v(-22.67, 33.5) * mm});
            skLineSegment(sketch, "E2649", {"start": v(-22.67, 33.5) * mm, "end": v(-23, 35.45) * mm});
            skLineSegment(sketch, "E2650", {"start": v(-23, 35.45) * mm, "end": v(-23.54, 37.28) * mm});
            skLineSegment(sketch, "E2651", {"start": v(-23.54, 37.28) * mm, "end": v(-24.2, 39.02) * mm});
            skLineSegment(sketch, "E2652", {"start": v(-24.2, 39.02) * mm, "end": v(-25.16, 40.75) * mm});
            skLineSegment(sketch, "E2653", {"start": v(-25.16, 40.75) * mm, "end": v(-26.25, 42.26) * mm});
            skLineSegment(sketch, "E2654", {"start": v(-26.25, 42.26) * mm, "end": v(-27.54, 43.67) * mm});
            skLineSegment(sketch, "E2655", {"start": v(-27.54, 43.67) * mm, "end": v(-28.95, 44.97) * mm});
            skLineSegment(sketch, "E2656", {"start": v(-28.95, 44.97) * mm, "end": v(-30.57, 46.05) * mm});
            skLineSegment(sketch, "E2657", {"start": v(-30.57, 46.05) * mm, "end": v(-32.2, 47.03) * mm});
            skLineSegment(sketch, "E2658", {"start": v(-32.2, 47.03) * mm, "end": v(-33.93, 47.79) * mm});
            skLineSegment(sketch, "E2659", {"start": v(-33.93, 47.79) * mm, "end": v(-35.77, 48.22) * mm});
            skLineSegment(sketch, "E2660", {"start": v(-35.77, 48.22) * mm, "end": v(-37.72, 48.55) * mm});
            skLineSegment(sketch, "E2661", {"start": v(-37.72, 48.55) * mm, "end": v(-39.56, 48.65) * mm});
            skLineSegment(sketch, "E2662", {"start": v(-39.56, 48.65) * mm, "end": v(-41.5, 48.55) * mm});
            skLineSegment(sketch, "E2663", {"start": v(-41.5, 48.55) * mm, "end": v(-43.46, 48.22) * mm});
            skLineSegment(sketch, "E2664", {"start": v(-43.46, 48.22) * mm, "end": v(-45.3, 47.79) * mm});
            skLineSegment(sketch, "E2665", {"start": v(-45.3, 47.79) * mm, "end": v(-47.03, 47.03) * mm});
            skLineSegment(sketch, "E2666", {"start": v(-47.03, 47.03) * mm, "end": v(-48.65, 46.05) * mm});
            skLineSegment(sketch, "E2667", {"start": v(-48.65, 46.05) * mm, "end": v(-50.28, 44.97) * mm});
            skLineSegment(sketch, "E2668", {"start": v(-50.28, 44.97) * mm, "end": v(-51.68, 43.67) * mm});
            skLineSegment(sketch, "E2669", {"start": v(-51.68, 43.67) * mm, "end": v(-52.98, 42.26) * mm});
            skLineSegment(sketch, "E2670", {"start": v(-52.98, 42.26) * mm, "end": v(-54.06, 40.75) * mm});
            skLineSegment(sketch, "E2671", {"start": v(-54.06, 40.75) * mm, "end": v(-55.04, 39.02) * mm});
            skLineSegment(sketch, "E2672", {"start": v(-55.04, 39.02) * mm, "end": v(-55.69, 37.28) * mm});
            skLineSegment(sketch, "E2673", {"start": v(-55.69, 37.28) * mm, "end": v(-56.23, 35.45) * mm});
            skLineSegment(sketch, "E2674", {"start": v(-56.23, 35.45) * mm, "end": v(-56.55, 33.5) * mm});
            skLineSegment(sketch, "E2675", {"start": v(-56.55, 33.5) * mm, "end": v(-56.66, 31.66) * mm});
            skLineSegment(sketch, "E2676", {"start": v(-101.04, 28.09) * mm, "end": v(-101.04, -179.19) * mm});
            skLineSegment(sketch, "E2677", {"start": v(-101.04, -179.19) * mm, "end": v(-100.93, -182.76) * mm});
            skLineSegment(sketch, "E2678", {"start": v(-100.93, -182.76) * mm, "end": v(-100.6, -186.33) * mm});
            skLineSegment(sketch, "E2679", {"start": v(-100.6, -186.33) * mm, "end": v(-100.07, -189.8) * mm});
            skLineSegment(sketch, "E2680", {"start": v(-100.07, -189.8) * mm, "end": v(-99.41, -193.37) * mm});
            skLineSegment(sketch, "E2681", {"start": v(-99.41, -193.37) * mm, "end": v(-98.44, -196.83) * mm});
            skLineSegment(sketch, "E2682", {"start": v(-98.44, -196.83) * mm, "end": v(-97.36, -200.19) * mm});
            skLineSegment(sketch, "E2683", {"start": v(-97.36, -200.19) * mm, "end": v(-95.95, -203.54) * mm});
            skLineSegment(sketch, "E2684", {"start": v(-95.95, -203.54) * mm, "end": v(-94.54, -206.79) * mm});
            skLineSegment(sketch, "E2685", {"start": v(-94.54, -206.79) * mm, "end": v(-92.81, -209.93) * mm});
            skLineSegment(sketch, "E2686", {"start": v(-92.81, -209.93) * mm, "end": v(-90.97, -212.96) * mm});
            skLineSegment(sketch, "E2687", {"start": v(-90.97, -212.96) * mm, "end": v(-88.91, -215.88) * mm});
            skLineSegment(sketch, "E2688", {"start": v(-88.91, -215.88) * mm, "end": v(-86.64, -218.7) * mm});
            skLineSegment(sketch, "E2689", {"start": v(-86.64, -218.7) * mm, "end": v(-84.26, -221.3) * mm});
            skLineSegment(sketch, "E2690", {"start": v(-84.26, -221.3) * mm, "end": v(-81.77, -223.89) * mm});
            skLineSegment(sketch, "E2691", {"start": v(-81.77, -223.89) * mm, "end": v(-79.07, -226.27) * mm});
            skLineSegment(sketch, "E2692", {"start": v(-79.07, -226.27) * mm, "end": v(-76.25, -228.43) * mm});
            skLineSegment(sketch, "E2693", {"start": v(-76.25, -228.43) * mm, "end": v(-73.33, -230.5) * mm});
            skLineSegment(sketch, "E2694", {"start": v(-73.33, -230.5) * mm, "end": v(-70.3, -232.33) * mm});
            skLineSegment(sketch, "E2695", {"start": v(-70.3, -232.33) * mm, "end": v(-67.16, -234.06) * mm});
            skLineSegment(sketch, "E2696", {"start": v(-67.16, -234.06) * mm, "end": v(-63.91, -235.58) * mm});
            skLineSegment(sketch, "E2697", {"start": v(-63.91, -235.58) * mm, "end": v(-60.66, -236.88) * mm});
            skLineSegment(sketch, "E2698", {"start": v(-60.66, -236.88) * mm, "end": v(-57.2, -238.07) * mm});
            skLineSegment(sketch, "E2699", {"start": v(-57.2, -238.07) * mm, "end": v(-53.74, -238.93) * mm});
            skLineSegment(sketch, "E2700", {"start": v(-53.74, -238.93) * mm, "end": v(-50.28, -239.7) * mm});
            skLineSegment(sketch, "E2701", {"start": v(-50.28, -239.7) * mm, "end": v(-46.7, -240.23) * mm});
            skLineSegment(sketch, "E2702", {"start": v(-46.7, -240.23) * mm, "end": v(-43.13, -240.45) * mm});
            skLineSegment(sketch, "E2703", {"start": v(-43.13, -240.45) * mm, "end": v(-39.56, -240.56) * mm});
            skLineSegment(sketch, "E2704", {"start": v(-39.56, -240.56) * mm, "end": v(-36.1, -240.45) * mm});
            skLineSegment(sketch, "E2705", {"start": v(-36.1, -240.45) * mm, "end": v(-32.52, -240.23) * mm});
            skLineSegment(sketch, "E2706", {"start": v(-32.52, -240.23) * mm, "end": v(-28.95, -239.7) * mm});
            skLineSegment(sketch, "E2707", {"start": v(-28.95, -239.7) * mm, "end": v(-25.49, -238.93) * mm});
            skLineSegment(sketch, "E2708", {"start": v(-25.49, -238.93) * mm, "end": v(-22.03, -238.07) * mm});
            skLineSegment(sketch, "E2709", {"start": v(-22.03, -238.07) * mm, "end": v(-18.56, -236.88) * mm});
            skLineSegment(sketch, "E2710", {"start": v(-18.56, -236.88) * mm, "end": v(-15.31, -235.58) * mm});
            skLineSegment(sketch, "E2711", {"start": v(-15.31, -235.58) * mm, "end": v(-12.07, -234.06) * mm});
            skLineSegment(sketch, "E2712", {"start": v(-12.07, -234.06) * mm, "end": v(-8.93, -232.33) * mm});
            skLineSegment(sketch, "E2713", {"start": v(-8.93, -232.33) * mm, "end": v(-5.9, -230.5) * mm});
            skLineSegment(sketch, "E2714", {"start": v(-5.9, -230.5) * mm, "end": v(-2.98, -228.43) * mm});
            skLineSegment(sketch, "E2715", {"start": v(-2.98, -228.43) * mm, "end": v(-0.16, -226.27) * mm});
            skLineSegment(sketch, "E2716", {"start": v(-0.16, -226.27) * mm, "end": v(2.55, -223.89) * mm});
            skLineSegment(sketch, "E2717", {"start": v(2.55, -223.89) * mm, "end": v(5.03, -221.3) * mm});
            skLineSegment(sketch, "E2718", {"start": v(5.03, -221.3) * mm, "end": v(7.42, -218.7) * mm});
            skLineSegment(sketch, "E2719", {"start": v(7.42, -218.7) * mm, "end": v(9.69, -215.88) * mm});
            skLineSegment(sketch, "E2720", {"start": v(9.69, -215.88) * mm, "end": v(11.74, -212.96) * mm});
            skLineSegment(sketch, "E2721", {"start": v(11.74, -212.96) * mm, "end": v(13.59, -209.93) * mm});
            skLineSegment(sketch, "E2722", {"start": v(13.59, -209.93) * mm, "end": v(15.32, -206.79) * mm});
            skLineSegment(sketch, "E2723", {"start": v(15.32, -206.79) * mm, "end": v(16.72, -203.54) * mm});
            skLineSegment(sketch, "E2724", {"start": v(16.72, -203.54) * mm, "end": v(18.13, -200.19) * mm});
            skLineSegment(sketch, "E2725", {"start": v(18.13, -200.19) * mm, "end": v(19.21, -196.83) * mm});
            skLineSegment(sketch, "E2726", {"start": v(19.21, -196.83) * mm, "end": v(20.18, -193.37) * mm});
            skLineSegment(sketch, "E2727", {"start": v(20.18, -193.37) * mm, "end": v(20.84, -189.8) * mm});
            skLineSegment(sketch, "E2728", {"start": v(20.84, -189.8) * mm, "end": v(21.38, -186.33) * mm});
            skLineSegment(sketch, "E2729", {"start": v(21.38, -186.33) * mm, "end": v(21.7, -182.76) * mm});
            skLineSegment(sketch, "E2730", {"start": v(21.7, -182.76) * mm, "end": v(21.81, -179.19) * mm});
            skLineSegment(sketch, "E2731", {"start": v(21.81, -179.19) * mm, "end": v(21.81, 28.09) * mm});
            skLineSegment(sketch, "E2732", {"start": v(21.81, 28.09) * mm, "end": v(21.7, 31.66) * mm});
            skLineSegment(sketch, "E2733", {"start": v(21.7, 31.66) * mm, "end": v(21.38, 35.23) * mm});
            skLineSegment(sketch, "E2734", {"start": v(21.38, 35.23) * mm, "end": v(20.84, 38.8) * mm});
            skLineSegment(sketch, "E2735", {"start": v(20.84, 38.8) * mm, "end": v(20.18, 42.26) * mm});
            skLineSegment(sketch, "E2736", {"start": v(20.18, 42.26) * mm, "end": v(19.21, 45.73) * mm});
            skLineSegment(sketch, "E2737", {"start": v(19.21, 45.73) * mm, "end": v(18.13, 49.08) * mm});
            skLineSegment(sketch, "E2738", {"start": v(18.13, 49.08) * mm, "end": v(16.72, 52.44) * mm});
            skLineSegment(sketch, "E2739", {"start": v(16.72, 52.44) * mm, "end": v(15.32, 55.69) * mm});
            skLineSegment(sketch, "E2740", {"start": v(15.32, 55.69) * mm, "end": v(13.59, 58.83) * mm});
            skLineSegment(sketch, "E2741", {"start": v(13.59, 58.83) * mm, "end": v(11.74, 61.86) * mm});
            skLineSegment(sketch, "E2742", {"start": v(11.74, 61.86) * mm, "end": v(9.69, 64.78) * mm});
            skLineSegment(sketch, "E2743", {"start": v(9.69, 64.78) * mm, "end": v(7.42, 67.6) * mm});
            skLineSegment(sketch, "E2744", {"start": v(7.42, 67.6) * mm, "end": v(5.03, 70.3) * mm});
            skLineSegment(sketch, "E2745", {"start": v(5.03, 70.3) * mm, "end": v(2.55, 72.79) * mm});
            skLineSegment(sketch, "E2746", {"start": v(2.55, 72.79) * mm, "end": v(-0.16, 75.17) * mm});
            skLineSegment(sketch, "E2747", {"start": v(-0.16, 75.17) * mm, "end": v(-2.98, 77.44) * mm});
            skLineSegment(sketch, "E2748", {"start": v(-2.98, 77.44) * mm, "end": v(-5.9, 79.5) * mm});
            skLineSegment(sketch, "E2749", {"start": v(-5.9, 79.5) * mm, "end": v(-8.93, 81.34) * mm});
            skLineSegment(sketch, "E2750", {"start": v(-8.93, 81.34) * mm, "end": v(-12.07, 83.07) * mm});
            skLineSegment(sketch, "E2751", {"start": v(-12.07, 83.07) * mm, "end": v(-15.31, 84.48) * mm});
            skLineSegment(sketch, "E2752", {"start": v(-15.31, 84.48) * mm, "end": v(-18.56, 85.89) * mm});
            skLineSegment(sketch, "E2753", {"start": v(-18.56, 85.89) * mm, "end": v(-22.03, 86.97) * mm});
            skLineSegment(sketch, "E2754", {"start": v(-22.03, 86.97) * mm, "end": v(-25.49, 87.94) * mm});
            skLineSegment(sketch, "E2755", {"start": v(-25.49, 87.94) * mm, "end": v(-28.95, 88.6) * mm});
            skLineSegment(sketch, "E2756", {"start": v(-28.95, 88.6) * mm, "end": v(-32.52, 89.13) * mm});
            skLineSegment(sketch, "E2757", {"start": v(-32.52, 89.13) * mm, "end": v(-36.1, 89.46) * mm});
            skLineSegment(sketch, "E2758", {"start": v(-36.1, 89.46) * mm, "end": v(-39.56, 89.57) * mm});
            skLineSegment(sketch, "E2759", {"start": v(-39.56, 89.57) * mm, "end": v(-43.13, 89.46) * mm});
            skLineSegment(sketch, "E2760", {"start": v(-43.13, 89.46) * mm, "end": v(-46.7, 89.13) * mm});
            skLineSegment(sketch, "E2761", {"start": v(-46.7, 89.13) * mm, "end": v(-50.28, 88.6) * mm});
            skLineSegment(sketch, "E2762", {"start": v(-50.28, 88.6) * mm, "end": v(-53.74, 87.94) * mm});
            skLineSegment(sketch, "E2763", {"start": v(-53.74, 87.94) * mm, "end": v(-57.2, 86.97) * mm});
            skLineSegment(sketch, "E2764", {"start": v(-57.2, 86.97) * mm, "end": v(-60.66, 85.89) * mm});
            skLineSegment(sketch, "E2765", {"start": v(-60.66, 85.89) * mm, "end": v(-63.91, 84.48) * mm});
            skLineSegment(sketch, "E2766", {"start": v(-63.91, 84.48) * mm, "end": v(-67.16, 83.07) * mm});
            skLineSegment(sketch, "E2767", {"start": v(-67.16, 83.07) * mm, "end": v(-70.3, 81.34) * mm});
            skLineSegment(sketch, "E2768", {"start": v(-70.3, 81.34) * mm, "end": v(-73.33, 79.5) * mm});
            skLineSegment(sketch, "E2769", {"start": v(-73.33, 79.5) * mm, "end": v(-76.25, 77.44) * mm});
            skLineSegment(sketch, "E2770", {"start": v(-76.25, 77.44) * mm, "end": v(-79.07, 75.17) * mm});
            skLineSegment(sketch, "E2771", {"start": v(-79.07, 75.17) * mm, "end": v(-81.77, 72.79) * mm});
            skLineSegment(sketch, "E2772", {"start": v(-81.77, 72.79) * mm, "end": v(-84.26, 70.3) * mm});
            skLineSegment(sketch, "E2773", {"start": v(-84.26, 70.3) * mm, "end": v(-86.64, 67.6) * mm});
            skLineSegment(sketch, "E2774", {"start": v(-86.64, 67.6) * mm, "end": v(-88.91, 64.78) * mm});
            skLineSegment(sketch, "E2775", {"start": v(-88.91, 64.78) * mm, "end": v(-90.97, 61.86) * mm});
            skLineSegment(sketch, "E2776", {"start": v(-90.97, 61.86) * mm, "end": v(-92.81, 58.83) * mm});
            skLineSegment(sketch, "E2777", {"start": v(-92.81, 58.83) * mm, "end": v(-94.54, 55.69) * mm});
            skLineSegment(sketch, "E2778", {"start": v(-94.54, 55.69) * mm, "end": v(-95.95, 52.44) * mm});
            skLineSegment(sketch, "E2779", {"start": v(-95.95, 52.44) * mm, "end": v(-97.36, 49.08) * mm});
            skLineSegment(sketch, "E2780", {"start": v(-97.36, 49.08) * mm, "end": v(-98.44, 45.73) * mm});
            skLineSegment(sketch, "E2781", {"start": v(-98.44, 45.73) * mm, "end": v(-99.41, 42.26) * mm});
            skLineSegment(sketch, "E2782", {"start": v(-99.41, 42.26) * mm, "end": v(-100.07, 38.8) * mm});
            skLineSegment(sketch, "E2783", {"start": v(-100.07, 38.8) * mm, "end": v(-100.6, 35.23) * mm});
            skLineSegment(sketch, "E2784", {"start": v(-100.6, 35.23) * mm, "end": v(-100.93, 31.66) * mm});
            skLineSegment(sketch, "E2785", {"start": v(-100.93, 31.66) * mm, "end": v(-101.04, 28.09) * mm});
            skLineSegment(sketch, "E2786", {"start": v(220.75, -101.9) * mm, "end": v(220.75, -211.12) * mm});
            skLineSegment(sketch, "E2787", {"start": v(203.33, -211.12) * mm, "end": v(203.43, -212.42) * mm});
            skLineSegment(sketch, "E2788", {"start": v(203.43, -212.42) * mm, "end": v(203.76, -213.82) * mm});
            skLineSegment(sketch, "E2789", {"start": v(203.76, -213.82) * mm, "end": v(204.3, -215.01) * mm});
            skLineSegment(sketch, "E2790", {"start": v(204.3, -215.01) * mm, "end": v(205.06, -216.2) * mm});
            skLineSegment(sketch, "E2791", {"start": v(205.06, -216.2) * mm, "end": v(205.92, -217.29) * mm});
            skLineSegment(sketch, "E2792", {"start": v(205.92, -217.29) * mm, "end": v(206.9, -218.15) * mm});
            skLineSegment(sketch, "E2793", {"start": v(206.9, -218.15) * mm, "end": v(208.09, -218.8) * mm});
            skLineSegment(sketch, "E2794", {"start": v(208.09, -218.8) * mm, "end": v(209.39, -219.35) * mm});
            skLineSegment(sketch, "E2795", {"start": v(209.39, -219.35) * mm, "end": v(210.68, -219.67) * mm});
            skLineSegment(sketch, "E2796", {"start": v(210.68, -219.67) * mm, "end": v(212.09, -219.78) * mm});
            skLineSegment(sketch, "E2797", {"start": v(212.09, -219.78) * mm, "end": v(213.4, -219.67) * mm});
            skLineSegment(sketch, "E2798", {"start": v(213.4, -219.67) * mm, "end": v(214.69, -219.35) * mm});
            skLineSegment(sketch, "E2799", {"start": v(214.69, -219.35) * mm, "end": v(215.99, -218.8) * mm});
            skLineSegment(sketch, "E2800", {"start": v(215.99, -218.8) * mm, "end": v(217.18, -218.15) * mm});
            skLineSegment(sketch, "E2801", {"start": v(217.18, -218.15) * mm, "end": v(218.15, -217.29) * mm});
            skLineSegment(sketch, "E2802", {"start": v(218.15, -217.29) * mm, "end": v(219.13, -216.2) * mm});
            skLineSegment(sketch, "E2803", {"start": v(219.13, -216.2) * mm, "end": v(219.78, -215.01) * mm});
            skLineSegment(sketch, "E2804", {"start": v(219.78, -215.01) * mm, "end": v(220.32, -213.82) * mm});
            skLineSegment(sketch, "E2805", {"start": v(220.32, -213.82) * mm, "end": v(220.64, -212.42) * mm});
            skLineSegment(sketch, "E2806", {"start": v(220.64, -212.42) * mm, "end": v(220.75, -211.12) * mm});
            skLineSegment(sketch, "E2807", {"start": v(203.33, -211.12) * mm, "end": v(203.33, -101.9) * mm});
            skLineSegment(sketch, "E2808", {"start": v(220.75, -101.9) * mm, "end": v(220.64, -100.5) * mm});
            skLineSegment(sketch, "E2809", {"start": v(220.64, -100.5) * mm, "end": v(220.32, -99.2) * mm});
            skLineSegment(sketch, "E2810", {"start": v(220.32, -99.2) * mm, "end": v(219.78, -97.9) * mm});
            skLineSegment(sketch, "E2811", {"start": v(219.78, -97.9) * mm, "end": v(219.13, -96.82) * mm});
            skLineSegment(sketch, "E2812", {"start": v(219.13, -96.82) * mm, "end": v(218.15, -95.74) * mm});
            skLineSegment(sketch, "E2813", {"start": v(218.15, -95.74) * mm, "end": v(217.18, -94.87) * mm});
            skLineSegment(sketch, "E2814", {"start": v(217.18, -94.87) * mm, "end": v(215.99, -94.12) * mm});
            skLineSegment(sketch, "E2815", {"start": v(215.99, -94.12) * mm, "end": v(214.69, -93.57) * mm});
            skLineSegment(sketch, "E2816", {"start": v(214.69, -93.57) * mm, "end": v(213.4, -93.25) * mm});
            skLineSegment(sketch, "E2817", {"start": v(213.4, -93.25) * mm, "end": v(212.09, -93.14) * mm});
            skLineSegment(sketch, "E2818", {"start": v(212.09, -93.14) * mm, "end": v(210.68, -93.25) * mm});
            skLineSegment(sketch, "E2819", {"start": v(210.68, -93.25) * mm, "end": v(209.39, -93.57) * mm});
            skLineSegment(sketch, "E2820", {"start": v(209.39, -93.57) * mm, "end": v(208.09, -94.12) * mm});
            skLineSegment(sketch, "E2821", {"start": v(208.09, -94.12) * mm, "end": v(206.9, -94.87) * mm});
            skLineSegment(sketch, "E2822", {"start": v(206.9, -94.87) * mm, "end": v(205.92, -95.74) * mm});
            skLineSegment(sketch, "E2823", {"start": v(205.92, -95.74) * mm, "end": v(205.06, -96.82) * mm});
            skLineSegment(sketch, "E2824", {"start": v(205.06, -96.82) * mm, "end": v(204.3, -97.9) * mm});
            skLineSegment(sketch, "E2825", {"start": v(204.3, -97.9) * mm, "end": v(203.76, -99.2) * mm});
            skLineSegment(sketch, "E2826", {"start": v(203.76, -99.2) * mm, "end": v(203.43, -100.5) * mm});
            skLineSegment(sketch, "E2827", {"start": v(203.43, -100.5) * mm, "end": v(203.33, -101.9) * mm});
            skLineSegment(sketch, "E2828", {"start": v(180.7, -103.64) * mm, "end": v(180.7, -209.28) * mm});
            skLineSegment(sketch, "E2829", {"start": v(180.7, -209.28) * mm, "end": v(180.81, -211.88) * mm});
            skLineSegment(sketch, "E2830", {"start": v(180.81, -211.88) * mm, "end": v(181.14, -214.47) * mm});
            skLineSegment(sketch, "E2831", {"start": v(181.14, -214.47) * mm, "end": v(181.68, -216.96) * mm});
            skLineSegment(sketch, "E2832", {"start": v(181.68, -216.96) * mm, "end": v(182.43, -219.45) * mm});
            skLineSegment(sketch, "E2833", {"start": v(182.43, -219.45) * mm, "end": v(183.4, -221.83) * mm});
            skLineSegment(sketch, "E2834", {"start": v(183.4, -221.83) * mm, "end": v(184.5, -224.21) * mm});
            skLineSegment(sketch, "E2835", {"start": v(184.5, -224.21) * mm, "end": v(185.79, -226.38) * mm});
            skLineSegment(sketch, "E2836", {"start": v(185.79, -226.38) * mm, "end": v(187.3, -228.54) * mm});
            skLineSegment(sketch, "E2837", {"start": v(187.3, -228.54) * mm, "end": v(189.04, -230.5) * mm});
            skLineSegment(sketch, "E2838", {"start": v(189.04, -230.5) * mm, "end": v(190.88, -232.33) * mm});
            skLineSegment(sketch, "E2839", {"start": v(190.88, -232.33) * mm, "end": v(192.82, -233.96) * mm});
            skLineSegment(sketch, "E2840", {"start": v(192.82, -233.96) * mm, "end": v(194.88, -235.47) * mm});
            skLineSegment(sketch, "E2841", {"start": v(194.88, -235.47) * mm, "end": v(197.16, -236.88) * mm});
            skLineSegment(sketch, "E2842", {"start": v(197.16, -236.88) * mm, "end": v(199.43, -237.96) * mm});
            skLineSegment(sketch, "E2843", {"start": v(199.43, -237.96) * mm, "end": v(201.92, -238.93) * mm});
            skLineSegment(sketch, "E2844", {"start": v(201.92, -238.93) * mm, "end": v(204.4, -239.7) * mm});
            skLineSegment(sketch, "E2845", {"start": v(204.4, -239.7) * mm, "end": v(206.9, -240.12) * mm});
            skLineSegment(sketch, "E2846", {"start": v(206.9, -240.12) * mm, "end": v(209.5, -240.45) * mm});
            skLineSegment(sketch, "E2847", {"start": v(209.5, -240.45) * mm, "end": v(212.09, -240.56) * mm});
            skLineSegment(sketch, "E2848", {"start": v(212.09, -240.56) * mm, "end": v(214.58, -240.45) * mm});
            skLineSegment(sketch, "E2849", {"start": v(214.58, -240.45) * mm, "end": v(217.18, -240.12) * mm});
            skLineSegment(sketch, "E2850", {"start": v(217.18, -240.12) * mm, "end": v(219.78, -239.7) * mm});
            skLineSegment(sketch, "E2851", {"start": v(219.78, -239.7) * mm, "end": v(222.16, -238.93) * mm});
            skLineSegment(sketch, "E2852", {"start": v(222.16, -238.93) * mm, "end": v(224.64, -237.96) * mm});
            skLineSegment(sketch, "E2853", {"start": v(224.64, -237.96) * mm, "end": v(226.92, -236.88) * mm});
            skLineSegment(sketch, "E2854", {"start": v(226.92, -236.88) * mm, "end": v(229.2, -235.47) * mm});
            skLineSegment(sketch, "E2855", {"start": v(229.2, -235.47) * mm, "end": v(231.25, -233.96) * mm});
            skLineSegment(sketch, "E2856", {"start": v(231.25, -233.96) * mm, "end": v(233.2, -232.33) * mm});
            skLineSegment(sketch, "E2857", {"start": v(233.2, -232.33) * mm, "end": v(235.04, -230.5) * mm});
            skLineSegment(sketch, "E2858", {"start": v(235.04, -230.5) * mm, "end": v(236.77, -228.54) * mm});
            skLineSegment(sketch, "E2859", {"start": v(236.77, -228.54) * mm, "end": v(238.28, -226.38) * mm});
            skLineSegment(sketch, "E2860", {"start": v(238.28, -226.38) * mm, "end": v(239.58, -224.21) * mm});
            skLineSegment(sketch, "E2861", {"start": v(239.58, -224.21) * mm, "end": v(240.66, -221.83) * mm});
            skLineSegment(sketch, "E2862", {"start": v(240.66, -221.83) * mm, "end": v(241.64, -219.45) * mm});
            skLineSegment(sketch, "E2863", {"start": v(241.64, -219.45) * mm, "end": v(242.4, -216.96) * mm});
            skLineSegment(sketch, "E2864", {"start": v(242.4, -216.96) * mm, "end": v(242.94, -214.47) * mm});
            skLineSegment(sketch, "E2865", {"start": v(242.94, -214.47) * mm, "end": v(243.26, -211.88) * mm});
            skLineSegment(sketch, "E2866", {"start": v(243.26, -211.88) * mm, "end": v(243.37, -209.28) * mm});
            skLineSegment(sketch, "E2867", {"start": v(243.37, -209.28) * mm, "end": v(243.37, -103.64) * mm});
            skLineSegment(sketch, "E2868", {"start": v(243.37, -103.64) * mm, "end": v(243.26, -101.04) * mm});
            skLineSegment(sketch, "E2869", {"start": v(243.26, -101.04) * mm, "end": v(242.94, -98.55) * mm});
            skLineSegment(sketch, "E2870", {"start": v(242.94, -98.55) * mm, "end": v(242.4, -95.95) * mm});
            skLineSegment(sketch, "E2871", {"start": v(242.4, -95.95) * mm, "end": v(241.64, -93.47) * mm});
            skLineSegment(sketch, "E2872", {"start": v(241.64, -93.47) * mm, "end": v(240.66, -91.09) * mm});
            skLineSegment(sketch, "E2873", {"start": v(240.66, -91.09) * mm, "end": v(239.58, -88.8) * mm});
            skLineSegment(sketch, "E2874", {"start": v(239.58, -88.8) * mm, "end": v(238.28, -86.54) * mm});
            skLineSegment(sketch, "E2875", {"start": v(238.28, -86.54) * mm, "end": v(236.77, -84.48) * mm});
            skLineSegment(sketch, "E2876", {"start": v(236.77, -84.48) * mm, "end": v(235.04, -82.42) * mm});
            skLineSegment(sketch, "E2877", {"start": v(235.04, -82.42) * mm, "end": v(233.2, -80.7) * mm});
            skLineSegment(sketch, "E2878", {"start": v(233.2, -80.7) * mm, "end": v(231.25, -78.96) * mm});
            skLineSegment(sketch, "E2879", {"start": v(231.25, -78.96) * mm, "end": v(229.2, -77.45) * mm});
            skLineSegment(sketch, "E2880", {"start": v(229.2, -77.45) * mm, "end": v(226.92, -76.15) * mm});
            skLineSegment(sketch, "E2881", {"start": v(226.92, -76.15) * mm, "end": v(224.64, -74.96) * mm});
            skLineSegment(sketch, "E2882", {"start": v(224.64, -74.96) * mm, "end": v(222.16, -74.09) * mm});
            skLineSegment(sketch, "E2883", {"start": v(222.16, -74.09) * mm, "end": v(219.78, -73.33) * mm});
            skLineSegment(sketch, "E2884", {"start": v(219.78, -73.33) * mm, "end": v(217.18, -72.79) * mm});
            skLineSegment(sketch, "E2885", {"start": v(217.18, -72.79) * mm, "end": v(214.58, -72.46) * mm});
            skLineSegment(sketch, "E2886", {"start": v(214.58, -72.46) * mm, "end": v(212.09, -72.36) * mm});
            skLineSegment(sketch, "E2887", {"start": v(212.09, -72.36) * mm, "end": v(209.5, -72.46) * mm});
            skLineSegment(sketch, "E2888", {"start": v(209.5, -72.46) * mm, "end": v(206.9, -72.79) * mm});
            skLineSegment(sketch, "E2889", {"start": v(206.9, -72.79) * mm, "end": v(204.4, -73.33) * mm});
            skLineSegment(sketch, "E2890", {"start": v(204.4, -73.33) * mm, "end": v(201.92, -74.09) * mm});
            skLineSegment(sketch, "E2891", {"start": v(201.92, -74.09) * mm, "end": v(199.43, -74.96) * mm});
            skLineSegment(sketch, "E2892", {"start": v(199.43, -74.96) * mm, "end": v(197.16, -76.15) * mm});
            skLineSegment(sketch, "E2893", {"start": v(197.16, -76.15) * mm, "end": v(194.88, -77.45) * mm});
            skLineSegment(sketch, "E2894", {"start": v(194.88, -77.45) * mm, "end": v(192.82, -78.96) * mm});
            skLineSegment(sketch, "E2895", {"start": v(192.82, -78.96) * mm, "end": v(190.88, -80.7) * mm});
            skLineSegment(sketch, "E2896", {"start": v(190.88, -80.7) * mm, "end": v(189.04, -82.42) * mm});
            skLineSegment(sketch, "E2897", {"start": v(189.04, -82.42) * mm, "end": v(187.3, -84.48) * mm});
            skLineSegment(sketch, "E2898", {"start": v(187.3, -84.48) * mm, "end": v(185.79, -86.54) * mm});
            skLineSegment(sketch, "E2899", {"start": v(185.79, -86.54) * mm, "end": v(184.5, -88.8) * mm});
            skLineSegment(sketch, "E2900", {"start": v(184.5, -88.8) * mm, "end": v(183.4, -91.09) * mm});
            skLineSegment(sketch, "E2901", {"start": v(183.4, -91.09) * mm, "end": v(182.43, -93.47) * mm});
            skLineSegment(sketch, "E2902", {"start": v(182.43, -93.47) * mm, "end": v(181.68, -95.95) * mm});
            skLineSegment(sketch, "E2903", {"start": v(181.68, -95.95) * mm, "end": v(181.14, -98.55) * mm});
            skLineSegment(sketch, "E2904", {"start": v(181.14, -98.55) * mm, "end": v(180.81, -101.04) * mm});
            skLineSegment(sketch, "E2905", {"start": v(180.81, -101.04) * mm, "end": v(180.7, -103.64) * mm});
            skLineSegment(sketch, "E2906", {"start": v(96.93, 60.02) * mm, "end": v(96.93, -49.2) * mm});
            skLineSegment(sketch, "E2907", {"start": v(79.5, -49.2) * mm, "end": v(79.61, -50.5) * mm});
            skLineSegment(sketch, "E2908", {"start": v(79.61, -50.5) * mm, "end": v(79.94, -51.9) * mm});
            skLineSegment(sketch, "E2909", {"start": v(79.94, -51.9) * mm, "end": v(80.47, -53.09) * mm});
            skLineSegment(sketch, "E2910", {"start": v(80.47, -53.09) * mm, "end": v(81.12, -54.28) * mm});
            skLineSegment(sketch, "E2911", {"start": v(81.12, -54.28) * mm, "end": v(81.99, -55.37) * mm});
            skLineSegment(sketch, "E2912", {"start": v(81.99, -55.37) * mm, "end": v(83.07, -56.23) * mm});
            skLineSegment(sketch, "E2913", {"start": v(83.07, -56.23) * mm, "end": v(84.26, -56.88) * mm});
            skLineSegment(sketch, "E2914", {"start": v(84.26, -56.88) * mm, "end": v(85.45, -57.42) * mm});
            skLineSegment(sketch, "E2915", {"start": v(85.45, -57.42) * mm, "end": v(86.86, -57.75) * mm});
            skLineSegment(sketch, "E2916", {"start": v(86.86, -57.75) * mm, "end": v(88.16, -57.85) * mm});
            skLineSegment(sketch, "E2917", {"start": v(88.16, -57.85) * mm, "end": v(89.57, -57.75) * mm});
            skLineSegment(sketch, "E2918", {"start": v(89.57, -57.75) * mm, "end": v(90.86, -57.42) * mm});
            skLineSegment(sketch, "E2919", {"start": v(90.86, -57.42) * mm, "end": v(92.16, -56.88) * mm});
            skLineSegment(sketch, "E2920", {"start": v(92.16, -56.88) * mm, "end": v(93.24, -56.23) * mm});
            skLineSegment(sketch, "E2921", {"start": v(93.24, -56.23) * mm, "end": v(94.33, -55.37) * mm});
            skLineSegment(sketch, "E2922", {"start": v(94.33, -55.37) * mm, "end": v(95.2, -54.28) * mm});
            skLineSegment(sketch, "E2923", {"start": v(95.2, -54.28) * mm, "end": v(95.95, -53.09) * mm});
            skLineSegment(sketch, "E2924", {"start": v(95.95, -53.09) * mm, "end": v(96.5, -51.9) * mm});
            skLineSegment(sketch, "E2925", {"start": v(96.5, -51.9) * mm, "end": v(96.82, -50.5) * mm});
            skLineSegment(sketch, "E2926", {"start": v(96.82, -50.5) * mm, "end": v(96.93, -49.2) * mm});
            skLineSegment(sketch, "E2927", {"start": v(79.5, -49.2) * mm, "end": v(79.5, 60.02) * mm});
            skLineSegment(sketch, "E2928", {"start": v(96.93, 60.02) * mm, "end": v(96.82, 61.42) * mm});
            skLineSegment(sketch, "E2929", {"start": v(96.82, 61.42) * mm, "end": v(96.5, 62.72) * mm});
            skLineSegment(sketch, "E2930", {"start": v(96.5, 62.72) * mm, "end": v(95.95, 64.02) * mm});
            skLineSegment(sketch, "E2931", {"start": v(95.95, 64.02) * mm, "end": v(95.2, 65.1) * mm});
            skLineSegment(sketch, "E2932", {"start": v(95.2, 65.1) * mm, "end": v(94.33, 66.18) * mm});
            skLineSegment(sketch, "E2933", {"start": v(94.33, 66.18) * mm, "end": v(93.24, 67.05) * mm});
            skLineSegment(sketch, "E2934", {"start": v(93.24, 67.05) * mm, "end": v(92.16, 67.8) * mm});
            skLineSegment(sketch, "E2935", {"start": v(92.16, 67.8) * mm, "end": v(90.86, 68.35) * mm});
            skLineSegment(sketch, "E2936", {"start": v(90.86, 68.35) * mm, "end": v(89.57, 68.68) * mm});
            skLineSegment(sketch, "E2937", {"start": v(89.57, 68.68) * mm, "end": v(88.16, 68.78) * mm});
            skLineSegment(sketch, "E2938", {"start": v(88.16, 68.78) * mm, "end": v(86.86, 68.68) * mm});
            skLineSegment(sketch, "E2939", {"start": v(86.86, 68.68) * mm, "end": v(85.45, 68.35) * mm});
            skLineSegment(sketch, "E2940", {"start": v(85.45, 68.35) * mm, "end": v(84.26, 67.8) * mm});
            skLineSegment(sketch, "E2941", {"start": v(84.26, 67.8) * mm, "end": v(83.07, 67.05) * mm});
            skLineSegment(sketch, "E2942", {"start": v(83.07, 67.05) * mm, "end": v(81.99, 66.18) * mm});
            skLineSegment(sketch, "E2943", {"start": v(81.99, 66.18) * mm, "end": v(81.12, 65.1) * mm});
            skLineSegment(sketch, "E2944", {"start": v(81.12, 65.1) * mm, "end": v(80.47, 64.02) * mm});
            skLineSegment(sketch, "E2945", {"start": v(80.47, 64.02) * mm, "end": v(79.94, 62.72) * mm});
            skLineSegment(sketch, "E2946", {"start": v(79.94, 62.72) * mm, "end": v(79.61, 61.42) * mm});
            skLineSegment(sketch, "E2947", {"start": v(79.61, 61.42) * mm, "end": v(79.5, 60.02) * mm});
            skLineSegment(sketch, "E2948", {"start": v(56.88, 58.28) * mm, "end": v(56.88, -47.35) * mm});
            skLineSegment(sketch, "E2949", {"start": v(56.88, -47.35) * mm, "end": v(56.99, -49.96) * mm});
            skLineSegment(sketch, "E2950", {"start": v(56.99, -49.96) * mm, "end": v(57.31, -52.55) * mm});
            skLineSegment(sketch, "E2951", {"start": v(57.31, -52.55) * mm, "end": v(57.86, -55.04) * mm});
            skLineSegment(sketch, "E2952", {"start": v(57.86, -55.04) * mm, "end": v(58.6, -57.53) * mm});
            skLineSegment(sketch, "E2953", {"start": v(58.6, -57.53) * mm, "end": v(59.48, -59.9) * mm});
            skLineSegment(sketch, "E2954", {"start": v(59.48, -59.9) * mm, "end": v(60.67, -62.29) * mm});
            skLineSegment(sketch, "E2955", {"start": v(60.67, -62.29) * mm, "end": v(61.97, -64.46) * mm});
            skLineSegment(sketch, "E2956", {"start": v(61.97, -64.46) * mm, "end": v(63.48, -66.62) * mm});
            skLineSegment(sketch, "E2957", {"start": v(63.48, -66.62) * mm, "end": v(65.21, -68.57) * mm});
            skLineSegment(sketch, "E2958", {"start": v(65.21, -68.57) * mm, "end": v(66.95, -70.4) * mm});
            skLineSegment(sketch, "E2959", {"start": v(66.95, -70.4) * mm, "end": v(69, -72.04) * mm});
            skLineSegment(sketch, "E2960", {"start": v(69, -72.04) * mm, "end": v(71.06, -73.55) * mm});
            skLineSegment(sketch, "E2961", {"start": v(71.06, -73.55) * mm, "end": v(73.33, -74.96) * mm});
            skLineSegment(sketch, "E2962", {"start": v(73.33, -74.96) * mm, "end": v(75.6, -76.04) * mm});
            skLineSegment(sketch, "E2963", {"start": v(75.6, -76.04) * mm, "end": v(77.98, -77.01) * mm});
            skLineSegment(sketch, "E2964", {"start": v(77.98, -77.01) * mm, "end": v(80.47, -77.77) * mm});
            skLineSegment(sketch, "E2965", {"start": v(80.47, -77.77) * mm, "end": v(83.07, -78.3) * mm});
            skLineSegment(sketch, "E2966", {"start": v(83.07, -78.3) * mm, "end": v(85.56, -78.53) * mm});
            skLineSegment(sketch, "E2967", {"start": v(85.56, -78.53) * mm, "end": v(88.16, -78.63) * mm});
            skLineSegment(sketch, "E2968", {"start": v(88.16, -78.63) * mm, "end": v(90.76, -78.53) * mm});
            skLineSegment(sketch, "E2969", {"start": v(90.76, -78.53) * mm, "end": v(93.35, -78.3) * mm});
            skLineSegment(sketch, "E2970", {"start": v(93.35, -78.3) * mm, "end": v(95.85, -77.77) * mm});
            skLineSegment(sketch, "E2971", {"start": v(95.85, -77.77) * mm, "end": v(98.33, -77.01) * mm});
            skLineSegment(sketch, "E2972", {"start": v(98.33, -77.01) * mm, "end": v(100.72, -76.04) * mm});
            skLineSegment(sketch, "E2973", {"start": v(100.72, -76.04) * mm, "end": v(103.1, -74.96) * mm});
            skLineSegment(sketch, "E2974", {"start": v(103.1, -74.96) * mm, "end": v(105.26, -73.55) * mm});
            skLineSegment(sketch, "E2975", {"start": v(105.26, -73.55) * mm, "end": v(107.43, -72.04) * mm});
            skLineSegment(sketch, "E2976", {"start": v(107.43, -72.04) * mm, "end": v(109.37, -70.4) * mm});
            skLineSegment(sketch, "E2977", {"start": v(109.37, -70.4) * mm, "end": v(111.21, -68.57) * mm});
            skLineSegment(sketch, "E2978", {"start": v(111.21, -68.57) * mm, "end": v(112.84, -66.62) * mm});
            skLineSegment(sketch, "E2979", {"start": v(112.84, -66.62) * mm, "end": v(114.35, -64.46) * mm});
            skLineSegment(sketch, "E2980", {"start": v(114.35, -64.46) * mm, "end": v(115.76, -62.29) * mm});
            skLineSegment(sketch, "E2981", {"start": v(115.76, -62.29) * mm, "end": v(116.84, -59.9) * mm});
            skLineSegment(sketch, "E2982", {"start": v(116.84, -59.9) * mm, "end": v(117.82, -57.53) * mm});
            skLineSegment(sketch, "E2983", {"start": v(117.82, -57.53) * mm, "end": v(118.57, -55.04) * mm});
            skLineSegment(sketch, "E2984", {"start": v(118.57, -55.04) * mm, "end": v(119, -52.55) * mm});
            skLineSegment(sketch, "E2985", {"start": v(119, -52.55) * mm, "end": v(119.33, -49.96) * mm});
            skLineSegment(sketch, "E2986", {"start": v(119.33, -49.96) * mm, "end": v(119.44, -47.35) * mm});
            skLineSegment(sketch, "E2987", {"start": v(119.44, -47.35) * mm, "end": v(119.44, 58.28) * mm});
            skLineSegment(sketch, "E2988", {"start": v(119.44, 58.28) * mm, "end": v(119.33, 60.88) * mm});
            skLineSegment(sketch, "E2989", {"start": v(119.33, 60.88) * mm, "end": v(119, 63.37) * mm});
            skLineSegment(sketch, "E2990", {"start": v(119, 63.37) * mm, "end": v(118.57, 65.97) * mm});
            skLineSegment(sketch, "E2991", {"start": v(118.57, 65.97) * mm, "end": v(117.82, 68.46) * mm});
            skLineSegment(sketch, "E2992", {"start": v(117.82, 68.46) * mm, "end": v(116.84, 70.84) * mm});
            skLineSegment(sketch, "E2993", {"start": v(116.84, 70.84) * mm, "end": v(115.76, 73.11) * mm});
            skLineSegment(sketch, "E2994", {"start": v(115.76, 73.11) * mm, "end": v(114.35, 75.38) * mm});
            skLineSegment(sketch, "E2995", {"start": v(114.35, 75.38) * mm, "end": v(112.84, 77.44) * mm});
            skLineSegment(sketch, "E2996", {"start": v(112.84, 77.44) * mm, "end": v(111.21, 79.5) * mm});
            skLineSegment(sketch, "E2997", {"start": v(111.21, 79.5) * mm, "end": v(109.37, 81.23) * mm});
            skLineSegment(sketch, "E2998", {"start": v(109.37, 81.23) * mm, "end": v(107.43, 82.96) * mm});
            skLineSegment(sketch, "E2999", {"start": v(107.43, 82.96) * mm, "end": v(105.26, 84.48) * mm});
            skLineSegment(sketch, "E3000", {"start": v(105.26, 84.48) * mm, "end": v(103.1, 85.78) * mm});
            skLineSegment(sketch, "E3001", {"start": v(103.1, 85.78) * mm, "end": v(100.72, 86.97) * mm});
            skLineSegment(sketch, "E3002", {"start": v(100.72, 86.97) * mm, "end": v(98.33, 87.83) * mm});
            skLineSegment(sketch, "E3003", {"start": v(98.33, 87.83) * mm, "end": v(95.85, 88.6) * mm});
            skLineSegment(sketch, "E3004", {"start": v(95.85, 88.6) * mm, "end": v(93.35, 89.13) * mm});
            skLineSegment(sketch, "E3005", {"start": v(93.35, 89.13) * mm, "end": v(90.76, 89.46) * mm});
            skLineSegment(sketch, "E3006", {"start": v(90.76, 89.46) * mm, "end": v(88.16, 89.57) * mm});
            skLineSegment(sketch, "E3007", {"start": v(88.16, 89.57) * mm, "end": v(85.56, 89.46) * mm});
            skLineSegment(sketch, "E3008", {"start": v(85.56, 89.46) * mm, "end": v(83.07, 89.13) * mm});
            skLineSegment(sketch, "E3009", {"start": v(83.07, 89.13) * mm, "end": v(80.47, 88.6) * mm});
            skLineSegment(sketch, "E3010", {"start": v(80.47, 88.6) * mm, "end": v(77.98, 87.83) * mm});
            skLineSegment(sketch, "E3011", {"start": v(77.98, 87.83) * mm, "end": v(75.6, 86.97) * mm});
            skLineSegment(sketch, "E3012", {"start": v(75.6, 86.97) * mm, "end": v(73.33, 85.78) * mm});
            skLineSegment(sketch, "E3013", {"start": v(73.33, 85.78) * mm, "end": v(71.06, 84.48) * mm});
            skLineSegment(sketch, "E3014", {"start": v(71.06, 84.48) * mm, "end": v(69, 82.96) * mm});
            skLineSegment(sketch, "E3015", {"start": v(69, 82.96) * mm, "end": v(66.95, 81.23) * mm});
            skLineSegment(sketch, "E3016", {"start": v(66.95, 81.23) * mm, "end": v(65.21, 79.5) * mm});
            skLineSegment(sketch, "E3017", {"start": v(65.21, 79.5) * mm, "end": v(63.48, 77.44) * mm});
            skLineSegment(sketch, "E3018", {"start": v(63.48, 77.44) * mm, "end": v(61.97, 75.38) * mm});
            skLineSegment(sketch, "E3019", {"start": v(61.97, 75.38) * mm, "end": v(60.67, 73.11) * mm});
            skLineSegment(sketch, "E3020", {"start": v(60.67, 73.11) * mm, "end": v(59.48, 70.84) * mm});
            skLineSegment(sketch, "E3021", {"start": v(59.48, 70.84) * mm, "end": v(58.6, 68.46) * mm});
            skLineSegment(sketch, "E3022", {"start": v(58.6, 68.46) * mm, "end": v(57.86, 65.97) * mm});
            skLineSegment(sketch, "E3023", {"start": v(57.86, 65.97) * mm, "end": v(57.31, 63.37) * mm});
            skLineSegment(sketch, "E3024", {"start": v(57.31, 63.37) * mm, "end": v(56.99, 60.88) * mm});
            skLineSegment(sketch, "E3025", {"start": v(56.99, 60.88) * mm, "end": v(56.88, 58.28) * mm});
            skLineSegment(sketch, "E3026", {"start": v(-63.26, -328.45) * mm, "end": v(-82.64, -328.45) * mm});
            skLineSegment(sketch, "E3027", {"start": v(-82.64, -328.45) * mm, "end": v(-82.64, -387.54) * mm});
            skLineSegment(sketch, "E3028", {"start": v(-82.64, -387.54) * mm, "end": v(-63.26, -387.54) * mm});
            skLineSegment(sketch, "E3029", {"start": v(-63.26, -387.54) * mm, "end": v(-63.26, -379.32) * mm});
            skLineSegment(sketch, "E3030", {"start": v(-63.26, -379.32) * mm, "end": v(-74.63, -379.32) * mm});
            skLineSegment(sketch, "E3031", {"start": v(-74.63, -379.32) * mm, "end": v(-74.63, -362.33) * mm});
            skLineSegment(sketch, "E3032", {"start": v(-74.63, -362.33) * mm, "end": v(-66.51, -362.33) * mm});
            skLineSegment(sketch, "E3033", {"start": v(-66.51, -362.33) * mm, "end": v(-66.51, -353.45) * mm});
            skLineSegment(sketch, "E3034", {"start": v(-66.51, -353.45) * mm, "end": v(-74.63, -353.45) * mm});
            skLineSegment(sketch, "E3035", {"start": v(-74.63, -353.45) * mm, "end": v(-74.63, -338.08) * mm});
            skLineSegment(sketch, "E3036", {"start": v(-74.63, -338.08) * mm, "end": v(-63.26, -338.08) * mm});
            skLineSegment(sketch, "E3037", {"start": v(-63.26, -338.08) * mm, "end": v(-63.26, -328.45) * mm});
            skLineSegment(sketch, "E3038", {"start": v(48.98, -328.45) * mm, "end": v(29.6, -328.45) * mm});
            skLineSegment(sketch, "E3039", {"start": v(29.6, -328.45) * mm, "end": v(29.6, -387.98) * mm});
            skLineSegment(sketch, "E3040", {"start": v(29.6, -387.98) * mm, "end": v(48.98, -387.98) * mm});
            skLineSegment(sketch, "E3041", {"start": v(48.98, -387.98) * mm, "end": v(48.98, -379.32) * mm});
            skLineSegment(sketch, "E3042", {"start": v(48.98, -379.32) * mm, "end": v(37.72, -379.32) * mm});
            skLineSegment(sketch, "E3043", {"start": v(37.72, -379.32) * mm, "end": v(37.72, -362.33) * mm});
            skLineSegment(sketch, "E3044", {"start": v(37.72, -362.33) * mm, "end": v(45.73, -362.33) * mm});
            skLineSegment(sketch, "E3045", {"start": v(45.73, -362.33) * mm, "end": v(45.73, -353.45) * mm});
            skLineSegment(sketch, "E3046", {"start": v(45.73, -353.45) * mm, "end": v(37.72, -353.45) * mm});
            skLineSegment(sketch, "E3047", {"start": v(37.72, -353.45) * mm, "end": v(37.72, -338.08) * mm});
            skLineSegment(sketch, "E3048", {"start": v(37.72, -338.08) * mm, "end": v(48.98, -338.08) * mm});
            skLineSegment(sketch, "E3049", {"start": v(48.98, -338.08) * mm, "end": v(48.98, -328.45) * mm});
            skLineSegment(sketch, "E3050", {"start": v(113.38, -328.45) * mm, "end": v(123.88, -328.45) * mm});
            skLineSegment(sketch, "E3051", {"start": v(118.68, -343.92) * mm, "end": v(122.04, -367.2) * mm});
            skLineSegment(sketch, "E3052", {"start": v(122.04, -367.2) * mm, "end": v(115.22, -367.2) * mm});
            skLineSegment(sketch, "E3053", {"start": v(115.22, -367.2) * mm, "end": v(118.68, -343.92) * mm});
            skLineSegment(sketch, "E3054", {"start": v(123.88, -328.45) * mm, "end": v(113.38, -328.45) * mm});
            skLineSegment(sketch, "E3055", {"start": v(113.38, -328.45) * mm, "end": v(104.72, -387.98) * mm});
            skLineSegment(sketch, "E3056", {"start": v(104.72, -387.98) * mm, "end": v(112.2, -387.98) * mm});
            skLineSegment(sketch, "E3057", {"start": v(112.2, -387.98) * mm, "end": v(113.92, -376.18) * mm});
            skLineSegment(sketch, "E3058", {"start": v(113.92, -376.18) * mm, "end": v(123.34, -376.18) * mm});
            skLineSegment(sketch, "E3059", {"start": v(123.34, -376.18) * mm, "end": v(125.07, -387.98) * mm});
            skLineSegment(sketch, "E3060", {"start": v(125.07, -387.98) * mm, "end": v(132.54, -387.98) * mm});
            skLineSegment(sketch, "E3061", {"start": v(132.54, -387.98) * mm, "end": v(123.88, -328.45) * mm});
            skLineSegment(sketch, "E3062", {"start": v(184.82, -343.92) * mm, "end": v(188.17, -367.2) * mm});
            skLineSegment(sketch, "E3063", {"start": v(188.17, -367.2) * mm, "end": v(181.35, -367.2) * mm});
            skLineSegment(sketch, "E3064", {"start": v(181.35, -367.2) * mm, "end": v(184.82, -343.92) * mm});
            skLineSegment(sketch, "E3065", {"start": v(190, -328.45) * mm, "end": v(179.51, -328.45) * mm});
            skLineSegment(sketch, "E3066", {"start": v(179.51, -328.45) * mm, "end": v(170.85, -387.98) * mm});
            skLineSegment(sketch, "E3067", {"start": v(170.85, -387.98) * mm, "end": v(178.32, -387.98) * mm});
            skLineSegment(sketch, "E3068", {"start": v(178.32, -387.98) * mm, "end": v(180.05, -376.18) * mm});
            skLineSegment(sketch, "E3069", {"start": v(180.05, -376.18) * mm, "end": v(189.47, -376.18) * mm});
            skLineSegment(sketch, "E3070", {"start": v(189.47, -376.18) * mm, "end": v(191.2, -387.98) * mm});
            skLineSegment(sketch, "E3071", {"start": v(191.2, -387.98) * mm, "end": v(198.67, -387.98) * mm});
            skLineSegment(sketch, "E3072", {"start": v(198.67, -387.98) * mm, "end": v(190, -328.45) * mm});
            skLineSegment(sketch, "E3073", {"start": v(-200.18, -338.84) * mm, "end": v(-200.18, -377.15) * mm});
            skLineSegment(sketch, "E3074", {"start": v(-206.24, -377.15) * mm, "end": v(-206.24, -377.8) * mm});
            skLineSegment(sketch, "E3075", {"start": v(-206.24, -377.8) * mm, "end": v(-206.03, -378.34) * mm});
            skLineSegment(sketch, "E3076", {"start": v(-206.03, -378.34) * mm, "end": v(-205.7, -378.89) * mm});
            skLineSegment(sketch, "E3077", {"start": v(-205.7, -378.89) * mm, "end": v(-205.38, -379.32) * mm});
            skLineSegment(sketch, "E3078", {"start": v(-205.38, -379.32) * mm, "end": v(-204.95, -379.75) * mm});
            skLineSegment(sketch, "E3079", {"start": v(-204.95, -379.75) * mm, "end": v(-204.4, -379.97) * mm});
            skLineSegment(sketch, "E3080", {"start": v(-204.4, -379.97) * mm, "end": v(-203.76, -380.18) * mm});
            skLineSegment(sketch, "E3081", {"start": v(-203.76, -380.18) * mm, "end": v(-202.57, -380.18) * mm});
            skLineSegment(sketch, "E3082", {"start": v(-202.57, -380.18) * mm, "end": v(-201.48, -379.75) * mm});
            skLineSegment(sketch, "E3083", {"start": v(-201.48, -379.75) * mm, "end": v(-200.62, -378.89) * mm});
            skLineSegment(sketch, "E3084", {"start": v(-200.62, -378.89) * mm, "end": v(-200.18, -377.8) * mm});
            skLineSegment(sketch, "E3085", {"start": v(-200.18, -377.8) * mm, "end": v(-200.18, -377.15) * mm});
            skLineSegment(sketch, "E3086", {"start": v(-206.24, -377.15) * mm, "end": v(-206.24, -338.84) * mm});
            skLineSegment(sketch, "E3087", {"start": v(-200.18, -338.84) * mm, "end": v(-200.18, -338.3) * mm});
            skLineSegment(sketch, "E3088", {"start": v(-200.18, -338.3) * mm, "end": v(-200.4, -337.65) * mm});
            skLineSegment(sketch, "E3089", {"start": v(-200.4, -337.65) * mm, "end": v(-200.62, -337.21) * mm});
            skLineSegment(sketch, "E3090", {"start": v(-200.62, -337.21) * mm, "end": v(-201.05, -336.67) * mm});
            skLineSegment(sketch, "E3091", {"start": v(-201.05, -336.67) * mm, "end": v(-201.48, -336.35) * mm});
            skLineSegment(sketch, "E3092", {"start": v(-201.48, -336.35) * mm, "end": v(-202.02, -336.02) * mm});
            skLineSegment(sketch, "E3093", {"start": v(-202.02, -336.02) * mm, "end": v(-202.57, -335.91) * mm});
            skLineSegment(sketch, "E3094", {"start": v(-202.57, -335.91) * mm, "end": v(-203.21, -335.8) * mm});
            skLineSegment(sketch, "E3095", {"start": v(-203.21, -335.8) * mm, "end": v(-203.76, -335.91) * mm});
            skLineSegment(sketch, "E3096", {"start": v(-203.76, -335.91) * mm, "end": v(-204.4, -336.02) * mm});
            skLineSegment(sketch, "E3097", {"start": v(-204.4, -336.02) * mm, "end": v(-204.95, -336.35) * mm});
            skLineSegment(sketch, "E3098", {"start": v(-204.95, -336.35) * mm, "end": v(-205.38, -336.67) * mm});
            skLineSegment(sketch, "E3099", {"start": v(-205.38, -336.67) * mm, "end": v(-205.7, -337.21) * mm});
            skLineSegment(sketch, "E3100", {"start": v(-205.7, -337.21) * mm, "end": v(-206.03, -337.65) * mm});
            skLineSegment(sketch, "E3101", {"start": v(-206.03, -337.65) * mm, "end": v(-206.24, -338.3) * mm});
            skLineSegment(sketch, "E3102", {"start": v(-206.24, -338.3) * mm, "end": v(-206.24, -338.84) * mm});
            skLineSegment(sketch, "E3103", {"start": v(-214.15, -339.49) * mm, "end": v(-214.15, -376.5) * mm});
            skLineSegment(sketch, "E3104", {"start": v(-214.15, -376.5) * mm, "end": v(-214.15, -377.7) * mm});
            skLineSegment(sketch, "E3105", {"start": v(-214.15, -377.7) * mm, "end": v(-213.93, -378.89) * mm});
            skLineSegment(sketch, "E3106", {"start": v(-213.93, -378.89) * mm, "end": v(-213.6, -379.97) * mm});
            skLineSegment(sketch, "E3107", {"start": v(-213.6, -379.97) * mm, "end": v(-213.28, -381.05) * mm});
            skLineSegment(sketch, "E3108", {"start": v(-213.28, -381.05) * mm, "end": v(-212.74, -382.02) * mm});
            skLineSegment(sketch, "E3109", {"start": v(-212.74, -382.02) * mm, "end": v(-212.1, -383) * mm});
            skLineSegment(sketch, "E3110", {"start": v(-212.1, -383) * mm, "end": v(-211.33, -383.86) * mm});
            skLineSegment(sketch, "E3111", {"start": v(-211.33, -383.86) * mm, "end": v(-210.57, -384.73) * mm});
            skLineSegment(sketch, "E3112", {"start": v(-210.57, -384.73) * mm, "end": v(-209.7, -385.49) * mm});
            skLineSegment(sketch, "E3113", {"start": v(-209.7, -385.49) * mm, "end": v(-208.73, -386.03) * mm});
            skLineSegment(sketch, "E3114", {"start": v(-208.73, -386.03) * mm, "end": v(-207.65, -386.57) * mm});
            skLineSegment(sketch, "E3115", {"start": v(-207.65, -386.57) * mm, "end": v(-206.57, -387) * mm});
            skLineSegment(sketch, "E3116", {"start": v(-206.57, -387) * mm, "end": v(-205.49, -387.33) * mm});
            skLineSegment(sketch, "E3117", {"start": v(-205.49, -387.33) * mm, "end": v(-204.4, -387.44) * mm});
            skLineSegment(sketch, "E3118", {"start": v(-204.4, -387.44) * mm, "end": v(-203.21, -387.54) * mm});
            skLineSegment(sketch, "E3119", {"start": v(-203.21, -387.54) * mm, "end": v(-202.02, -387.44) * mm});
            skLineSegment(sketch, "E3120", {"start": v(-202.02, -387.44) * mm, "end": v(-200.94, -387.33) * mm});
            skLineSegment(sketch, "E3121", {"start": v(-200.94, -387.33) * mm, "end": v(-199.86, -387) * mm});
            skLineSegment(sketch, "E3122", {"start": v(-199.86, -387) * mm, "end": v(-198.78, -386.57) * mm});
            skLineSegment(sketch, "E3123", {"start": v(-198.78, -386.57) * mm, "end": v(-197.7, -386.03) * mm});
            skLineSegment(sketch, "E3124", {"start": v(-197.7, -386.03) * mm, "end": v(-196.72, -385.49) * mm});
            skLineSegment(sketch, "E3125", {"start": v(-196.72, -385.49) * mm, "end": v(-195.86, -384.73) * mm});
            skLineSegment(sketch, "E3126", {"start": v(-195.86, -384.73) * mm, "end": v(-195.1, -383.86) * mm});
            skLineSegment(sketch, "E3127", {"start": v(-195.1, -383.86) * mm, "end": v(-194.34, -383) * mm});
            skLineSegment(sketch, "E3128", {"start": v(-194.34, -383) * mm, "end": v(-193.69, -382.02) * mm});
            skLineSegment(sketch, "E3129", {"start": v(-193.69, -382.02) * mm, "end": v(-193.15, -381.05) * mm});
            skLineSegment(sketch, "E3130", {"start": v(-193.15, -381.05) * mm, "end": v(-192.72, -379.97) * mm});
            skLineSegment(sketch, "E3131", {"start": v(-192.72, -379.97) * mm, "end": v(-192.5, -378.89) * mm});
            skLineSegment(sketch, "E3132", {"start": v(-192.5, -378.89) * mm, "end": v(-192.28, -377.7) * mm});
            skLineSegment(sketch, "E3133", {"start": v(-192.28, -377.7) * mm, "end": v(-192.17, -376.5) * mm});
            skLineSegment(sketch, "E3134", {"start": v(-192.17, -376.5) * mm, "end": v(-192.17, -339.49) * mm});
            skLineSegment(sketch, "E3135", {"start": v(-192.17, -339.49) * mm, "end": v(-192.28, -338.3) * mm});
            skLineSegment(sketch, "E3136", {"start": v(-192.28, -338.3) * mm, "end": v(-192.72, -336.13) * mm});
            skLineSegment(sketch, "E3137", {"start": v(-192.72, -336.13) * mm, "end": v(-193.15, -335.05) * mm});
            skLineSegment(sketch, "E3138", {"start": v(-193.15, -335.05) * mm, "end": v(-193.69, -333.97) * mm});
            skLineSegment(sketch, "E3139", {"start": v(-193.69, -333.97) * mm, "end": v(-194.34, -333) * mm});
            skLineSegment(sketch, "E3140", {"start": v(-194.34, -333) * mm, "end": v(-195.1, -332.13) * mm});
            skLineSegment(sketch, "E3141", {"start": v(-195.1, -332.13) * mm, "end": v(-195.86, -331.37) * mm});
            skLineSegment(sketch, "E3142", {"start": v(-195.86, -331.37) * mm, "end": v(-196.72, -330.61) * mm});
            skLineSegment(sketch, "E3143", {"start": v(-196.72, -330.61) * mm, "end": v(-197.7, -329.96) * mm});
            skLineSegment(sketch, "E3144", {"start": v(-197.7, -329.96) * mm, "end": v(-198.78, -329.42) * mm});
            skLineSegment(sketch, "E3145", {"start": v(-198.78, -329.42) * mm, "end": v(-199.86, -328.99) * mm});
            skLineSegment(sketch, "E3146", {"start": v(-199.86, -328.99) * mm, "end": v(-200.94, -328.77) * mm});
            skLineSegment(sketch, "E3147", {"start": v(-200.94, -328.77) * mm, "end": v(-202.02, -328.56) * mm});
            skLineSegment(sketch, "E3148", {"start": v(-202.02, -328.56) * mm, "end": v(-203.21, -328.45) * mm});
            skLineSegment(sketch, "E3149", {"start": v(-203.21, -328.45) * mm, "end": v(-204.4, -328.56) * mm});
            skLineSegment(sketch, "E3150", {"start": v(-204.4, -328.56) * mm, "end": v(-205.49, -328.77) * mm});
            skLineSegment(sketch, "E3151", {"start": v(-205.49, -328.77) * mm, "end": v(-206.57, -328.99) * mm});
            skLineSegment(sketch, "E3152", {"start": v(-206.57, -328.99) * mm, "end": v(-207.65, -329.42) * mm});
            skLineSegment(sketch, "E3153", {"start": v(-207.65, -329.42) * mm, "end": v(-208.73, -329.96) * mm});
            skLineSegment(sketch, "E3154", {"start": v(-208.73, -329.96) * mm, "end": v(-209.7, -330.61) * mm});
            skLineSegment(sketch, "E3155", {"start": v(-209.7, -330.61) * mm, "end": v(-210.57, -331.37) * mm});
            skLineSegment(sketch, "E3156", {"start": v(-210.57, -331.37) * mm, "end": v(-211.33, -332.13) * mm});
            skLineSegment(sketch, "E3157", {"start": v(-211.33, -332.13) * mm, "end": v(-212.1, -333) * mm});
            skLineSegment(sketch, "E3158", {"start": v(-212.1, -333) * mm, "end": v(-212.74, -333.97) * mm});
            skLineSegment(sketch, "E3159", {"start": v(-212.74, -333.97) * mm, "end": v(-213.28, -335.05) * mm});
            skLineSegment(sketch, "E3160", {"start": v(-213.28, -335.05) * mm, "end": v(-213.6, -336.13) * mm});
            skLineSegment(sketch, "E3161", {"start": v(-213.6, -336.13) * mm, "end": v(-213.93, -337.21) * mm});
            skLineSegment(sketch, "E3162", {"start": v(-213.93, -337.21) * mm, "end": v(-214.15, -338.3) * mm});
            skLineSegment(sketch, "E3163", {"start": v(-214.15, -338.3) * mm, "end": v(-214.15, -339.49) * mm});
            skLineSegment(sketch, "E3164", {"start": v(222.16, -338.84) * mm, "end": v(222.16, -377.15) * mm});
            skLineSegment(sketch, "E3165", {"start": v(216.1, -377.15) * mm, "end": v(216.1, -377.8) * mm});
            skLineSegment(sketch, "E3166", {"start": v(216.1, -377.8) * mm, "end": v(216.53, -378.89) * mm});
            skLineSegment(sketch, "E3167", {"start": v(216.53, -378.89) * mm, "end": v(217.4, -379.75) * mm});
            skLineSegment(sketch, "E3168", {"start": v(217.4, -379.75) * mm, "end": v(217.94, -379.97) * mm});
            skLineSegment(sketch, "E3169", {"start": v(217.94, -379.97) * mm, "end": v(218.47, -380.18) * mm});
            skLineSegment(sketch, "E3170", {"start": v(218.47, -380.18) * mm, "end": v(219.67, -380.18) * mm});
            skLineSegment(sketch, "E3171", {"start": v(219.67, -380.18) * mm, "end": v(220.32, -379.97) * mm});
            skLineSegment(sketch, "E3172", {"start": v(220.32, -379.97) * mm, "end": v(220.75, -379.75) * mm});
            skLineSegment(sketch, "E3173", {"start": v(220.75, -379.75) * mm, "end": v(221.29, -379.32) * mm});
            skLineSegment(sketch, "E3174", {"start": v(221.29, -379.32) * mm, "end": v(221.61, -378.89) * mm});
            skLineSegment(sketch, "E3175", {"start": v(221.61, -378.89) * mm, "end": v(221.94, -378.34) * mm});
            skLineSegment(sketch, "E3176", {"start": v(221.94, -378.34) * mm, "end": v(222.05, -377.8) * mm});
            skLineSegment(sketch, "E3177", {"start": v(222.05, -377.8) * mm, "end": v(222.16, -377.15) * mm});
            skLineSegment(sketch, "E3178", {"start": v(216.1, -377.15) * mm, "end": v(216.1, -338.84) * mm});
            skLineSegment(sketch, "E3179", {"start": v(222.16, -338.84) * mm, "end": v(222.05, -338.3) * mm});
            skLineSegment(sketch, "E3180", {"start": v(222.05, -338.3) * mm, "end": v(221.94, -337.65) * mm});
            skLineSegment(sketch, "E3181", {"start": v(221.94, -337.65) * mm, "end": v(221.61, -337.21) * mm});
            skLineSegment(sketch, "E3182", {"start": v(221.61, -337.21) * mm, "end": v(221.29, -336.67) * mm});
            skLineSegment(sketch, "E3183", {"start": v(221.29, -336.67) * mm, "end": v(220.75, -336.35) * mm});
            skLineSegment(sketch, "E3184", {"start": v(220.75, -336.35) * mm, "end": v(220.32, -336.02) * mm});
            skLineSegment(sketch, "E3185", {"start": v(220.32, -336.02) * mm, "end": v(219.67, -335.91) * mm});
            skLineSegment(sketch, "E3186", {"start": v(219.67, -335.91) * mm, "end": v(219.13, -335.8) * mm});
            skLineSegment(sketch, "E3187", {"start": v(219.13, -335.8) * mm, "end": v(218.47, -335.91) * mm});
            skLineSegment(sketch, "E3188", {"start": v(218.47, -335.91) * mm, "end": v(217.94, -336.02) * mm});
            skLineSegment(sketch, "E3189", {"start": v(217.94, -336.02) * mm, "end": v(217.4, -336.35) * mm});
            skLineSegment(sketch, "E3190", {"start": v(217.4, -336.35) * mm, "end": v(216.96, -336.67) * mm});
            skLineSegment(sketch, "E3191", {"start": v(216.96, -336.67) * mm, "end": v(216.53, -337.21) * mm});
            skLineSegment(sketch, "E3192", {"start": v(216.53, -337.21) * mm, "end": v(216.31, -337.65) * mm});
            skLineSegment(sketch, "E3193", {"start": v(216.31, -337.65) * mm, "end": v(216.1, -338.3) * mm});
            skLineSegment(sketch, "E3194", {"start": v(216.1, -338.3) * mm, "end": v(216.1, -338.84) * mm});
            skLineSegment(sketch, "E3195", {"start": v(208.09, -339.49) * mm, "end": v(208.09, -376.5) * mm});
            skLineSegment(sketch, "E3196", {"start": v(208.09, -376.5) * mm, "end": v(208.2, -377.7) * mm});
            skLineSegment(sketch, "E3197", {"start": v(208.2, -377.7) * mm, "end": v(208.41, -378.89) * mm});
            skLineSegment(sketch, "E3198", {"start": v(208.41, -378.89) * mm, "end": v(208.63, -379.97) * mm});
            skLineSegment(sketch, "E3199", {"start": v(208.63, -379.97) * mm, "end": v(209.06, -381.05) * mm});
            skLineSegment(sketch, "E3200", {"start": v(209.06, -381.05) * mm, "end": v(209.6, -382.02) * mm});
            skLineSegment(sketch, "E3201", {"start": v(209.6, -382.02) * mm, "end": v(210.25, -383) * mm});
            skLineSegment(sketch, "E3202", {"start": v(210.25, -383) * mm, "end": v(210.9, -383.86) * mm});
            skLineSegment(sketch, "E3203", {"start": v(210.9, -383.86) * mm, "end": v(211.77, -384.73) * mm});
            skLineSegment(sketch, "E3204", {"start": v(211.77, -384.73) * mm, "end": v(212.63, -385.49) * mm});
            skLineSegment(sketch, "E3205", {"start": v(212.63, -385.49) * mm, "end": v(213.6, -386.03) * mm});
            skLineSegment(sketch, "E3206", {"start": v(213.6, -386.03) * mm, "end": v(214.69, -386.57) * mm});
            skLineSegment(sketch, "E3207", {"start": v(214.69, -386.57) * mm, "end": v(215.66, -387) * mm});
            skLineSegment(sketch, "E3208", {"start": v(215.66, -387) * mm, "end": v(216.85, -387.33) * mm});
            skLineSegment(sketch, "E3209", {"start": v(216.85, -387.33) * mm, "end": v(217.94, -387.44) * mm});
            skLineSegment(sketch, "E3210", {"start": v(217.94, -387.44) * mm, "end": v(219.13, -387.54) * mm});
            skLineSegment(sketch, "E3211", {"start": v(219.13, -387.54) * mm, "end": v(220.2, -387.44) * mm});
            skLineSegment(sketch, "E3212", {"start": v(220.2, -387.44) * mm, "end": v(221.4, -387.33) * mm});
            skLineSegment(sketch, "E3213", {"start": v(221.4, -387.33) * mm, "end": v(222.48, -387) * mm});
            skLineSegment(sketch, "E3214", {"start": v(222.48, -387) * mm, "end": v(223.56, -386.57) * mm});
            skLineSegment(sketch, "E3215", {"start": v(223.56, -386.57) * mm, "end": v(224.64, -386.03) * mm});
            skLineSegment(sketch, "E3216", {"start": v(224.64, -386.03) * mm, "end": v(225.51, -385.49) * mm});
            skLineSegment(sketch, "E3217", {"start": v(225.51, -385.49) * mm, "end": v(226.49, -384.73) * mm});
            skLineSegment(sketch, "E3218", {"start": v(226.49, -384.73) * mm, "end": v(227.25, -383.86) * mm});
            skLineSegment(sketch, "E3219", {"start": v(227.25, -383.86) * mm, "end": v(228, -383) * mm});
            skLineSegment(sketch, "E3220", {"start": v(228, -383) * mm, "end": v(228.65, -382.02) * mm});
            skLineSegment(sketch, "E3221", {"start": v(228.65, -382.02) * mm, "end": v(229.09, -381.05) * mm});
            skLineSegment(sketch, "E3222", {"start": v(229.09, -381.05) * mm, "end": v(229.52, -379.97) * mm});
            skLineSegment(sketch, "E3223", {"start": v(229.52, -379.97) * mm, "end": v(229.84, -378.89) * mm});
            skLineSegment(sketch, "E3224", {"start": v(229.84, -378.89) * mm, "end": v(230.06, -377.7) * mm});
            skLineSegment(sketch, "E3225", {"start": v(230.06, -377.7) * mm, "end": v(230.06, -376.5) * mm});
            skLineSegment(sketch, "E3226", {"start": v(230.06, -376.5) * mm, "end": v(230.06, -339.49) * mm});
            skLineSegment(sketch, "E3227", {"start": v(230.06, -339.49) * mm, "end": v(230.06, -338.3) * mm});
            skLineSegment(sketch, "E3228", {"start": v(230.06, -338.3) * mm, "end": v(229.84, -337.21) * mm});
            skLineSegment(sketch, "E3229", {"start": v(229.84, -337.21) * mm, "end": v(229.52, -336.13) * mm});
            skLineSegment(sketch, "E3230", {"start": v(229.52, -336.13) * mm, "end": v(229.09, -335.05) * mm});
            skLineSegment(sketch, "E3231", {"start": v(229.09, -335.05) * mm, "end": v(228.65, -333.97) * mm});
            skLineSegment(sketch, "E3232", {"start": v(228.65, -333.97) * mm, "end": v(228, -333) * mm});
            skLineSegment(sketch, "E3233", {"start": v(228, -333) * mm, "end": v(227.25, -332.13) * mm});
            skLineSegment(sketch, "E3234", {"start": v(227.25, -332.13) * mm, "end": v(226.49, -331.37) * mm});
            skLineSegment(sketch, "E3235", {"start": v(226.49, -331.37) * mm, "end": v(225.51, -330.61) * mm});
            skLineSegment(sketch, "E3236", {"start": v(225.51, -330.61) * mm, "end": v(224.64, -329.96) * mm});
            skLineSegment(sketch, "E3237", {"start": v(224.64, -329.96) * mm, "end": v(223.56, -329.42) * mm});
            skLineSegment(sketch, "E3238", {"start": v(223.56, -329.42) * mm, "end": v(222.48, -328.99) * mm});
            skLineSegment(sketch, "E3239", {"start": v(222.48, -328.99) * mm, "end": v(221.4, -328.77) * mm});
            skLineSegment(sketch, "E3240", {"start": v(221.4, -328.77) * mm, "end": v(220.2, -328.56) * mm});
            skLineSegment(sketch, "E3241", {"start": v(220.2, -328.56) * mm, "end": v(219.13, -328.45) * mm});
            skLineSegment(sketch, "E3242", {"start": v(219.13, -328.45) * mm, "end": v(217.94, -328.56) * mm});
            skLineSegment(sketch, "E3243", {"start": v(217.94, -328.56) * mm, "end": v(216.85, -328.77) * mm});
            skLineSegment(sketch, "E3244", {"start": v(216.85, -328.77) * mm, "end": v(215.66, -328.99) * mm});
            skLineSegment(sketch, "E3245", {"start": v(215.66, -328.99) * mm, "end": v(214.69, -329.42) * mm});
            skLineSegment(sketch, "E3246", {"start": v(214.69, -329.42) * mm, "end": v(213.6, -329.96) * mm});
            skLineSegment(sketch, "E3247", {"start": v(213.6, -329.96) * mm, "end": v(212.63, -330.61) * mm});
            skLineSegment(sketch, "E3248", {"start": v(212.63, -330.61) * mm, "end": v(211.77, -331.37) * mm});
            skLineSegment(sketch, "E3249", {"start": v(211.77, -331.37) * mm, "end": v(210.9, -332.13) * mm});
            skLineSegment(sketch, "E3250", {"start": v(210.9, -332.13) * mm, "end": v(210.25, -333) * mm});
            skLineSegment(sketch, "E3251", {"start": v(210.25, -333) * mm, "end": v(209.6, -333.97) * mm});
            skLineSegment(sketch, "E3252", {"start": v(209.6, -333.97) * mm, "end": v(209.06, -335.05) * mm});
            skLineSegment(sketch, "E3253", {"start": v(209.06, -335.05) * mm, "end": v(208.63, -336.13) * mm});
            skLineSegment(sketch, "E3254", {"start": v(208.63, -336.13) * mm, "end": v(208.2, -338.3) * mm});
            skLineSegment(sketch, "E3255", {"start": v(208.2, -338.3) * mm, "end": v(208.09, -339.49) * mm});
            skLineSegment(sketch, "E3256", {"start": v(75.39, -376.5) * mm, "end": v(75.5, -377.7) * mm});
            skLineSegment(sketch, "E3257", {"start": v(75.5, -377.7) * mm, "end": v(75.6, -378.89) * mm});
            skLineSegment(sketch, "E3258", {"start": v(75.6, -378.89) * mm, "end": v(75.93, -379.97) * mm});
            skLineSegment(sketch, "E3259", {"start": v(75.93, -379.97) * mm, "end": v(76.36, -381.05) * mm});
            skLineSegment(sketch, "E3260", {"start": v(76.36, -381.05) * mm, "end": v(76.9, -382.02) * mm});
            skLineSegment(sketch, "E3261", {"start": v(76.9, -382.02) * mm, "end": v(77.55, -383) * mm});
            skLineSegment(sketch, "E3262", {"start": v(77.55, -383) * mm, "end": v(78.2, -383.86) * mm});
            skLineSegment(sketch, "E3263", {"start": v(78.2, -383.86) * mm, "end": v(79.07, -384.73) * mm});
            skLineSegment(sketch, "E3264", {"start": v(79.07, -384.73) * mm, "end": v(79.94, -385.49) * mm});
            skLineSegment(sketch, "E3265", {"start": v(79.94, -385.49) * mm, "end": v(80.9, -386.03) * mm});
            skLineSegment(sketch, "E3266", {"start": v(80.9, -386.03) * mm, "end": v(81.88, -386.57) * mm});
            skLineSegment(sketch, "E3267", {"start": v(81.88, -386.57) * mm, "end": v(82.97, -387) * mm});
            skLineSegment(sketch, "E3268", {"start": v(82.97, -387) * mm, "end": v(84.15, -387.33) * mm});
            skLineSegment(sketch, "E3269", {"start": v(84.15, -387.33) * mm, "end": v(85.24, -387.44) * mm});
            skLineSegment(sketch, "E3270", {"start": v(85.24, -387.44) * mm, "end": v(86.43, -387.54) * mm});
            skLineSegment(sketch, "E3271", {"start": v(86.43, -387.54) * mm, "end": v(87.5, -387.44) * mm});
            skLineSegment(sketch, "E3272", {"start": v(87.5, -387.44) * mm, "end": v(88.7, -387.33) * mm});
            skLineSegment(sketch, "E3273", {"start": v(88.7, -387.33) * mm, "end": v(89.78, -387) * mm});
            skLineSegment(sketch, "E3274", {"start": v(89.78, -387) * mm, "end": v(90.86, -386.57) * mm});
            skLineSegment(sketch, "E3275", {"start": v(90.86, -386.57) * mm, "end": v(91.84, -386.03) * mm});
            skLineSegment(sketch, "E3276", {"start": v(91.84, -386.03) * mm, "end": v(92.82, -385.49) * mm});
            skLineSegment(sketch, "E3277", {"start": v(92.82, -385.49) * mm, "end": v(93.79, -384.73) * mm});
            skLineSegment(sketch, "E3278", {"start": v(93.79, -384.73) * mm, "end": v(94.54, -383.86) * mm});
            skLineSegment(sketch, "E3279", {"start": v(94.54, -383.86) * mm, "end": v(95.3, -383) * mm});
            skLineSegment(sketch, "E3280", {"start": v(95.3, -383) * mm, "end": v(95.95, -382.02) * mm});
            skLineSegment(sketch, "E3281", {"start": v(95.95, -382.02) * mm, "end": v(96.38, -381.05) * mm});
            skLineSegment(sketch, "E3282", {"start": v(96.38, -381.05) * mm, "end": v(96.82, -379.97) * mm});
            skLineSegment(sketch, "E3283", {"start": v(96.82, -379.97) * mm, "end": v(97.14, -378.89) * mm});
            skLineSegment(sketch, "E3284", {"start": v(97.14, -378.89) * mm, "end": v(97.36, -377.7) * mm});
            skLineSegment(sketch, "E3285", {"start": v(97.36, -377.7) * mm, "end": v(97.36, -376.5) * mm});
            skLineSegment(sketch, "E3286", {"start": v(97.36, -376.5) * mm, "end": v(97.36, -367.3) * mm});
            skLineSegment(sketch, "E3287", {"start": v(97.36, -367.3) * mm, "end": v(89.46, -367.3) * mm});
            skLineSegment(sketch, "E3288", {"start": v(89.46, -367.3) * mm, "end": v(89.46, -377.15) * mm});
            skLineSegment(sketch, "E3289", {"start": v(83.29, -377.15) * mm, "end": v(83.4, -377.8) * mm});
            skLineSegment(sketch, "E3290", {"start": v(83.4, -377.8) * mm, "end": v(83.62, -378.34) * mm});
            skLineSegment(sketch, "E3291", {"start": v(83.62, -378.34) * mm, "end": v(83.83, -378.89) * mm});
            skLineSegment(sketch, "E3292", {"start": v(83.83, -378.89) * mm, "end": v(84.7, -379.75) * mm});
            skLineSegment(sketch, "E3293", {"start": v(84.7, -379.75) * mm, "end": v(85.24, -379.97) * mm});
            skLineSegment(sketch, "E3294", {"start": v(85.24, -379.97) * mm, "end": v(85.78, -380.18) * mm});
            skLineSegment(sketch, "E3295", {"start": v(85.78, -380.18) * mm, "end": v(86.97, -380.18) * mm});
            skLineSegment(sketch, "E3296", {"start": v(86.97, -380.18) * mm, "end": v(88.05, -379.75) * mm});
            skLineSegment(sketch, "E3297", {"start": v(88.05, -379.75) * mm, "end": v(88.6, -379.32) * mm});
            skLineSegment(sketch, "E3298", {"start": v(88.6, -379.32) * mm, "end": v(88.92, -378.89) * mm});
            skLineSegment(sketch, "E3299", {"start": v(88.92, -378.89) * mm, "end": v(89.24, -378.34) * mm});
            skLineSegment(sketch, "E3300", {"start": v(89.24, -378.34) * mm, "end": v(89.35, -377.8) * mm});
            skLineSegment(sketch, "E3301", {"start": v(89.35, -377.8) * mm, "end": v(89.46, -377.15) * mm});
            skLineSegment(sketch, "E3302", {"start": v(83.29, -377.15) * mm, "end": v(83.29, -338.84) * mm});
            skLineSegment(sketch, "E3303", {"start": v(89.46, -338.84) * mm, "end": v(89.35, -338.3) * mm});
            skLineSegment(sketch, "E3304", {"start": v(89.35, -338.3) * mm, "end": v(89.24, -337.65) * mm});
            skLineSegment(sketch, "E3305", {"start": v(89.24, -337.65) * mm, "end": v(88.92, -337.21) * mm});
            skLineSegment(sketch, "E3306", {"start": v(88.92, -337.21) * mm, "end": v(88.6, -336.67) * mm});
            skLineSegment(sketch, "E3307", {"start": v(88.6, -336.67) * mm, "end": v(88.05, -336.35) * mm});
            skLineSegment(sketch, "E3308", {"start": v(88.05, -336.35) * mm, "end": v(87.5, -336.02) * mm});
            skLineSegment(sketch, "E3309", {"start": v(87.5, -336.02) * mm, "end": v(86.97, -335.91) * mm});
            skLineSegment(sketch, "E3310", {"start": v(86.97, -335.91) * mm, "end": v(86.43, -335.8) * mm});
            skLineSegment(sketch, "E3311", {"start": v(86.43, -335.8) * mm, "end": v(85.78, -335.91) * mm});
            skLineSegment(sketch, "E3312", {"start": v(85.78, -335.91) * mm, "end": v(85.24, -336.02) * mm});
            skLineSegment(sketch, "E3313", {"start": v(85.24, -336.02) * mm, "end": v(84.7, -336.35) * mm});
            skLineSegment(sketch, "E3314", {"start": v(84.7, -336.35) * mm, "end": v(84.26, -336.67) * mm});
            skLineSegment(sketch, "E3315", {"start": v(84.26, -336.67) * mm, "end": v(83.83, -337.21) * mm});
            skLineSegment(sketch, "E3316", {"start": v(83.83, -337.21) * mm, "end": v(83.62, -337.65) * mm});
            skLineSegment(sketch, "E3317", {"start": v(83.62, -337.65) * mm, "end": v(83.4, -338.3) * mm});
            skLineSegment(sketch, "E3318", {"start": v(83.4, -338.3) * mm, "end": v(83.29, -338.84) * mm});
            skLineSegment(sketch, "E3319", {"start": v(89.46, -338.84) * mm, "end": v(89.46, -348.69) * mm});
            skLineSegment(sketch, "E3320", {"start": v(89.46, -348.69) * mm, "end": v(97.36, -348.69) * mm});
            skLineSegment(sketch, "E3321", {"start": v(97.36, -348.69) * mm, "end": v(97.36, -339.49) * mm});
            skLineSegment(sketch, "E3322", {"start": v(97.36, -339.49) * mm, "end": v(97.36, -338.3) * mm});
            skLineSegment(sketch, "E3323", {"start": v(97.36, -338.3) * mm, "end": v(97.14, -337.21) * mm});
            skLineSegment(sketch, "E3324", {"start": v(97.14, -337.21) * mm, "end": v(96.82, -336.13) * mm});
            skLineSegment(sketch, "E3325", {"start": v(96.82, -336.13) * mm, "end": v(96.38, -335.05) * mm});
            skLineSegment(sketch, "E3326", {"start": v(96.38, -335.05) * mm, "end": v(95.95, -333.97) * mm});
            skLineSegment(sketch, "E3327", {"start": v(95.95, -333.97) * mm, "end": v(95.3, -333) * mm});
            skLineSegment(sketch, "E3328", {"start": v(95.3, -333) * mm, "end": v(94.54, -332.13) * mm});
            skLineSegment(sketch, "E3329", {"start": v(94.54, -332.13) * mm, "end": v(93.79, -331.37) * mm});
            skLineSegment(sketch, "E3330", {"start": v(93.79, -331.37) * mm, "end": v(92.82, -330.61) * mm});
            skLineSegment(sketch, "E3331", {"start": v(92.82, -330.61) * mm, "end": v(91.84, -329.96) * mm});
            skLineSegment(sketch, "E3332", {"start": v(91.84, -329.96) * mm, "end": v(90.86, -329.42) * mm});
            skLineSegment(sketch, "E3333", {"start": v(90.86, -329.42) * mm, "end": v(89.78, -328.99) * mm});
            skLineSegment(sketch, "E3334", {"start": v(89.78, -328.99) * mm, "end": v(88.7, -328.77) * mm});
            skLineSegment(sketch, "E3335", {"start": v(88.7, -328.77) * mm, "end": v(87.5, -328.56) * mm});
            skLineSegment(sketch, "E3336", {"start": v(87.5, -328.56) * mm, "end": v(86.43, -328.45) * mm});
            skLineSegment(sketch, "E3337", {"start": v(86.43, -328.45) * mm, "end": v(85.24, -328.56) * mm});
            skLineSegment(sketch, "E3338", {"start": v(85.24, -328.56) * mm, "end": v(84.15, -328.77) * mm});
            skLineSegment(sketch, "E3339", {"start": v(84.15, -328.77) * mm, "end": v(82.97, -328.99) * mm});
            skLineSegment(sketch, "E3340", {"start": v(82.97, -328.99) * mm, "end": v(81.88, -329.42) * mm});
            skLineSegment(sketch, "E3341", {"start": v(81.88, -329.42) * mm, "end": v(80.9, -329.96) * mm});
            skLineSegment(sketch, "E3342", {"start": v(80.9, -329.96) * mm, "end": v(79.94, -330.61) * mm});
            skLineSegment(sketch, "E3343", {"start": v(79.94, -330.61) * mm, "end": v(79.07, -331.37) * mm});
            skLineSegment(sketch, "E3344", {"start": v(79.07, -331.37) * mm, "end": v(78.2, -332.13) * mm});
            skLineSegment(sketch, "E3345", {"start": v(78.2, -332.13) * mm, "end": v(77.55, -333) * mm});
            skLineSegment(sketch, "E3346", {"start": v(77.55, -333) * mm, "end": v(76.9, -333.97) * mm});
            skLineSegment(sketch, "E3347", {"start": v(76.9, -333.97) * mm, "end": v(76.36, -335.05) * mm});
            skLineSegment(sketch, "E3348", {"start": v(76.36, -335.05) * mm, "end": v(75.93, -336.13) * mm});
            skLineSegment(sketch, "E3349", {"start": v(75.93, -336.13) * mm, "end": v(75.6, -337.21) * mm});
            skLineSegment(sketch, "E3350", {"start": v(75.6, -337.21) * mm, "end": v(75.5, -338.3) * mm});
            skLineSegment(sketch, "E3351", {"start": v(75.5, -338.3) * mm, "end": v(75.39, -339.49) * mm});
            skLineSegment(sketch, "E3352", {"start": v(75.39, -339.49) * mm, "end": v(75.39, -376.5) * mm});
            skLineSegment(sketch, "E3353", {"start": v(141.63, -376.5) * mm, "end": v(141.74, -377.7) * mm});
            skLineSegment(sketch, "E3354", {"start": v(141.74, -377.7) * mm, "end": v(141.95, -378.89) * mm});
            skLineSegment(sketch, "E3355", {"start": v(141.95, -378.89) * mm, "end": v(142.17, -379.97) * mm});
            skLineSegment(sketch, "E3356", {"start": v(142.17, -379.97) * mm, "end": v(142.6, -381.05) * mm});
            skLineSegment(sketch, "E3357", {"start": v(142.6, -381.05) * mm, "end": v(143.15, -382.02) * mm});
            skLineSegment(sketch, "E3358", {"start": v(143.15, -382.02) * mm, "end": v(143.8, -383) * mm});
            skLineSegment(sketch, "E3359", {"start": v(143.8, -383) * mm, "end": v(144.44, -383.86) * mm});
            skLineSegment(sketch, "E3360", {"start": v(144.44, -383.86) * mm, "end": v(145.3, -384.73) * mm});
            skLineSegment(sketch, "E3361", {"start": v(145.3, -384.73) * mm, "end": v(146.18, -385.49) * mm});
            skLineSegment(sketch, "E3362", {"start": v(146.18, -385.49) * mm, "end": v(147.15, -386.03) * mm});
            skLineSegment(sketch, "E3363", {"start": v(147.15, -386.03) * mm, "end": v(148.23, -386.57) * mm});
            skLineSegment(sketch, "E3364", {"start": v(148.23, -386.57) * mm, "end": v(149.2, -387) * mm});
            skLineSegment(sketch, "E3365", {"start": v(149.2, -387) * mm, "end": v(150.4, -387.33) * mm});
            skLineSegment(sketch, "E3366", {"start": v(150.4, -387.33) * mm, "end": v(151.48, -387.44) * mm});
            skLineSegment(sketch, "E3367", {"start": v(151.48, -387.44) * mm, "end": v(152.67, -387.54) * mm});
            skLineSegment(sketch, "E3368", {"start": v(152.67, -387.54) * mm, "end": v(153.75, -387.44) * mm});
            skLineSegment(sketch, "E3369", {"start": v(153.75, -387.44) * mm, "end": v(154.94, -387.33) * mm});
            skLineSegment(sketch, "E3370", {"start": v(154.94, -387.33) * mm, "end": v(156.02, -387) * mm});
            skLineSegment(sketch, "E3371", {"start": v(156.02, -387) * mm, "end": v(157.1, -386.57) * mm});
            skLineSegment(sketch, "E3372", {"start": v(157.1, -386.57) * mm, "end": v(158.19, -386.03) * mm});
            skLineSegment(sketch, "E3373", {"start": v(158.19, -386.03) * mm, "end": v(159.06, -385.49) * mm});
            skLineSegment(sketch, "E3374", {"start": v(159.06, -385.49) * mm, "end": v(160.03, -384.73) * mm});
            skLineSegment(sketch, "E3375", {"start": v(160.03, -384.73) * mm, "end": v(160.79, -383.86) * mm});
            skLineSegment(sketch, "E3376", {"start": v(160.79, -383.86) * mm, "end": v(161.54, -383) * mm});
            skLineSegment(sketch, "E3377", {"start": v(161.54, -383) * mm, "end": v(162.2, -382.02) * mm});
            skLineSegment(sketch, "E3378", {"start": v(162.2, -382.02) * mm, "end": v(162.74, -381.05) * mm});
            skLineSegment(sketch, "E3379", {"start": v(162.74, -381.05) * mm, "end": v(163.06, -379.97) * mm});
            skLineSegment(sketch, "E3380", {"start": v(163.06, -379.97) * mm, "end": v(163.38, -378.89) * mm});
            skLineSegment(sketch, "E3381", {"start": v(163.38, -378.89) * mm, "end": v(163.6, -377.7) * mm});
            skLineSegment(sketch, "E3382", {"start": v(163.6, -377.7) * mm, "end": v(163.6, -376.5) * mm});
            skLineSegment(sketch, "E3383", {"start": v(163.6, -376.5) * mm, "end": v(163.6, -367.3) * mm});
            skLineSegment(sketch, "E3384", {"start": v(163.6, -367.3) * mm, "end": v(155.7, -367.3) * mm});
            skLineSegment(sketch, "E3385", {"start": v(155.7, -367.3) * mm, "end": v(155.7, -377.15) * mm});
            skLineSegment(sketch, "E3386", {"start": v(149.64, -377.15) * mm, "end": v(149.64, -377.8) * mm});
            skLineSegment(sketch, "E3387", {"start": v(149.64, -377.8) * mm, "end": v(149.86, -378.34) * mm});
            skLineSegment(sketch, "E3388", {"start": v(149.86, -378.34) * mm, "end": v(150.07, -378.89) * mm});
            skLineSegment(sketch, "E3389", {"start": v(150.07, -378.89) * mm, "end": v(150.94, -379.75) * mm});
            skLineSegment(sketch, "E3390", {"start": v(150.94, -379.75) * mm, "end": v(151.48, -379.97) * mm});
            skLineSegment(sketch, "E3391", {"start": v(151.48, -379.97) * mm, "end": v(152.02, -380.18) * mm});
            skLineSegment(sketch, "E3392", {"start": v(152.02, -380.18) * mm, "end": v(153.21, -380.18) * mm});
            skLineSegment(sketch, "E3393", {"start": v(153.21, -380.18) * mm, "end": v(153.86, -379.97) * mm});
            skLineSegment(sketch, "E3394", {"start": v(153.86, -379.97) * mm, "end": v(154.3, -379.75) * mm});
            skLineSegment(sketch, "E3395", {"start": v(154.3, -379.75) * mm, "end": v(154.83, -379.32) * mm});
            skLineSegment(sketch, "E3396", {"start": v(154.83, -379.32) * mm, "end": v(155.16, -378.89) * mm});
            skLineSegment(sketch, "E3397", {"start": v(155.16, -378.89) * mm, "end": v(155.48, -378.34) * mm});
            skLineSegment(sketch, "E3398", {"start": v(155.48, -378.34) * mm, "end": v(155.6, -377.8) * mm});
            skLineSegment(sketch, "E3399", {"start": v(155.6, -377.8) * mm, "end": v(155.7, -377.15) * mm});
            skLineSegment(sketch, "E3400", {"start": v(149.64, -377.15) * mm, "end": v(149.64, -338.84) * mm});
            skLineSegment(sketch, "E3401", {"start": v(155.7, -338.84) * mm, "end": v(155.6, -338.3) * mm});
            skLineSegment(sketch, "E3402", {"start": v(155.6, -338.3) * mm, "end": v(155.48, -337.65) * mm});
            skLineSegment(sketch, "E3403", {"start": v(155.48, -337.65) * mm, "end": v(155.16, -337.21) * mm});
            skLineSegment(sketch, "E3404", {"start": v(155.16, -337.21) * mm, "end": v(154.83, -336.67) * mm});
            skLineSegment(sketch, "E3405", {"start": v(154.83, -336.67) * mm, "end": v(154.3, -336.35) * mm});
            skLineSegment(sketch, "E3406", {"start": v(154.3, -336.35) * mm, "end": v(153.86, -336.02) * mm});
            skLineSegment(sketch, "E3407", {"start": v(153.86, -336.02) * mm, "end": v(153.21, -335.91) * mm});
            skLineSegment(sketch, "E3408", {"start": v(153.21, -335.91) * mm, "end": v(152.67, -335.8) * mm});
            skLineSegment(sketch, "E3409", {"start": v(152.67, -335.8) * mm, "end": v(152.02, -335.91) * mm});
            skLineSegment(sketch, "E3410", {"start": v(152.02, -335.91) * mm, "end": v(151.48, -336.02) * mm});
            skLineSegment(sketch, "E3411", {"start": v(151.48, -336.02) * mm, "end": v(150.94, -336.35) * mm});
            skLineSegment(sketch, "E3412", {"start": v(150.94, -336.35) * mm, "end": v(150.5, -336.67) * mm});
            skLineSegment(sketch, "E3413", {"start": v(150.5, -336.67) * mm, "end": v(150.07, -337.21) * mm});
            skLineSegment(sketch, "E3414", {"start": v(150.07, -337.21) * mm, "end": v(149.86, -337.65) * mm});
            skLineSegment(sketch, "E3415", {"start": v(149.86, -337.65) * mm, "end": v(149.64, -338.3) * mm});
            skLineSegment(sketch, "E3416", {"start": v(149.64, -338.3) * mm, "end": v(149.64, -338.84) * mm});
            skLineSegment(sketch, "E3417", {"start": v(155.7, -338.84) * mm, "end": v(155.7, -348.69) * mm});
            skLineSegment(sketch, "E3418", {"start": v(155.7, -348.69) * mm, "end": v(163.6, -348.69) * mm});
            skLineSegment(sketch, "E3419", {"start": v(163.6, -348.69) * mm, "end": v(163.6, -339.49) * mm});
            skLineSegment(sketch, "E3420", {"start": v(163.6, -339.49) * mm, "end": v(163.6, -338.3) * mm});
            skLineSegment(sketch, "E3421", {"start": v(163.6, -338.3) * mm, "end": v(163.38, -337.21) * mm});
            skLineSegment(sketch, "E3422", {"start": v(163.38, -337.21) * mm, "end": v(163.06, -336.13) * mm});
            skLineSegment(sketch, "E3423", {"start": v(163.06, -336.13) * mm, "end": v(162.74, -335.05) * mm});
            skLineSegment(sketch, "E3424", {"start": v(162.74, -335.05) * mm, "end": v(162.2, -333.97) * mm});
            skLineSegment(sketch, "E3425", {"start": v(162.2, -333.97) * mm, "end": v(161.54, -333) * mm});
            skLineSegment(sketch, "E3426", {"start": v(161.54, -333) * mm, "end": v(160.79, -332.13) * mm});
            skLineSegment(sketch, "E3427", {"start": v(160.79, -332.13) * mm, "end": v(160.03, -331.37) * mm});
            skLineSegment(sketch, "E3428", {"start": v(160.03, -331.37) * mm, "end": v(159.06, -330.61) * mm});
            skLineSegment(sketch, "E3429", {"start": v(159.06, -330.61) * mm, "end": v(158.19, -329.96) * mm});
            skLineSegment(sketch, "E3430", {"start": v(158.19, -329.96) * mm, "end": v(157.1, -329.42) * mm});
            skLineSegment(sketch, "E3431", {"start": v(157.1, -329.42) * mm, "end": v(156.02, -328.99) * mm});
            skLineSegment(sketch, "E3432", {"start": v(156.02, -328.99) * mm, "end": v(154.94, -328.77) * mm});
            skLineSegment(sketch, "E3433", {"start": v(154.94, -328.77) * mm, "end": v(153.75, -328.56) * mm});
            skLineSegment(sketch, "E3434", {"start": v(153.75, -328.56) * mm, "end": v(152.67, -328.45) * mm});
            skLineSegment(sketch, "E3435", {"start": v(152.67, -328.45) * mm, "end": v(151.48, -328.56) * mm});
            skLineSegment(sketch, "E3436", {"start": v(151.48, -328.56) * mm, "end": v(150.4, -328.77) * mm});
            skLineSegment(sketch, "E3437", {"start": v(150.4, -328.77) * mm, "end": v(149.2, -328.99) * mm});
            skLineSegment(sketch, "E3438", {"start": v(149.2, -328.99) * mm, "end": v(148.23, -329.42) * mm});
            skLineSegment(sketch, "E3439", {"start": v(148.23, -329.42) * mm, "end": v(147.15, -329.96) * mm});
            skLineSegment(sketch, "E3440", {"start": v(147.15, -329.96) * mm, "end": v(146.18, -330.61) * mm});
            skLineSegment(sketch, "E3441", {"start": v(146.18, -330.61) * mm, "end": v(145.3, -331.37) * mm});
            skLineSegment(sketch, "E3442", {"start": v(145.3, -331.37) * mm, "end": v(144.44, -332.13) * mm});
            skLineSegment(sketch, "E3443", {"start": v(144.44, -332.13) * mm, "end": v(143.8, -333) * mm});
            skLineSegment(sketch, "E3444", {"start": v(143.8, -333) * mm, "end": v(143.15, -333.97) * mm});
            skLineSegment(sketch, "E3445", {"start": v(143.15, -333.97) * mm, "end": v(142.6, -335.05) * mm});
            skLineSegment(sketch, "E3446", {"start": v(142.6, -335.05) * mm, "end": v(142.17, -336.13) * mm});
            skLineSegment(sketch, "E3447", {"start": v(142.17, -336.13) * mm, "end": v(141.74, -338.3) * mm});
            skLineSegment(sketch, "E3448", {"start": v(141.74, -338.3) * mm, "end": v(141.63, -339.49) * mm});
            skLineSegment(sketch, "E3449", {"start": v(141.63, -339.49) * mm, "end": v(141.63, -376.5) * mm});
            skSolve(sketch);
        }
        {
            var Q0;
            Q0=qSketchRegion(id+"F0",true);
            extrude(context, id + "F1", {"entities" : qUnion([Q0]), "depth" : 25.4 * mm, "offsetDistance" : 25.4 * mm});
        }
        {
            var Q0;
            Q0=qCreatedBy(makeId("Top.planeOp"),FACE);
            var sketch = newSketch(context, id + "F2", { "sketchPlane" : qUnion([Q0])});
            skLineSegment(sketch, "E3450.bottom", {"start": v(-279.84, 429.7) * mm, "end": v(282.03, 429.7) * mm});
            skLineSegment(sketch, "E3450.top", {"start": v(-279.84, -426.73) * mm, "end": v(282.03, -426.73) * mm});
            skLineSegment(sketch, "E3450.left", {"start": v(-279.84, 429.7) * mm, "end": v(-279.84, -426.73) * mm});
            skLineSegment(sketch, "E3450.right", {"start": v(282.03, 429.7) * mm, "end": v(282.03, -426.73) * mm});
            skSolve(sketch);
        }
        {
            var Q0;
            Q0=makeQuery(id+"F2.imprint","IMPRINT",FACE,{"disambiguationData":[TD([[makeQuery(id+"F2.imprint","IMPRINT",EDGE,{"derivedFrom":sQuery(id+"F2.wireOp",EDGE,"E3450.bottom")}),-1.0]])]});
            extrude(context, id + "F3", {"entities" : qUnion([Q0]), "endBound" : BoundingType.SYMMETRIC, "depth" : 25.4 * mm, "offsetDistance" : 25.4 * mm});
        }
        {
            var Q0;
            Q0=makeQuery(id+"F1.opExtrude","CAP_FACE",FACE,{"disambiguationData":[OSD([sQuery(id+"F0.wireOp",EDGE,"E2611"),sQuery(id+"F0.wireOp",EDGE,"E2612"),sQuery(id+"F0.wireOp",EDGE,"E2613"),sQuery(id+"F0.wireOp",EDGE,"E2614"),sQuery(id+"F0.wireOp",EDGE,"E2615"),sQuery(id+"F0.wireOp",EDGE,"E2616"),sQuery(id+"F0.wireOp",EDGE,"E2617")])],"isStart":false});
            var sketch = newSketch(context, id + "F4", { "sketchPlane" : qUnion([Q0])});
            skLineSegment(sketch, "E3451.bottom", {"start": v(-305.4, 102.57) * mm, "end": v(352.13, 102.57) * mm});
            skLineSegment(sketch, "E3451.top", {"start": v(-305.4, 484.5) * mm, "end": v(352.13, 484.5) * mm});
            skLineSegment(sketch, "E3451.left", {"start": v(-305.4, 102.57) * mm, "end": v(-305.4, 484.5) * mm});
            skLineSegment(sketch, "E3451.right", {"start": v(352.13, 102.57) * mm, "end": v(352.13, 484.5) * mm});
            skLineSegment(sketch, "E3452.bottom", {"start": v(-321.06, -250.24) * mm, "end": v(346.36, -250.24) * mm});
            skLineSegment(sketch, "E3452.top", {"start": v(-321.06, -452.2) * mm, "end": v(346.36, -452.2) * mm});
            skLineSegment(sketch, "E3452.left", {"start": v(-321.06, -250.24) * mm, "end": v(-321.06, -452.2) * mm});
            skLineSegment(sketch, "E3452.right", {"start": v(346.36, -250.24) * mm, "end": v(346.36, -452.2) * mm});
            skSolve(sketch);
        }
        {
            var Q0;
            Q0=makeQuery(id+"F4.imprint","IMPRINT",FACE,{"disambiguationData":[TD([[makeQuery(id+"F4.imprint","IMPRINT",EDGE,{"derivedFrom":sQuery(id+"F4.wireOp",EDGE,"E3451.bottom")}),1.0]])]});
            var Q1;
            Q1=makeQuery(id+"F4.imprint","IMPRINT",FACE,{"disambiguationData":[TD([[makeQuery(id+"F4.imprint","IMPRINT",EDGE,{"derivedFrom":sQuery(id+"F4.wireOp",EDGE,"E3452.bottom")}),-1.0]])]});
            extrude(context, id + "F5", {"entities" : qUnion([Q0, Q1]), "operationType" : NewBodyOperationType.REMOVE, "oppositeDirection" : true, "depth" : 109.22 * mm, "offsetDistance" : 25.4 * mm});
        }
    });
